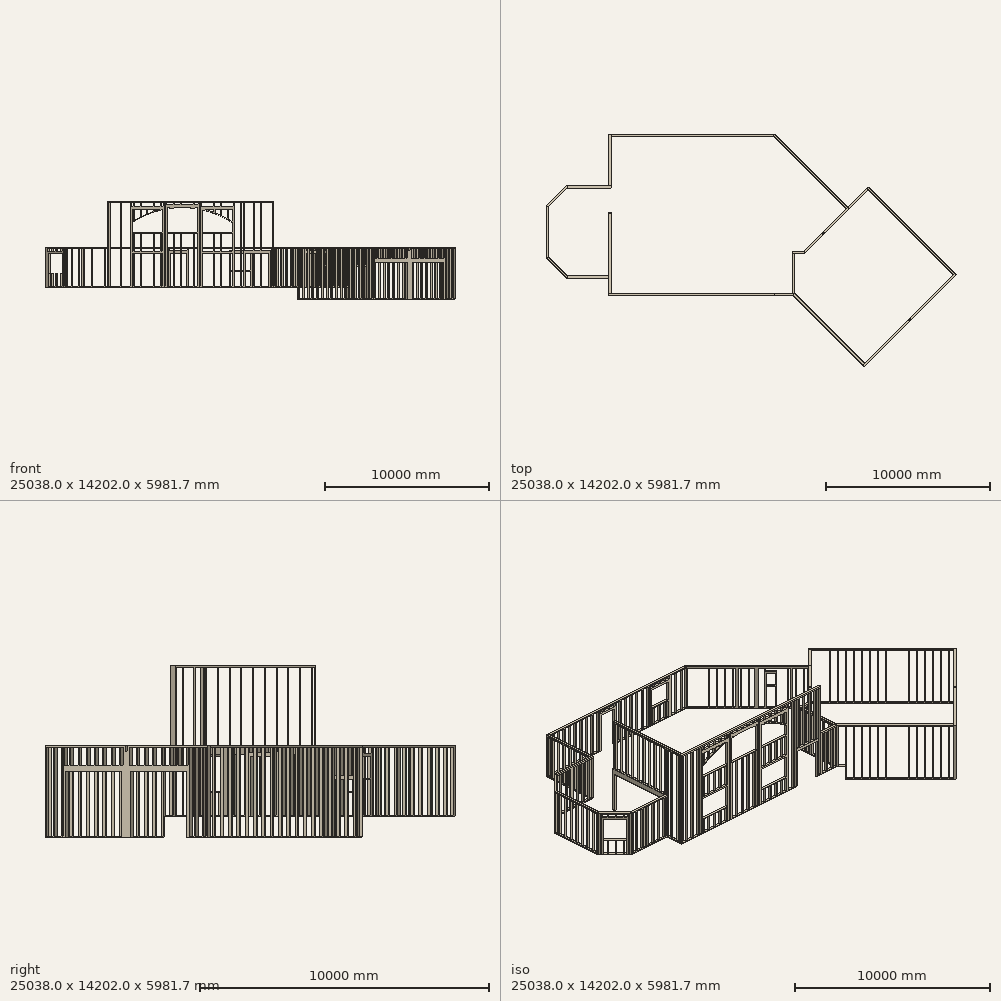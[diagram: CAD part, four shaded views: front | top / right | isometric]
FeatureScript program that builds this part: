
annotation { "Feature Type Name" : "Feature", "Feature Type Description" : "" }
export const myFeature = defineFeature(function(context is Context, id is Id, definition is map)
    precondition{}
    {
        {
            var Q0;
            Q0=qCreatedBy(makeId("Top.planeOp"),FACE);
            var sketch = newSketch(context, id + "F0", { "sketchPlane" : qUnion([Q0]) });
            skLineSegment(sketch, "E0", {"start": v(-0.03, 0) * mm, "end": v(-11277.6, 0) * mm});
            skLineSegment(sketch, "E1", {"start": v(-11277.6, 0) * mm, "end": v(-11277.6, 139.7) * mm});
            skLineSegment(sketch, "E2", {"start": v(-11277.63, 1066.8) * mm, "end": v(-13810.5, 1066.8) * mm});
            skLineSegment(sketch, "E3", {"start": v(-13868.4, 1066.8) * mm, "end": v(-15087.6, 2286) * mm});
            skLineSegment(sketch, "E4", {"start": v(-15087.6, 2286) * mm, "end": v(-15087.6, 2343.87) * mm});
            skLineSegment(sketch, "E5", {"start": v(-15087.6, 5486.4) * mm, "end": v(-13868.4, 6705.6) * mm});
            skLineSegment(sketch, "E6", {"start": v(-13868.4, 6705.6) * mm, "end": v(-13810.53, 6705.6) * mm});
            skLineSegment(sketch, "E7", {"start": v(-11277.6, 6705.63) * mm, "end": v(-11277.6, 9855.2) * mm});
            skLineSegment(sketch, "E8", {"start": v(-11277.6, 9855.2) * mm, "end": v(-11137.9, 9855.2) * mm});
            skLineSegment(sketch, "E9", {"start": v(-1162.31, 9855.2) * mm, "end": v(3305.03, 5387.86) * mm});
            skLineSegment(sketch, "E10", {"start": v(3305.06, 5387.86) * mm, "end": v(4463.48, 6546.28) * mm});
            skLineSegment(sketch, "E11", {"start": v(9950.43, 1256.93) * mm, "end": v(4346.75, -4346.75) * mm});
            skLineSegment(sketch, "E12", {"start": v(4346.75, -4346.75) * mm, "end": v(4247.97, -4247.97) * mm});
            skLineSegment(sketch, "E13.0", {"start": v(-11137.9, 6565.9) * mm, "end": v(-11137.9, 6705.6) * mm});
            skLineSegment(sketch, "E13.1", {"start": v(-13810.5, 6565.9) * mm, "end": v(-11137.9, 6565.9) * mm});
            skLineSegment(sketch, "E13.2", {"start": v(-14947.9, 5428.53) * mm, "end": v(-13810.53, 6565.9) * mm});
            skLineSegment(sketch, "E13.3", {"start": v(9752.87, 1256.93) * mm, "end": v(4346.75, -4149.19) * mm});
            skLineSegment(sketch, "E13.4", {"start": v(4463.5, 6546.3) * mm, "end": v(9752.85, 1256.94) * mm});
            skLineSegment(sketch, "E13.5", {"start": v(3305.04, 5190.28) * mm, "end": v(3403.83, 5289.06) * mm});
            skLineSegment(sketch, "E13.6", {"start": v(-1220.18, 9715.5) * mm, "end": v(3206.24, 5289.08) * mm});
            skLineSegment(sketch, "E13.7", {"start": v(4346.74, -4149.17) * mm, "end": v(57.87, 139.7) * mm});
            skLineSegment(sketch, "E13.8", {"start": v(-81.83, 139.7) * mm, "end": v(-11137.9, 139.7) * mm});
            skLineSegment(sketch, "E13.9", {"start": v(-11137.9, 139.73) * mm, "end": v(-11137.9, 5080) * mm});
            skLineSegment(sketch, "E13.10", {"start": v(-11137.87, 9715.5) * mm, "end": v(-1220.2, 9715.5) * mm});
            skLineSegment(sketch, "E13.12", {"start": v(-13810.53, 1206.5) * mm, "end": v(-14947.9, 2343.87) * mm});
            skLineSegment(sketch, "E13.13", {"start": v(-14947.9, 2343.9) * mm, "end": v(-14947.9, 5428.5) * mm});
            skLineSegment(sketch, "E14", {"start": v(57.87, 139.73) * mm, "end": v(57.87, 2578.07) * mm});
            skLineSegment(sketch, "E15", {"start": v(57.87, 2578.1) * mm, "end": v(692.87, 2578.1) * mm});
            skLineSegment(sketch, "E16", {"start": v(692.87, 2578.1) * mm, "end": v(733.78, 2619.02) * mm});
            skLineSegment(sketch, "E17.0", {"start": v(635.02, 2717.82) * mm, "end": v(3206.26, 5289.06) * mm});
            skLineSegment(sketch, "E17.1", {"start": v(-81.83, 2717.8) * mm, "end": v(635, 2717.8) * mm});
            skLineSegment(sketch, "E17.2", {"start": v(-81.83, 139.73) * mm, "end": v(-81.83, 2578.07) * mm});
            skLineSegment(sketch, "E18", {"start": v(-11137.9, 139.7) * mm, "end": v(-11277.6, 139.7) * mm});
            skLineSegment(sketch, "E19", {"start": v(-11137.9, 139.73) * mm, "end": v(-11277.6, 139.73) * mm});
            skLineSegment(sketch, "E20.trimOffspring", {"start": v(-11277.6, 139.73) * mm, "end": v(-11277.6, 5080) * mm});
            skLineSegment(sketch, "E21", {"start": v(-13810.53, 1206.5) * mm, "end": v(-13810.53, 1066.8) * mm});
            skLineSegment(sketch, "E22", {"start": v(-13810.5, 1206.5) * mm, "end": v(-13810.5, 1066.8) * mm});
            skLineSegment(sketch, "E23.trimOffspring", {"start": v(-13810.53, 1066.8) * mm, "end": v(-13868.4, 1066.8) * mm});
            skLineSegment(sketch, "E24", {"start": v(-14947.9, 2343.87) * mm, "end": v(-15087.6, 2343.87) * mm});
            skLineSegment(sketch, "E25", {"start": v(-15087.6, 2343.9) * mm, "end": v(-14947.9, 2343.9) * mm});
            skLineSegment(sketch, "E26.trimOffspring", {"start": v(-15087.6, 2343.9) * mm, "end": v(-15087.6, 5428.5) * mm});
            skLineSegment(sketch, "E27", {"start": v(-14947.9, 5428.53) * mm, "end": v(-15087.6, 5428.53) * mm});
            skLineSegment(sketch, "E28", {"start": v(-14947.9, 5428.5) * mm, "end": v(-15087.6, 5428.5) * mm});
            skLineSegment(sketch, "E29.trimOffspring", {"start": v(-15087.6, 5428.53) * mm, "end": v(-15087.6, 5486.4) * mm});
            skLineSegment(sketch, "E30", {"start": v(-13810.53, 6565.9) * mm, "end": v(-13810.53, 6705.6) * mm});
            skLineSegment(sketch, "E31", {"start": v(-13810.5, 6705.6) * mm, "end": v(-13810.5, 6565.9) * mm});
            skLineSegment(sketch, "E32.trimOffspring", {"start": v(-13810.5, 6705.6) * mm, "end": v(-11277.6, 6705.6) * mm});
            skLineSegment(sketch, "E33", {"start": v(-11277.6, 6705.6) * mm, "end": v(-11137.9, 6705.6) * mm});
            skLineSegment(sketch, "E34", {"start": v(-11277.6, 6705.63) * mm, "end": v(-11137.9, 6705.63) * mm});
            skLineSegment(sketch, "E35.trimOffspring", {"start": v(-11137.9, 6705.63) * mm, "end": v(-11137.9, 9715.5) * mm});
            skLineSegment(sketch, "E36", {"start": v(-11137.9, 9715.5) * mm, "end": v(-11137.9, 9855.2) * mm});
            skLineSegment(sketch, "E37", {"start": v(-11137.87, 9855.2) * mm, "end": v(-11137.87, 9715.5) * mm});
            skLineSegment(sketch, "E38.trimOffspring", {"start": v(-11137.87, 9855.2) * mm, "end": v(-1220.2, 9855.2) * mm});
            skLineSegment(sketch, "E39", {"start": v(-1220.18, 9715.5) * mm, "end": v(-1220.18, 9855.2) * mm});
            skLineSegment(sketch, "E40", {"start": v(-1220.2, 9855.2) * mm, "end": v(-1220.2, 9715.5) * mm});
            skLineSegment(sketch, "E41.trimOffspring", {"start": v(-1220.18, 9855.2) * mm, "end": v(-1162.31, 9855.2) * mm});
            skLineSegment(sketch, "E42", {"start": v(3206.26, 5289.06) * mm, "end": v(3305.04, 5387.84) * mm});
            skLineSegment(sketch, "E43", {"start": v(3305.04, 5387.84) * mm, "end": v(3403.83, 5289.06) * mm});
            skLineSegment(sketch, "E44", {"start": v(3206.24, 5289.08) * mm, "end": v(3305.03, 5387.86) * mm});
            skLineSegment(sketch, "E45", {"start": v(3305.06, 5387.86) * mm, "end": v(3403.84, 5289.08) * mm});
            skLineSegment(sketch, "E46.trimOffspring", {"start": v(3403.84, 5289.08) * mm, "end": v(4562.26, 6447.5) * mm});
            skLineSegment(sketch, "E47", {"start": v(635, 2717.8) * mm, "end": v(733.78, 2619.02) * mm});
            skLineSegment(sketch, "E48", {"start": v(635.02, 2717.82) * mm, "end": v(733.8, 2619.04) * mm});
            skLineSegment(sketch, "E49.trimOffspring", {"start": v(733.8, 2619.04) * mm, "end": v(3305.04, 5190.28) * mm});
            skLineSegment(sketch, "E50", {"start": v(57.87, 2578.1) * mm, "end": v(-81.83, 2578.1) * mm});
            skLineSegment(sketch, "E51", {"start": v(-81.83, 2578.07) * mm, "end": v(57.87, 2578.07) * mm});
            skLineSegment(sketch, "E52.trimOffspring", {"start": v(-81.83, 2578.1) * mm, "end": v(-81.83, 2717.8) * mm});
            skLineSegment(sketch, "E53", {"start": v(-81.83, 139.7) * mm, "end": v(-0.03, 139.7) * mm});
            skLineSegment(sketch, "E54", {"start": v(-81.83, 139.73) * mm, "end": v(57.87, 139.73) * mm});
            skLineSegment(sketch, "E55", {"start": v(0, 0) * mm, "end": v(0, 139.7) * mm});
            skLineSegment(sketch, "E56", {"start": v(-0.03, 0) * mm, "end": v(-0.03, 139.7) * mm});
            skLineSegment(sketch, "E57.trimOffspring", {"start": v(0, 139.7) * mm, "end": v(57.87, 139.7) * mm});
            skLineSegment(sketch, "E58", {"start": v(4346.75, -4149.19) * mm, "end": v(4247.97, -4247.97) * mm});
            skLineSegment(sketch, "E59", {"start": v(4346.74, -4149.17) * mm, "end": v(4247.95, -4247.95) * mm});
            skLineSegment(sketch, "E60.trimOffspring", {"start": v(4247.95, -4247.95) * mm, "end": v(0, 0) * mm});
            skLineSegment(sketch, "E61", {"start": v(9752.87, 1256.93) * mm, "end": v(9851.65, 1355.7) * mm});
            skLineSegment(sketch, "E62", {"start": v(9752.85, 1256.94) * mm, "end": v(9851.63, 1355.73) * mm});
            skLineSegment(sketch, "E63.trimOffspring", {"start": v(9851.65, 1355.7) * mm, "end": v(9950.43, 1256.93) * mm});
            skLineSegment(sketch, "E64.trimOffspring", {"start": v(4562.28, 6645.08) * mm, "end": v(9851.63, 1355.73) * mm});
            skLineSegment(sketch, "E65", {"start": v(4562.26, 6447.5) * mm, "end": v(4463.48, 6546.28) * mm});
            skLineSegment(sketch, "E66.trimOffspring", {"start": v(4463.5, 6546.3) * mm, "end": v(4562.28, 6645.08) * mm});
            skLineSegment(sketch, "E67", {"start": v(-12712.7, 6565.9) * mm, "end": v(-12712.7, 5080) * mm, "construction": true});
            skLineSegment(sketch, "E68", {"start": v(-12712.7, 5080) * mm, "end": v(-11277.6, 5080) * mm, "construction": true});
            skLineSegment(sketch, "E69", {"start": v(-12801.6, 6565.9) * mm, "end": v(-12801.6, 4991.1) * mm, "construction": true});
            skLineSegment(sketch, "E70", {"start": v(-12801.6, 4991.1) * mm, "end": v(-11277.6, 4991.1) * mm, "construction": true});
            skLineSegment(sketch, "E71", {"start": v(-11277.63, 1206.5) * mm, "end": v(-11277.63, 1066.8) * mm});
            skLineSegment(sketch, "E72.trimOffspring", {"start": v(-11277.63, 1206.5) * mm, "end": v(-13810.5, 1206.5) * mm});
            skLineSegment(sketch, "E73", {"start": v(-11137.9, 5080) * mm, "end": v(-10632.52, 5080) * mm, "construction": true});
            skLineSegment(sketch, "E74", {"start": v(-11137.9, 5000.63) * mm, "end": v(-10601.72, 5000.63) * mm, "construction": true});
            skLineSegment(sketch, "E75", {"start": v(-11277.6, 5080) * mm, "end": v(-11137.9, 5080) * mm});
            skSolve(sketch);
        }
        {
            var Q0;
            Q0 = qSketchRegion(id + "F0", true);
            extrude(context, id + "F1", {"entities" : qUnion([Q0]), "depth" : 38.1 * mm});
        }
        {
            var Q0;
            Q0=makeQuery(id+"F1.opExtrude","CAP_FACE",FACE,{"disambiguationData":[OSD([sQuery(id+"F0.wireOp",EDGE,"E0"),sQuery(id+"F0.wireOp",EDGE,"E1"),sQuery(id+"F0.wireOp",EDGE,"E13.8"),sQuery(id+"F0.wireOp",EDGE,"E18"),sQuery(id+"F0.wireOp",EDGE,"E53"),sQuery(id+"F0.wireOp",EDGE,"E56")])],"isStart":false});
            var sketch = newSketch(context, id + "F2", { "sketchPlane" : qUnion([Q0]) });
            skLineSegment(sketch, "E76.bottom", {"start": v(-11277.6, 0) * mm, "end": v(-11239.5, 0) * mm});
            skLineSegment(sketch, "E76.top", {"start": v(-11277.6, 139.7) * mm, "end": v(-11239.5, 139.7) * mm});
            skLineSegment(sketch, "E76.left", {"start": v(-11277.6, 0) * mm, "end": v(-11277.6, 139.7) * mm});
            skLineSegment(sketch, "E76.right", {"start": v(-11239.5, 0) * mm, "end": v(-11239.5, 139.7) * mm});
            skLineSegment(sketch, "E77.bottom", {"start": v(-11099.8, 139.7) * mm, "end": v(-11239.47, 139.7) * mm});
            skLineSegment(sketch, "E77.top", {"start": v(-11099.8, 101.6) * mm, "end": v(-11239.47, 101.6) * mm});
            skLineSegment(sketch, "E77.left", {"start": v(-11099.8, 139.7) * mm, "end": v(-11099.8, 101.6) * mm});
            skLineSegment(sketch, "E77.right", {"start": v(-11239.47, 139.7) * mm, "end": v(-11239.47, 101.6) * mm});
            skLineSegment(sketch, "E78.bottom", {"start": v(-0.03, 0) * mm, "end": v(-38.1, 0) * mm});
            skLineSegment(sketch, "E78.top", {"start": v(-0.03, 139.7) * mm, "end": v(-38.1, 139.7) * mm});
            skLineSegment(sketch, "E78.left", {"start": v(-0.03, 0) * mm, "end": v(-0.03, 139.7) * mm});
            skLineSegment(sketch, "E78.right", {"start": v(-38.1, 0) * mm, "end": v(-38.1, 139.7) * mm});
            skLineSegment(sketch, "E79.bottom", {"start": v(-127, 139.7) * mm, "end": v(-38.13, 139.7) * mm});
            skLineSegment(sketch, "E79.top", {"start": v(-127, 101.6) * mm, "end": v(-38.13, 101.6) * mm});
            skLineSegment(sketch, "E79.left", {"start": v(-127, 139.7) * mm, "end": v(-127, 101.6) * mm});
            skLineSegment(sketch, "E79.right", {"start": v(-38.13, 139.7) * mm, "end": v(-38.13, 101.6) * mm});
            skLineSegment(sketch, "E80.bottom", {"start": v(-10902.95, 139.7) * mm, "end": v(-10864.85, 139.7) * mm});
            skLineSegment(sketch, "E80.top", {"start": v(-10902.95, 0) * mm, "end": v(-10864.85, 0) * mm});
            skLineSegment(sketch, "E80.left", {"start": v(-10902.95, 139.7) * mm, "end": v(-10902.95, 0) * mm});
            skLineSegment(sketch, "E80.right", {"start": v(-10864.85, 139.7) * mm, "end": v(-10864.85, 0) * mm});
            skLineSegment(sketch, "E81.1.0.0", {"start": v(-10496.55, 139.7) * mm, "end": v(-10496.55, 0) * mm});
            skLineSegment(sketch, "E81.1.0.1", {"start": v(-10458.45, 139.7) * mm, "end": v(-10458.45, 0) * mm});
            skLineSegment(sketch, "E81.1.0.2", {"start": v(-10496.55, 139.7) * mm, "end": v(-10458.45, 139.7) * mm});
            skLineSegment(sketch, "E81.1.0.3", {"start": v(-10496.55, 0) * mm, "end": v(-10458.45, 0) * mm});
            skLineSegment(sketch, "E81.2.0.0", {"start": v(-10090.15, 139.7) * mm, "end": v(-10090.15, 0) * mm});
            skLineSegment(sketch, "E81.2.0.1", {"start": v(-10052.05, 139.7) * mm, "end": v(-10052.05, 0) * mm});
            skLineSegment(sketch, "E81.2.0.2", {"start": v(-10090.15, 139.7) * mm, "end": v(-10052.05, 139.7) * mm});
            skLineSegment(sketch, "E81.2.0.3", {"start": v(-10090.15, 0) * mm, "end": v(-10052.05, 0) * mm});
            skLineSegment(sketch, "E81.3.0.0", {"start": v(-9683.75, 139.7) * mm, "end": v(-9683.75, 0) * mm});
            skLineSegment(sketch, "E81.3.0.1", {"start": v(-9645.65, 139.7) * mm, "end": v(-9645.65, 0) * mm});
            skLineSegment(sketch, "E81.3.0.2", {"start": v(-9683.75, 139.7) * mm, "end": v(-9645.65, 139.7) * mm});
            skLineSegment(sketch, "E81.3.0.3", {"start": v(-9683.75, 0) * mm, "end": v(-9645.65, 0) * mm});
            skLineSegment(sketch, "E81.4.0.0", {"start": v(-9277.35, 139.7) * mm, "end": v(-9277.35, 0) * mm});
            skLineSegment(sketch, "E81.4.0.1", {"start": v(-9239.25, 139.7) * mm, "end": v(-9239.25, 0) * mm});
            skLineSegment(sketch, "E81.4.0.2", {"start": v(-9277.35, 139.7) * mm, "end": v(-9239.25, 139.7) * mm});
            skLineSegment(sketch, "E81.4.0.3", {"start": v(-9277.35, 0) * mm, "end": v(-9239.25, 0) * mm});
            skLineSegment(sketch, "E81.5.0.0", {"start": v(-8870.95, 139.7) * mm, "end": v(-8870.95, 0) * mm});
            skLineSegment(sketch, "E81.5.0.1", {"start": v(-8832.85, 139.7) * mm, "end": v(-8832.85, 0) * mm});
            skLineSegment(sketch, "E81.5.0.2", {"start": v(-8870.95, 139.7) * mm, "end": v(-8832.85, 139.7) * mm});
            skLineSegment(sketch, "E81.5.0.3", {"start": v(-8870.95, 0) * mm, "end": v(-8832.85, 0) * mm});
            skLineSegment(sketch, "E81.6.0.0", {"start": v(-8464.55, 139.7) * mm, "end": v(-8464.55, 0) * mm});
            skLineSegment(sketch, "E81.6.0.1", {"start": v(-8426.45, 139.7) * mm, "end": v(-8426.45, 0) * mm});
            skLineSegment(sketch, "E81.6.0.2", {"start": v(-8464.55, 139.7) * mm, "end": v(-8426.45, 139.7) * mm});
            skLineSegment(sketch, "E81.6.0.3", {"start": v(-8464.55, 0) * mm, "end": v(-8426.45, 0) * mm});
            skLineSegment(sketch, "E81.7.0.0", {"start": v(-8058.15, 139.7) * mm, "end": v(-8058.15, 0) * mm});
            skLineSegment(sketch, "E81.7.0.1", {"start": v(-8020.05, 139.7) * mm, "end": v(-8020.05, 0) * mm});
            skLineSegment(sketch, "E81.7.0.2", {"start": v(-8058.15, 139.7) * mm, "end": v(-8020.05, 139.7) * mm});
            skLineSegment(sketch, "E81.7.0.3", {"start": v(-8058.15, 0) * mm, "end": v(-8020.05, 0) * mm});
            skLineSegment(sketch, "E81.8.0.0", {"start": v(-7651.75, 139.7) * mm, "end": v(-7651.75, 0) * mm});
            skLineSegment(sketch, "E81.8.0.1", {"start": v(-7613.65, 139.7) * mm, "end": v(-7613.65, 0) * mm});
            skLineSegment(sketch, "E81.8.0.2", {"start": v(-7651.75, 139.7) * mm, "end": v(-7613.65, 139.7) * mm});
            skLineSegment(sketch, "E81.8.0.3", {"start": v(-7651.75, 0) * mm, "end": v(-7613.65, 0) * mm});
            skLineSegment(sketch, "E81.9.0.0", {"start": v(-7245.35, 139.7) * mm, "end": v(-7245.35, 0) * mm});
            skLineSegment(sketch, "E81.9.0.1", {"start": v(-7207.25, 139.7) * mm, "end": v(-7207.25, 0) * mm});
            skLineSegment(sketch, "E81.9.0.2", {"start": v(-7245.35, 139.7) * mm, "end": v(-7207.25, 139.7) * mm});
            skLineSegment(sketch, "E81.9.0.3", {"start": v(-7245.35, 0) * mm, "end": v(-7207.25, 0) * mm});
            skLineSegment(sketch, "E81.10.0.0", {"start": v(-6838.95, 139.7) * mm, "end": v(-6838.95, 0) * mm});
            skLineSegment(sketch, "E81.10.0.1", {"start": v(-6800.85, 139.7) * mm, "end": v(-6800.85, 0) * mm});
            skLineSegment(sketch, "E81.10.0.2", {"start": v(-6838.95, 139.7) * mm, "end": v(-6800.85, 139.7) * mm});
            skLineSegment(sketch, "E81.10.0.3", {"start": v(-6838.95, 0) * mm, "end": v(-6800.85, 0) * mm});
            skLineSegment(sketch, "E81.11.0.0", {"start": v(-6432.55, 139.7) * mm, "end": v(-6432.55, 0) * mm});
            skLineSegment(sketch, "E81.11.0.1", {"start": v(-6394.45, 139.7) * mm, "end": v(-6394.45, 0) * mm});
            skLineSegment(sketch, "E81.11.0.2", {"start": v(-6432.55, 139.7) * mm, "end": v(-6394.45, 139.7) * mm});
            skLineSegment(sketch, "E81.11.0.3", {"start": v(-6432.55, 0) * mm, "end": v(-6394.45, 0) * mm});
            skLineSegment(sketch, "E81.12.0.0", {"start": v(-6026.15, 139.7) * mm, "end": v(-6026.15, 0) * mm});
            skLineSegment(sketch, "E81.12.0.1", {"start": v(-5988.05, 139.7) * mm, "end": v(-5988.05, 0) * mm});
            skLineSegment(sketch, "E81.12.0.2", {"start": v(-6026.15, 139.7) * mm, "end": v(-5988.05, 139.7) * mm});
            skLineSegment(sketch, "E81.12.0.3", {"start": v(-6026.15, 0) * mm, "end": v(-5988.05, 0) * mm});
            skLineSegment(sketch, "E81.13.0.0", {"start": v(-5619.75, 139.7) * mm, "end": v(-5619.75, 0) * mm});
            skLineSegment(sketch, "E81.13.0.1", {"start": v(-5581.65, 139.7) * mm, "end": v(-5581.65, 0) * mm});
            skLineSegment(sketch, "E81.13.0.2", {"start": v(-5619.75, 139.7) * mm, "end": v(-5581.65, 139.7) * mm});
            skLineSegment(sketch, "E81.13.0.3", {"start": v(-5619.75, 0) * mm, "end": v(-5581.65, 0) * mm});
            skLineSegment(sketch, "E81.14.0.0", {"start": v(-5213.35, 139.7) * mm, "end": v(-5213.35, 0) * mm});
            skLineSegment(sketch, "E81.14.0.1", {"start": v(-5175.25, 139.7) * mm, "end": v(-5175.25, 0) * mm});
            skLineSegment(sketch, "E81.14.0.2", {"start": v(-5213.35, 139.7) * mm, "end": v(-5175.25, 139.7) * mm});
            skLineSegment(sketch, "E81.14.0.3", {"start": v(-5213.35, 0) * mm, "end": v(-5175.25, 0) * mm});
            skLineSegment(sketch, "E81.15.0.0", {"start": v(-4806.95, 139.7) * mm, "end": v(-4806.95, 0) * mm});
            skLineSegment(sketch, "E81.15.0.1", {"start": v(-4768.85, 139.7) * mm, "end": v(-4768.85, 0) * mm});
            skLineSegment(sketch, "E81.15.0.2", {"start": v(-4806.95, 139.7) * mm, "end": v(-4768.85, 139.7) * mm});
            skLineSegment(sketch, "E81.15.0.3", {"start": v(-4806.95, 0) * mm, "end": v(-4768.85, 0) * mm});
            skLineSegment(sketch, "E81.16.0.0", {"start": v(-4400.55, 139.7) * mm, "end": v(-4400.55, 0) * mm});
            skLineSegment(sketch, "E81.16.0.1", {"start": v(-4362.45, 139.7) * mm, "end": v(-4362.45, 0) * mm});
            skLineSegment(sketch, "E81.16.0.2", {"start": v(-4400.55, 139.7) * mm, "end": v(-4362.45, 139.7) * mm});
            skLineSegment(sketch, "E81.16.0.3", {"start": v(-4400.55, 0) * mm, "end": v(-4362.45, 0) * mm});
            skLineSegment(sketch, "E81.17.0.0", {"start": v(-3994.15, 139.7) * mm, "end": v(-3994.15, 0) * mm});
            skLineSegment(sketch, "E81.17.0.1", {"start": v(-3956.05, 139.7) * mm, "end": v(-3956.05, 0) * mm});
            skLineSegment(sketch, "E81.17.0.2", {"start": v(-3994.15, 139.7) * mm, "end": v(-3956.05, 139.7) * mm});
            skLineSegment(sketch, "E81.17.0.3", {"start": v(-3994.15, 0) * mm, "end": v(-3956.05, 0) * mm});
            skLineSegment(sketch, "E81.18.0.0", {"start": v(-3587.75, 139.7) * mm, "end": v(-3587.75, 0) * mm});
            skLineSegment(sketch, "E81.18.0.1", {"start": v(-3549.65, 139.7) * mm, "end": v(-3549.65, 0) * mm});
            skLineSegment(sketch, "E81.18.0.2", {"start": v(-3587.75, 139.7) * mm, "end": v(-3549.65, 139.7) * mm});
            skLineSegment(sketch, "E81.18.0.3", {"start": v(-3587.75, 0) * mm, "end": v(-3549.65, 0) * mm});
            skLineSegment(sketch, "E81.19.0.0", {"start": v(-3181.35, 139.7) * mm, "end": v(-3181.35, 0) * mm});
            skLineSegment(sketch, "E81.19.0.1", {"start": v(-3143.25, 139.7) * mm, "end": v(-3143.25, 0) * mm});
            skLineSegment(sketch, "E81.19.0.2", {"start": v(-3181.35, 139.7) * mm, "end": v(-3143.25, 139.7) * mm});
            skLineSegment(sketch, "E81.19.0.3", {"start": v(-3181.35, 0) * mm, "end": v(-3143.25, 0) * mm});
            skLineSegment(sketch, "E81.20.0.0", {"start": v(-2774.95, 139.7) * mm, "end": v(-2774.95, 0) * mm});
            skLineSegment(sketch, "E81.20.0.1", {"start": v(-2736.85, 139.7) * mm, "end": v(-2736.85, 0) * mm});
            skLineSegment(sketch, "E81.20.0.2", {"start": v(-2774.95, 139.7) * mm, "end": v(-2736.85, 139.7) * mm});
            skLineSegment(sketch, "E81.20.0.3", {"start": v(-2774.95, 0) * mm, "end": v(-2736.85, 0) * mm});
            skLineSegment(sketch, "E81.21.0.0", {"start": v(-2368.55, 139.7) * mm, "end": v(-2368.55, 0) * mm});
            skLineSegment(sketch, "E81.21.0.1", {"start": v(-2330.45, 139.7) * mm, "end": v(-2330.45, 0) * mm});
            skLineSegment(sketch, "E81.21.0.2", {"start": v(-2368.55, 139.7) * mm, "end": v(-2330.45, 139.7) * mm});
            skLineSegment(sketch, "E81.21.0.3", {"start": v(-2368.55, 0) * mm, "end": v(-2330.45, 0) * mm});
            skLineSegment(sketch, "E81.22.0.0", {"start": v(-1962.15, 139.7) * mm, "end": v(-1962.15, 0) * mm});
            skLineSegment(sketch, "E81.22.0.1", {"start": v(-1924.05, 139.7) * mm, "end": v(-1924.05, 0) * mm});
            skLineSegment(sketch, "E81.22.0.2", {"start": v(-1962.15, 139.7) * mm, "end": v(-1924.05, 139.7) * mm});
            skLineSegment(sketch, "E81.22.0.3", {"start": v(-1962.15, 0) * mm, "end": v(-1924.05, 0) * mm});
            skLineSegment(sketch, "E81.23.0.0", {"start": v(-1555.75, 139.7) * mm, "end": v(-1555.75, 0) * mm});
            skLineSegment(sketch, "E81.23.0.1", {"start": v(-1517.65, 139.7) * mm, "end": v(-1517.65, 0) * mm});
            skLineSegment(sketch, "E81.23.0.2", {"start": v(-1555.75, 139.7) * mm, "end": v(-1517.65, 139.7) * mm});
            skLineSegment(sketch, "E81.23.0.3", {"start": v(-1555.75, 0) * mm, "end": v(-1517.65, 0) * mm});
            skLineSegment(sketch, "E81.25.0.0", {"start": v(-742.95, 139.7) * mm, "end": v(-742.95, 0) * mm});
            skLineSegment(sketch, "E81.25.0.1", {"start": v(-704.85, 139.7) * mm, "end": v(-704.85, 0) * mm});
            skLineSegment(sketch, "E81.25.0.2", {"start": v(-742.95, 139.7) * mm, "end": v(-704.85, 139.7) * mm});
            skLineSegment(sketch, "E81.25.0.3", {"start": v(-742.95, 0) * mm, "end": v(-704.85, 0) * mm});
            skLineSegment(sketch, "E81.26.0.0", {"start": v(-336.55, 139.7) * mm, "end": v(-336.55, 0) * mm});
            skLineSegment(sketch, "E81.26.0.1", {"start": v(-298.45, 139.7) * mm, "end": v(-298.45, 0) * mm});
            skLineSegment(sketch, "E81.26.0.2", {"start": v(-336.55, 139.7) * mm, "end": v(-298.45, 139.7) * mm});
            skLineSegment(sketch, "E81.26.0.3", {"start": v(-336.55, 0) * mm, "end": v(-298.45, 0) * mm});
            skLineSegment(sketch, "E81.direction1", {"start": v(-10902.95, 0) * mm, "end": v(-10496.55, 0) * mm, "construction": true});
            skLineSegment(sketch, "E82", {"start": v(-1085.13, 1434.54) * mm, "end": v(-1085.13, 139.7) * mm, "construction": true});
            skLineSegment(sketch, "E83", {"start": v(-1174.03, 1434.54) * mm, "end": v(-1174.03, 139.7) * mm, "construction": true});
            skLineSegment(sketch, "E84.bottom", {"start": v(-1174.03, 139.7) * mm, "end": v(-1135.93, 139.7) * mm});
            skLineSegment(sketch, "E84.top", {"start": v(-1174.03, 0) * mm, "end": v(-1135.93, 0) * mm});
            skLineSegment(sketch, "E84.left", {"start": v(-1174.03, 139.7) * mm, "end": v(-1174.03, 0) * mm});
            skLineSegment(sketch, "E84.right", {"start": v(-1135.93, 139.7) * mm, "end": v(-1135.93, 0) * mm});
            skLineSegment(sketch, "E85.bottom", {"start": v(-1094.66, 139.7) * mm, "end": v(-1132.76, 139.7) * mm});
            skLineSegment(sketch, "E85.top", {"start": v(-1094.66, 0) * mm, "end": v(-1132.76, 0) * mm});
            skLineSegment(sketch, "E85.left", {"start": v(-1094.66, 139.7) * mm, "end": v(-1094.66, 0) * mm});
            skLineSegment(sketch, "E85.right", {"start": v(-1132.76, 139.7) * mm, "end": v(-1132.76, 0) * mm});
            skLineSegment(sketch, "E86.bottom", {"start": v(-1174.06, 139.7) * mm, "end": v(-1212.13, 139.7) * mm});
            skLineSegment(sketch, "E86.top", {"start": v(-1174.06, 0) * mm, "end": v(-1212.13, 0) * mm});
            skLineSegment(sketch, "E86.left", {"start": v(-1174.06, 139.7) * mm, "end": v(-1174.06, 0) * mm});
            skLineSegment(sketch, "E86.right", {"start": v(-1212.13, 139.7) * mm, "end": v(-1212.13, 0) * mm});
            skLineSegment(sketch, "E87.bottom", {"start": v(-1094.63, 139.7) * mm, "end": v(-1056.56, 139.7) * mm});
            skLineSegment(sketch, "E87.top", {"start": v(-1094.63, 0) * mm, "end": v(-1056.56, 0) * mm});
            skLineSegment(sketch, "E87.left", {"start": v(-1094.63, 139.7) * mm, "end": v(-1094.63, 0) * mm});
            skLineSegment(sketch, "E87.right", {"start": v(-1056.56, 139.7) * mm, "end": v(-1056.56, 0) * mm});
            skLineSegment(sketch, "E88.bottom", {"start": v(-1453.43, 139.7) * mm, "end": v(-1415.33, 139.7) * mm});
            skLineSegment(sketch, "E88.top", {"start": v(-1453.43, 0) * mm, "end": v(-1415.33, 0) * mm});
            skLineSegment(sketch, "E88.left", {"start": v(-1453.43, 139.7) * mm, "end": v(-1453.43, 0) * mm});
            skLineSegment(sketch, "E88.right", {"start": v(-1415.33, 139.7) * mm, "end": v(-1415.33, 0) * mm});
            skLineSegment(sketch, "E89.bottom", {"start": v(-2898.06, 139.7) * mm, "end": v(-2859.96, 139.7) * mm});
            skLineSegment(sketch, "E89.top", {"start": v(-2898.06, 0) * mm, "end": v(-2859.96, 0) * mm});
            skLineSegment(sketch, "E89.left", {"start": v(-2898.06, 139.7) * mm, "end": v(-2898.06, 0) * mm});
            skLineSegment(sketch, "E89.right", {"start": v(-2859.96, 139.7) * mm, "end": v(-2859.96, 0) * mm});
            skLineSegment(sketch, "E90.bottom", {"start": v(-2936.16, 139.7) * mm, "end": v(-2898.08, 139.7) * mm});
            skLineSegment(sketch, "E90.top", {"start": v(-2936.16, 0) * mm, "end": v(-2898.08, 0) * mm});
            skLineSegment(sketch, "E90.left", {"start": v(-2936.16, 139.7) * mm, "end": v(-2936.16, 0) * mm});
            skLineSegment(sketch, "E90.right", {"start": v(-2898.08, 139.7) * mm, "end": v(-2898.08, 0) * mm});
            skLineSegment(sketch, "E91.bottom", {"start": v(-1415.3, 139.7) * mm, "end": v(-1377.23, 139.7) * mm});
            skLineSegment(sketch, "E91.top", {"start": v(-1415.3, 0) * mm, "end": v(-1377.23, 0) * mm});
            skLineSegment(sketch, "E91.left", {"start": v(-1415.3, 139.7) * mm, "end": v(-1415.3, 0) * mm});
            skLineSegment(sketch, "E91.right", {"start": v(-1377.23, 139.7) * mm, "end": v(-1377.23, 0) * mm});
            skLineSegment(sketch, "E92.bottom", {"start": v(-1377.2, 139.7) * mm, "end": v(-1339.13, 139.7) * mm});
            skLineSegment(sketch, "E92.top", {"start": v(-1377.2, 0) * mm, "end": v(-1339.13, 0) * mm});
            skLineSegment(sketch, "E92.left", {"start": v(-1377.2, 139.7) * mm, "end": v(-1377.2, 0) * mm});
            skLineSegment(sketch, "E92.right", {"start": v(-1339.13, 139.7) * mm, "end": v(-1339.13, 0) * mm});
            skLineSegment(sketch, "E93.bottom", {"start": v(-2974.26, 139.7) * mm, "end": v(-2936.18, 139.7) * mm});
            skLineSegment(sketch, "E93.top", {"start": v(-2974.26, 0) * mm, "end": v(-2936.18, 0) * mm});
            skLineSegment(sketch, "E93.left", {"start": v(-2974.26, 139.7) * mm, "end": v(-2974.26, 0) * mm});
            skLineSegment(sketch, "E93.right", {"start": v(-2936.18, 139.7) * mm, "end": v(-2936.18, 0) * mm});
            skLineSegment(sketch, "E94.bottom", {"start": v(-9804.4, 139.7) * mm, "end": v(-9766.3, 139.7) * mm});
            skLineSegment(sketch, "E94.top", {"start": v(-9804.4, 0) * mm, "end": v(-9766.3, 0) * mm});
            skLineSegment(sketch, "E94.left", {"start": v(-9804.4, 139.7) * mm, "end": v(-9804.4, 0) * mm});
            skLineSegment(sketch, "E94.right", {"start": v(-9766.3, 139.7) * mm, "end": v(-9766.3, 0) * mm});
            skLineSegment(sketch, "E95.bottom", {"start": v(-9842.5, 139.7) * mm, "end": v(-9804.43, 139.7) * mm});
            skLineSegment(sketch, "E95.top", {"start": v(-9842.5, 0) * mm, "end": v(-9804.43, 0) * mm});
            skLineSegment(sketch, "E95.left", {"start": v(-9842.5, 139.7) * mm, "end": v(-9842.5, 0) * mm});
            skLineSegment(sketch, "E95.right", {"start": v(-9804.43, 139.7) * mm, "end": v(-9804.43, 0) * mm});
            skLineSegment(sketch, "E96.bottom", {"start": v(-7937.5, 139.7) * mm, "end": v(-7899.4, 139.7) * mm});
            skLineSegment(sketch, "E96.top", {"start": v(-7937.5, 0) * mm, "end": v(-7899.4, 0) * mm});
            skLineSegment(sketch, "E96.left", {"start": v(-7937.5, 139.7) * mm, "end": v(-7937.5, 0) * mm});
            skLineSegment(sketch, "E96.right", {"start": v(-7899.4, 139.7) * mm, "end": v(-7899.4, 0) * mm});
            skLineSegment(sketch, "E97.bottom", {"start": v(-7899.37, 139.7) * mm, "end": v(-7861.3, 139.7) * mm});
            skLineSegment(sketch, "E97.top", {"start": v(-7899.37, 0) * mm, "end": v(-7861.3, 0) * mm});
            skLineSegment(sketch, "E97.left", {"start": v(-7899.37, 139.7) * mm, "end": v(-7899.37, 0) * mm});
            skLineSegment(sketch, "E97.right", {"start": v(-7861.3, 139.7) * mm, "end": v(-7861.3, 0) * mm});
            skLineSegment(sketch, "E98.bottom", {"start": v(-5543.52, 139.7) * mm, "end": v(-5505.42, 139.7) * mm});
            skLineSegment(sketch, "E98.top", {"start": v(-5543.52, 0) * mm, "end": v(-5505.42, 0) * mm});
            skLineSegment(sketch, "E98.left", {"start": v(-5543.52, 139.7) * mm, "end": v(-5543.52, 0) * mm});
            skLineSegment(sketch, "E98.right", {"start": v(-5505.42, 139.7) * mm, "end": v(-5505.42, 0) * mm});
            skLineSegment(sketch, "E99.bottom", {"start": v(-5543.55, 139.7) * mm, "end": v(-5581.62, 139.7) * mm});
            skLineSegment(sketch, "E99.top", {"start": v(-5543.55, 0) * mm, "end": v(-5581.62, 0) * mm});
            skLineSegment(sketch, "E99.left", {"start": v(-5543.55, 139.7) * mm, "end": v(-5543.55, 0) * mm});
            skLineSegment(sketch, "E99.right", {"start": v(-5581.62, 139.7) * mm, "end": v(-5581.62, 0) * mm});
            skLineSegment(sketch, "E100.bottom", {"start": v(-3676.62, 139.7) * mm, "end": v(-3638.52, 139.7) * mm});
            skLineSegment(sketch, "E100.top", {"start": v(-3676.62, 0) * mm, "end": v(-3638.52, 0) * mm});
            skLineSegment(sketch, "E100.left", {"start": v(-3676.62, 139.7) * mm, "end": v(-3676.62, 0) * mm});
            skLineSegment(sketch, "E100.right", {"start": v(-3638.52, 139.7) * mm, "end": v(-3638.52, 0) * mm});
            skLineSegment(sketch, "E101.bottom", {"start": v(-3638.5, 139.7) * mm, "end": v(-3600.42, 139.7) * mm});
            skLineSegment(sketch, "E101.top", {"start": v(-3638.5, 0) * mm, "end": v(-3600.42, 0) * mm});
            skLineSegment(sketch, "E101.left", {"start": v(-3638.5, 139.7) * mm, "end": v(-3638.5, 0) * mm});
            skLineSegment(sketch, "E101.right", {"start": v(-3600.42, 139.7) * mm, "end": v(-3600.42, 0) * mm});
            skLineSegment(sketch, "E102.bottom", {"start": v(-7727.95, 139.7) * mm, "end": v(-7689.88, 139.7) * mm});
            skLineSegment(sketch, "E102.top", {"start": v(-7727.95, 0) * mm, "end": v(-7689.88, 0) * mm});
            skLineSegment(sketch, "E102.left", {"start": v(-7727.95, 139.7) * mm, "end": v(-7727.95, 0) * mm});
            skLineSegment(sketch, "E102.right", {"start": v(-7689.88, 139.7) * mm, "end": v(-7689.88, 0) * mm});
            skLineSegment(sketch, "E103.bottom", {"start": v(-7689.85, 139.7) * mm, "end": v(-7651.78, 139.7) * mm});
            skLineSegment(sketch, "E103.top", {"start": v(-7689.85, 0) * mm, "end": v(-7651.78, 0) * mm});
            skLineSegment(sketch, "E103.left", {"start": v(-7689.85, 139.7) * mm, "end": v(-7689.85, 0) * mm});
            skLineSegment(sketch, "E103.right", {"start": v(-7651.78, 139.7) * mm, "end": v(-7651.78, 0) * mm});
            skLineSegment(sketch, "E104.bottom", {"start": v(-5714.97, 139.7) * mm, "end": v(-5753.05, 139.7) * mm});
            skLineSegment(sketch, "E104.top", {"start": v(-5714.97, 0) * mm, "end": v(-5753.05, 0) * mm});
            skLineSegment(sketch, "E104.left", {"start": v(-5714.97, 139.7) * mm, "end": v(-5714.97, 0) * mm});
            skLineSegment(sketch, "E104.right", {"start": v(-5753.05, 139.7) * mm, "end": v(-5753.05, 0) * mm});
            skLineSegment(sketch, "E105.bottom", {"start": v(-5753.07, 139.7) * mm, "end": v(-5791.17, 139.7) * mm});
            skLineSegment(sketch, "E105.top", {"start": v(-5753.07, 0) * mm, "end": v(-5791.17, 0) * mm});
            skLineSegment(sketch, "E105.left", {"start": v(-5753.07, 139.7) * mm, "end": v(-5753.07, 0) * mm});
            skLineSegment(sketch, "E105.right", {"start": v(-5791.17, 139.7) * mm, "end": v(-5791.17, 0) * mm});
            skLineSegment(sketch, "E106.bottom", {"start": v(-9880.6, 139.7) * mm, "end": v(-9842.53, 139.7) * mm});
            skLineSegment(sketch, "E106.top", {"start": v(-9880.6, 0) * mm, "end": v(-9842.53, 0) * mm});
            skLineSegment(sketch, "E106.left", {"start": v(-9880.6, 139.7) * mm, "end": v(-9880.6, 0) * mm});
            skLineSegment(sketch, "E106.right", {"start": v(-9842.53, 139.7) * mm, "end": v(-9842.53, 0) * mm});
            skLineSegment(sketch, "E107.bottom", {"start": v(-7861.27, 139.7) * mm, "end": v(-7823.2, 139.7) * mm});
            skLineSegment(sketch, "E107.top", {"start": v(-7861.27, 0) * mm, "end": v(-7823.2, 0) * mm});
            skLineSegment(sketch, "E107.left", {"start": v(-7861.27, 139.7) * mm, "end": v(-7861.27, 0) * mm});
            skLineSegment(sketch, "E107.right", {"start": v(-7823.2, 139.7) * mm, "end": v(-7823.2, 0) * mm});
            skLineSegment(sketch, "E108.bottom", {"start": v(-5714.95, 139.7) * mm, "end": v(-5676.87, 139.7) * mm});
            skLineSegment(sketch, "E108.top", {"start": v(-5714.95, 0) * mm, "end": v(-5676.87, 0) * mm});
            skLineSegment(sketch, "E108.left", {"start": v(-5714.95, 139.7) * mm, "end": v(-5714.95, 0) * mm});
            skLineSegment(sketch, "E108.right", {"start": v(-5676.87, 139.7) * mm, "end": v(-5676.87, 0) * mm});
            skLineSegment(sketch, "E109.bottom", {"start": v(-7766.05, 139.7) * mm, "end": v(-7727.98, 139.7) * mm});
            skLineSegment(sketch, "E109.top", {"start": v(-7766.05, 0) * mm, "end": v(-7727.98, 0) * mm});
            skLineSegment(sketch, "E109.left", {"start": v(-7766.05, 139.7) * mm, "end": v(-7766.05, 0) * mm});
            skLineSegment(sketch, "E109.right", {"start": v(-7727.98, 139.7) * mm, "end": v(-7727.98, 0) * mm});
            skSolve(sketch);
        }
        {
            var Q0;
            Q0 = qSketchRegion(id + "F2", true);
            extrude(context, id + "F3", {"entities" : qUnion([Q0]), "operationType" : NewBodyOperationType.ADD, "depth" : 2352.67 * mm});
        }
        {
            var Q0;
            Q0=makeQuery(id+"F3.opExtrude","CAP_FACE",FACE,{"disambiguationData":[OSD([sQuery(id+"F2.wireOp",EDGE,"E84.bottom"),sQuery(id+"F2.wireOp",EDGE,"E84.top"),sQuery(id+"F2.wireOp",EDGE,"E84.left"),sQuery(id+"F2.wireOp",EDGE,"E84.right")])],"isStart":false});
            var sketch = newSketch(context, id + "F4", { "sketchPlane" : qUnion([Q0]) });
            skLineSegment(sketch, "E110.bottom", {"start": v(-1174.03, 0) * mm, "end": v(-0.03, 0) * mm});
            skLineSegment(sketch, "E110.top", {"start": v(-1174.03, 139.7) * mm, "end": v(-0.03, 139.7) * mm});
            skLineSegment(sketch, "E110.left", {"start": v(-1174.03, 0) * mm, "end": v(-1174.03, 139.7) * mm});
            skLineSegment(sketch, "E111", {"start": v(-0.03, 0) * mm, "end": v(-0.03, 139.7) * mm});
            skSolve(sketch);
        }
        {
            var Q0;
            Q0 = qSketchRegion(id + "F4", true);
            extrude(context, id + "F5", {"entities" : qUnion([Q0]), "operationType" : NewBodyOperationType.ADD, "depth" : 76.2 * mm});
        }
        {
            var Q0;
            Q0=makeQuery(id+"F3.opExtrude","CAP_FACE",FACE,{"disambiguationData":[OSD([sQuery(id+"F2.wireOp",EDGE,"E76.bottom"),sQuery(id+"F2.wireOp",EDGE,"E76.top"),sQuery(id+"F2.wireOp",EDGE,"E76.left"),sQuery(id+"F2.wireOp",EDGE,"E76.right")])],"isStart":false});
            var sketch = newSketch(context, id + "F6", { "sketchPlane" : qUnion([Q0]) });
            skSolve(sketch);
        }
        {
            var Q0;
            Q0=makeQuery(id+"F6.imprint","IMPRINT",FACE,{"disambiguationData":[TD([[makeQuery(id+"F6.imprint","IMPRINT",EDGE,{"derivedFrom":makeQuery(id+"F3.opExtrude","CAP_EDGE",EDGE,{"disambiguationData":[OSD([sQuery(id+"F2.wireOp",EDGE,"E76.bottom")])],"isStart":false})}),-1.0]])]});
            var Q1;
            Q1=makeQuery(id+"F3.opExtrude","CAP_FACE",FACE,{"disambiguationData":[OSD([sQuery(id+"F2.wireOp",EDGE,"E77.bottom"),sQuery(id+"F2.wireOp",EDGE,"E77.top"),sQuery(id+"F2.wireOp",EDGE,"E77.left"),sQuery(id+"F2.wireOp",EDGE,"E77.right")])],"isStart":false});
            var Q2;
            Q2=makeQuery(id+"F3.opExtrude","CAP_FACE",FACE,{"disambiguationData":[OSD([sQuery(id+"F2.wireOp",EDGE,"E80.bottom"),sQuery(id+"F2.wireOp",EDGE,"E80.top"),sQuery(id+"F2.wireOp",EDGE,"E80.left"),sQuery(id+"F2.wireOp",EDGE,"E80.right")])],"isStart":false});
            var Q3;
            Q3=makeQuery(id+"F3.opExtrude","CAP_FACE",FACE,{"disambiguationData":[OSD([sQuery(id+"F2.wireOp",EDGE,"E81.1.0.0"),sQuery(id+"F2.wireOp",EDGE,"E81.1.0.1"),sQuery(id+"F2.wireOp",EDGE,"E81.1.0.2"),sQuery(id+"F2.wireOp",EDGE,"E81.1.0.3")])],"isStart":false});
            var Q4;
            Q4=makeQuery(id+"F3.opExtrude","CAP_FACE",FACE,{"disambiguationData":[OSD([sQuery(id+"F2.wireOp",EDGE,"E81.2.0.0"),sQuery(id+"F2.wireOp",EDGE,"E81.2.0.1"),sQuery(id+"F2.wireOp",EDGE,"E81.2.0.2"),sQuery(id+"F2.wireOp",EDGE,"E81.2.0.3")])],"isStart":false});
            var Q5;
            Q5=makeQuery(id+"F3.opExtrude","CAP_FACE",FACE,{"disambiguationData":[OSD([sQuery(id+"F2.wireOp",EDGE,"E81.3.0.0"),sQuery(id+"F2.wireOp",EDGE,"E81.3.0.1"),sQuery(id+"F2.wireOp",EDGE,"E81.3.0.2"),sQuery(id+"F2.wireOp",EDGE,"E81.3.0.3")])],"isStart":false});
            var Q6;
            Q6=makeQuery(id+"F3.opExtrude","CAP_FACE",FACE,{"disambiguationData":[OSD([sQuery(id+"F2.wireOp",EDGE,"E81.4.0.0"),sQuery(id+"F2.wireOp",EDGE,"E81.4.0.1"),sQuery(id+"F2.wireOp",EDGE,"E81.4.0.2"),sQuery(id+"F2.wireOp",EDGE,"E81.4.0.3")])],"isStart":false});
            var Q7;
            Q7=makeQuery(id+"F3.opExtrude","CAP_FACE",FACE,{"disambiguationData":[OSD([sQuery(id+"F2.wireOp",EDGE,"E81.5.0.0"),sQuery(id+"F2.wireOp",EDGE,"E81.5.0.1"),sQuery(id+"F2.wireOp",EDGE,"E81.5.0.2"),sQuery(id+"F2.wireOp",EDGE,"E81.5.0.3")])],"isStart":false});
            var Q8;
            Q8=makeQuery(id+"F3.opExtrude","CAP_FACE",FACE,{"disambiguationData":[OSD([sQuery(id+"F2.wireOp",EDGE,"E81.6.0.0"),sQuery(id+"F2.wireOp",EDGE,"E81.6.0.1"),sQuery(id+"F2.wireOp",EDGE,"E81.6.0.2"),sQuery(id+"F2.wireOp",EDGE,"E81.6.0.3")])],"isStart":false});
            var Q9;
            Q9=makeQuery(id+"F3.opExtrude","CAP_FACE",FACE,{"disambiguationData":[OSD([sQuery(id+"F2.wireOp",EDGE,"E81.7.0.0"),sQuery(id+"F2.wireOp",EDGE,"E81.7.0.1"),sQuery(id+"F2.wireOp",EDGE,"E81.7.0.2"),sQuery(id+"F2.wireOp",EDGE,"E81.7.0.3")])],"isStart":false});
            var Q10;
            Q10=makeQuery(id+"F3.opExtrude","CAP_FACE",FACE,{"disambiguationData":[OSD([sQuery(id+"F2.wireOp",EDGE,"E81.8.0.0"),sQuery(id+"F2.wireOp",EDGE,"E81.8.0.1"),sQuery(id+"F2.wireOp",EDGE,"E81.8.0.2"),sQuery(id+"F2.wireOp",EDGE,"E81.8.0.3")])],"isStart":false});
            var Q11;
            Q11=makeQuery(id+"F3.opExtrude","CAP_FACE",FACE,{"disambiguationData":[OSD([sQuery(id+"F2.wireOp",EDGE,"E81.9.0.0"),sQuery(id+"F2.wireOp",EDGE,"E81.9.0.1"),sQuery(id+"F2.wireOp",EDGE,"E81.9.0.2"),sQuery(id+"F2.wireOp",EDGE,"E81.9.0.3")])],"isStart":false});
            var Q12;
            Q12=makeQuery(id+"F3.opExtrude","CAP_FACE",FACE,{"disambiguationData":[OSD([sQuery(id+"F2.wireOp",EDGE,"E81.10.0.0"),sQuery(id+"F2.wireOp",EDGE,"E81.10.0.1"),sQuery(id+"F2.wireOp",EDGE,"E81.10.0.2"),sQuery(id+"F2.wireOp",EDGE,"E81.10.0.3")])],"isStart":false});
            var Q13;
            Q13=makeQuery(id+"F3.opExtrude","CAP_FACE",FACE,{"disambiguationData":[OSD([sQuery(id+"F2.wireOp",EDGE,"E81.11.0.0"),sQuery(id+"F2.wireOp",EDGE,"E81.11.0.1"),sQuery(id+"F2.wireOp",EDGE,"E81.11.0.2"),sQuery(id+"F2.wireOp",EDGE,"E81.11.0.3")])],"isStart":false});
            var Q14;
            Q14=makeQuery(id+"F3.opExtrude","CAP_FACE",FACE,{"disambiguationData":[OSD([sQuery(id+"F2.wireOp",EDGE,"E81.12.0.0"),sQuery(id+"F2.wireOp",EDGE,"E81.12.0.1"),sQuery(id+"F2.wireOp",EDGE,"E81.12.0.2"),sQuery(id+"F2.wireOp",EDGE,"E81.12.0.3")])],"isStart":false});
            var Q15;
            Q15=makeQuery(id+"F3.opExtrude","CAP_FACE",FACE,{"disambiguationData":[OSD([sQuery(id+"F2.wireOp",EDGE,"E81.13.0.0"),sQuery(id+"F2.wireOp",EDGE,"E81.13.0.1"),sQuery(id+"F2.wireOp",EDGE,"E81.13.0.2"),sQuery(id+"F2.wireOp",EDGE,"E81.13.0.3")])],"isStart":false});
            var Q16;
            Q16=makeQuery(id+"F3.opExtrude","CAP_FACE",FACE,{"disambiguationData":[OSD([sQuery(id+"F2.wireOp",EDGE,"E81.14.0.0"),sQuery(id+"F2.wireOp",EDGE,"E81.14.0.1"),sQuery(id+"F2.wireOp",EDGE,"E81.14.0.2"),sQuery(id+"F2.wireOp",EDGE,"E81.14.0.3")])],"isStart":false});
            var Q17;
            Q17=makeQuery(id+"F3.opExtrude","CAP_FACE",FACE,{"disambiguationData":[OSD([sQuery(id+"F2.wireOp",EDGE,"E81.15.0.0"),sQuery(id+"F2.wireOp",EDGE,"E81.15.0.1"),sQuery(id+"F2.wireOp",EDGE,"E81.15.0.2"),sQuery(id+"F2.wireOp",EDGE,"E81.15.0.3")])],"isStart":false});
            var Q18;
            Q18=makeQuery(id+"F3.opExtrude","CAP_FACE",FACE,{"disambiguationData":[OSD([sQuery(id+"F2.wireOp",EDGE,"E81.16.0.0"),sQuery(id+"F2.wireOp",EDGE,"E81.16.0.1"),sQuery(id+"F2.wireOp",EDGE,"E81.16.0.2"),sQuery(id+"F2.wireOp",EDGE,"E81.16.0.3")])],"isStart":false});
            var Q19;
            Q19=makeQuery(id+"F3.opExtrude","CAP_FACE",FACE,{"disambiguationData":[OSD([sQuery(id+"F2.wireOp",EDGE,"E81.17.0.0"),sQuery(id+"F2.wireOp",EDGE,"E81.17.0.1"),sQuery(id+"F2.wireOp",EDGE,"E81.17.0.2"),sQuery(id+"F2.wireOp",EDGE,"E81.17.0.3")])],"isStart":false});
            var Q20;
            Q20=makeQuery(id+"F3.opExtrude","CAP_FACE",FACE,{"disambiguationData":[OSD([sQuery(id+"F2.wireOp",EDGE,"E81.18.0.0"),sQuery(id+"F2.wireOp",EDGE,"E81.18.0.1"),sQuery(id+"F2.wireOp",EDGE,"E81.18.0.2"),sQuery(id+"F2.wireOp",EDGE,"E81.18.0.3")])],"isStart":false});
            var Q21;
            Q21=makeQuery(id+"F3.opExtrude","CAP_FACE",FACE,{"disambiguationData":[OSD([sQuery(id+"F2.wireOp",EDGE,"E81.19.0.0"),sQuery(id+"F2.wireOp",EDGE,"E81.19.0.1"),sQuery(id+"F2.wireOp",EDGE,"E81.19.0.2"),sQuery(id+"F2.wireOp",EDGE,"E81.19.0.3")])],"isStart":false});
            var Q22;
            Q22=makeQuery(id+"F3.opExtrude","CAP_FACE",FACE,{"disambiguationData":[OSD([sQuery(id+"F2.wireOp",EDGE,"E81.20.0.0"),sQuery(id+"F2.wireOp",EDGE,"E81.20.0.1"),sQuery(id+"F2.wireOp",EDGE,"E81.20.0.2"),sQuery(id+"F2.wireOp",EDGE,"E81.20.0.3")])],"isStart":false});
            var Q23;
            Q23=makeQuery(id+"F3.opExtrude","CAP_FACE",FACE,{"disambiguationData":[OSD([sQuery(id+"F2.wireOp",EDGE,"E81.21.0.0"),sQuery(id+"F2.wireOp",EDGE,"E81.21.0.1"),sQuery(id+"F2.wireOp",EDGE,"E81.21.0.2"),sQuery(id+"F2.wireOp",EDGE,"E81.21.0.3")])],"isStart":false});
            var Q24;
            Q24=makeQuery(id+"F3.opExtrude","CAP_FACE",FACE,{"disambiguationData":[OSD([sQuery(id+"F2.wireOp",EDGE,"E81.22.0.0"),sQuery(id+"F2.wireOp",EDGE,"E81.22.0.1"),sQuery(id+"F2.wireOp",EDGE,"E81.22.0.2"),sQuery(id+"F2.wireOp",EDGE,"E81.22.0.3")])],"isStart":false});
            var Q25;
            Q25=makeQuery(id+"F3.opExtrude","CAP_FACE",FACE,{"disambiguationData":[OSD([sQuery(id+"F2.wireOp",EDGE,"E81.23.0.0"),sQuery(id+"F2.wireOp",EDGE,"E81.23.0.1"),sQuery(id+"F2.wireOp",EDGE,"E81.23.0.2"),sQuery(id+"F2.wireOp",EDGE,"E81.23.0.3")])],"isStart":false});
            var Q26;
            Q26=makeQuery(id+"F3.opExtrude","CAP_FACE",FACE,{"disambiguationData":[OSD([sQuery(id+"F2.wireOp",EDGE,"E86.bottom"),sQuery(id+"F2.wireOp",EDGE,"E86.top"),sQuery(id+"F2.wireOp",EDGE,"E86.left"),sQuery(id+"F2.wireOp",EDGE,"E86.right")])],"isStart":false});
            var Q27;
            Q27=makeQuery(id+"F3.opExtrude","CAP_FACE",FACE,{"disambiguationData":[OSD([sQuery(id+"F2.wireOp",EDGE,"E92.bottom"),sQuery(id+"F2.wireOp",EDGE,"E92.top"),sQuery(id+"F2.wireOp",EDGE,"E92.left"),sQuery(id+"F2.wireOp",EDGE,"E92.right")])],"isStart":false});
            var Q28;
            Q28=makeQuery(id+"F3.opExtrude","CAP_FACE",FACE,{"disambiguationData":[OSD([sQuery(id+"F2.wireOp",EDGE,"E93.bottom"),sQuery(id+"F2.wireOp",EDGE,"E93.top"),sQuery(id+"F2.wireOp",EDGE,"E93.left"),sQuery(id+"F2.wireOp",EDGE,"E93.right")])],"isStart":false});
            var Q29;
            Q29=makeQuery(id+"F3.opExtrude","CAP_FACE",FACE,{"disambiguationData":[OSD([sQuery(id+"F2.wireOp",EDGE,"E95.bottom"),sQuery(id+"F2.wireOp",EDGE,"E95.top"),sQuery(id+"F2.wireOp",EDGE,"E95.left"),sQuery(id+"F2.wireOp",EDGE,"E95.right")])],"isStart":false});
            var Q30;
            Q30=makeQuery(id+"F3.opExtrude","CAP_FACE",FACE,{"disambiguationData":[OSD([sQuery(id+"F2.wireOp",EDGE,"E97.bottom"),sQuery(id+"F2.wireOp",EDGE,"E97.top"),sQuery(id+"F2.wireOp",EDGE,"E97.left"),sQuery(id+"F2.wireOp",EDGE,"E97.right")])],"isStart":false});
            var Q31;
            Q31=makeQuery(id+"F3.opExtrude","CAP_FACE",FACE,{"disambiguationData":[OSD([sQuery(id+"F2.wireOp",EDGE,"E99.bottom"),sQuery(id+"F2.wireOp",EDGE,"E99.top"),sQuery(id+"F2.wireOp",EDGE,"E99.left"),sQuery(id+"F2.wireOp",EDGE,"E99.right")])],"isStart":false});
            var Q32;
            Q32=makeQuery(id+"F3.opExtrude","CAP_FACE",FACE,{"disambiguationData":[OSD([sQuery(id+"F2.wireOp",EDGE,"E101.bottom"),sQuery(id+"F2.wireOp",EDGE,"E101.top"),sQuery(id+"F2.wireOp",EDGE,"E101.left"),sQuery(id+"F2.wireOp",EDGE,"E101.right")])],"isStart":false});
            var Q33;
            Q33=makeQuery(id+"F3.opExtrude","CAP_FACE",FACE,{"disambiguationData":[OSD([sQuery(id+"F2.wireOp",EDGE,"E94.bottom"),sQuery(id+"F2.wireOp",EDGE,"E94.top"),sQuery(id+"F2.wireOp",EDGE,"E94.left"),sQuery(id+"F2.wireOp",EDGE,"E94.right")])],"isStart":false});
            var Q34;
            Q34=makeQuery(id+"F3.opExtrude","CAP_FACE",FACE,{"disambiguationData":[OSD([sQuery(id+"F2.wireOp",EDGE,"E96.bottom"),sQuery(id+"F2.wireOp",EDGE,"E96.top"),sQuery(id+"F2.wireOp",EDGE,"E96.left"),sQuery(id+"F2.wireOp",EDGE,"E96.right")])],"isStart":false});
            var Q35;
            Q35=makeQuery(id+"F3.opExtrude","CAP_FACE",FACE,{"disambiguationData":[OSD([sQuery(id+"F2.wireOp",EDGE,"E98.bottom"),sQuery(id+"F2.wireOp",EDGE,"E98.top"),sQuery(id+"F2.wireOp",EDGE,"E98.left"),sQuery(id+"F2.wireOp",EDGE,"E98.right")])],"isStart":false});
            var Q36;
            Q36=makeQuery(id+"F3.opExtrude","CAP_FACE",FACE,{"disambiguationData":[OSD([sQuery(id+"F2.wireOp",EDGE,"E100.bottom"),sQuery(id+"F2.wireOp",EDGE,"E100.top"),sQuery(id+"F2.wireOp",EDGE,"E100.left"),sQuery(id+"F2.wireOp",EDGE,"E100.right")])],"isStart":false});
            var Q37;
            Q37=makeQuery(id+"F3.opExtrude","CAP_FACE",FACE,{"disambiguationData":[OSD([sQuery(id+"F2.wireOp",EDGE,"E102.bottom"),sQuery(id+"F2.wireOp",EDGE,"E102.top"),sQuery(id+"F2.wireOp",EDGE,"E102.left"),sQuery(id+"F2.wireOp",EDGE,"E102.right")])],"isStart":false});
            var Q38;
            Q38=makeQuery(id+"F3.opExtrude","CAP_FACE",FACE,{"disambiguationData":[OSD([sQuery(id+"F2.wireOp",EDGE,"E103.bottom"),sQuery(id+"F2.wireOp",EDGE,"E103.top"),sQuery(id+"F2.wireOp",EDGE,"E103.left"),sQuery(id+"F2.wireOp",EDGE,"E103.right")])],"isStart":false});
            var Q39;
            Q39=makeQuery(id+"F3.opExtrude","CAP_FACE",FACE,{"disambiguationData":[OSD([sQuery(id+"F2.wireOp",EDGE,"E105.bottom"),sQuery(id+"F2.wireOp",EDGE,"E105.top"),sQuery(id+"F2.wireOp",EDGE,"E105.left"),sQuery(id+"F2.wireOp",EDGE,"E105.right")])],"isStart":false});
            var Q40;
            Q40=makeQuery(id+"F3.opExtrude","CAP_FACE",FACE,{"disambiguationData":[OSD([sQuery(id+"F2.wireOp",EDGE,"E104.bottom"),sQuery(id+"F2.wireOp",EDGE,"E104.top"),sQuery(id+"F2.wireOp",EDGE,"E104.left"),sQuery(id+"F2.wireOp",EDGE,"E104.right")])],"isStart":false});
            var Q41;
            Q41=makeQuery(id+"F3.opExtrude","CAP_FACE",FACE,{"disambiguationData":[OSD([sQuery(id+"F2.wireOp",EDGE,"E106.bottom"),sQuery(id+"F2.wireOp",EDGE,"E106.top"),sQuery(id+"F2.wireOp",EDGE,"E106.left"),sQuery(id+"F2.wireOp",EDGE,"E106.right")])],"isStart":false});
            var Q42;
            Q42=makeQuery(id+"F3.opExtrude","CAP_FACE",FACE,{"disambiguationData":[OSD([sQuery(id+"F2.wireOp",EDGE,"E107.bottom"),sQuery(id+"F2.wireOp",EDGE,"E107.top"),sQuery(id+"F2.wireOp",EDGE,"E107.left"),sQuery(id+"F2.wireOp",EDGE,"E107.right")])],"isStart":false});
            var Q43;
            Q43=makeQuery(id+"F3.opExtrude","CAP_FACE",FACE,{"disambiguationData":[OSD([sQuery(id+"F2.wireOp",EDGE,"E108.bottom"),sQuery(id+"F2.wireOp",EDGE,"E108.top"),sQuery(id+"F2.wireOp",EDGE,"E108.left"),sQuery(id+"F2.wireOp",EDGE,"E108.right")])],"isStart":false});
            var Q44;
            Q44=makeQuery(id+"F3.opExtrude","CAP_FACE",FACE,{"disambiguationData":[OSD([sQuery(id+"F2.wireOp",EDGE,"E109.bottom"),sQuery(id+"F2.wireOp",EDGE,"E109.top"),sQuery(id+"F2.wireOp",EDGE,"E109.left"),sQuery(id+"F2.wireOp",EDGE,"E109.right")])],"isStart":false});
            extrude(context, id + "F7", {"entities" : qUnion([Q0, Q1, Q2, Q3, Q4, Q5, Q6, Q7, Q8, Q9, Q10, Q11, Q12, Q13, Q14, Q15, Q16, Q17, Q18, Q19, Q20, Q21, Q22, Q23, Q24, Q25, Q26, Q27, Q28, Q29, Q30, Q31, Q32, Q33, Q34, Q35, Q36, Q37, Q38, Q39, Q40, Q41, Q42, Q43, Q44]), "operationType" : NewBodyOperationType.ADD, "depth" : 2787.65 * mm});
        }
        {
            var Q0;
            Q0=makeQuery(id+"F7.opExtrude","CAP_FACE",FACE,{"disambiguationData":[OSD([sQuery(id+"F2.wireOp",EDGE,"E76.bottom"),sQuery(id+"F2.wireOp",EDGE,"E76.top"),sQuery(id+"F2.wireOp",EDGE,"E76.left"),sQuery(id+"F2.wireOp",EDGE,"E76.right")])],"isStart":false});
            var sketch = newSketch(context, id + "F8", { "sketchPlane" : qUnion([Q0]) });
            skLineSegment(sketch, "E112.bottom", {"start": v(-11277.6, 139.7) * mm, "end": v(-1174.06, 139.7) * mm});
            skLineSegment(sketch, "E112.top", {"start": v(-11277.6, 0) * mm, "end": v(-1174.06, 0) * mm});
            skLineSegment(sketch, "E112.left", {"start": v(-11277.6, 139.7) * mm, "end": v(-11277.6, 0) * mm});
            skLineSegment(sketch, "E112.right", {"start": v(-1174.06, 139.7) * mm, "end": v(-1174.06, 0) * mm});
            skSolve(sketch);
        }
        {
            var Q0;
            Q0 = qSketchRegion(id + "F8", true);
            extrude(context, id + "F9", {"entities" : qUnion([Q0]), "operationType" : NewBodyOperationType.ADD, "depth" : 76.2 * mm});
        }
        {
            var Q0;
            {var subQ0=sQuery(id+"F2.wireOp",EDGE,"E76.bottom");var subQ1=sQuery(id+"F2.wireOp",EDGE,"E93.top");var subQ2=sQuery(id+"F2.wireOp",EDGE,"E92.top");var subQ3=sQuery(id+"F2.wireOp",EDGE,"E86.top");var subQ4=sQuery(id+"F2.wireOp",EDGE,"E81.23.0.3");var subQ5=sQuery(id+"F2.wireOp",EDGE,"E81.22.0.3");var subQ6=sQuery(id+"F2.wireOp",EDGE,"E81.21.0.3");var subQ7=sQuery(id+"F2.wireOp",EDGE,"E81.20.0.3");var subQ8=sQuery(id+"F2.wireOp",EDGE,"E81.19.0.3");var subQ9=sQuery(id+"F2.wireOp",EDGE,"E81.18.0.3");var subQ10=sQuery(id+"F2.wireOp",EDGE,"E81.17.0.3");var subQ11=sQuery(id+"F2.wireOp",EDGE,"E81.16.0.3");var subQ12=sQuery(id+"F2.wireOp",EDGE,"E81.15.0.3");var subQ13=sQuery(id+"F2.wireOp",EDGE,"E81.14.0.3");var subQ14=sQuery(id+"F2.wireOp",EDGE,"E81.13.0.3");var subQ15=sQuery(id+"F2.wireOp",EDGE,"E81.12.0.3");var subQ16=sQuery(id+"F2.wireOp",EDGE,"E81.11.0.3");var subQ17=sQuery(id+"F2.wireOp",EDGE,"E81.10.0.3");var subQ18=sQuery(id+"F2.wireOp",EDGE,"E81.9.0.3");var subQ19=sQuery(id+"F2.wireOp",EDGE,"E81.8.0.3");var subQ20=sQuery(id+"F2.wireOp",EDGE,"E81.7.0.3");var subQ21=sQuery(id+"F2.wireOp",EDGE,"E81.6.0.3");var subQ22=sQuery(id+"F2.wireOp",EDGE,"E81.5.0.3");var subQ23=sQuery(id+"F2.wireOp",EDGE,"E81.4.0.3");var subQ24=sQuery(id+"F2.wireOp",EDGE,"E81.3.0.3");var subQ25=sQuery(id+"F2.wireOp",EDGE,"E81.2.0.3");var subQ26=sQuery(id+"F2.wireOp",EDGE,"E81.1.0.3");var subQ27=sQuery(id+"F2.wireOp",EDGE,"E80.top");Q0=makeQuery(id+"F9.boolean.opBoolean","MERGE",FACE,{"derivedFrom":[makeQuery(id+"F7.boolean.opBoolean","MERGE",FACE,{"derivedFrom":[makeQuery(id+"F5.boolean.opBoolean","MERGE",FACE,{"derivedFrom":[makeQuery(id+"F3.boolean.opBoolean","MERGE",FACE,{"derivedFrom":[makeQuery(id+"F1.opExtrude","SWEPT_FACE",FACE,{"disambiguationData":[OSD([sQuery(id+"F0.wireOp",EDGE,"E0")])]}),makeQuery(id+"F3.opExtrude","SWEPT_FACE",FACE,{"disambiguationData":[OSD([subQ0])]}),makeQuery(id+"F3.opExtrude","SWEPT_FACE",FACE,{"disambiguationData":[OSD([sQuery(id+"F2.wireOp",EDGE,"E78.bottom")])]}),makeQuery(id+"F3.opExtrude","SWEPT_FACE",FACE,{"disambiguationData":[OSD([subQ27])]}),makeQuery(id+"F3.opExtrude","SWEPT_FACE",FACE,{"disambiguationData":[OSD([subQ26])]}),makeQuery(id+"F3.opExtrude","SWEPT_FACE",FACE,{"disambiguationData":[OSD([subQ25])]}),makeQuery(id+"F3.opExtrude","SWEPT_FACE",FACE,{"disambiguationData":[OSD([subQ24])]}),makeQuery(id+"F3.opExtrude","SWEPT_FACE",FACE,{"disambiguationData":[OSD([subQ23])]}),makeQuery(id+"F3.opExtrude","SWEPT_FACE",FACE,{"disambiguationData":[OSD([subQ22])]}),makeQuery(id+"F3.opExtrude","SWEPT_FACE",FACE,{"disambiguationData":[OSD([subQ21])]}),makeQuery(id+"F3.opExtrude","SWEPT_FACE",FACE,{"disambiguationData":[OSD([subQ20])]}),makeQuery(id+"F3.opExtrude","SWEPT_FACE",FACE,{"disambiguationData":[OSD([subQ19])]}),makeQuery(id+"F3.opExtrude","SWEPT_FACE",FACE,{"disambiguationData":[OSD([subQ18])]}),makeQuery(id+"F3.opExtrude","SWEPT_FACE",FACE,{"disambiguationData":[OSD([subQ17])]}),makeQuery(id+"F3.opExtrude","SWEPT_FACE",FACE,{"disambiguationData":[OSD([subQ16])]}),makeQuery(id+"F3.opExtrude","SWEPT_FACE",FACE,{"disambiguationData":[OSD([subQ15])]}),makeQuery(id+"F3.opExtrude","SWEPT_FACE",FACE,{"disambiguationData":[OSD([subQ14])]}),makeQuery(id+"F3.opExtrude","SWEPT_FACE",FACE,{"disambiguationData":[OSD([subQ13])]}),makeQuery(id+"F3.opExtrude","SWEPT_FACE",FACE,{"disambiguationData":[OSD([subQ12])]}),makeQuery(id+"F3.opExtrude","SWEPT_FACE",FACE,{"disambiguationData":[OSD([subQ11])]}),makeQuery(id+"F3.opExtrude","SWEPT_FACE",FACE,{"disambiguationData":[OSD([subQ10])]}),makeQuery(id+"F3.opExtrude","SWEPT_FACE",FACE,{"disambiguationData":[OSD([subQ9])]}),makeQuery(id+"F3.opExtrude","SWEPT_FACE",FACE,{"disambiguationData":[OSD([subQ8])]}),makeQuery(id+"F3.opExtrude","SWEPT_FACE",FACE,{"disambiguationData":[OSD([subQ7])]}),makeQuery(id+"F3.opExtrude","SWEPT_FACE",FACE,{"disambiguationData":[OSD([subQ6])]}),makeQuery(id+"F3.opExtrude","SWEPT_FACE",FACE,{"disambiguationData":[OSD([subQ5])]}),makeQuery(id+"F3.opExtrude","SWEPT_FACE",FACE,{"disambiguationData":[OSD([subQ4])]}),makeQuery(id+"F3.opExtrude","SWEPT_FACE",FACE,{"disambiguationData":[OSD([sQuery(id+"F2.wireOp",EDGE,"E81.25.0.3")])]}),makeQuery(id+"F3.opExtrude","SWEPT_FACE",FACE,{"disambiguationData":[OSD([sQuery(id+"F2.wireOp",EDGE,"E81.26.0.3")])]}),makeQuery(id+"F3.opExtrude","SWEPT_FACE",FACE,{"disambiguationData":[OSD([sQuery(id+"F2.wireOp",EDGE,"E84.top")])]}),makeQuery(id+"F3.opExtrude","SWEPT_FACE",FACE,{"disambiguationData":[OSD([sQuery(id+"F2.wireOp",EDGE,"E85.top")])]}),makeQuery(id+"F3.opExtrude","SWEPT_FACE",FACE,{"disambiguationData":[OSD([subQ3])]}),makeQuery(id+"F3.opExtrude","SWEPT_FACE",FACE,{"disambiguationData":[OSD([sQuery(id+"F2.wireOp",EDGE,"E87.top")])]}),makeQuery(id+"F3.opExtrude","SWEPT_FACE",FACE,{"disambiguationData":[OSD([sQuery(id+"F2.wireOp",EDGE,"E88.top")])]}),makeQuery(id+"F3.opExtrude","SWEPT_FACE",FACE,{"disambiguationData":[OSD([sQuery(id+"F2.wireOp",EDGE,"E89.top")])]}),makeQuery(id+"F3.opExtrude","SWEPT_FACE",FACE,{"disambiguationData":[OSD([sQuery(id+"F2.wireOp",EDGE,"E90.top")])]}),makeQuery(id+"F3.opExtrude","SWEPT_FACE",FACE,{"disambiguationData":[OSD([sQuery(id+"F2.wireOp",EDGE,"E91.top")])]}),makeQuery(id+"F3.opExtrude","SWEPT_FACE",FACE,{"disambiguationData":[OSD([subQ2])]}),makeQuery(id+"F3.opExtrude","SWEPT_FACE",FACE,{"disambiguationData":[OSD([subQ1])]})]}),makeQuery(id+"F5.opExtrude","SWEPT_FACE",FACE,{"disambiguationData":[OSD([sQuery(id+"F4.wireOp",EDGE,"E110.bottom")])]})]}),makeQuery(id+"F7.opExtrude","SWEPT_FACE",FACE,{"disambiguationData":[OSD([subQ27])]}),makeQuery(id+"F7.opExtrude","SWEPT_FACE",FACE,{"disambiguationData":[OSD([subQ26])]}),makeQuery(id+"F7.opExtrude","SWEPT_FACE",FACE,{"disambiguationData":[OSD([subQ25])]}),makeQuery(id+"F7.opExtrude","SWEPT_FACE",FACE,{"disambiguationData":[OSD([subQ24])]}),makeQuery(id+"F7.opExtrude","SWEPT_FACE",FACE,{"disambiguationData":[OSD([subQ23])]}),makeQuery(id+"F7.opExtrude","SWEPT_FACE",FACE,{"disambiguationData":[OSD([subQ22])]}),makeQuery(id+"F7.opExtrude","SWEPT_FACE",FACE,{"disambiguationData":[OSD([subQ21])]}),makeQuery(id+"F7.opExtrude","SWEPT_FACE",FACE,{"disambiguationData":[OSD([subQ20])]}),makeQuery(id+"F7.opExtrude","SWEPT_FACE",FACE,{"disambiguationData":[OSD([subQ19])]}),makeQuery(id+"F7.opExtrude","SWEPT_FACE",FACE,{"disambiguationData":[OSD([subQ18])]}),makeQuery(id+"F7.opExtrude","SWEPT_FACE",FACE,{"disambiguationData":[OSD([subQ17])]}),makeQuery(id+"F7.opExtrude","SWEPT_FACE",FACE,{"disambiguationData":[OSD([subQ16])]}),makeQuery(id+"F7.opExtrude","SWEPT_FACE",FACE,{"disambiguationData":[OSD([subQ15])]}),makeQuery(id+"F7.opExtrude","SWEPT_FACE",FACE,{"disambiguationData":[OSD([subQ14])]}),makeQuery(id+"F7.opExtrude","SWEPT_FACE",FACE,{"disambiguationData":[OSD([subQ13])]}),makeQuery(id+"F7.opExtrude","SWEPT_FACE",FACE,{"disambiguationData":[OSD([subQ12])]}),makeQuery(id+"F7.opExtrude","SWEPT_FACE",FACE,{"disambiguationData":[OSD([subQ11])]}),makeQuery(id+"F7.opExtrude","SWEPT_FACE",FACE,{"disambiguationData":[OSD([subQ10])]}),makeQuery(id+"F7.opExtrude","SWEPT_FACE",FACE,{"disambiguationData":[OSD([subQ9])]}),makeQuery(id+"F7.opExtrude","SWEPT_FACE",FACE,{"disambiguationData":[OSD([subQ8])]}),makeQuery(id+"F7.opExtrude","SWEPT_FACE",FACE,{"disambiguationData":[OSD([subQ7])]}),makeQuery(id+"F7.opExtrude","SWEPT_FACE",FACE,{"disambiguationData":[OSD([subQ6])]}),makeQuery(id+"F7.opExtrude","SWEPT_FACE",FACE,{"disambiguationData":[OSD([subQ5])]}),makeQuery(id+"F7.opExtrude","SWEPT_FACE",FACE,{"disambiguationData":[OSD([subQ4])]}),makeQuery(id+"F7.opExtrude","SWEPT_FACE",FACE,{"disambiguationData":[OSD([subQ3])]}),makeQuery(id+"F7.opExtrude","SWEPT_FACE",FACE,{"disambiguationData":[OSD([subQ2])]}),makeQuery(id+"F7.opExtrude","SWEPT_FACE",FACE,{"disambiguationData":[OSD([subQ1])]}),makeQuery(id+"F7.opExtrude","SWEPT_FACE",FACE,{"disambiguationData":[OSD([subQ0])]})]}),makeQuery(id+"F9.opExtrude","SWEPT_FACE",FACE,{"disambiguationData":[OSD([sQuery(id+"F8.wireOp",EDGE,"E112.top")])]})]});}
            var sketch = newSketch(context, id + "F10", { "sketchPlane" : qUnion([Q0]) });
            skLineSegment(sketch, "E113.bottom", {"start": v(-2859.96, 0) * mm, "end": v(-1453.43, 0) * mm});
            skLineSegment(sketch, "E113.left", {"start": v(-2859.96, 0) * mm, "end": v(-2859.96, 2095.5) * mm});
            skLineSegment(sketch, "E113.right", {"start": v(-1453.43, 0) * mm, "end": v(-1453.43, 2095.5) * mm});
            skLineSegment(sketch, "E114", {"start": v(-2936.16, 2390.78) * mm, "end": v(-2859.96, 2390.78) * mm});
            skLineSegment(sketch, "E115", {"start": v(-1377.23, 2390.78) * mm, "end": v(-1377.23, 2095.5) * mm});
            skLineSegment(sketch, "E116", {"start": v(-1377.23, 2095.5) * mm, "end": v(-1453.43, 2095.5) * mm});
            skLineSegment(sketch, "E117", {"start": v(-2936.16, 2390.78) * mm, "end": v(-2936.16, 2095.5) * mm});
            skLineSegment(sketch, "E118", {"start": v(-2936.16, 2095.5) * mm, "end": v(-2859.96, 2095.5) * mm});
            skLineSegment(sketch, "E119", {"start": v(-2859.96, 2390.78) * mm, "end": v(-2859.96, 2235.2) * mm});
            skLineSegment(sketch, "E120", {"start": v(-2859.96, 2235.2) * mm, "end": v(-1453.43, 2235.2) * mm});
            skLineSegment(sketch, "E121", {"start": v(-1453.43, 2235.2) * mm, "end": v(-1453.43, 2390.78) * mm});
            skLineSegment(sketch, "E122.trimOffspring", {"start": v(-1453.43, 2390.78) * mm, "end": v(-1377.23, 2390.78) * mm});
            skSolve(sketch);
        }
        {
            var Q0;
            Q0 = qSketchRegion(id + "F10", true);
            extrude(context, id + "F11", {"entities" : qUnion([Q0]), "operationType" : NewBodyOperationType.REMOVE, "oppositeDirection" : true, "depth" : 139.7 * mm});
        }
        {
            var Q0;
            {var subQ0=sQuery(id+"F2.wireOp",EDGE,"E93.right");Q0=makeQuery(id+"F7.boolean.opBoolean","MERGE",FACE,{"derivedFrom":[makeQuery(id+"F3.opExtrude","SWEPT_FACE",FACE,{"disambiguationData":[OSD([subQ0])]}),makeQuery(id+"F7.opExtrude","SWEPT_FACE",FACE,{"disambiguationData":[OSD([subQ0])]})]});}
            var sketch = newSketch(context, id + "F12", { "sketchPlane" : qUnion([Q0]) });
            skLineSegment(sketch, "E123.bottom", {"start": v(0, 2235.17) * mm, "end": v(139.7, 2235.17) * mm});
            skLineSegment(sketch, "E123.top", {"start": v(0, 2095.53) * mm, "end": v(139.7, 2095.53) * mm});
            skLineSegment(sketch, "E123.left", {"start": v(0, 2235.17) * mm, "end": v(0, 2095.53) * mm});
            skLineSegment(sketch, "E123.right", {"start": v(139.7, 2235.17) * mm, "end": v(139.7, 2095.53) * mm});
            skSolve(sketch);
        }
        {
            var Q0;
            Q0 = qSketchRegion(id + "F12", true);
            var Q1;
            {var subQ0=sQuery(id+"F2.wireOp",EDGE,"E92.left");Q1=makeQuery(id+"F7.boolean.opBoolean","MERGE",FACE,{"derivedFrom":[makeQuery(id+"F3.opExtrude","SWEPT_FACE",FACE,{"disambiguationData":[OSD([subQ0])]}),makeQuery(id+"F7.opExtrude","SWEPT_FACE",FACE,{"disambiguationData":[OSD([subQ0])]})]});}
            extrude(context, id + "F13", {"entities" : qUnion([Q0]), "operationType" : NewBodyOperationType.ADD, "endBound" : BoundingType.UP_TO_SURFACE, "endBoundEntityFace" : qUnion([Q1]), "depth" : 25.4 * mm});
        }
        {
            var Q0;
            {var subQ0=sQuery(id+"F2.wireOp",EDGE,"E76.bottom");var subQ1=sQuery(id+"F2.wireOp",EDGE,"E93.top");var subQ2=sQuery(id+"F2.wireOp",EDGE,"E92.top");var subQ3=sQuery(id+"F2.wireOp",EDGE,"E86.top");var subQ4=sQuery(id+"F2.wireOp",EDGE,"E81.23.0.3");var subQ5=sQuery(id+"F2.wireOp",EDGE,"E81.22.0.3");var subQ6=sQuery(id+"F2.wireOp",EDGE,"E81.21.0.3");var subQ7=sQuery(id+"F2.wireOp",EDGE,"E81.20.0.3");var subQ8=sQuery(id+"F2.wireOp",EDGE,"E81.19.0.3");var subQ9=sQuery(id+"F2.wireOp",EDGE,"E81.18.0.3");var subQ10=sQuery(id+"F2.wireOp",EDGE,"E81.17.0.3");var subQ11=sQuery(id+"F2.wireOp",EDGE,"E81.16.0.3");var subQ12=sQuery(id+"F2.wireOp",EDGE,"E81.15.0.3");var subQ13=sQuery(id+"F2.wireOp",EDGE,"E81.14.0.3");var subQ14=sQuery(id+"F2.wireOp",EDGE,"E81.13.0.3");var subQ15=sQuery(id+"F2.wireOp",EDGE,"E81.12.0.3");var subQ16=sQuery(id+"F2.wireOp",EDGE,"E81.11.0.3");var subQ17=sQuery(id+"F2.wireOp",EDGE,"E81.10.0.3");var subQ18=sQuery(id+"F2.wireOp",EDGE,"E81.9.0.3");var subQ19=sQuery(id+"F2.wireOp",EDGE,"E81.8.0.3");var subQ20=sQuery(id+"F2.wireOp",EDGE,"E81.7.0.3");var subQ21=sQuery(id+"F2.wireOp",EDGE,"E81.6.0.3");var subQ22=sQuery(id+"F2.wireOp",EDGE,"E81.5.0.3");var subQ23=sQuery(id+"F2.wireOp",EDGE,"E81.4.0.3");var subQ24=sQuery(id+"F2.wireOp",EDGE,"E81.3.0.3");var subQ25=sQuery(id+"F2.wireOp",EDGE,"E81.2.0.3");var subQ26=sQuery(id+"F2.wireOp",EDGE,"E81.1.0.3");var subQ27=sQuery(id+"F2.wireOp",EDGE,"E80.top");Q0=makeQuery(id+"F13.boolean.opBoolean","MERGE",FACE,{"derivedFrom":[makeQuery(id+"F9.boolean.opBoolean","MERGE",FACE,{"derivedFrom":[makeQuery(id+"F7.boolean.opBoolean","MERGE",FACE,{"derivedFrom":[makeQuery(id+"F5.boolean.opBoolean","MERGE",FACE,{"derivedFrom":[makeQuery(id+"F3.boolean.opBoolean","MERGE",FACE,{"derivedFrom":[makeQuery(id+"F1.opExtrude","SWEPT_FACE",FACE,{"disambiguationData":[OSD([sQuery(id+"F0.wireOp",EDGE,"E0")])]}),makeQuery(id+"F3.opExtrude","SWEPT_FACE",FACE,{"disambiguationData":[OSD([subQ0])]}),makeQuery(id+"F3.opExtrude","SWEPT_FACE",FACE,{"disambiguationData":[OSD([sQuery(id+"F2.wireOp",EDGE,"E78.bottom")])]}),makeQuery(id+"F3.opExtrude","SWEPT_FACE",FACE,{"disambiguationData":[OSD([subQ27])]}),makeQuery(id+"F3.opExtrude","SWEPT_FACE",FACE,{"disambiguationData":[OSD([subQ26])]}),makeQuery(id+"F3.opExtrude","SWEPT_FACE",FACE,{"disambiguationData":[OSD([subQ25])]}),makeQuery(id+"F3.opExtrude","SWEPT_FACE",FACE,{"disambiguationData":[OSD([subQ24])]}),makeQuery(id+"F3.opExtrude","SWEPT_FACE",FACE,{"disambiguationData":[OSD([subQ23])]}),makeQuery(id+"F3.opExtrude","SWEPT_FACE",FACE,{"disambiguationData":[OSD([subQ22])]}),makeQuery(id+"F3.opExtrude","SWEPT_FACE",FACE,{"disambiguationData":[OSD([subQ21])]}),makeQuery(id+"F3.opExtrude","SWEPT_FACE",FACE,{"disambiguationData":[OSD([subQ20])]}),makeQuery(id+"F3.opExtrude","SWEPT_FACE",FACE,{"disambiguationData":[OSD([subQ19])]}),makeQuery(id+"F3.opExtrude","SWEPT_FACE",FACE,{"disambiguationData":[OSD([subQ18])]}),makeQuery(id+"F3.opExtrude","SWEPT_FACE",FACE,{"disambiguationData":[OSD([subQ17])]}),makeQuery(id+"F3.opExtrude","SWEPT_FACE",FACE,{"disambiguationData":[OSD([subQ16])]}),makeQuery(id+"F3.opExtrude","SWEPT_FACE",FACE,{"disambiguationData":[OSD([subQ15])]}),makeQuery(id+"F3.opExtrude","SWEPT_FACE",FACE,{"disambiguationData":[OSD([subQ14])]}),makeQuery(id+"F3.opExtrude","SWEPT_FACE",FACE,{"disambiguationData":[OSD([subQ13])]}),makeQuery(id+"F3.opExtrude","SWEPT_FACE",FACE,{"disambiguationData":[OSD([subQ12])]}),makeQuery(id+"F3.opExtrude","SWEPT_FACE",FACE,{"disambiguationData":[OSD([subQ11])]}),makeQuery(id+"F3.opExtrude","SWEPT_FACE",FACE,{"disambiguationData":[OSD([subQ10])]}),makeQuery(id+"F3.opExtrude","SWEPT_FACE",FACE,{"disambiguationData":[OSD([subQ9])]}),makeQuery(id+"F3.opExtrude","SWEPT_FACE",FACE,{"disambiguationData":[OSD([subQ8])]}),makeQuery(id+"F3.opExtrude","SWEPT_FACE",FACE,{"disambiguationData":[OSD([subQ7])]}),makeQuery(id+"F3.opExtrude","SWEPT_FACE",FACE,{"disambiguationData":[OSD([subQ6])]}),makeQuery(id+"F3.opExtrude","SWEPT_FACE",FACE,{"disambiguationData":[OSD([subQ5])]}),makeQuery(id+"F3.opExtrude","SWEPT_FACE",FACE,{"disambiguationData":[OSD([subQ4])]}),makeQuery(id+"F3.opExtrude","SWEPT_FACE",FACE,{"disambiguationData":[OSD([sQuery(id+"F2.wireOp",EDGE,"E81.25.0.3")])]}),makeQuery(id+"F3.opExtrude","SWEPT_FACE",FACE,{"disambiguationData":[OSD([sQuery(id+"F2.wireOp",EDGE,"E81.26.0.3")])]}),makeQuery(id+"F3.opExtrude","SWEPT_FACE",FACE,{"disambiguationData":[OSD([sQuery(id+"F2.wireOp",EDGE,"E84.top")])]}),makeQuery(id+"F3.opExtrude","SWEPT_FACE",FACE,{"disambiguationData":[OSD([sQuery(id+"F2.wireOp",EDGE,"E85.top")])]}),makeQuery(id+"F3.opExtrude","SWEPT_FACE",FACE,{"disambiguationData":[OSD([subQ3])]}),makeQuery(id+"F3.opExtrude","SWEPT_FACE",FACE,{"disambiguationData":[OSD([sQuery(id+"F2.wireOp",EDGE,"E87.top")])]}),makeQuery(id+"F3.opExtrude","SWEPT_FACE",FACE,{"disambiguationData":[OSD([sQuery(id+"F2.wireOp",EDGE,"E88.top")])]}),makeQuery(id+"F3.opExtrude","SWEPT_FACE",FACE,{"disambiguationData":[OSD([sQuery(id+"F2.wireOp",EDGE,"E89.top")])]}),makeQuery(id+"F3.opExtrude","SWEPT_FACE",FACE,{"disambiguationData":[OSD([sQuery(id+"F2.wireOp",EDGE,"E90.top")])]}),makeQuery(id+"F3.opExtrude","SWEPT_FACE",FACE,{"disambiguationData":[OSD([sQuery(id+"F2.wireOp",EDGE,"E91.top")])]}),makeQuery(id+"F3.opExtrude","SWEPT_FACE",FACE,{"disambiguationData":[OSD([subQ2])]}),makeQuery(id+"F3.opExtrude","SWEPT_FACE",FACE,{"disambiguationData":[OSD([subQ1])]}),makeQuery(id+"F3.opExtrude","SWEPT_FACE",FACE,{"disambiguationData":[OSD([sQuery(id+"F2.wireOp",EDGE,"E94.top")])]}),makeQuery(id+"F3.opExtrude","SWEPT_FACE",FACE,{"disambiguationData":[OSD([sQuery(id+"F2.wireOp",EDGE,"E95.top")])]}),makeQuery(id+"F3.opExtrude","SWEPT_FACE",FACE,{"disambiguationData":[OSD([sQuery(id+"F2.wireOp",EDGE,"E96.top")])]}),makeQuery(id+"F3.opExtrude","SWEPT_FACE",FACE,{"disambiguationData":[OSD([sQuery(id+"F2.wireOp",EDGE,"E97.top")])]}),makeQuery(id+"F3.opExtrude","SWEPT_FACE",FACE,{"disambiguationData":[OSD([sQuery(id+"F2.wireOp",EDGE,"E98.top")])]}),makeQuery(id+"F3.opExtrude","SWEPT_FACE",FACE,{"disambiguationData":[OSD([sQuery(id+"F2.wireOp",EDGE,"E99.top")])]}),makeQuery(id+"F3.opExtrude","SWEPT_FACE",FACE,{"disambiguationData":[OSD([sQuery(id+"F2.wireOp",EDGE,"E100.top")])]}),makeQuery(id+"F3.opExtrude","SWEPT_FACE",FACE,{"disambiguationData":[OSD([sQuery(id+"F2.wireOp",EDGE,"E101.top")])]})]}),makeQuery(id+"F5.opExtrude","SWEPT_FACE",FACE,{"disambiguationData":[OSD([sQuery(id+"F4.wireOp",EDGE,"E110.bottom")])]})]}),makeQuery(id+"F7.opExtrude","SWEPT_FACE",FACE,{"disambiguationData":[OSD([subQ27])]}),makeQuery(id+"F7.opExtrude","SWEPT_FACE",FACE,{"disambiguationData":[OSD([subQ26])]}),makeQuery(id+"F7.opExtrude","SWEPT_FACE",FACE,{"disambiguationData":[OSD([subQ25])]}),makeQuery(id+"F7.opExtrude","SWEPT_FACE",FACE,{"disambiguationData":[OSD([subQ24])]}),makeQuery(id+"F7.opExtrude","SWEPT_FACE",FACE,{"disambiguationData":[OSD([subQ23])]}),makeQuery(id+"F7.opExtrude","SWEPT_FACE",FACE,{"disambiguationData":[OSD([subQ22])]}),makeQuery(id+"F7.opExtrude","SWEPT_FACE",FACE,{"disambiguationData":[OSD([subQ21])]}),makeQuery(id+"F7.opExtrude","SWEPT_FACE",FACE,{"disambiguationData":[OSD([subQ20])]}),makeQuery(id+"F7.opExtrude","SWEPT_FACE",FACE,{"disambiguationData":[OSD([subQ19])]}),makeQuery(id+"F7.opExtrude","SWEPT_FACE",FACE,{"disambiguationData":[OSD([subQ18])]}),makeQuery(id+"F7.opExtrude","SWEPT_FACE",FACE,{"disambiguationData":[OSD([subQ17])]}),makeQuery(id+"F7.opExtrude","SWEPT_FACE",FACE,{"disambiguationData":[OSD([subQ16])]}),makeQuery(id+"F7.opExtrude","SWEPT_FACE",FACE,{"disambiguationData":[OSD([subQ15])]}),makeQuery(id+"F7.opExtrude","SWEPT_FACE",FACE,{"disambiguationData":[OSD([subQ14])]}),makeQuery(id+"F7.opExtrude","SWEPT_FACE",FACE,{"disambiguationData":[OSD([subQ13])]}),makeQuery(id+"F7.opExtrude","SWEPT_FACE",FACE,{"disambiguationData":[OSD([subQ12])]}),makeQuery(id+"F7.opExtrude","SWEPT_FACE",FACE,{"disambiguationData":[OSD([subQ11])]}),makeQuery(id+"F7.opExtrude","SWEPT_FACE",FACE,{"disambiguationData":[OSD([subQ10])]}),makeQuery(id+"F7.opExtrude","SWEPT_FACE",FACE,{"disambiguationData":[OSD([subQ9])]}),makeQuery(id+"F7.opExtrude","SWEPT_FACE",FACE,{"disambiguationData":[OSD([subQ8])]}),makeQuery(id+"F7.opExtrude","SWEPT_FACE",FACE,{"disambiguationData":[OSD([subQ7])]}),makeQuery(id+"F7.opExtrude","SWEPT_FACE",FACE,{"disambiguationData":[OSD([subQ6])]}),makeQuery(id+"F7.opExtrude","SWEPT_FACE",FACE,{"disambiguationData":[OSD([subQ5])]}),makeQuery(id+"F7.opExtrude","SWEPT_FACE",FACE,{"disambiguationData":[OSD([subQ4])]}),makeQuery(id+"F7.opExtrude","SWEPT_FACE",FACE,{"disambiguationData":[OSD([subQ3])]}),makeQuery(id+"F7.opExtrude","SWEPT_FACE",FACE,{"disambiguationData":[OSD([subQ2])]}),makeQuery(id+"F7.opExtrude","SWEPT_FACE",FACE,{"disambiguationData":[OSD([subQ1])]}),makeQuery(id+"F7.opExtrude","SWEPT_FACE",FACE,{"disambiguationData":[OSD([subQ0])]})]}),makeQuery(id+"F9.opExtrude","SWEPT_FACE",FACE,{"disambiguationData":[OSD([sQuery(id+"F8.wireOp",EDGE,"E112.top")])]})]}),makeQuery(id+"F13.opExtrude","SWEPT_FACE",FACE,{"disambiguationData":[OSD([sQuery(id+"F12.wireOp",EDGE,"E123.left")])]})]});}
            var sketch = newSketch(context, id + "F14", { "sketchPlane" : qUnion([Q0]) });
            skLineSegment(sketch, "E124", {"start": v(-9804.43, 2184.4) * mm, "end": v(-9804.43, 2095.5) * mm});
            skLineSegment(sketch, "E125", {"start": v(-9804.43, 2095.5) * mm, "end": v(-9766.3, 2095.5) * mm});
            skLineSegment(sketch, "E126", {"start": v(-9766.3, 2095.5) * mm, "end": v(-9766.3, 876.3) * mm});
            skLineSegment(sketch, "E127", {"start": v(-9766.3, 876.3) * mm, "end": v(-7937.5, 876.3) * mm});
            skLineSegment(sketch, "E128", {"start": v(-7937.5, 876.3) * mm, "end": v(-7937.5, 2095.5) * mm});
            skLineSegment(sketch, "E129", {"start": v(-7937.5, 2095.5) * mm, "end": v(-7899.4, 2095.5) * mm});
            skLineSegment(sketch, "E130", {"start": v(-7899.4, 2095.5) * mm, "end": v(-7899.4, 2184.4) * mm});
            skLineSegment(sketch, "E131", {"start": v(-7899.4, 2184.4) * mm, "end": v(-9804.43, 2184.4) * mm});
            skLineSegment(sketch, "E132", {"start": v(-5543.55, 2184.4) * mm, "end": v(-5543.55, 2095.5) * mm});
            skLineSegment(sketch, "E133", {"start": v(-5543.55, 2095.5) * mm, "end": v(-5505.42, 2095.5) * mm});
            skLineSegment(sketch, "E134", {"start": v(-5505.42, 2095.5) * mm, "end": v(-5505.42, 876.3) * mm});
            skLineSegment(sketch, "E135", {"start": v(-5505.42, 876.3) * mm, "end": v(-3676.62, 876.3) * mm});
            skLineSegment(sketch, "E136", {"start": v(-3676.62, 876.3) * mm, "end": v(-3676.62, 2095.5) * mm});
            skLineSegment(sketch, "E137", {"start": v(-3676.62, 2095.5) * mm, "end": v(-3638.52, 2095.5) * mm});
            skLineSegment(sketch, "E138", {"start": v(-3638.52, 2095.5) * mm, "end": v(-3638.52, 2184.4) * mm});
            skLineSegment(sketch, "E139", {"start": v(-3638.52, 2184.4) * mm, "end": v(-5543.55, 2184.4) * mm});
            skLineSegment(sketch, "E140", {"start": v(-9766.3, 3352.8) * mm, "end": v(-7937.5, 3352.8) * mm, "construction": true});
            skLineSegment(sketch, "E141", {"start": v(-7651.75, 3352.8) * mm, "end": v(-5791.17, 3352.8) * mm, "construction": true});
            skLineSegment(sketch, "E142", {"start": v(-5505.42, 3352.8) * mm, "end": v(-3676.62, 3352.8) * mm, "construction": true});
            skLineSegment(sketch, "E143", {"start": v(-9766.3, 3352.8) * mm, "end": v(-9766.3, 4741.36) * mm, "construction": true});
            skLineSegment(sketch, "E144", {"start": v(-3676.62, 3352.8) * mm, "end": v(-3676.62, 4741.36) * mm, "construction": true});
            skLineSegment(sketch, "E145", {"start": v(-9766.3, 4741.36) * mm, "end": v(-9842.53, 4741.36) * mm, "construction": true});
            skLineSegment(sketch, "E146", {"start": v(-9842.53, 4741.36) * mm, "end": v(-9842.53, 5178.43) * mm, "construction": true});
            skLineSegment(sketch, "E147", {"start": v(-9842.53, 5178.43) * mm, "end": v(-9766.3, 5178.43) * mm, "construction": true});
            skLineSegment(sketch, "E148", {"start": v(-9766.3, 5178.43) * mm, "end": v(-9766.3, 4925.5) * mm, "construction": true});
            skLineSegment(sketch, "E149", {"start": v(-9766.3, 4925.5) * mm, "end": v(-7937.5, 4925.5) * mm, "construction": true});
            skLineSegment(sketch, "E150", {"start": v(-7937.5, 4925.5) * mm, "end": v(-7937.5, 5178.43) * mm, "construction": true});
            skLineSegment(sketch, "E151", {"start": v(-7937.5, 5178.43) * mm, "end": v(-7861.3, 5178.43) * mm, "construction": true});
            skLineSegment(sketch, "E152", {"start": v(-7861.3, 5178.43) * mm, "end": v(-7861.3, 4741.36) * mm, "construction": true});
            skLineSegment(sketch, "E153", {"start": v(-7861.3, 4741.36) * mm, "end": v(-7937.5, 4741.36) * mm, "construction": true});
            skLineSegment(sketch, "E154", {"start": v(-7937.5, 4741.36) * mm, "end": v(-7937.5, 3352.8) * mm, "construction": true});
            skLineSegment(sketch, "E155", {"start": v(-5791.17, 3352.8) * mm, "end": v(-5791.17, 4876.8) * mm, "construction": true});
            skLineSegment(sketch, "E156", {"start": v(-5791.17, 4876.8) * mm, "end": v(-5714.97, 4876.8) * mm, "construction": true});
            skLineSegment(sketch, "E157", {"start": v(-5714.97, 4876.8) * mm, "end": v(-5714.97, 5178.43) * mm, "construction": true});
            skLineSegment(sketch, "E158", {"start": v(-5714.97, 5178.43) * mm, "end": v(-5791.17, 5178.43) * mm, "construction": true});
            skLineSegment(sketch, "E159", {"start": v(-5791.17, 5178.43) * mm, "end": v(-5791.17, 5060.95) * mm, "construction": true});
            skLineSegment(sketch, "E160", {"start": v(-5791.17, 5060.95) * mm, "end": v(-7651.75, 5060.95) * mm, "construction": true});
            skLineSegment(sketch, "E161", {"start": v(-7651.75, 5060.95) * mm, "end": v(-7651.75, 5178.43) * mm, "construction": true});
            skLineSegment(sketch, "E162", {"start": v(-7651.75, 5178.43) * mm, "end": v(-7727.95, 5178.43) * mm, "construction": true});
            skLineSegment(sketch, "E163", {"start": v(-7727.95, 5178.43) * mm, "end": v(-7727.95, 4876.8) * mm, "construction": true});
            skLineSegment(sketch, "E164", {"start": v(-7727.95, 4876.8) * mm, "end": v(-7651.75, 4876.8) * mm, "construction": true});
            skLineSegment(sketch, "E165", {"start": v(-7651.75, 4876.8) * mm, "end": v(-7651.75, 3352.8) * mm, "construction": true});
            skLineSegment(sketch, "E166", {"start": v(-3676.62, 4741.36) * mm, "end": v(-3600.42, 4741.36) * mm, "construction": true});
            skLineSegment(sketch, "E167", {"start": v(-3600.42, 4741.36) * mm, "end": v(-3600.42, 5178.43) * mm, "construction": true});
            skLineSegment(sketch, "E168", {"start": v(-3600.42, 5178.43) * mm, "end": v(-3676.62, 5178.43) * mm, "construction": true});
            skLineSegment(sketch, "E169", {"start": v(-3676.62, 5178.43) * mm, "end": v(-3676.62, 4925.5) * mm, "construction": true});
            skLineSegment(sketch, "E170", {"start": v(-3676.62, 4925.5) * mm, "end": v(-5505.42, 4925.5) * mm, "construction": true});
            skLineSegment(sketch, "E171", {"start": v(-5505.42, 4925.5) * mm, "end": v(-5505.42, 5178.43) * mm, "construction": true});
            skLineSegment(sketch, "E172", {"start": v(-5505.42, 5178.43) * mm, "end": v(-5581.65, 5178.43) * mm, "construction": true});
            skLineSegment(sketch, "E173", {"start": v(-5581.65, 5178.43) * mm, "end": v(-5581.65, 4741.36) * mm, "construction": true});
            skLineSegment(sketch, "E174", {"start": v(-5581.65, 4741.36) * mm, "end": v(-5505.42, 4741.36) * mm, "construction": true});
            skLineSegment(sketch, "E175", {"start": v(-5505.42, 4741.36) * mm, "end": v(-5505.42, 3352.8) * mm, "construction": true});
            skArc(sketch, "E176", {"start": v(-3676.62, 3962.4) * mm, "mid": v(-6721.46, 4876.8) * mm, "end": v(-9766.3, 3962.4) * mm, "construction": true});
            skLineSegment(sketch, "E177", {"start": v(-7651.75, 4876.8) * mm, "end": v(-5791.17, 4876.8) * mm, "construction": true});
            skSolve(sketch);
        }
        {
            var Q0;
            Q0 = qSketchRegion(id + "F14", true);
            extrude(context, id + "F15", {"entities" : qUnion([Q0]), "operationType" : NewBodyOperationType.REMOVE, "oppositeDirection" : true, "depth" : 139.7 * mm});
        }
        {
            var Q0;
            {var subQ0=sQuery(id+"F2.wireOp",EDGE,"E76.bottom");var subQ1=sQuery(id+"F2.wireOp",EDGE,"E93.top");var subQ2=sQuery(id+"F2.wireOp",EDGE,"E92.top");var subQ3=sQuery(id+"F2.wireOp",EDGE,"E86.top");var subQ4=sQuery(id+"F2.wireOp",EDGE,"E81.23.0.3");var subQ5=sQuery(id+"F2.wireOp",EDGE,"E81.22.0.3");var subQ6=sQuery(id+"F2.wireOp",EDGE,"E81.21.0.3");var subQ7=sQuery(id+"F2.wireOp",EDGE,"E81.20.0.3");var subQ8=sQuery(id+"F2.wireOp",EDGE,"E81.19.0.3");var subQ9=sQuery(id+"F2.wireOp",EDGE,"E81.18.0.3");var subQ10=sQuery(id+"F2.wireOp",EDGE,"E81.17.0.3");var subQ11=sQuery(id+"F2.wireOp",EDGE,"E81.16.0.3");var subQ12=sQuery(id+"F2.wireOp",EDGE,"E81.15.0.3");var subQ13=sQuery(id+"F2.wireOp",EDGE,"E81.14.0.3");var subQ14=sQuery(id+"F2.wireOp",EDGE,"E81.13.0.3");var subQ15=sQuery(id+"F2.wireOp",EDGE,"E81.12.0.3");var subQ16=sQuery(id+"F2.wireOp",EDGE,"E81.11.0.3");var subQ17=sQuery(id+"F2.wireOp",EDGE,"E81.10.0.3");var subQ18=sQuery(id+"F2.wireOp",EDGE,"E81.9.0.3");var subQ19=sQuery(id+"F2.wireOp",EDGE,"E81.8.0.3");var subQ20=sQuery(id+"F2.wireOp",EDGE,"E81.7.0.3");var subQ21=sQuery(id+"F2.wireOp",EDGE,"E81.6.0.3");var subQ22=sQuery(id+"F2.wireOp",EDGE,"E81.5.0.3");var subQ23=sQuery(id+"F2.wireOp",EDGE,"E81.4.0.3");var subQ24=sQuery(id+"F2.wireOp",EDGE,"E81.3.0.3");var subQ25=sQuery(id+"F2.wireOp",EDGE,"E81.2.0.3");var subQ26=sQuery(id+"F2.wireOp",EDGE,"E81.1.0.3");var subQ27=sQuery(id+"F2.wireOp",EDGE,"E80.top");Q0=makeQuery(id+"F13.boolean.opBoolean","MERGE",FACE,{"derivedFrom":[makeQuery(id+"F9.boolean.opBoolean","MERGE",FACE,{"derivedFrom":[makeQuery(id+"F7.boolean.opBoolean","MERGE",FACE,{"derivedFrom":[makeQuery(id+"F5.boolean.opBoolean","MERGE",FACE,{"derivedFrom":[makeQuery(id+"F3.boolean.opBoolean","MERGE",FACE,{"derivedFrom":[makeQuery(id+"F1.opExtrude","SWEPT_FACE",FACE,{"disambiguationData":[OSD([sQuery(id+"F0.wireOp",EDGE,"E0")])]}),makeQuery(id+"F3.opExtrude","SWEPT_FACE",FACE,{"disambiguationData":[OSD([subQ0])]}),makeQuery(id+"F3.opExtrude","SWEPT_FACE",FACE,{"disambiguationData":[OSD([sQuery(id+"F2.wireOp",EDGE,"E78.bottom")])]}),makeQuery(id+"F3.opExtrude","SWEPT_FACE",FACE,{"disambiguationData":[OSD([subQ27])]}),makeQuery(id+"F3.opExtrude","SWEPT_FACE",FACE,{"disambiguationData":[OSD([subQ26])]}),makeQuery(id+"F3.opExtrude","SWEPT_FACE",FACE,{"disambiguationData":[OSD([subQ25])]}),makeQuery(id+"F3.opExtrude","SWEPT_FACE",FACE,{"disambiguationData":[OSD([subQ24])]}),makeQuery(id+"F3.opExtrude","SWEPT_FACE",FACE,{"disambiguationData":[OSD([subQ23])]}),makeQuery(id+"F3.opExtrude","SWEPT_FACE",FACE,{"disambiguationData":[OSD([subQ22])]}),makeQuery(id+"F3.opExtrude","SWEPT_FACE",FACE,{"disambiguationData":[OSD([subQ21])]}),makeQuery(id+"F3.opExtrude","SWEPT_FACE",FACE,{"disambiguationData":[OSD([subQ20])]}),makeQuery(id+"F3.opExtrude","SWEPT_FACE",FACE,{"disambiguationData":[OSD([subQ19])]}),makeQuery(id+"F3.opExtrude","SWEPT_FACE",FACE,{"disambiguationData":[OSD([subQ18])]}),makeQuery(id+"F3.opExtrude","SWEPT_FACE",FACE,{"disambiguationData":[OSD([subQ17])]}),makeQuery(id+"F3.opExtrude","SWEPT_FACE",FACE,{"disambiguationData":[OSD([subQ16])]}),makeQuery(id+"F3.opExtrude","SWEPT_FACE",FACE,{"disambiguationData":[OSD([subQ15])]}),makeQuery(id+"F3.opExtrude","SWEPT_FACE",FACE,{"disambiguationData":[OSD([subQ14])]}),makeQuery(id+"F3.opExtrude","SWEPT_FACE",FACE,{"disambiguationData":[OSD([subQ13])]}),makeQuery(id+"F3.opExtrude","SWEPT_FACE",FACE,{"disambiguationData":[OSD([subQ12])]}),makeQuery(id+"F3.opExtrude","SWEPT_FACE",FACE,{"disambiguationData":[OSD([subQ11])]}),makeQuery(id+"F3.opExtrude","SWEPT_FACE",FACE,{"disambiguationData":[OSD([subQ10])]}),makeQuery(id+"F3.opExtrude","SWEPT_FACE",FACE,{"disambiguationData":[OSD([subQ9])]}),makeQuery(id+"F3.opExtrude","SWEPT_FACE",FACE,{"disambiguationData":[OSD([subQ8])]}),makeQuery(id+"F3.opExtrude","SWEPT_FACE",FACE,{"disambiguationData":[OSD([subQ7])]}),makeQuery(id+"F3.opExtrude","SWEPT_FACE",FACE,{"disambiguationData":[OSD([subQ6])]}),makeQuery(id+"F3.opExtrude","SWEPT_FACE",FACE,{"disambiguationData":[OSD([subQ5])]}),makeQuery(id+"F3.opExtrude","SWEPT_FACE",FACE,{"disambiguationData":[OSD([subQ4])]}),makeQuery(id+"F3.opExtrude","SWEPT_FACE",FACE,{"disambiguationData":[OSD([sQuery(id+"F2.wireOp",EDGE,"E81.25.0.3")])]}),makeQuery(id+"F3.opExtrude","SWEPT_FACE",FACE,{"disambiguationData":[OSD([sQuery(id+"F2.wireOp",EDGE,"E81.26.0.3")])]}),makeQuery(id+"F3.opExtrude","SWEPT_FACE",FACE,{"disambiguationData":[OSD([sQuery(id+"F2.wireOp",EDGE,"E84.top")])]}),makeQuery(id+"F3.opExtrude","SWEPT_FACE",FACE,{"disambiguationData":[OSD([sQuery(id+"F2.wireOp",EDGE,"E85.top")])]}),makeQuery(id+"F3.opExtrude","SWEPT_FACE",FACE,{"disambiguationData":[OSD([subQ3])]}),makeQuery(id+"F3.opExtrude","SWEPT_FACE",FACE,{"disambiguationData":[OSD([sQuery(id+"F2.wireOp",EDGE,"E87.top")])]}),makeQuery(id+"F3.opExtrude","SWEPT_FACE",FACE,{"disambiguationData":[OSD([sQuery(id+"F2.wireOp",EDGE,"E88.top")])]}),makeQuery(id+"F3.opExtrude","SWEPT_FACE",FACE,{"disambiguationData":[OSD([sQuery(id+"F2.wireOp",EDGE,"E89.top")])]}),makeQuery(id+"F3.opExtrude","SWEPT_FACE",FACE,{"disambiguationData":[OSD([sQuery(id+"F2.wireOp",EDGE,"E90.top")])]}),makeQuery(id+"F3.opExtrude","SWEPT_FACE",FACE,{"disambiguationData":[OSD([sQuery(id+"F2.wireOp",EDGE,"E91.top")])]}),makeQuery(id+"F3.opExtrude","SWEPT_FACE",FACE,{"disambiguationData":[OSD([subQ2])]}),makeQuery(id+"F3.opExtrude","SWEPT_FACE",FACE,{"disambiguationData":[OSD([subQ1])]}),makeQuery(id+"F3.opExtrude","SWEPT_FACE",FACE,{"disambiguationData":[OSD([sQuery(id+"F2.wireOp",EDGE,"E94.top")])]}),makeQuery(id+"F3.opExtrude","SWEPT_FACE",FACE,{"disambiguationData":[OSD([sQuery(id+"F2.wireOp",EDGE,"E95.top")])]}),makeQuery(id+"F3.opExtrude","SWEPT_FACE",FACE,{"disambiguationData":[OSD([sQuery(id+"F2.wireOp",EDGE,"E96.top")])]}),makeQuery(id+"F3.opExtrude","SWEPT_FACE",FACE,{"disambiguationData":[OSD([sQuery(id+"F2.wireOp",EDGE,"E97.top")])]}),makeQuery(id+"F3.opExtrude","SWEPT_FACE",FACE,{"disambiguationData":[OSD([sQuery(id+"F2.wireOp",EDGE,"E98.top")])]}),makeQuery(id+"F3.opExtrude","SWEPT_FACE",FACE,{"disambiguationData":[OSD([sQuery(id+"F2.wireOp",EDGE,"E99.top")])]}),makeQuery(id+"F3.opExtrude","SWEPT_FACE",FACE,{"disambiguationData":[OSD([sQuery(id+"F2.wireOp",EDGE,"E100.top")])]}),makeQuery(id+"F3.opExtrude","SWEPT_FACE",FACE,{"disambiguationData":[OSD([sQuery(id+"F2.wireOp",EDGE,"E101.top")])]})]}),makeQuery(id+"F5.opExtrude","SWEPT_FACE",FACE,{"disambiguationData":[OSD([sQuery(id+"F4.wireOp",EDGE,"E110.bottom")])]})]}),makeQuery(id+"F7.opExtrude","SWEPT_FACE",FACE,{"disambiguationData":[OSD([subQ27])]}),makeQuery(id+"F7.opExtrude","SWEPT_FACE",FACE,{"disambiguationData":[OSD([subQ26])]}),makeQuery(id+"F7.opExtrude","SWEPT_FACE",FACE,{"disambiguationData":[OSD([subQ25])]}),makeQuery(id+"F7.opExtrude","SWEPT_FACE",FACE,{"disambiguationData":[OSD([subQ24])]}),makeQuery(id+"F7.opExtrude","SWEPT_FACE",FACE,{"disambiguationData":[OSD([subQ23])]}),makeQuery(id+"F7.opExtrude","SWEPT_FACE",FACE,{"disambiguationData":[OSD([subQ22])]}),makeQuery(id+"F7.opExtrude","SWEPT_FACE",FACE,{"disambiguationData":[OSD([subQ21])]}),makeQuery(id+"F7.opExtrude","SWEPT_FACE",FACE,{"disambiguationData":[OSD([subQ20])]}),makeQuery(id+"F7.opExtrude","SWEPT_FACE",FACE,{"disambiguationData":[OSD([subQ19])]}),makeQuery(id+"F7.opExtrude","SWEPT_FACE",FACE,{"disambiguationData":[OSD([subQ18])]}),makeQuery(id+"F7.opExtrude","SWEPT_FACE",FACE,{"disambiguationData":[OSD([subQ17])]}),makeQuery(id+"F7.opExtrude","SWEPT_FACE",FACE,{"disambiguationData":[OSD([subQ16])]}),makeQuery(id+"F7.opExtrude","SWEPT_FACE",FACE,{"disambiguationData":[OSD([subQ15])]}),makeQuery(id+"F7.opExtrude","SWEPT_FACE",FACE,{"disambiguationData":[OSD([subQ14])]}),makeQuery(id+"F7.opExtrude","SWEPT_FACE",FACE,{"disambiguationData":[OSD([subQ13])]}),makeQuery(id+"F7.opExtrude","SWEPT_FACE",FACE,{"disambiguationData":[OSD([subQ12])]}),makeQuery(id+"F7.opExtrude","SWEPT_FACE",FACE,{"disambiguationData":[OSD([subQ11])]}),makeQuery(id+"F7.opExtrude","SWEPT_FACE",FACE,{"disambiguationData":[OSD([subQ10])]}),makeQuery(id+"F7.opExtrude","SWEPT_FACE",FACE,{"disambiguationData":[OSD([subQ9])]}),makeQuery(id+"F7.opExtrude","SWEPT_FACE",FACE,{"disambiguationData":[OSD([subQ8])]}),makeQuery(id+"F7.opExtrude","SWEPT_FACE",FACE,{"disambiguationData":[OSD([subQ7])]}),makeQuery(id+"F7.opExtrude","SWEPT_FACE",FACE,{"disambiguationData":[OSD([subQ6])]}),makeQuery(id+"F7.opExtrude","SWEPT_FACE",FACE,{"disambiguationData":[OSD([subQ5])]}),makeQuery(id+"F7.opExtrude","SWEPT_FACE",FACE,{"disambiguationData":[OSD([subQ4])]}),makeQuery(id+"F7.opExtrude","SWEPT_FACE",FACE,{"disambiguationData":[OSD([subQ3])]}),makeQuery(id+"F7.opExtrude","SWEPT_FACE",FACE,{"disambiguationData":[OSD([subQ2])]}),makeQuery(id+"F7.opExtrude","SWEPT_FACE",FACE,{"disambiguationData":[OSD([subQ1])]}),makeQuery(id+"F7.opExtrude","SWEPT_FACE",FACE,{"disambiguationData":[OSD([subQ0])]})]}),makeQuery(id+"F9.opExtrude","SWEPT_FACE",FACE,{"disambiguationData":[OSD([sQuery(id+"F8.wireOp",EDGE,"E112.top")])]})]}),makeQuery(id+"F13.opExtrude","SWEPT_FACE",FACE,{"disambiguationData":[OSD([sQuery(id+"F12.wireOp",EDGE,"E123.left")])]})]});}
            var sketch = newSketch(context, id + "F16", { "sketchPlane" : qUnion([Q0]) });
            skLineSegment(sketch, "E178.bottom", {"start": v(-9804.43, 2184.4) * mm, "end": v(-7899.37, 2184.4) * mm});
            skLineSegment(sketch, "E178.top", {"start": v(-9804.43, 2095.53) * mm, "end": v(-7899.37, 2095.53) * mm});
            skLineSegment(sketch, "E178.left", {"start": v(-9804.43, 2184.4) * mm, "end": v(-9804.43, 2095.53) * mm});
            skLineSegment(sketch, "E178.right", {"start": v(-7899.37, 2184.4) * mm, "end": v(-7899.37, 2095.53) * mm});
            skLineSegment(sketch, "E179.bottom", {"start": v(-5543.55, 2184.4) * mm, "end": v(-3638.5, 2184.4) * mm});
            skLineSegment(sketch, "E179.top", {"start": v(-5543.55, 2095.53) * mm, "end": v(-3638.5, 2095.53) * mm});
            skLineSegment(sketch, "E179.left", {"start": v(-5543.55, 2184.4) * mm, "end": v(-5543.55, 2095.53) * mm});
            skLineSegment(sketch, "E179.right", {"start": v(-3638.5, 2184.4) * mm, "end": v(-3638.5, 2095.53) * mm});
            skLineSegment(sketch, "E180.bottom", {"start": v(-9766.3, 838.2) * mm, "end": v(-7937.5, 838.2) * mm});
            skLineSegment(sketch, "E180.top", {"start": v(-9766.3, 876.3) * mm, "end": v(-7937.5, 876.3) * mm});
            skLineSegment(sketch, "E180.left", {"start": v(-9766.3, 838.2) * mm, "end": v(-9766.3, 876.3) * mm});
            skLineSegment(sketch, "E180.right", {"start": v(-7937.5, 838.2) * mm, "end": v(-7937.5, 876.3) * mm});
            skLineSegment(sketch, "E181.bottom", {"start": v(-5505.42, 838.2) * mm, "end": v(-3676.62, 838.2) * mm});
            skLineSegment(sketch, "E181.top", {"start": v(-5505.42, 876.3) * mm, "end": v(-3676.62, 876.3) * mm});
            skLineSegment(sketch, "E181.left", {"start": v(-5505.42, 838.2) * mm, "end": v(-5505.42, 876.3) * mm});
            skLineSegment(sketch, "E181.right", {"start": v(-3676.62, 838.2) * mm, "end": v(-3676.62, 876.3) * mm});
            skSolve(sketch);
        }
        {
            var Q0;
            Q0 = qSketchRegion(id + "F16", true);
            extrude(context, id + "F17", {"entities" : qUnion([Q0]), "operationType" : NewBodyOperationType.ADD, "oppositeDirection" : true, "depth" : 139.7 * mm});
        }
        {
            var Q0;
            {var subQ170=sQuery(id+"F14.wireOp",EDGE,"E124");Q0=makeQuery(id+"F14.imprint","IMPRINT",FACE,{"disambiguationData":[TD([[makeQuery(id+"F14.imprint","IMPRINT",EDGE,{"derivedFrom":subQ170}),-1.0]])]});}
            var sketch = newSketch(context, id + "F18", { "sketchPlane" : qUnion([Q0]) });
            skLineSegment(sketch, "E182.0", {"start": v(-9766.3, 4925.5) * mm, "end": v(-7937.5, 4925.5) * mm});
            skLineSegment(sketch, "E182.1", {"start": v(-9766.3, 5178.43) * mm, "end": v(-9766.3, 4925.5) * mm});
            skLineSegment(sketch, "E182.2", {"start": v(-9842.53, 5178.43) * mm, "end": v(-9766.3, 5178.43) * mm});
            skLineSegment(sketch, "E182.3", {"start": v(-9842.53, 4741.36) * mm, "end": v(-9842.53, 5178.43) * mm});
            skLineSegment(sketch, "E182.4", {"start": v(-9766.3, 4741.36) * mm, "end": v(-9842.53, 4741.36) * mm});
            skLineSegment(sketch, "E182.5", {"start": v(-9766.3, 3352.8) * mm, "end": v(-9766.3, 4741.36) * mm});
            skLineSegment(sketch, "E182.6", {"start": v(-9766.3, 3352.8) * mm, "end": v(-7937.5, 3352.8) * mm});
            skLineSegment(sketch, "E182.7", {"start": v(-7937.5, 4741.36) * mm, "end": v(-7937.5, 3352.8) * mm});
            skLineSegment(sketch, "E182.8", {"start": v(-7861.3, 4741.36) * mm, "end": v(-7937.5, 4741.36) * mm});
            skLineSegment(sketch, "E182.9", {"start": v(-7861.3, 5178.43) * mm, "end": v(-7861.3, 4741.36) * mm});
            skLineSegment(sketch, "E182.10", {"start": v(-7937.5, 5178.43) * mm, "end": v(-7861.3, 5178.43) * mm});
            skLineSegment(sketch, "E182.11", {"start": v(-7937.5, 4925.5) * mm, "end": v(-7937.5, 5178.43) * mm});
            skLineSegment(sketch, "E183.0", {"start": v(-7651.75, 5178.43) * mm, "end": v(-7727.95, 5178.43) * mm});
            skLineSegment(sketch, "E183.1", {"start": v(-7727.95, 5178.43) * mm, "end": v(-7727.95, 4876.8) * mm});
            skLineSegment(sketch, "E183.2", {"start": v(-7727.95, 4876.8) * mm, "end": v(-7651.75, 4876.8) * mm});
            skLineSegment(sketch, "E183.3", {"start": v(-7651.75, 5060.95) * mm, "end": v(-7651.75, 5178.43) * mm});
            skLineSegment(sketch, "E183.4", {"start": v(-5791.17, 5060.95) * mm, "end": v(-7651.75, 5060.95) * mm});
            skLineSegment(sketch, "E183.5", {"start": v(-7651.75, 4876.8) * mm, "end": v(-7651.75, 3352.8) * mm});
            skLineSegment(sketch, "E183.6", {"start": v(-7651.75, 3352.8) * mm, "end": v(-5791.17, 3352.8) * mm});
            skLineSegment(sketch, "E183.7", {"start": v(-5791.17, 3352.8) * mm, "end": v(-5791.17, 4876.8) * mm});
            skLineSegment(sketch, "E183.8", {"start": v(-5714.97, 5178.43) * mm, "end": v(-5791.17, 5178.43) * mm});
            skLineSegment(sketch, "E183.9", {"start": v(-5714.97, 4876.8) * mm, "end": v(-5714.97, 5178.43) * mm});
            skLineSegment(sketch, "E183.10", {"start": v(-5791.17, 4876.8) * mm, "end": v(-5714.97, 4876.8) * mm});
            skLineSegment(sketch, "E183.11", {"start": v(-5791.17, 5178.43) * mm, "end": v(-5791.17, 5060.95) * mm});
            skLineSegment(sketch, "E184.0", {"start": v(-5581.65, 5178.43) * mm, "end": v(-5581.65, 4741.36) * mm});
            skLineSegment(sketch, "E184.1", {"start": v(-5505.42, 4925.5) * mm, "end": v(-5505.42, 5178.43) * mm});
            skLineSegment(sketch, "E184.2", {"start": v(-5505.42, 5178.43) * mm, "end": v(-5581.65, 5178.43) * mm});
            skLineSegment(sketch, "E184.3", {"start": v(-5581.65, 4741.36) * mm, "end": v(-5505.42, 4741.36) * mm});
            skLineSegment(sketch, "E184.4", {"start": v(-5505.42, 4741.36) * mm, "end": v(-5505.42, 3352.8) * mm});
            skLineSegment(sketch, "E184.5", {"start": v(-3676.62, 4925.5) * mm, "end": v(-5505.42, 4925.5) * mm});
            skLineSegment(sketch, "E184.6", {"start": v(-5505.42, 3352.8) * mm, "end": v(-3676.62, 3352.8) * mm});
            skLineSegment(sketch, "E184.7", {"start": v(-3676.62, 3352.8) * mm, "end": v(-3676.62, 4741.36) * mm});
            skLineSegment(sketch, "E184.8", {"start": v(-3676.62, 4741.36) * mm, "end": v(-3600.42, 4741.36) * mm});
            skLineSegment(sketch, "E184.9", {"start": v(-3600.42, 4741.36) * mm, "end": v(-3600.42, 5178.43) * mm});
            skLineSegment(sketch, "E184.10", {"start": v(-3676.62, 5178.43) * mm, "end": v(-3676.62, 4925.5) * mm});
            skLineSegment(sketch, "E184.11", {"start": v(-3600.42, 5178.43) * mm, "end": v(-3676.62, 5178.43) * mm});
            skSolve(sketch);
        }
        {
            var Q0;
            Q0 = qSketchRegion(id + "F18", true);
            extrude(context, id + "F19", {"entities" : qUnion([Q0]), "operationType" : NewBodyOperationType.REMOVE, "oppositeDirection" : true, "depth" : 139.7 * mm});
        }
        {
            var Q0;
            {var subQ0=sQuery(id+"F2.wireOp",EDGE,"E76.bottom");var subQ1=sQuery(id+"F2.wireOp",EDGE,"E105.top");var subQ2=sQuery(id+"F2.wireOp",EDGE,"E104.top");var subQ3=sQuery(id+"F2.wireOp",EDGE,"E103.top");var subQ4=sQuery(id+"F2.wireOp",EDGE,"E102.top");var subQ5=sQuery(id+"F2.wireOp",EDGE,"E101.top");var subQ6=sQuery(id+"F2.wireOp",EDGE,"E100.top");var subQ7=sQuery(id+"F2.wireOp",EDGE,"E99.top");var subQ8=sQuery(id+"F2.wireOp",EDGE,"E98.top");var subQ9=sQuery(id+"F2.wireOp",EDGE,"E97.top");var subQ10=sQuery(id+"F2.wireOp",EDGE,"E96.top");var subQ11=sQuery(id+"F2.wireOp",EDGE,"E95.top");var subQ12=sQuery(id+"F2.wireOp",EDGE,"E94.top");var subQ13=sQuery(id+"F2.wireOp",EDGE,"E93.top");var subQ14=sQuery(id+"F2.wireOp",EDGE,"E92.top");var subQ15=sQuery(id+"F2.wireOp",EDGE,"E86.top");var subQ16=sQuery(id+"F2.wireOp",EDGE,"E81.23.0.3");var subQ17=sQuery(id+"F2.wireOp",EDGE,"E81.22.0.3");var subQ18=sQuery(id+"F2.wireOp",EDGE,"E81.21.0.3");var subQ19=sQuery(id+"F2.wireOp",EDGE,"E81.20.0.3");var subQ20=sQuery(id+"F2.wireOp",EDGE,"E81.19.0.3");var subQ21=sQuery(id+"F2.wireOp",EDGE,"E81.18.0.3");var subQ22=sQuery(id+"F2.wireOp",EDGE,"E81.17.0.3");var subQ23=sQuery(id+"F2.wireOp",EDGE,"E81.16.0.3");var subQ24=sQuery(id+"F2.wireOp",EDGE,"E81.15.0.3");var subQ25=sQuery(id+"F2.wireOp",EDGE,"E81.14.0.3");var subQ26=sQuery(id+"F2.wireOp",EDGE,"E81.13.0.3");var subQ27=sQuery(id+"F2.wireOp",EDGE,"E81.12.0.3");var subQ28=sQuery(id+"F2.wireOp",EDGE,"E81.11.0.3");var subQ29=sQuery(id+"F2.wireOp",EDGE,"E81.10.0.3");var subQ30=sQuery(id+"F2.wireOp",EDGE,"E81.9.0.3");var subQ31=sQuery(id+"F2.wireOp",EDGE,"E81.8.0.3");var subQ32=sQuery(id+"F2.wireOp",EDGE,"E81.7.0.3");var subQ33=sQuery(id+"F2.wireOp",EDGE,"E81.6.0.3");var subQ34=sQuery(id+"F2.wireOp",EDGE,"E81.5.0.3");var subQ35=sQuery(id+"F2.wireOp",EDGE,"E81.4.0.3");var subQ36=sQuery(id+"F2.wireOp",EDGE,"E81.3.0.3");var subQ37=sQuery(id+"F2.wireOp",EDGE,"E81.2.0.3");var subQ38=sQuery(id+"F2.wireOp",EDGE,"E81.1.0.3");var subQ39=sQuery(id+"F2.wireOp",EDGE,"E80.top");Q0=makeQuery(id+"F17.boolean.opBoolean","MERGE",FACE,{"derivedFrom":[makeQuery(id+"F13.boolean.opBoolean","MERGE",FACE,{"derivedFrom":[makeQuery(id+"F9.boolean.opBoolean","MERGE",FACE,{"derivedFrom":[makeQuery(id+"F7.boolean.opBoolean","MERGE",FACE,{"derivedFrom":[makeQuery(id+"F5.boolean.opBoolean","MERGE",FACE,{"derivedFrom":[makeQuery(id+"F3.boolean.opBoolean","MERGE",FACE,{"derivedFrom":[makeQuery(id+"F1.opExtrude","SWEPT_FACE",FACE,{"disambiguationData":[OSD([sQuery(id+"F0.wireOp",EDGE,"E0")])]}),makeQuery(id+"F3.opExtrude","SWEPT_FACE",FACE,{"disambiguationData":[OSD([subQ0])]}),makeQuery(id+"F3.opExtrude","SWEPT_FACE",FACE,{"disambiguationData":[OSD([sQuery(id+"F2.wireOp",EDGE,"E78.bottom")])]}),makeQuery(id+"F3.opExtrude","SWEPT_FACE",FACE,{"disambiguationData":[OSD([subQ39])]}),makeQuery(id+"F3.opExtrude","SWEPT_FACE",FACE,{"disambiguationData":[OSD([subQ38])]}),makeQuery(id+"F3.opExtrude","SWEPT_FACE",FACE,{"disambiguationData":[OSD([subQ37])]}),makeQuery(id+"F3.opExtrude","SWEPT_FACE",FACE,{"disambiguationData":[OSD([subQ36])]}),makeQuery(id+"F3.opExtrude","SWEPT_FACE",FACE,{"disambiguationData":[OSD([subQ35])]}),makeQuery(id+"F3.opExtrude","SWEPT_FACE",FACE,{"disambiguationData":[OSD([subQ34])]}),makeQuery(id+"F3.opExtrude","SWEPT_FACE",FACE,{"disambiguationData":[OSD([subQ33])]}),makeQuery(id+"F3.opExtrude","SWEPT_FACE",FACE,{"disambiguationData":[OSD([subQ32])]}),makeQuery(id+"F3.opExtrude","SWEPT_FACE",FACE,{"disambiguationData":[OSD([subQ31])]}),makeQuery(id+"F3.opExtrude","SWEPT_FACE",FACE,{"disambiguationData":[OSD([subQ30])]}),makeQuery(id+"F3.opExtrude","SWEPT_FACE",FACE,{"disambiguationData":[OSD([subQ29])]}),makeQuery(id+"F3.opExtrude","SWEPT_FACE",FACE,{"disambiguationData":[OSD([subQ28])]}),makeQuery(id+"F3.opExtrude","SWEPT_FACE",FACE,{"disambiguationData":[OSD([subQ27])]}),makeQuery(id+"F3.opExtrude","SWEPT_FACE",FACE,{"disambiguationData":[OSD([subQ26])]}),makeQuery(id+"F3.opExtrude","SWEPT_FACE",FACE,{"disambiguationData":[OSD([subQ25])]}),makeQuery(id+"F3.opExtrude","SWEPT_FACE",FACE,{"disambiguationData":[OSD([subQ24])]}),makeQuery(id+"F3.opExtrude","SWEPT_FACE",FACE,{"disambiguationData":[OSD([subQ23])]}),makeQuery(id+"F3.opExtrude","SWEPT_FACE",FACE,{"disambiguationData":[OSD([subQ22])]}),makeQuery(id+"F3.opExtrude","SWEPT_FACE",FACE,{"disambiguationData":[OSD([subQ21])]}),makeQuery(id+"F3.opExtrude","SWEPT_FACE",FACE,{"disambiguationData":[OSD([subQ20])]}),makeQuery(id+"F3.opExtrude","SWEPT_FACE",FACE,{"disambiguationData":[OSD([subQ19])]}),makeQuery(id+"F3.opExtrude","SWEPT_FACE",FACE,{"disambiguationData":[OSD([subQ18])]}),makeQuery(id+"F3.opExtrude","SWEPT_FACE",FACE,{"disambiguationData":[OSD([subQ17])]}),makeQuery(id+"F3.opExtrude","SWEPT_FACE",FACE,{"disambiguationData":[OSD([subQ16])]}),makeQuery(id+"F3.opExtrude","SWEPT_FACE",FACE,{"disambiguationData":[OSD([sQuery(id+"F2.wireOp",EDGE,"E81.25.0.3")])]}),makeQuery(id+"F3.opExtrude","SWEPT_FACE",FACE,{"disambiguationData":[OSD([sQuery(id+"F2.wireOp",EDGE,"E81.26.0.3")])]}),makeQuery(id+"F3.opExtrude","SWEPT_FACE",FACE,{"disambiguationData":[OSD([sQuery(id+"F2.wireOp",EDGE,"E84.top")])]}),makeQuery(id+"F3.opExtrude","SWEPT_FACE",FACE,{"disambiguationData":[OSD([sQuery(id+"F2.wireOp",EDGE,"E85.top")])]}),makeQuery(id+"F3.opExtrude","SWEPT_FACE",FACE,{"disambiguationData":[OSD([subQ15])]}),makeQuery(id+"F3.opExtrude","SWEPT_FACE",FACE,{"disambiguationData":[OSD([sQuery(id+"F2.wireOp",EDGE,"E87.top")])]}),makeQuery(id+"F3.opExtrude","SWEPT_FACE",FACE,{"disambiguationData":[OSD([sQuery(id+"F2.wireOp",EDGE,"E88.top")])]}),makeQuery(id+"F3.opExtrude","SWEPT_FACE",FACE,{"disambiguationData":[OSD([sQuery(id+"F2.wireOp",EDGE,"E89.top")])]}),makeQuery(id+"F3.opExtrude","SWEPT_FACE",FACE,{"disambiguationData":[OSD([sQuery(id+"F2.wireOp",EDGE,"E90.top")])]}),makeQuery(id+"F3.opExtrude","SWEPT_FACE",FACE,{"disambiguationData":[OSD([sQuery(id+"F2.wireOp",EDGE,"E91.top")])]}),makeQuery(id+"F3.opExtrude","SWEPT_FACE",FACE,{"disambiguationData":[OSD([subQ14])]}),makeQuery(id+"F3.opExtrude","SWEPT_FACE",FACE,{"disambiguationData":[OSD([subQ13])]}),makeQuery(id+"F3.opExtrude","SWEPT_FACE",FACE,{"disambiguationData":[OSD([subQ12])]}),makeQuery(id+"F3.opExtrude","SWEPT_FACE",FACE,{"disambiguationData":[OSD([subQ11])]}),makeQuery(id+"F3.opExtrude","SWEPT_FACE",FACE,{"disambiguationData":[OSD([subQ10])]}),makeQuery(id+"F3.opExtrude","SWEPT_FACE",FACE,{"disambiguationData":[OSD([subQ9])]}),makeQuery(id+"F3.opExtrude","SWEPT_FACE",FACE,{"disambiguationData":[OSD([subQ8])]}),makeQuery(id+"F3.opExtrude","SWEPT_FACE",FACE,{"disambiguationData":[OSD([subQ7])]}),makeQuery(id+"F3.opExtrude","SWEPT_FACE",FACE,{"disambiguationData":[OSD([subQ6])]}),makeQuery(id+"F3.opExtrude","SWEPT_FACE",FACE,{"disambiguationData":[OSD([subQ5])]}),makeQuery(id+"F3.opExtrude","SWEPT_FACE",FACE,{"disambiguationData":[OSD([subQ4])]}),makeQuery(id+"F3.opExtrude","SWEPT_FACE",FACE,{"disambiguationData":[OSD([subQ3])]}),makeQuery(id+"F3.opExtrude","SWEPT_FACE",FACE,{"disambiguationData":[OSD([subQ2])]}),makeQuery(id+"F3.opExtrude","SWEPT_FACE",FACE,{"disambiguationData":[OSD([subQ1])]})]}),makeQuery(id+"F5.opExtrude","SWEPT_FACE",FACE,{"disambiguationData":[OSD([sQuery(id+"F4.wireOp",EDGE,"E110.bottom")])]})]}),makeQuery(id+"F7.opExtrude","SWEPT_FACE",FACE,{"disambiguationData":[OSD([subQ39])]}),makeQuery(id+"F7.opExtrude","SWEPT_FACE",FACE,{"disambiguationData":[OSD([subQ38])]}),makeQuery(id+"F7.opExtrude","SWEPT_FACE",FACE,{"disambiguationData":[OSD([subQ37])]}),makeQuery(id+"F7.opExtrude","SWEPT_FACE",FACE,{"disambiguationData":[OSD([subQ36])]}),makeQuery(id+"F7.opExtrude","SWEPT_FACE",FACE,{"disambiguationData":[OSD([subQ35])]}),makeQuery(id+"F7.opExtrude","SWEPT_FACE",FACE,{"disambiguationData":[OSD([subQ34])]}),makeQuery(id+"F7.opExtrude","SWEPT_FACE",FACE,{"disambiguationData":[OSD([subQ33])]}),makeQuery(id+"F7.opExtrude","SWEPT_FACE",FACE,{"disambiguationData":[OSD([subQ32])]}),makeQuery(id+"F7.opExtrude","SWEPT_FACE",FACE,{"disambiguationData":[OSD([subQ31])]}),makeQuery(id+"F7.opExtrude","SWEPT_FACE",FACE,{"disambiguationData":[OSD([subQ30])]}),makeQuery(id+"F7.opExtrude","SWEPT_FACE",FACE,{"disambiguationData":[OSD([subQ29])]}),makeQuery(id+"F7.opExtrude","SWEPT_FACE",FACE,{"disambiguationData":[OSD([subQ28])]}),makeQuery(id+"F7.opExtrude","SWEPT_FACE",FACE,{"disambiguationData":[OSD([subQ27])]}),makeQuery(id+"F7.opExtrude","SWEPT_FACE",FACE,{"disambiguationData":[OSD([subQ26])]}),makeQuery(id+"F7.opExtrude","SWEPT_FACE",FACE,{"disambiguationData":[OSD([subQ25])]}),makeQuery(id+"F7.opExtrude","SWEPT_FACE",FACE,{"disambiguationData":[OSD([subQ24])]}),makeQuery(id+"F7.opExtrude","SWEPT_FACE",FACE,{"disambiguationData":[OSD([subQ23])]}),makeQuery(id+"F7.opExtrude","SWEPT_FACE",FACE,{"disambiguationData":[OSD([subQ22])]}),makeQuery(id+"F7.opExtrude","SWEPT_FACE",FACE,{"disambiguationData":[OSD([subQ21])]}),makeQuery(id+"F7.opExtrude","SWEPT_FACE",FACE,{"disambiguationData":[OSD([subQ20])]}),makeQuery(id+"F7.opExtrude","SWEPT_FACE",FACE,{"disambiguationData":[OSD([subQ19])]}),makeQuery(id+"F7.opExtrude","SWEPT_FACE",FACE,{"disambiguationData":[OSD([subQ18])]}),makeQuery(id+"F7.opExtrude","SWEPT_FACE",FACE,{"disambiguationData":[OSD([subQ17])]}),makeQuery(id+"F7.opExtrude","SWEPT_FACE",FACE,{"disambiguationData":[OSD([subQ16])]}),makeQuery(id+"F7.opExtrude","SWEPT_FACE",FACE,{"disambiguationData":[OSD([subQ15])]}),makeQuery(id+"F7.opExtrude","SWEPT_FACE",FACE,{"disambiguationData":[OSD([subQ14])]}),makeQuery(id+"F7.opExtrude","SWEPT_FACE",FACE,{"disambiguationData":[OSD([subQ13])]}),makeQuery(id+"F7.opExtrude","SWEPT_FACE",FACE,{"disambiguationData":[OSD([subQ12])]}),makeQuery(id+"F7.opExtrude","SWEPT_FACE",FACE,{"disambiguationData":[OSD([subQ11])]}),makeQuery(id+"F7.opExtrude","SWEPT_FACE",FACE,{"disambiguationData":[OSD([subQ10])]}),makeQuery(id+"F7.opExtrude","SWEPT_FACE",FACE,{"disambiguationData":[OSD([subQ9])]}),makeQuery(id+"F7.opExtrude","SWEPT_FACE",FACE,{"disambiguationData":[OSD([subQ8])]}),makeQuery(id+"F7.opExtrude","SWEPT_FACE",FACE,{"disambiguationData":[OSD([subQ7])]}),makeQuery(id+"F7.opExtrude","SWEPT_FACE",FACE,{"disambiguationData":[OSD([subQ6])]}),makeQuery(id+"F7.opExtrude","SWEPT_FACE",FACE,{"disambiguationData":[OSD([subQ5])]}),makeQuery(id+"F7.opExtrude","SWEPT_FACE",FACE,{"disambiguationData":[OSD([subQ4])]}),makeQuery(id+"F7.opExtrude","SWEPT_FACE",FACE,{"disambiguationData":[OSD([subQ3])]}),makeQuery(id+"F7.opExtrude","SWEPT_FACE",FACE,{"disambiguationData":[OSD([subQ2])]}),makeQuery(id+"F7.opExtrude","SWEPT_FACE",FACE,{"disambiguationData":[OSD([subQ1])]}),makeQuery(id+"F7.opExtrude","SWEPT_FACE",FACE,{"disambiguationData":[OSD([subQ0])]})]}),makeQuery(id+"F9.opExtrude","SWEPT_FACE",FACE,{"disambiguationData":[OSD([sQuery(id+"F8.wireOp",EDGE,"E112.top")])]})]}),makeQuery(id+"F13.opExtrude","SWEPT_FACE",FACE,{"disambiguationData":[OSD([sQuery(id+"F12.wireOp",EDGE,"E123.left")])]})]}),makeQuery(id+"F17.opExtrude","CAP_FACE",FACE,{"disambiguationData":[OSD([sQuery(id+"F16.wireOp",EDGE,"E178.bottom"),sQuery(id+"F16.wireOp",EDGE,"E178.top"),sQuery(id+"F16.wireOp",EDGE,"E178.left"),sQuery(id+"F16.wireOp",EDGE,"E178.right")])],"isStart":true}),makeQuery(id+"F17.opExtrude","CAP_FACE",FACE,{"disambiguationData":[OSD([sQuery(id+"F16.wireOp",EDGE,"E179.bottom"),sQuery(id+"F16.wireOp",EDGE,"E179.top"),sQuery(id+"F16.wireOp",EDGE,"E179.left"),sQuery(id+"F16.wireOp",EDGE,"E179.right")])],"isStart":true}),makeQuery(id+"F17.opExtrude","CAP_FACE",FACE,{"disambiguationData":[OSD([sQuery(id+"F16.wireOp",EDGE,"E180.bottom"),sQuery(id+"F16.wireOp",EDGE,"E180.top"),sQuery(id+"F16.wireOp",EDGE,"E180.left"),sQuery(id+"F16.wireOp",EDGE,"E180.right")])],"isStart":true}),makeQuery(id+"F17.opExtrude","CAP_FACE",FACE,{"disambiguationData":[OSD([sQuery(id+"F16.wireOp",EDGE,"E181.bottom"),sQuery(id+"F16.wireOp",EDGE,"E181.top"),sQuery(id+"F16.wireOp",EDGE,"E181.left"),sQuery(id+"F16.wireOp",EDGE,"E181.right")])],"isStart":true})]});}
            var sketch = newSketch(context, id + "F20", { "sketchPlane" : qUnion([Q0]) });
            skLineSegment(sketch, "E185.bottom", {"start": v(-9842.53, 4741.38) * mm, "end": v(-7861.27, 4741.38) * mm});
            skLineSegment(sketch, "E185.top", {"start": v(-9842.53, 4925.48) * mm, "end": v(-7861.27, 4925.48) * mm});
            skLineSegment(sketch, "E185.left", {"start": v(-9842.53, 4741.38) * mm, "end": v(-9842.53, 4925.48) * mm});
            skLineSegment(sketch, "E185.right", {"start": v(-7861.27, 4741.38) * mm, "end": v(-7861.27, 4925.48) * mm});
            skLineSegment(sketch, "E186.bottom", {"start": v(-7727.98, 4876.83) * mm, "end": v(-5714.95, 4876.83) * mm});
            skLineSegment(sketch, "E186.top", {"start": v(-7727.98, 5060.92) * mm, "end": v(-5714.95, 5060.92) * mm});
            skLineSegment(sketch, "E186.left", {"start": v(-7727.98, 4876.83) * mm, "end": v(-7727.98, 5060.92) * mm});
            skLineSegment(sketch, "E186.right", {"start": v(-5714.95, 4876.83) * mm, "end": v(-5714.95, 5060.92) * mm});
            skLineSegment(sketch, "E187.bottom", {"start": v(-5581.65, 4741.38) * mm, "end": v(-3587.75, 4741.38) * mm});
            skLineSegment(sketch, "E187.top", {"start": v(-5581.65, 4925.48) * mm, "end": v(-3587.75, 4925.48) * mm});
            skLineSegment(sketch, "E187.left", {"start": v(-5581.65, 4741.38) * mm, "end": v(-5581.65, 4925.48) * mm});
            skLineSegment(sketch, "E187.right", {"start": v(-3587.75, 4741.38) * mm, "end": v(-3587.75, 4925.48) * mm});
            skLineSegment(sketch, "E188.bottom", {"start": v(-3676.62, 3352.8) * mm, "end": v(-5505.42, 3352.8) * mm});
            skLineSegment(sketch, "E188.top", {"start": v(-3676.62, 3314.7) * mm, "end": v(-5505.42, 3314.7) * mm});
            skLineSegment(sketch, "E188.left", {"start": v(-3676.62, 3352.8) * mm, "end": v(-3676.62, 3314.7) * mm});
            skLineSegment(sketch, "E188.right", {"start": v(-5505.42, 3352.8) * mm, "end": v(-5505.42, 3314.7) * mm});
            skLineSegment(sketch, "E189.bottom", {"start": v(-5791.17, 3352.8) * mm, "end": v(-7651.78, 3352.8) * mm});
            skLineSegment(sketch, "E189.top", {"start": v(-5791.17, 3314.7) * mm, "end": v(-7651.78, 3314.7) * mm});
            skLineSegment(sketch, "E189.left", {"start": v(-5791.17, 3352.8) * mm, "end": v(-5791.17, 3314.7) * mm});
            skLineSegment(sketch, "E189.right", {"start": v(-7651.78, 3352.8) * mm, "end": v(-7651.78, 3314.7) * mm});
            skLineSegment(sketch, "E190.bottom", {"start": v(-7937.5, 3352.8) * mm, "end": v(-9766.3, 3352.8) * mm});
            skLineSegment(sketch, "E190.top", {"start": v(-7937.5, 3314.7) * mm, "end": v(-9766.3, 3314.7) * mm});
            skLineSegment(sketch, "E190.left", {"start": v(-7937.5, 3352.8) * mm, "end": v(-7937.5, 3314.7) * mm});
            skLineSegment(sketch, "E190.right", {"start": v(-9766.3, 3352.8) * mm, "end": v(-9766.3, 3314.7) * mm});
            skSolve(sketch);
        }
        {
            var Q0;
            Q0 = qSketchRegion(id + "F20", true);
            extrude(context, id + "F21", {"entities" : qUnion([Q0]), "operationType" : NewBodyOperationType.ADD, "oppositeDirection" : true, "depth" : 139.7 * mm});
        }
        {
            var Q0;
            {var subQ170=sQuery(id+"F14.wireOp",EDGE,"E124");Q0=makeQuery(id+"F14.imprint","IMPRINT",FACE,{"disambiguationData":[TD([[makeQuery(id+"F14.imprint","IMPRINT",EDGE,{"derivedFrom":subQ170}),-1.0]])]});}
            var sketch = newSketch(context, id + "F22", { "sketchPlane" : qUnion([Q0]) });
            skLineSegment(sketch, "E191", {"start": v(-9683.75, 4741.38) * mm, "end": v(-9683.75, 4063.82) * mm});
            skLineSegment(sketch, "E192", {"start": v(-9683.75, 4063.82) * mm, "end": v(-9766.27, 4015.32) * mm});
            skLineSegment(sketch, "E193", {"start": v(-9766.27, 4015.32) * mm, "end": v(-9766.27, 3971.12) * mm});
            skLineSegment(sketch, "E194", {"start": v(-9766.27, 3971.12) * mm, "end": v(-9277.38, 4258.47) * mm});
            skLineSegment(sketch, "E195", {"start": v(-9277.38, 4258.47) * mm, "end": v(-8870.95, 4443.57) * mm});
            skLineSegment(sketch, "E196", {"start": v(-8870.95, 4443.57) * mm, "end": v(-8464.58, 4603.15) * mm});
            skLineSegment(sketch, "E197", {"start": v(-8464.58, 4603.15) * mm, "end": v(-7958.42, 4741.38) * mm});
            skLineSegment(sketch, "E198", {"start": v(-9683.75, 4741.38) * mm, "end": v(-9645.65, 4741.38) * mm});
            skLineSegment(sketch, "E199", {"start": v(-9645.65, 4741.38) * mm, "end": v(-9645.65, 4086.21) * mm});
            skLineSegment(sketch, "E200", {"start": v(-9645.65, 4086.21) * mm, "end": v(-9315.45, 4280.28) * mm});
            skLineSegment(sketch, "E201", {"start": v(-9315.45, 4280.28) * mm, "end": v(-9315.45, 4741.38) * mm});
            skLineSegment(sketch, "E202", {"start": v(-9315.45, 4741.38) * mm, "end": v(-9277.38, 4741.38) * mm});
            skLineSegment(sketch, "E203", {"start": v(-9277.38, 4741.38) * mm, "end": v(-9277.38, 4302.66) * mm});
            skLineSegment(sketch, "E204", {"start": v(-9277.38, 4302.66) * mm, "end": v(-9277.35, 4302.66) * mm});
            skLineSegment(sketch, "E205", {"start": v(-9277.35, 4302.66) * mm, "end": v(-9277.35, 4741.38) * mm});
            skLineSegment(sketch, "E206", {"start": v(-9277.35, 4741.38) * mm, "end": v(-9239.25, 4741.38) * mm});
            skLineSegment(sketch, "E207", {"start": v(-9239.25, 4741.38) * mm, "end": v(-9239.25, 4317.7) * mm});
            skLineSegment(sketch, "E208", {"start": v(-9239.25, 4317.7) * mm, "end": v(-8909.05, 4468.08) * mm});
            skPoint(sketch, "E209", {"position": v(-9521.82, 4114.8) * mm});
            skLineSegment(sketch, "E210", {"start": v(-8909.05, 4468.08) * mm, "end": v(-8909.05, 4741.38) * mm});
            skLineSegment(sketch, "E211", {"start": v(-8909.05, 4741.38) * mm, "end": v(-8870.98, 4741.38) * mm});
            skLineSegment(sketch, "E212", {"start": v(-8870.98, 4741.38) * mm, "end": v(-8870.98, 4485.43) * mm});
            skLineSegment(sketch, "E213", {"start": v(-8870.98, 4485.43) * mm, "end": v(-8870.95, 4485.43) * mm});
            skLineSegment(sketch, "E214", {"start": v(-8870.95, 4485.43) * mm, "end": v(-8870.95, 4741.38) * mm});
            skLineSegment(sketch, "E215", {"start": v(-8870.95, 4741.38) * mm, "end": v(-8832.85, 4741.38) * mm});
            skLineSegment(sketch, "E216", {"start": v(-8832.85, 4741.38) * mm, "end": v(-8832.85, 4499.46) * mm});
            skLineSegment(sketch, "E217", {"start": v(-8832.85, 4499.46) * mm, "end": v(-8502.65, 4629.13) * mm});
            skPoint(sketch, "E218", {"position": v(-9074.16, 4351.02) * mm});
            skLineSegment(sketch, "E219", {"start": v(-8502.65, 4629.13) * mm, "end": v(-8502.65, 4741.38) * mm});
            skLineSegment(sketch, "E220", {"start": v(-8502.65, 4741.38) * mm, "end": v(-8464.58, 4741.38) * mm});
            skLineSegment(sketch, "E221", {"start": v(-8464.58, 4741.38) * mm, "end": v(-8464.58, 4644.09) * mm});
            skLineSegment(sketch, "E222", {"start": v(-8464.58, 4644.09) * mm, "end": v(-8464.55, 4644.09) * mm});
            skLineSegment(sketch, "E223", {"start": v(-8464.55, 4644.09) * mm, "end": v(-8464.55, 4741.38) * mm});
            skLineSegment(sketch, "E224", {"start": v(-8464.55, 4741.38) * mm, "end": v(-8426.45, 4741.38) * mm});
            skLineSegment(sketch, "E225", {"start": v(-8426.45, 4741.38) * mm, "end": v(-8426.45, 4653.05) * mm});
            skLineSegment(sketch, "E226", {"start": v(-8426.45, 4653.05) * mm, "end": v(-8103.03, 4741.38) * mm});
            skLineSegment(sketch, "E227", {"start": v(-8103.03, 4741.38) * mm, "end": v(-7958.42, 4741.38) * mm});
            skLineSegment(sketch, "E228", {"start": v(-7651.75, 4806.83) * mm, "end": v(-7032.87, 4876.8) * mm});
            skLineSegment(sketch, "E229", {"start": v(-7032.87, 4876.8) * mm, "end": v(-7219.63, 4876.8) * mm});
            skLineSegment(sketch, "E230", {"start": v(-7372.03, 4876.8) * mm, "end": v(-7651.75, 4845.18) * mm});
            skLineSegment(sketch, "E231", {"start": v(-7651.75, 4845.18) * mm, "end": v(-7651.75, 4806.83) * mm});
            skPoint(sketch, "E232", {"position": v(-7342.31, 4841.82) * mm});
            skLineSegment(sketch, "E233", {"start": v(-6410.05, 4876.8) * mm, "end": v(-5791.17, 4806.83) * mm});
            skLineSegment(sketch, "E234", {"start": v(-5791.17, 4806.83) * mm, "end": v(-5791.17, 4845.18) * mm});
            skLineSegment(sketch, "E235", {"start": v(-5791.17, 4845.18) * mm, "end": v(-6070.9, 4876.8) * mm});
            skLineSegment(sketch, "E236", {"start": v(-6070.9, 4876.8) * mm, "end": v(-6410.05, 4876.8) * mm});
            skLineSegment(sketch, "E237", {"start": v(-4324.35, 4378.78) * mm, "end": v(-3994.15, 4201.65) * mm});
            skLineSegment(sketch, "E238", {"start": v(-3994.15, 4201.65) * mm, "end": v(-3994.15, 4741.38) * mm});
            skLineSegment(sketch, "E239", {"start": v(-3994.15, 4741.38) * mm, "end": v(-3956.05, 4741.38) * mm});
            skLineSegment(sketch, "E240", {"start": v(-3956.05, 4741.38) * mm, "end": v(-3956.05, 4182.76) * mm});
            skLineSegment(sketch, "E241", {"start": v(-3956.05, 4182.76) * mm, "end": v(-3956.02, 4182.76) * mm});
            skLineSegment(sketch, "E242", {"start": v(-3956.02, 4182.76) * mm, "end": v(-3956.02, 4741.38) * mm});
            skLineSegment(sketch, "E243", {"start": v(-3956.02, 4741.38) * mm, "end": v(-3917.95, 4741.38) * mm});
            skLineSegment(sketch, "E244", {"start": v(-3917.95, 4741.38) * mm, "end": v(-3917.95, 4159.23) * mm});
            skLineSegment(sketch, "E245", {"start": v(-3917.95, 4159.23) * mm, "end": v(-3676.62, 4010.1) * mm});
            skLineSegment(sketch, "E246", {"start": v(-3676.62, 4010.1) * mm, "end": v(-3676.62, 3965.32) * mm});
            skLineSegment(sketch, "E247", {"start": v(-3676.62, 3965.32) * mm, "end": v(-3956.02, 4137.97) * mm});
            skLineSegment(sketch, "E248", {"start": v(-3956.02, 4137.97) * mm, "end": v(-4362.45, 4355.98) * mm});
            skPoint(sketch, "E249", {"position": v(-3816.32, 4051.65) * mm});
            skLineSegment(sketch, "E250", {"start": v(-4324.35, 4378.78) * mm, "end": v(-4324.35, 4741.38) * mm});
            skLineSegment(sketch, "E251", {"start": v(-4324.35, 4741.38) * mm, "end": v(-4362.42, 4741.38) * mm});
            skLineSegment(sketch, "E252", {"start": v(-4362.42, 4741.38) * mm, "end": v(-4362.42, 4399.21) * mm});
            skLineSegment(sketch, "E253", {"start": v(-4362.42, 4399.21) * mm, "end": v(-4362.45, 4399.21) * mm});
            skLineSegment(sketch, "E254", {"start": v(-4362.45, 4399.21) * mm, "end": v(-4362.45, 4741.38) * mm});
            skLineSegment(sketch, "E255", {"start": v(-4362.45, 4741.38) * mm, "end": v(-4400.55, 4741.38) * mm});
            skLineSegment(sketch, "E256", {"start": v(-4400.55, 4741.38) * mm, "end": v(-4400.55, 4412.8) * mm});
            skLineSegment(sketch, "E257", {"start": v(-4400.55, 4412.8) * mm, "end": v(-4730.75, 4548.32) * mm});
            skLineSegment(sketch, "E258", {"start": v(-4730.75, 4548.32) * mm, "end": v(-4730.75, 4741.38) * mm});
            skLineSegment(sketch, "E259", {"start": v(-4730.75, 4741.38) * mm, "end": v(-4768.82, 4741.38) * mm});
            skLineSegment(sketch, "E260", {"start": v(-4768.82, 4741.38) * mm, "end": v(-4768.82, 4563.95) * mm});
            skLineSegment(sketch, "E261", {"start": v(-4768.82, 4563.95) * mm, "end": v(-4768.85, 4563.95) * mm});
            skLineSegment(sketch, "E262", {"start": v(-4768.85, 4563.95) * mm, "end": v(-4768.85, 4741.38) * mm});
            skLineSegment(sketch, "E263", {"start": v(-4768.85, 4741.38) * mm, "end": v(-4806.95, 4741.38) * mm});
            skLineSegment(sketch, "E264", {"start": v(-4806.95, 4741.38) * mm, "end": v(-4806.95, 4576.23) * mm});
            skLineSegment(sketch, "E265", {"start": v(-4806.95, 4576.23) * mm, "end": v(-5137.15, 4690.24) * mm});
            skLineSegment(sketch, "E266", {"start": v(-4362.45, 4355.98) * mm, "end": v(-4768.82, 4522.76) * mm});
            skLineSegment(sketch, "E267", {"start": v(-4768.82, 4522.76) * mm, "end": v(-5175.22, 4663.08) * mm});
            skPoint(sketch, "E268", {"position": v(-4159.24, 4246.97) * mm});
            skPoint(sketch, "E269", {"position": v(-4565.64, 4439.37) * mm});
            skLineSegment(sketch, "E270", {"start": v(-5137.15, 4690.24) * mm, "end": v(-5137.15, 4741.38) * mm});
            skLineSegment(sketch, "E271", {"start": v(-5137.15, 4741.38) * mm, "end": v(-5175.22, 4741.38) * mm});
            skLineSegment(sketch, "E272", {"start": v(-5175.22, 4741.38) * mm, "end": v(-5175.22, 4703.4) * mm});
            skLineSegment(sketch, "E273", {"start": v(-5175.22, 4703.4) * mm, "end": v(-5175.25, 4703.4) * mm});
            skLineSegment(sketch, "E274", {"start": v(-5175.25, 4703.4) * mm, "end": v(-5175.25, 4741.38) * mm});
            skLineSegment(sketch, "E275", {"start": v(-5175.25, 4741.38) * mm, "end": v(-5213.35, 4741.38) * mm});
            skLineSegment(sketch, "E276", {"start": v(-5213.35, 4741.38) * mm, "end": v(-5213.35, 4711.33) * mm});
            skLineSegment(sketch, "E277", {"start": v(-5213.35, 4711.33) * mm, "end": v(-5339.44, 4741.38) * mm});
            skLineSegment(sketch, "E278", {"start": v(-5339.44, 4741.38) * mm, "end": v(-5503.78, 4741.38) * mm});
            skLineSegment(sketch, "E279", {"start": v(-5503.78, 4741.38) * mm, "end": v(-5175.22, 4663.08) * mm});
            skLineSegment(sketch, "E280.top", {"start": v(-7270.43, 4889.5) * mm, "end": v(-7219.63, 4889.5) * mm});
            skLineSegment(sketch, "E280.left", {"start": v(-7270.43, 4876.8) * mm, "end": v(-7270.43, 4889.5) * mm});
            skLineSegment(sketch, "E280.right", {"start": v(-7219.63, 4876.8) * mm, "end": v(-7219.63, 4889.5) * mm});
            skLineSegment(sketch, "E281.trimOffspring", {"start": v(-7270.43, 4876.8) * mm, "end": v(-7372.03, 4876.8) * mm});
            skSolve(sketch);
        }
        {
            var Q0;
            Q0 = qSketchRegion(id + "F22", true);
            extrude(context, id + "F23", {"entities" : qUnion([Q0]), "operationType" : NewBodyOperationType.ADD, "oppositeDirection" : true, "depth" : 139.7 * mm});
        }
        {
            var Q0;
            Q0=makeQuery(id+"F1.opExtrude","CAP_FACE",FACE,{"disambiguationData":[OSD([sQuery(id+"F0.wireOp",EDGE,"E2"),sQuery(id+"F0.wireOp",EDGE,"E13.11"),sQuery(id+"F0.wireOp",EDGE,"6705dlQq-f1UD-V3qU-CbVU-eFvXpBAe9cDM"),sQuery(id+"F0.wireOp",EDGE,"86c541f8-da60-444e-9c9f-927beb1ecad3.trimOffspring"),sQuery(id+"F0.wireOp",EDGE,"E22")])],"isStart":false});
            var sketch = newSketch(context, id + "F24", { "sketchPlane" : qUnion([Q0]) });
            skLineSegment(sketch, "E282.bottom", {"start": v(-13486.31, 1206.5) * mm, "end": v(-13448.21, 1206.5) * mm});
            skLineSegment(sketch, "E282.top", {"start": v(-13486.31, 1066.8) * mm, "end": v(-13448.21, 1066.8) * mm});
            skLineSegment(sketch, "E282.left", {"start": v(-13486.31, 1206.5) * mm, "end": v(-13486.31, 1066.8) * mm});
            skLineSegment(sketch, "E282.right", {"start": v(-13448.21, 1206.5) * mm, "end": v(-13448.21, 1066.8) * mm});
            skLineSegment(sketch, "E283", {"start": v(-13857.29, 1066.8) * mm, "end": v(-13873.66, 1066.8) * mm, "construction": true});
            skLineSegment(sketch, "E284", {"start": v(-13873.66, 1066.8) * mm, "end": v(-13873.66, 1054.1) * mm, "construction": true});
            skLineSegment(sketch, "E285", {"start": v(-13873.66, 1054.1) * mm, "end": v(-13808.05, 1054.1) * mm, "construction": true});
            skLineSegment(sketch, "E286", {"start": v(-13963.04, 1161.44) * mm, "end": v(-13871.03, 1069.43) * mm, "construction": true});
            skLineSegment(sketch, "E287", {"start": v(-13871.03, 1069.43) * mm, "end": v(-13880.01, 1060.45) * mm, "construction": true});
            skLineSegment(sketch, "E288", {"start": v(-13880.01, 1060.45) * mm, "end": v(-13955.28, 1135.72) * mm, "construction": true});
            skLineSegment(sketch, "E289.1.0.0", {"start": v(-13079.91, 1206.5) * mm, "end": v(-13079.91, 1066.8) * mm});
            skLineSegment(sketch, "E289.1.0.1", {"start": v(-13041.81, 1206.5) * mm, "end": v(-13041.81, 1066.8) * mm});
            skLineSegment(sketch, "E289.1.0.2", {"start": v(-13079.91, 1206.5) * mm, "end": v(-13041.81, 1206.5) * mm});
            skLineSegment(sketch, "E289.1.0.3", {"start": v(-13079.91, 1066.8) * mm, "end": v(-13041.81, 1066.8) * mm});
            skLineSegment(sketch, "E289.2.0.0", {"start": v(-12673.51, 1206.5) * mm, "end": v(-12673.51, 1066.8) * mm});
            skLineSegment(sketch, "E289.2.0.1", {"start": v(-12635.41, 1206.5) * mm, "end": v(-12635.41, 1066.8) * mm});
            skLineSegment(sketch, "E289.2.0.2", {"start": v(-12673.51, 1206.5) * mm, "end": v(-12635.41, 1206.5) * mm});
            skLineSegment(sketch, "E289.2.0.3", {"start": v(-12673.51, 1066.8) * mm, "end": v(-12635.41, 1066.8) * mm});
            skLineSegment(sketch, "E289.3.0.0", {"start": v(-12267.11, 1206.5) * mm, "end": v(-12267.11, 1066.8) * mm});
            skLineSegment(sketch, "E289.3.0.1", {"start": v(-12229.01, 1206.5) * mm, "end": v(-12229.01, 1066.8) * mm});
            skLineSegment(sketch, "E289.3.0.2", {"start": v(-12267.11, 1206.5) * mm, "end": v(-12229.01, 1206.5) * mm});
            skLineSegment(sketch, "E289.3.0.3", {"start": v(-12267.11, 1066.8) * mm, "end": v(-12229.01, 1066.8) * mm});
            skLineSegment(sketch, "E289.4.0.0", {"start": v(-11860.71, 1206.5) * mm, "end": v(-11860.71, 1066.8) * mm});
            skLineSegment(sketch, "E289.4.0.1", {"start": v(-11822.61, 1206.5) * mm, "end": v(-11822.61, 1066.8) * mm});
            skLineSegment(sketch, "E289.4.0.2", {"start": v(-11860.71, 1206.5) * mm, "end": v(-11822.61, 1206.5) * mm});
            skLineSegment(sketch, "E289.4.0.3", {"start": v(-11860.71, 1066.8) * mm, "end": v(-11822.61, 1066.8) * mm});
            skLineSegment(sketch, "E289.5.0.0", {"start": v(-11454.31, 1206.5) * mm, "end": v(-11454.31, 1066.8) * mm});
            skLineSegment(sketch, "E289.5.0.1", {"start": v(-11416.21, 1206.5) * mm, "end": v(-11416.21, 1066.8) * mm});
            skLineSegment(sketch, "E289.5.0.2", {"start": v(-11454.31, 1206.5) * mm, "end": v(-11416.21, 1206.5) * mm});
            skLineSegment(sketch, "E289.5.0.3", {"start": v(-11454.31, 1066.8) * mm, "end": v(-11416.21, 1066.8) * mm});
            skLineSegment(sketch, "E289.direction1", {"start": v(-13486.31, 1066.8) * mm, "end": v(-13079.91, 1066.8) * mm, "construction": true});
            skLineSegment(sketch, "E290", {"start": v(-12788.9, 1206.5) * mm, "end": v(-12788.9, 1283.32) * mm, "construction": true});
            skLineSegment(sketch, "E291", {"start": v(-12788.9, 1283.32) * mm, "end": v(-12700, 1283.32) * mm, "construction": true});
            skLineSegment(sketch, "E292", {"start": v(-12700, 1283.32) * mm, "end": v(-12700, 1372.22) * mm, "construction": true});
            skLineSegment(sketch, "E293", {"start": v(-12700, 1372.22) * mm, "end": v(-12877.8, 1372.22) * mm, "construction": true});
            skLineSegment(sketch, "E294", {"start": v(-12877.8, 1372.22) * mm, "end": v(-12877.8, 1066.8) * mm, "construction": true});
            skLineSegment(sketch, "E295.bottom", {"start": v(-12903.2, 1206.5) * mm, "end": v(-12763.5, 1206.5) * mm});
            skLineSegment(sketch, "E295.top", {"start": v(-12903.2, 1168.4) * mm, "end": v(-12763.5, 1168.4) * mm});
            skLineSegment(sketch, "E295.left", {"start": v(-12903.2, 1206.5) * mm, "end": v(-12903.2, 1168.4) * mm});
            skLineSegment(sketch, "E295.right", {"start": v(-12763.5, 1206.5) * mm, "end": v(-12763.5, 1168.4) * mm});
            skLineSegment(sketch, "E296.bottom", {"start": v(-13810.5, 1206.5) * mm, "end": v(-13772.43, 1206.5) * mm});
            skLineSegment(sketch, "E296.top", {"start": v(-13810.5, 1066.8) * mm, "end": v(-13772.43, 1066.8) * mm});
            skLineSegment(sketch, "E296.left", {"start": v(-13810.5, 1206.5) * mm, "end": v(-13810.5, 1066.8) * mm});
            skLineSegment(sketch, "E296.right", {"start": v(-13772.43, 1206.5) * mm, "end": v(-13772.43, 1066.8) * mm});
            skLineSegment(sketch, "E297.bottom", {"start": v(-11277.63, 1066.8) * mm, "end": v(-11315.7, 1066.8) * mm});
            skLineSegment(sketch, "E297.top", {"start": v(-11277.63, 1206.5) * mm, "end": v(-11315.7, 1206.5) * mm});
            skLineSegment(sketch, "E297.left", {"start": v(-11277.63, 1066.8) * mm, "end": v(-11277.63, 1206.5) * mm});
            skLineSegment(sketch, "E297.right", {"start": v(-11315.7, 1066.8) * mm, "end": v(-11315.7, 1206.5) * mm});
            skLineSegment(sketch, "E298", {"start": v(-11277.6, 1372.22) * mm, "end": v(-11455.4, 1372.22) * mm, "construction": true});
            skLineSegment(sketch, "E299", {"start": v(-11455.4, 1372.22) * mm, "end": v(-11455.4, 1283.32) * mm, "construction": true});
            skLineSegment(sketch, "E300", {"start": v(-11455.4, 1283.32) * mm, "end": v(-11277.6, 1283.32) * mm, "construction": true});
            skSolve(sketch);
        }
        {
            var Q0;
            Q0 = qSketchRegion(id + "F24", true);
            extrude(context, id + "F25", {"entities" : qUnion([Q0]), "operationType" : NewBodyOperationType.ADD, "depth" : 2352.67 * mm});
        }
        {
            var Q0;
            Q0=makeQuery(id+"F25.opExtrude","CAP_FACE",FACE,{"disambiguationData":[OSD([sQuery(id+"F24.wireOp",EDGE,"E296.bottom"),sQuery(id+"F24.wireOp",EDGE,"E296.top"),sQuery(id+"F24.wireOp",EDGE,"E296.left"),sQuery(id+"F24.wireOp",EDGE,"E296.right")])],"isStart":false});
            var sketch = newSketch(context, id + "F26", { "sketchPlane" : qUnion([Q0]) });
            skLineSegment(sketch, "E301.bottom", {"start": v(-11277.63, 1206.5) * mm, "end": v(-13810.5, 1206.5) * mm});
            skLineSegment(sketch, "E301.top", {"start": v(-11277.63, 1066.8) * mm, "end": v(-13810.5, 1066.8) * mm});
            skLineSegment(sketch, "E301.left", {"start": v(-11277.63, 1206.5) * mm, "end": v(-11277.63, 1066.8) * mm});
            skLineSegment(sketch, "E301.right", {"start": v(-13810.5, 1206.5) * mm, "end": v(-13810.5, 1066.8) * mm});
            skSolve(sketch);
        }
        {
            var Q0;
            Q0 = qSketchRegion(id + "F26", true);
            extrude(context, id + "F27", {"entities" : qUnion([Q0]), "operationType" : NewBodyOperationType.ADD, "depth" : 76.2 * mm});
        }
        {
            var Q0;
            Q0=makeQuery(id+"F1.opExtrude","CAP_FACE",FACE,{"disambiguationData":[OSD([sQuery(id+"F0.wireOp",EDGE,"E3"),sQuery(id+"F0.wireOp",EDGE,"E4"),sQuery(id+"F0.wireOp",EDGE,"E13.12"),sQuery(id+"F0.wireOp",EDGE,"E21"),sQuery(id+"F0.wireOp",EDGE,"E23.trimOffspring"),sQuery(id+"F0.wireOp",EDGE,"E24")])],"isStart":false});
            var sketch = newSketch(context, id + "F28", { "sketchPlane" : qUnion([Q0]) });
            skLineSegment(sketch, "E302", {"start": v(-13810.53, 1206.5) * mm, "end": v(-13909.32, 1107.72) * mm});
            skLineSegment(sketch, "E303", {"start": v(-13909.32, 1107.72) * mm, "end": v(-13936.26, 1134.66) * mm});
            skLineSegment(sketch, "E304", {"start": v(-13936.26, 1134.66) * mm, "end": v(-13837.48, 1233.44) * mm});
            skLineSegment(sketch, "E305", {"start": v(-13837.48, 1233.44) * mm, "end": v(-13810.53, 1206.5) * mm});
            skLineSegment(sketch, "E306", {"start": v(-13810.53, 1206.46) * mm, "end": v(-13810.53, 1066.8) * mm});
            skLineSegment(sketch, "E307", {"start": v(-13810.53, 1066.8) * mm, "end": v(-13848.63, 1066.8) * mm});
            skLineSegment(sketch, "E308", {"start": v(-13848.63, 1066.8) * mm, "end": v(-13848.63, 1168.36) * mm});
            skLineSegment(sketch, "E309", {"start": v(-13848.63, 1168.36) * mm, "end": v(-13810.53, 1206.46) * mm});
            skLineSegment(sketch, "E310", {"start": v(-13909.3, 1107.7) * mm, "end": v(-13868.4, 1066.8) * mm});
            skLineSegment(sketch, "E311", {"start": v(-13868.4, 1066.8) * mm, "end": v(-13848.66, 1066.8) * mm});
            skLineSegment(sketch, "E312", {"start": v(-13848.66, 1066.8) * mm, "end": v(-13848.66, 1100.94) * mm});
            skLineSegment(sketch, "E313", {"start": v(-13882.36, 1134.64) * mm, "end": v(-13909.3, 1107.7) * mm});
            skLineSegment(sketch, "E314", {"start": v(-13882.36, 1134.64) * mm, "end": v(-13848.66, 1100.94) * mm});
            skLineSegment(sketch, "E315", {"start": v(-13921.83, 1120.23) * mm, "end": v(-13871.03, 1069.43) * mm, "construction": true});
            skLineSegment(sketch, "E316", {"start": v(-13871.03, 1069.43) * mm, "end": v(-13880.01, 1060.45) * mm, "construction": true});
            skLineSegment(sketch, "E317", {"start": v(-13880.01, 1060.45) * mm, "end": v(-13926.76, 1107.2) * mm, "construction": true});
            skLineSegment(sketch, "E318", {"start": v(-13826.73, 1066.8) * mm, "end": v(-13873.66, 1066.8) * mm, "construction": true});
            skLineSegment(sketch, "E319", {"start": v(-13873.66, 1066.8) * mm, "end": v(-13873.66, 1054.1) * mm, "construction": true});
            skLineSegment(sketch, "E320", {"start": v(-13873.66, 1054.1) * mm, "end": v(-13817.24, 1054.1) * mm, "construction": true});
            skLineSegment(sketch, "E321", {"start": v(-14046.15, 1442.11) * mm, "end": v(-14144.93, 1343.33) * mm});
            skLineSegment(sketch, "E322", {"start": v(-14144.93, 1343.33) * mm, "end": v(-14171.87, 1370.27) * mm});
            skLineSegment(sketch, "E323", {"start": v(-14171.87, 1370.27) * mm, "end": v(-14073.09, 1469.05) * mm});
            skLineSegment(sketch, "E324", {"start": v(-14073.09, 1469.05) * mm, "end": v(-14046.15, 1442.11) * mm});
            skLineSegment(sketch, "E325.0.1.0", {"start": v(-14333.51, 1729.48) * mm, "end": v(-14432.3, 1630.7) * mm});
            skLineSegment(sketch, "E325.0.1.1", {"start": v(-14459.24, 1657.64) * mm, "end": v(-14360.45, 1756.42) * mm});
            skLineSegment(sketch, "E325.0.1.2", {"start": v(-14360.45, 1756.42) * mm, "end": v(-14333.51, 1729.48) * mm});
            skLineSegment(sketch, "E325.0.1.3", {"start": v(-14432.3, 1630.7) * mm, "end": v(-14459.24, 1657.64) * mm});
            skLineSegment(sketch, "E325.0.2.0", {"start": v(-14620.88, 2016.85) * mm, "end": v(-14719.66, 1918.06) * mm});
            skLineSegment(sketch, "E325.0.2.1", {"start": v(-14746.6, 1945) * mm, "end": v(-14647.82, 2043.79) * mm});
            skLineSegment(sketch, "E325.0.2.2", {"start": v(-14647.82, 2043.79) * mm, "end": v(-14620.88, 2016.85) * mm});
            skLineSegment(sketch, "E325.0.2.3", {"start": v(-14719.66, 1918.06) * mm, "end": v(-14746.6, 1945) * mm});
            skLineSegment(sketch, "E325.direction1", {"start": v(-14144.93, 1343.33) * mm, "end": v(-14119.53, 1343.33) * mm, "construction": true});
            skLineSegment(sketch, "E325.direction2", {"start": v(-14144.93, 1343.33) * mm, "end": v(-14432.3, 1630.7) * mm, "construction": true});
            skLineSegment(sketch, "E326", {"start": v(-14947.9, 2343.87) * mm, "end": v(-14920.96, 2316.92) * mm});
            skLineSegment(sketch, "E327", {"start": v(-14920.96, 2316.92) * mm, "end": v(-15019.74, 2218.14) * mm});
            skLineSegment(sketch, "E328", {"start": v(-15019.74, 2218.14) * mm, "end": v(-15046.68, 2245.08) * mm});
            skLineSegment(sketch, "E329", {"start": v(-15046.68, 2245.08) * mm, "end": v(-14947.9, 2343.87) * mm});
            skLineSegment(sketch, "E330", {"start": v(-14920.94, 2316.9) * mm, "end": v(-15019.72, 2218.12) * mm});
            skLineSegment(sketch, "E331", {"start": v(-15019.72, 2218.12) * mm, "end": v(-14992.8, 2191.2) * mm});
            skLineSegment(sketch, "E332", {"start": v(-14992.8, 2191.2) * mm, "end": v(-14894.02, 2289.98) * mm});
            skLineSegment(sketch, "E333", {"start": v(-14894.02, 2289.98) * mm, "end": v(-14920.94, 2316.9) * mm});
            skLineSegment(sketch, "E334", {"start": v(-14947.94, 2343.87) * mm, "end": v(-14986.04, 2305.77) * mm});
            skLineSegment(sketch, "E335", {"start": v(-14986.04, 2305.77) * mm, "end": v(-15087.6, 2305.77) * mm});
            skLineSegment(sketch, "E336", {"start": v(-15087.6, 2305.77) * mm, "end": v(-15087.6, 2343.87) * mm});
            skLineSegment(sketch, "E337", {"start": v(-15087.6, 2343.87) * mm, "end": v(-14947.94, 2343.87) * mm});
            skLineSegment(sketch, "E338", {"start": v(-15087.6, 2305.74) * mm, "end": v(-15087.6, 2286) * mm});
            skLineSegment(sketch, "E339", {"start": v(-15087.6, 2286) * mm, "end": v(-15046.7, 2245.1) * mm});
            skLineSegment(sketch, "E340", {"start": v(-15046.7, 2245.1) * mm, "end": v(-15019.76, 2272.04) * mm});
            skLineSegment(sketch, "E341", {"start": v(-15019.76, 2272.04) * mm, "end": v(-15053.46, 2305.74) * mm});
            skLineSegment(sketch, "E342", {"start": v(-15053.46, 2305.74) * mm, "end": v(-15087.6, 2305.74) * mm});
            skLineSegment(sketch, "E343", {"start": v(-15087.6, 2286) * mm, "end": v(-14909.05, 2107.45) * mm, "construction": true});
            skLineSegment(sketch, "E344", {"start": v(-13868.4, 1066.8) * mm, "end": v(-14046.95, 1245.35) * mm, "construction": true});
            skLineSegment(sketch, "E345", {"start": v(-14909.05, 2107.45) * mm, "end": v(-14810.27, 2206.24) * mm});
            skLineSegment(sketch, "E346", {"start": v(-14810.27, 2206.24) * mm, "end": v(-14837.21, 2233.18) * mm});
            skLineSegment(sketch, "E347", {"start": v(-14837.21, 2233.18) * mm, "end": v(-14936, 2134.4) * mm});
            skLineSegment(sketch, "E348", {"start": v(-14936, 2134.4) * mm, "end": v(-14909.05, 2107.45) * mm});
            skLineSegment(sketch, "E349", {"start": v(-14837.23, 2233.2) * mm, "end": v(-14864.15, 2260.12) * mm});
            skLineSegment(sketch, "E350", {"start": v(-14864.15, 2260.12) * mm, "end": v(-14962.93, 2161.33) * mm});
            skLineSegment(sketch, "E351", {"start": v(-14962.93, 2161.33) * mm, "end": v(-14936.01, 2134.41) * mm});
            skLineSegment(sketch, "E352", {"start": v(-14936.01, 2134.41) * mm, "end": v(-14837.23, 2233.2) * mm});
            skLineSegment(sketch, "E353", {"start": v(-14046.95, 1245.35) * mm, "end": v(-13948.16, 1344.13) * mm});
            skLineSegment(sketch, "E354", {"start": v(-13948.16, 1344.13) * mm, "end": v(-13921.22, 1317.19) * mm});
            skLineSegment(sketch, "E355", {"start": v(-13921.22, 1317.19) * mm, "end": v(-14020, 1218.4) * mm});
            skLineSegment(sketch, "E356", {"start": v(-14020, 1218.4) * mm, "end": v(-14046.95, 1245.35) * mm});
            skLineSegment(sketch, "E357", {"start": v(-13921.2, 1317.17) * mm, "end": v(-14019.99, 1218.39) * mm});
            skLineSegment(sketch, "E358", {"start": v(-14019.99, 1218.39) * mm, "end": v(-13993.07, 1191.47) * mm});
            skLineSegment(sketch, "E359", {"start": v(-13993.07, 1191.47) * mm, "end": v(-13894.28, 1290.25) * mm});
            skLineSegment(sketch, "E360", {"start": v(-13894.28, 1290.25) * mm, "end": v(-13921.2, 1317.17) * mm});
            skSolve(sketch);
        }
        {
            var Q0;
            Q0 = qSketchRegion(id + "F28", true);
            extrude(context, id + "F29", {"entities" : qUnion([Q0]), "operationType" : NewBodyOperationType.ADD, "depth" : 2352.67 * mm});
        }
        {
            var Q0;
            Q0=makeQuery(id+"F29.opExtrude","CAP_FACE",FACE,{"disambiguationData":[OSD([sQuery(id+"F28.wireOp",EDGE,"E302"),sQuery(id+"F28.wireOp",EDGE,"E303"),sQuery(id+"F28.wireOp",EDGE,"E304"),sQuery(id+"F28.wireOp",EDGE,"E305")])],"isStart":false});
            var sketch = newSketch(context, id + "F30", { "sketchPlane" : qUnion([Q0]) });
            skLineSegment(sketch, "E361", {"start": v(-13810.53, 1206.5) * mm, "end": v(-13810.53, 1066.8) * mm});
            skLineSegment(sketch, "E362", {"start": v(-13810.53, 1066.8) * mm, "end": v(-13868.4, 1066.8) * mm});
            skLineSegment(sketch, "E363", {"start": v(-13868.4, 1066.8) * mm, "end": v(-15087.6, 2286) * mm});
            skLineSegment(sketch, "E364", {"start": v(-15087.6, 2286) * mm, "end": v(-15087.6, 2343.87) * mm});
            skLineSegment(sketch, "E365", {"start": v(-15087.6, 2343.87) * mm, "end": v(-14947.9, 2343.87) * mm});
            skLineSegment(sketch, "E366", {"start": v(-14947.9, 2343.87) * mm, "end": v(-13810.53, 1206.5) * mm});
            skSolve(sketch);
        }
        {
            var Q0;
            Q0 = qSketchRegion(id + "F30", true);
            extrude(context, id + "F31", {"entities" : qUnion([Q0]), "operationType" : NewBodyOperationType.ADD, "depth" : 76.2 * mm});
        }
        {
            var Q0;
            Q0=makeQuery(id+"F31.boolean.opBoolean","MERGE",FACE,{"derivedFrom":[makeQuery(id+"F29.boolean.opBoolean","MERGE",FACE,{"derivedFrom":[makeQuery(id+"F1.opExtrude","SWEPT_FACE",FACE,{"disambiguationData":[OSD([sQuery(id+"F0.wireOp",EDGE,"E3")])]}),makeQuery(id+"F29.opExtrude","SWEPT_FACE",FACE,{"disambiguationData":[OSD([sQuery(id+"F28.wireOp",EDGE,"E303")])]}),makeQuery(id+"F29.opExtrude","SWEPT_FACE",FACE,{"disambiguationData":[OSD([sQuery(id+"F28.wireOp",EDGE,"E310")])]}),makeQuery(id+"F29.opExtrude","SWEPT_FACE",FACE,{"disambiguationData":[OSD([sQuery(id+"F28.wireOp",EDGE,"E322")])]}),makeQuery(id+"F29.opExtrude","SWEPT_FACE",FACE,{"disambiguationData":[OSD([sQuery(id+"F28.wireOp",EDGE,"E325.0.1.3")])]}),makeQuery(id+"F29.opExtrude","SWEPT_FACE",FACE,{"disambiguationData":[OSD([sQuery(id+"F28.wireOp",EDGE,"E325.0.2.3")])]}),makeQuery(id+"F29.opExtrude","SWEPT_FACE",FACE,{"disambiguationData":[OSD([sQuery(id+"F28.wireOp",EDGE,"E328")])]}),makeQuery(id+"F29.opExtrude","SWEPT_FACE",FACE,{"disambiguationData":[OSD([sQuery(id+"F28.wireOp",EDGE,"E331")])]}),makeQuery(id+"F29.opExtrude","SWEPT_FACE",FACE,{"disambiguationData":[OSD([sQuery(id+"F28.wireOp",EDGE,"E339")])]}),makeQuery(id+"F29.opExtrude","SWEPT_FACE",FACE,{"disambiguationData":[OSD([sQuery(id+"F28.wireOp",EDGE,"E348")])]}),makeQuery(id+"F29.opExtrude","SWEPT_FACE",FACE,{"disambiguationData":[OSD([sQuery(id+"F28.wireOp",EDGE,"E351")])]}),makeQuery(id+"F29.opExtrude","SWEPT_FACE",FACE,{"disambiguationData":[OSD([sQuery(id+"F28.wireOp",EDGE,"E356")])]}),makeQuery(id+"F29.opExtrude","SWEPT_FACE",FACE,{"disambiguationData":[OSD([sQuery(id+"F28.wireOp",EDGE,"E358")])]})]}),makeQuery(id+"F31.opExtrude","SWEPT_FACE",FACE,{"disambiguationData":[OSD([sQuery(id+"F30.wireOp",EDGE,"E363")])]})]});
            var sketch = newSketch(context, id + "F32", { "sketchPlane" : qUnion([Q0]) });
            skLineSegment(sketch, "E367", {"start": v(-12032.49, 2184.4) * mm, "end": v(-10813.29, 2184.4) * mm});
            skLineSegment(sketch, "E368", {"start": v(-10775.19, 2184.4) * mm, "end": v(-10775.19, 2095.5) * mm});
            skLineSegment(sketch, "E369", {"start": v(-10775.19, 2095.5) * mm, "end": v(-10813.29, 2095.5) * mm});
            skLineSegment(sketch, "E370", {"start": v(-10813.29, 2095.5) * mm, "end": v(-10813.29, 876.3) * mm});
            skLineSegment(sketch, "E371", {"start": v(-12032.49, 876.3) * mm, "end": v(-12032.49, 2095.5) * mm});
            skLineSegment(sketch, "E372", {"start": v(-12032.49, 2095.5) * mm, "end": v(-12070.59, 2095.5) * mm});
            skLineSegment(sketch, "E373", {"start": v(-12070.59, 2095.5) * mm, "end": v(-12070.59, 2184.4) * mm});
            skLineSegment(sketch, "E374", {"start": v(-12032.49, 876.3) * mm, "end": v(-12032.49, 876.3) * mm});
            skLineSegment(sketch, "E375", {"start": v(-12032.49, 876.3) * mm, "end": v(-12032.49, 838.2) * mm});
            skLineSegment(sketch, "E376", {"start": v(-12032.49, 838.2) * mm, "end": v(-10813.29, 838.2) * mm});
            skLineSegment(sketch, "E377", {"start": v(-10813.29, 838.2) * mm, "end": v(-10813.29, 876.3) * mm});
            skLineSegment(sketch, "E378", {"start": v(-10813.29, 876.3) * mm, "end": v(-10813.29, 876.3) * mm});
            skLineSegment(sketch, "E379", {"start": v(-12070.59, 2184.4) * mm, "end": v(-12070.59, 2390.78) * mm});
            skLineSegment(sketch, "E380", {"start": v(-12070.59, 2390.78) * mm, "end": v(-12032.49, 2390.78) * mm});
            skLineSegment(sketch, "E381", {"start": v(-12032.49, 2390.78) * mm, "end": v(-12032.49, 2184.4) * mm});
            skLineSegment(sketch, "E382", {"start": v(-10813.29, 2184.4) * mm, "end": v(-10813.29, 2390.78) * mm});
            skLineSegment(sketch, "E383", {"start": v(-10813.29, 2390.78) * mm, "end": v(-10775.19, 2390.78) * mm});
            skLineSegment(sketch, "E384", {"start": v(-10775.19, 2390.78) * mm, "end": v(-10775.19, 2184.4) * mm});
            skSolve(sketch);
        }
        {
            var Q0;
            Q0 = qSketchRegion(id + "F32", true);
            extrude(context, id + "F33", {"entities" : qUnion([Q0]), "operationType" : NewBodyOperationType.REMOVE, "oppositeDirection" : true, "depth" : 139.7 * mm});
        }
        {
            var Q0;
            Q0=makeQuery(id+"F29.opExtrude","SWEPT_FACE",FACE,{"disambiguationData":[OSD([sQuery(id+"F28.wireOp",EDGE,"E357")])]});
            var sketch = newSketch(context, id + "F34", { "sketchPlane" : qUnion([Q0]) });
            skLineSegment(sketch, "E385.bottom", {"start": v(8912.4, 876.3) * mm, "end": v(9052.1, 876.3) * mm});
            skLineSegment(sketch, "E385.top", {"start": v(8912.4, 838.23) * mm, "end": v(9052.1, 838.23) * mm});
            skLineSegment(sketch, "E385.left", {"start": v(8912.4, 876.3) * mm, "end": v(8912.4, 838.23) * mm});
            skLineSegment(sketch, "E385.right", {"start": v(9052.1, 876.3) * mm, "end": v(9052.1, 838.23) * mm});
            skLineSegment(sketch, "E386.bottom", {"start": v(8912.4, 2095.53) * mm, "end": v(9052.1, 2095.53) * mm});
            skLineSegment(sketch, "E386.top", {"start": v(8912.4, 2184.37) * mm, "end": v(9052.1, 2184.37) * mm});
            skLineSegment(sketch, "E386.left", {"start": v(8912.4, 2095.53) * mm, "end": v(8912.4, 2184.37) * mm});
            skLineSegment(sketch, "E386.right", {"start": v(9052.1, 2095.53) * mm, "end": v(9052.1, 2184.37) * mm});
            skSolve(sketch);
        }
        {
            var Q0;
            Q0 = qSketchRegion(id + "F34", true);
            var Q1;
            Q1=makeQuery(id+"F29.opExtrude","SWEPT_FACE",FACE,{"disambiguationData":[OSD([sQuery(id+"F28.wireOp",EDGE,"E352")])]});
            extrude(context, id + "F35", {"entities" : qUnion([Q0]), "operationType" : NewBodyOperationType.ADD, "endBound" : BoundingType.UP_TO_SURFACE, "endBoundEntityFace" : qUnion([Q1]), "depth" : 25.4 * mm});
        }
        {
            var Q0;
            Q0=makeQuery(id+"F1.opExtrude","CAP_FACE",FACE,{"disambiguationData":[OSD([sQuery(id+"F0.wireOp",EDGE,"E5"),sQuery(id+"F0.wireOp",EDGE,"E6"),sQuery(id+"F0.wireOp",EDGE,"E13.2"),sQuery(id+"F0.wireOp",EDGE,"E27"),sQuery(id+"F0.wireOp",EDGE,"E29.trimOffspring"),sQuery(id+"F0.wireOp",EDGE,"E30")])],"isStart":false});
            var sketch = newSketch(context, id + "F36", { "sketchPlane" : qUnion([Q0]) });
            skLineSegment(sketch, "E387", {"start": v(-13810.53, 6565.9) * mm, "end": v(-13909.32, 6664.68) * mm});
            skLineSegment(sketch, "E388", {"start": v(-13909.32, 6664.68) * mm, "end": v(-13936.26, 6637.74) * mm});
            skLineSegment(sketch, "E389", {"start": v(-13936.26, 6637.74) * mm, "end": v(-13837.48, 6538.96) * mm});
            skLineSegment(sketch, "E390", {"start": v(-13837.48, 6538.96) * mm, "end": v(-13810.53, 6565.9) * mm});
            skLineSegment(sketch, "E391", {"start": v(-13810.53, 6565.94) * mm, "end": v(-13810.53, 6705.6) * mm});
            skLineSegment(sketch, "E392", {"start": v(-13810.53, 6705.6) * mm, "end": v(-13848.63, 6705.6) * mm});
            skLineSegment(sketch, "E393", {"start": v(-13848.63, 6705.6) * mm, "end": v(-13848.63, 6604.04) * mm});
            skLineSegment(sketch, "E394", {"start": v(-13848.63, 6604.04) * mm, "end": v(-13810.53, 6565.94) * mm});
            skLineSegment(sketch, "E395", {"start": v(-13848.66, 6705.6) * mm, "end": v(-13868.4, 6705.6) * mm});
            skLineSegment(sketch, "E396", {"start": v(-13868.4, 6705.6) * mm, "end": v(-13909.3, 6664.7) * mm});
            skLineSegment(sketch, "E397", {"start": v(-13909.3, 6664.7) * mm, "end": v(-13882.36, 6637.76) * mm});
            skLineSegment(sketch, "E398", {"start": v(-13882.36, 6637.76) * mm, "end": v(-13848.66, 6671.46) * mm});
            skLineSegment(sketch, "E399", {"start": v(-13848.66, 6671.46) * mm, "end": v(-13848.66, 6705.6) * mm});
            skLineSegment(sketch, "E400", {"start": v(-14947.9, 5428.53) * mm, "end": v(-15046.68, 5527.32) * mm});
            skLineSegment(sketch, "E401", {"start": v(-15046.68, 5527.32) * mm, "end": v(-15019.74, 5554.26) * mm});
            skLineSegment(sketch, "E402", {"start": v(-15019.74, 5554.26) * mm, "end": v(-14920.96, 5455.48) * mm});
            skLineSegment(sketch, "E403", {"start": v(-14920.96, 5455.48) * mm, "end": v(-14947.9, 5428.53) * mm});
            skLineSegment(sketch, "E404", {"start": v(-14947.94, 5428.53) * mm, "end": v(-14986.04, 5466.63) * mm});
            skLineSegment(sketch, "E405", {"start": v(-14986.04, 5466.63) * mm, "end": v(-15087.6, 5466.63) * mm});
            skLineSegment(sketch, "E406", {"start": v(-15087.6, 5466.63) * mm, "end": v(-15087.6, 5428.53) * mm});
            skLineSegment(sketch, "E407", {"start": v(-15087.6, 5428.53) * mm, "end": v(-14947.94, 5428.53) * mm});
            skLineSegment(sketch, "E408", {"start": v(-15087.6, 5466.66) * mm, "end": v(-15087.6, 5486.4) * mm});
            skLineSegment(sketch, "E409", {"start": v(-15087.6, 5486.4) * mm, "end": v(-15046.7, 5527.3) * mm});
            skLineSegment(sketch, "E410", {"start": v(-15046.7, 5527.3) * mm, "end": v(-15019.76, 5500.36) * mm});
            skLineSegment(sketch, "E411", {"start": v(-15019.76, 5500.36) * mm, "end": v(-15053.46, 5466.66) * mm});
            skLineSegment(sketch, "E412", {"start": v(-15053.46, 5466.66) * mm, "end": v(-15087.6, 5466.66) * mm});
            skLineSegment(sketch, "E413", {"start": v(-13868.4, 6705.6) * mm, "end": v(-13873.66, 6705.6) * mm, "construction": true});
            skLineSegment(sketch, "E414", {"start": v(-13873.66, 6705.6) * mm, "end": v(-13873.66, 6718.3) * mm, "construction": true});
            skLineSegment(sketch, "E415", {"start": v(-13873.66, 6718.3) * mm, "end": v(-13789.55, 6718.3) * mm, "construction": true});
            skLineSegment(sketch, "E416", {"start": v(-13871.03, 6702.97) * mm, "end": v(-13880.01, 6711.95) * mm, "construction": true});
            skLineSegment(sketch, "E417", {"start": v(-13880.01, 6711.95) * mm, "end": v(-13953.67, 6638.29) * mm, "construction": true});
            skLineSegment(sketch, "E418", {"start": v(-14144.93, 6429.07) * mm, "end": v(-14046.15, 6330.29) * mm});
            skLineSegment(sketch, "E419", {"start": v(-14046.15, 6330.29) * mm, "end": v(-14073.09, 6303.35) * mm});
            skLineSegment(sketch, "E420", {"start": v(-14073.09, 6303.35) * mm, "end": v(-14171.87, 6402.13) * mm});
            skLineSegment(sketch, "E421", {"start": v(-14171.87, 6402.13) * mm, "end": v(-14144.93, 6429.07) * mm});
            skLineSegment(sketch, "E422.1.0.0", {"start": v(-14432.3, 6141.7) * mm, "end": v(-14333.51, 6042.92) * mm});
            skLineSegment(sketch, "E422.1.0.1", {"start": v(-14360.45, 6015.98) * mm, "end": v(-14459.24, 6114.76) * mm});
            skLineSegment(sketch, "E422.1.0.2", {"start": v(-14333.51, 6042.92) * mm, "end": v(-14360.45, 6015.98) * mm});
            skLineSegment(sketch, "E422.1.0.3", {"start": v(-14459.24, 6114.76) * mm, "end": v(-14432.3, 6141.7) * mm});
            skLineSegment(sketch, "E422.2.0.0", {"start": v(-14719.66, 5854.34) * mm, "end": v(-14620.88, 5755.55) * mm});
            skLineSegment(sketch, "E422.2.0.1", {"start": v(-14647.82, 5728.61) * mm, "end": v(-14746.6, 5827.4) * mm});
            skLineSegment(sketch, "E422.2.0.2", {"start": v(-14620.88, 5755.55) * mm, "end": v(-14647.82, 5728.61) * mm});
            skLineSegment(sketch, "E422.2.0.3", {"start": v(-14746.6, 5827.4) * mm, "end": v(-14719.66, 5854.34) * mm});
            skLineSegment(sketch, "E422.direction1", {"start": v(-14073.09, 6303.35) * mm, "end": v(-14360.45, 6015.98) * mm, "construction": true});
            skLineSegment(sketch, "E423", {"start": v(-15019.72, 5554.28) * mm, "end": v(-14920.94, 5455.5) * mm});
            skLineSegment(sketch, "E424", {"start": v(-14920.94, 5455.5) * mm, "end": v(-14894.02, 5482.42) * mm});
            skLineSegment(sketch, "E425", {"start": v(-14894.02, 5482.42) * mm, "end": v(-14992.8, 5581.2) * mm});
            skLineSegment(sketch, "E426", {"start": v(-14992.8, 5581.2) * mm, "end": v(-15019.72, 5554.28) * mm});
            skLineSegment(sketch, "E427", {"start": v(-15087.6, 5486.4) * mm, "end": v(-14909.05, 5664.95) * mm, "construction": true});
            skLineSegment(sketch, "E428", {"start": v(-13868.4, 6705.6) * mm, "end": v(-14046.95, 6527.05) * mm, "construction": true});
            skLineSegment(sketch, "E429", {"start": v(-14046.95, 6527.05) * mm, "end": v(-13948.16, 6428.27) * mm});
            skLineSegment(sketch, "E430", {"start": v(-13948.16, 6428.27) * mm, "end": v(-13921.22, 6455.21) * mm});
            skLineSegment(sketch, "E431", {"start": v(-13921.22, 6455.21) * mm, "end": v(-14020, 6554) * mm});
            skLineSegment(sketch, "E432", {"start": v(-14020, 6554) * mm, "end": v(-14046.95, 6527.05) * mm});
            skLineSegment(sketch, "E433", {"start": v(-14019.99, 6554.01) * mm, "end": v(-13921.2, 6455.23) * mm});
            skLineSegment(sketch, "E434", {"start": v(-13921.2, 6455.23) * mm, "end": v(-13894.28, 6482.15) * mm});
            skLineSegment(sketch, "E435", {"start": v(-13894.28, 6482.15) * mm, "end": v(-13993.07, 6580.93) * mm});
            skLineSegment(sketch, "E436", {"start": v(-13993.07, 6580.93) * mm, "end": v(-14019.99, 6554.01) * mm});
            skLineSegment(sketch, "E437", {"start": v(-14909.05, 5664.95) * mm, "end": v(-14810.27, 5566.16) * mm});
            skLineSegment(sketch, "E438", {"start": v(-14810.27, 5566.16) * mm, "end": v(-14837.21, 5539.22) * mm});
            skLineSegment(sketch, "E439", {"start": v(-14837.21, 5539.22) * mm, "end": v(-14936, 5638) * mm});
            skLineSegment(sketch, "E440", {"start": v(-14936, 5638) * mm, "end": v(-14909.05, 5664.95) * mm});
            skLineSegment(sketch, "E441", {"start": v(-14936.01, 5637.99) * mm, "end": v(-14837.23, 5539.2) * mm});
            skLineSegment(sketch, "E442", {"start": v(-14837.23, 5539.2) * mm, "end": v(-14864.17, 5512.27) * mm});
            skLineSegment(sketch, "E443", {"start": v(-14864.17, 5512.27) * mm, "end": v(-14962.95, 5611.05) * mm});
            skLineSegment(sketch, "E444", {"start": v(-14962.95, 5611.05) * mm, "end": v(-14936.01, 5637.99) * mm});
            skSolve(sketch);
        }
        {
            var Q0;
            Q0 = qSketchRegion(id + "F36", true);
            extrude(context, id + "F37", {"entities" : qUnion([Q0]), "operationType" : NewBodyOperationType.ADD, "depth" : 2352.67 * mm});
        }
        {
            var Q0;
            Q0=makeQuery(id+"F37.opExtrude","CAP_FACE",FACE,{"disambiguationData":[OSD([sQuery(id+"F36.wireOp",EDGE,"E391"),sQuery(id+"F36.wireOp",EDGE,"E392"),sQuery(id+"F36.wireOp",EDGE,"E393"),sQuery(id+"F36.wireOp",EDGE,"E394")])],"isStart":false});
            var sketch = newSketch(context, id + "F38", { "sketchPlane" : qUnion([Q0]) });
            skLineSegment(sketch, "E445", {"start": v(-13810.53, 6705.6) * mm, "end": v(-13868.4, 6705.6) * mm});
            skLineSegment(sketch, "E446", {"start": v(-13868.4, 6705.6) * mm, "end": v(-15087.6, 5486.4) * mm});
            skLineSegment(sketch, "E447", {"start": v(-15087.6, 5486.4) * mm, "end": v(-15087.6, 5428.53) * mm});
            skLineSegment(sketch, "E448", {"start": v(-15087.6, 5428.53) * mm, "end": v(-14947.9, 5428.53) * mm});
            skLineSegment(sketch, "E449", {"start": v(-14947.9, 5428.53) * mm, "end": v(-13810.53, 6565.9) * mm});
            skLineSegment(sketch, "E450", {"start": v(-13810.53, 6565.9) * mm, "end": v(-13810.53, 6705.6) * mm});
            skSolve(sketch);
        }
        {
            var Q0;
            Q0 = qSketchRegion(id + "F38", true);
            extrude(context, id + "F39", {"entities" : qUnion([Q0]), "operationType" : NewBodyOperationType.ADD, "depth" : 76.2 * mm});
        }
        {
            var Q0;
            Q0=makeQuery(id+"F39.boolean.opBoolean","MERGE",FACE,{"derivedFrom":[makeQuery(id+"F37.boolean.opBoolean","MERGE",FACE,{"derivedFrom":[makeQuery(id+"F1.opExtrude","SWEPT_FACE",FACE,{"disambiguationData":[OSD([sQuery(id+"F0.wireOp",EDGE,"E5")])]}),makeQuery(id+"F37.opExtrude","SWEPT_FACE",FACE,{"disambiguationData":[OSD([sQuery(id+"F36.wireOp",EDGE,"E388")])]}),makeQuery(id+"F37.opExtrude","SWEPT_FACE",FACE,{"disambiguationData":[OSD([sQuery(id+"F36.wireOp",EDGE,"E396")])]}),makeQuery(id+"F37.opExtrude","SWEPT_FACE",FACE,{"disambiguationData":[OSD([sQuery(id+"F36.wireOp",EDGE,"E401")])]}),makeQuery(id+"F37.opExtrude","SWEPT_FACE",FACE,{"disambiguationData":[OSD([sQuery(id+"F36.wireOp",EDGE,"E409")])]}),makeQuery(id+"F37.opExtrude","SWEPT_FACE",FACE,{"disambiguationData":[OSD([sQuery(id+"F36.wireOp",EDGE,"E421")])]}),makeQuery(id+"F37.opExtrude","SWEPT_FACE",FACE,{"disambiguationData":[OSD([sQuery(id+"F36.wireOp",EDGE,"E422.1.0.3")])]}),makeQuery(id+"F37.opExtrude","SWEPT_FACE",FACE,{"disambiguationData":[OSD([sQuery(id+"F36.wireOp",EDGE,"E422.2.0.3")])]}),makeQuery(id+"F37.opExtrude","SWEPT_FACE",FACE,{"disambiguationData":[OSD([sQuery(id+"F36.wireOp",EDGE,"E426")])]}),makeQuery(id+"F37.opExtrude","SWEPT_FACE",FACE,{"disambiguationData":[OSD([sQuery(id+"F36.wireOp",EDGE,"E432")])]}),makeQuery(id+"F37.opExtrude","SWEPT_FACE",FACE,{"disambiguationData":[OSD([sQuery(id+"F36.wireOp",EDGE,"E436")])]}),makeQuery(id+"F37.opExtrude","SWEPT_FACE",FACE,{"disambiguationData":[OSD([sQuery(id+"F36.wireOp",EDGE,"E440")])]}),makeQuery(id+"F37.opExtrude","SWEPT_FACE",FACE,{"disambiguationData":[OSD([sQuery(id+"F36.wireOp",EDGE,"E444")])]})]}),makeQuery(id+"F39.opExtrude","SWEPT_FACE",FACE,{"disambiguationData":[OSD([sQuery(id+"F38.wireOp",EDGE,"E446")])]})]});
            var sketch = newSketch(context, id + "F40", { "sketchPlane" : qUnion([Q0]) });
            skLineSegment(sketch, "E451", {"start": v(5317.37, 2390.78) * mm, "end": v(5279.27, 2390.78) * mm});
            skLineSegment(sketch, "E452", {"start": v(5279.27, 2390.78) * mm, "end": v(5279.27, 2095.5) * mm});
            skLineSegment(sketch, "E453", {"start": v(5279.27, 2095.5) * mm, "end": v(5317.37, 2095.5) * mm});
            skLineSegment(sketch, "E454", {"start": v(5317.37, 2095.5) * mm, "end": v(5317.37, 838.2) * mm});
            skLineSegment(sketch, "E455", {"start": v(5317.37, 838.2) * mm, "end": v(6536.57, 838.2) * mm});
            skLineSegment(sketch, "E456", {"start": v(6536.57, 838.2) * mm, "end": v(6536.57, 2095.5) * mm});
            skLineSegment(sketch, "E457", {"start": v(6536.57, 2095.5) * mm, "end": v(6574.67, 2095.5) * mm});
            skLineSegment(sketch, "E458", {"start": v(6574.67, 2095.5) * mm, "end": v(6574.67, 2390.78) * mm});
            skLineSegment(sketch, "E459", {"start": v(6574.67, 2390.78) * mm, "end": v(6536.57, 2390.78) * mm});
            skLineSegment(sketch, "E460", {"start": v(6536.57, 2390.78) * mm, "end": v(6536.57, 2184.4) * mm});
            skLineSegment(sketch, "E461", {"start": v(6536.57, 2184.4) * mm, "end": v(5317.37, 2184.4) * mm});
            skLineSegment(sketch, "E462", {"start": v(5317.37, 2184.4) * mm, "end": v(5317.37, 2390.78) * mm});
            skSolve(sketch);
        }
        {
            var Q0;
            Q0 = qSketchRegion(id + "F40", true);
            extrude(context, id + "F41", {"entities" : qUnion([Q0]), "operationType" : NewBodyOperationType.REMOVE, "oppositeDirection" : true, "depth" : 139.7 * mm});
        }
        {
            var Q0;
            Q0=makeQuery(id+"F37.opExtrude","SWEPT_FACE",FACE,{"disambiguationData":[OSD([sQuery(id+"F36.wireOp",EDGE,"E441")])]});
            var sketch = newSketch(context, id + "F42", { "sketchPlane" : qUnion([Q0]) });
            skLineSegment(sketch, "E463.bottom", {"start": v(14408.31, 2184.37) * mm, "end": v(14548.01, 2184.37) * mm});
            skLineSegment(sketch, "E463.top", {"start": v(14408.31, 2095.53) * mm, "end": v(14548.01, 2095.53) * mm});
            skLineSegment(sketch, "E463.left", {"start": v(14408.31, 2184.37) * mm, "end": v(14408.31, 2095.53) * mm});
            skLineSegment(sketch, "E463.right", {"start": v(14548.01, 2184.37) * mm, "end": v(14548.01, 2095.53) * mm});
            skLineSegment(sketch, "E464.bottom", {"start": v(14408.31, 838.23) * mm, "end": v(14548.01, 838.23) * mm});
            skLineSegment(sketch, "E464.top", {"start": v(14408.31, 876.3) * mm, "end": v(14548.01, 876.3) * mm});
            skLineSegment(sketch, "E464.left", {"start": v(14408.31, 838.23) * mm, "end": v(14408.31, 876.3) * mm});
            skLineSegment(sketch, "E464.right", {"start": v(14548.01, 838.23) * mm, "end": v(14548.01, 876.3) * mm});
            skSolve(sketch);
        }
        {
            var Q0;
            Q0 = qSketchRegion(id + "F42", true);
            var Q1;
            Q1=makeQuery(id+"F37.opExtrude","SWEPT_FACE",FACE,{"disambiguationData":[OSD([sQuery(id+"F36.wireOp",EDGE,"E433")])]});
            extrude(context, id + "F43", {"entities" : qUnion([Q0]), "operationType" : NewBodyOperationType.ADD, "endBound" : BoundingType.UP_TO_SURFACE, "endBoundEntityFace" : qUnion([Q1]), "depth" : 25.4 * mm});
        }
        {
            var Q0;
            Q0=makeQuery(id+"F1.opExtrude","CAP_FACE",FACE,{"disambiguationData":[OSD([sQuery(id+"F0.wireOp",EDGE,"E7"),sQuery(id+"F0.wireOp",EDGE,"E8"),sQuery(id+"F0.wireOp",EDGE,"E34"),sQuery(id+"F0.wireOp",EDGE,"E35.trimOffspring"),sQuery(id+"F0.wireOp",EDGE,"E36")])],"isStart":false});
            var sketch = newSketch(context, id + "F44", { "sketchPlane" : qUnion([Q0]) });
            skLineSegment(sketch, "E465.bottom", {"start": v(-11277.6, 6705.63) * mm, "end": v(-11137.9, 6705.63) * mm});
            skLineSegment(sketch, "E465.top", {"start": v(-11277.6, 6743.7) * mm, "end": v(-11137.9, 6743.7) * mm});
            skLineSegment(sketch, "E465.left", {"start": v(-11277.6, 6705.63) * mm, "end": v(-11277.6, 6743.7) * mm});
            skLineSegment(sketch, "E465.right", {"start": v(-11137.9, 6705.63) * mm, "end": v(-11137.9, 6743.7) * mm});
            skLineSegment(sketch, "E466.bottom", {"start": v(-11137.9, 9855.2) * mm, "end": v(-11277.6, 9855.2) * mm});
            skLineSegment(sketch, "E466.top", {"start": v(-11137.9, 9817.1) * mm, "end": v(-11277.6, 9817.1) * mm});
            skLineSegment(sketch, "E466.left", {"start": v(-11137.9, 9855.2) * mm, "end": v(-11137.9, 9817.1) * mm});
            skLineSegment(sketch, "E466.right", {"start": v(-11277.6, 9855.2) * mm, "end": v(-11277.6, 9817.1) * mm});
            skLineSegment(sketch, "E467.bottom", {"start": v(-11137.9, 9677.4) * mm, "end": v(-11176, 9677.4) * mm});
            skLineSegment(sketch, "E467.top", {"start": v(-11137.9, 9817.07) * mm, "end": v(-11176, 9817.07) * mm});
            skLineSegment(sketch, "E467.left", {"start": v(-11137.9, 9677.4) * mm, "end": v(-11137.9, 9817.07) * mm});
            skLineSegment(sketch, "E467.right", {"start": v(-11176, 9677.4) * mm, "end": v(-11176, 9817.07) * mm});
            skLineSegment(sketch, "E468.bottom", {"start": v(-11277.6, 9467.85) * mm, "end": v(-11137.9, 9467.85) * mm});
            skLineSegment(sketch, "E468.top", {"start": v(-11277.6, 9429.75) * mm, "end": v(-11137.9, 9429.75) * mm});
            skLineSegment(sketch, "E468.left", {"start": v(-11277.6, 9467.85) * mm, "end": v(-11277.6, 9429.75) * mm});
            skLineSegment(sketch, "E468.right", {"start": v(-11137.9, 9467.85) * mm, "end": v(-11137.9, 9429.75) * mm});
            skLineSegment(sketch, "E469.0.1.0", {"start": v(-11277.6, 9061.45) * mm, "end": v(-11137.9, 9061.45) * mm});
            skLineSegment(sketch, "E469.0.1.1", {"start": v(-11277.6, 9023.35) * mm, "end": v(-11137.9, 9023.35) * mm});
            skLineSegment(sketch, "E469.0.1.2", {"start": v(-11277.6, 9061.45) * mm, "end": v(-11277.6, 9023.35) * mm});
            skLineSegment(sketch, "E469.0.1.3", {"start": v(-11137.9, 9061.45) * mm, "end": v(-11137.9, 9023.35) * mm});
            skLineSegment(sketch, "E469.0.2.0", {"start": v(-11277.6, 8655.05) * mm, "end": v(-11137.9, 8655.05) * mm});
            skLineSegment(sketch, "E469.0.2.1", {"start": v(-11277.6, 8616.95) * mm, "end": v(-11137.9, 8616.95) * mm});
            skLineSegment(sketch, "E469.0.2.2", {"start": v(-11277.6, 8655.05) * mm, "end": v(-11277.6, 8616.95) * mm});
            skLineSegment(sketch, "E469.0.2.3", {"start": v(-11137.9, 8655.05) * mm, "end": v(-11137.9, 8616.95) * mm});
            skLineSegment(sketch, "E469.0.3.0", {"start": v(-11277.6, 8248.65) * mm, "end": v(-11137.9, 8248.65) * mm});
            skLineSegment(sketch, "E469.0.3.1", {"start": v(-11277.6, 8210.55) * mm, "end": v(-11137.9, 8210.55) * mm});
            skLineSegment(sketch, "E469.0.3.2", {"start": v(-11277.6, 8248.65) * mm, "end": v(-11277.6, 8210.55) * mm});
            skLineSegment(sketch, "E469.0.3.3", {"start": v(-11137.9, 8248.65) * mm, "end": v(-11137.9, 8210.55) * mm});
            skLineSegment(sketch, "E469.0.4.0", {"start": v(-11277.6, 7842.25) * mm, "end": v(-11137.9, 7842.25) * mm});
            skLineSegment(sketch, "E469.0.4.1", {"start": v(-11277.6, 7804.15) * mm, "end": v(-11137.9, 7804.15) * mm});
            skLineSegment(sketch, "E469.0.4.2", {"start": v(-11277.6, 7842.25) * mm, "end": v(-11277.6, 7804.15) * mm});
            skLineSegment(sketch, "E469.0.4.3", {"start": v(-11137.9, 7842.25) * mm, "end": v(-11137.9, 7804.15) * mm});
            skLineSegment(sketch, "E469.0.5.0", {"start": v(-11277.6, 7435.85) * mm, "end": v(-11137.9, 7435.85) * mm});
            skLineSegment(sketch, "E469.0.5.1", {"start": v(-11277.6, 7397.75) * mm, "end": v(-11137.9, 7397.75) * mm});
            skLineSegment(sketch, "E469.0.5.2", {"start": v(-11277.6, 7435.85) * mm, "end": v(-11277.6, 7397.75) * mm});
            skLineSegment(sketch, "E469.0.5.3", {"start": v(-11137.9, 7435.85) * mm, "end": v(-11137.9, 7397.75) * mm});
            skLineSegment(sketch, "E469.0.6.0", {"start": v(-11277.6, 7029.45) * mm, "end": v(-11137.9, 7029.45) * mm});
            skLineSegment(sketch, "E469.0.6.1", {"start": v(-11277.6, 6991.35) * mm, "end": v(-11137.9, 6991.35) * mm});
            skLineSegment(sketch, "E469.0.6.2", {"start": v(-11277.6, 7029.45) * mm, "end": v(-11277.6, 6991.35) * mm});
            skLineSegment(sketch, "E469.0.6.3", {"start": v(-11137.9, 7029.45) * mm, "end": v(-11137.9, 6991.35) * mm});
            skLineSegment(sketch, "E469.direction1", {"start": v(-11277.6, 9429.75) * mm, "end": v(-11252.2, 9429.75) * mm, "construction": true});
            skLineSegment(sketch, "E469.direction2", {"start": v(-11277.6, 9429.75) * mm, "end": v(-11277.6, 9023.35) * mm, "construction": true});
            skSolve(sketch);
        }
        {
            var Q0;
            Q0 = qSketchRegion(id + "F44", true);
            extrude(context, id + "F45", {"entities" : qUnion([Q0]), "operationType" : NewBodyOperationType.ADD, "depth" : 2352.67 * mm});
        }
        {
            var Q0;
            Q0=makeQuery(id+"F45.opExtrude","CAP_FACE",FACE,{"disambiguationData":[OSD([sQuery(id+"F44.wireOp",EDGE,"E465.bottom"),sQuery(id+"F44.wireOp",EDGE,"E465.top"),sQuery(id+"F44.wireOp",EDGE,"E465.left"),sQuery(id+"F44.wireOp",EDGE,"E465.right")])],"isStart":false});
            var sketch = newSketch(context, id + "F46", { "sketchPlane" : qUnion([Q0]) });
            skLineSegment(sketch, "E470.bottom", {"start": v(-11277.6, 6705.63) * mm, "end": v(-11137.9, 6705.63) * mm});
            skLineSegment(sketch, "E470.top", {"start": v(-11277.6, 9855.2) * mm, "end": v(-11137.9, 9855.2) * mm});
            skLineSegment(sketch, "E470.left", {"start": v(-11277.6, 6705.63) * mm, "end": v(-11277.6, 9855.2) * mm});
            skLineSegment(sketch, "E470.right", {"start": v(-11137.9, 6705.63) * mm, "end": v(-11137.9, 9855.2) * mm});
            skSolve(sketch);
        }
        {
            var Q0;
            Q0 = qSketchRegion(id + "F46", true);
            extrude(context, id + "F47", {"entities" : qUnion([Q0]), "operationType" : NewBodyOperationType.ADD, "depth" : 76.2 * mm});
        }
        {
            var Q0;
            Q0=makeQuery(id+"F1.opExtrude","CAP_FACE",FACE,{"disambiguationData":[OSD([sQuery(id+"F0.wireOp",EDGE,"E9"),sQuery(id+"F0.wireOp",EDGE,"E13.6"),sQuery(id+"F0.wireOp",EDGE,"E39"),sQuery(id+"F0.wireOp",EDGE,"E41.trimOffspring"),sQuery(id+"F0.wireOp",EDGE,"E44")])],"isStart":false});
            var sketch = newSketch(context, id + "F48", { "sketchPlane" : qUnion([Q0]) });
            skLineSegment(sketch, "E471", {"start": v(-1220.18, 9715.5) * mm, "end": v(-1121.4, 9814.28) * mm});
            skLineSegment(sketch, "E472", {"start": v(-1121.4, 9814.28) * mm, "end": v(-1094.45, 9787.34) * mm});
            skLineSegment(sketch, "E473", {"start": v(-1094.45, 9787.34) * mm, "end": v(-1193.24, 9688.56) * mm});
            skLineSegment(sketch, "E474", {"start": v(-1193.24, 9688.56) * mm, "end": v(-1220.18, 9715.5) * mm});
            skLineSegment(sketch, "E475", {"start": v(-1220.18, 9715.54) * mm, "end": v(-1182.08, 9753.64) * mm});
            skLineSegment(sketch, "E476", {"start": v(-1182.08, 9753.64) * mm, "end": v(-1182.08, 9855.2) * mm});
            skLineSegment(sketch, "E477", {"start": v(-1182.08, 9855.2) * mm, "end": v(-1220.18, 9855.2) * mm});
            skLineSegment(sketch, "E478", {"start": v(-1220.18, 9855.2) * mm, "end": v(-1220.18, 9715.54) * mm});
            skLineSegment(sketch, "E479", {"start": v(-1121.41, 9814.3) * mm, "end": v(-1148.35, 9787.36) * mm});
            skLineSegment(sketch, "E480", {"start": v(-1148.35, 9787.36) * mm, "end": v(-1182.05, 9821.06) * mm});
            skLineSegment(sketch, "E481", {"start": v(-1182.05, 9821.06) * mm, "end": v(-1182.05, 9855.2) * mm});
            skLineSegment(sketch, "E482", {"start": v(-1182.05, 9855.2) * mm, "end": v(-1162.31, 9855.2) * mm});
            skLineSegment(sketch, "E483", {"start": v(-1162.31, 9855.2) * mm, "end": v(-1121.41, 9814.3) * mm});
            skLineSegment(sketch, "E484", {"start": v(-1162.31, 9855.2) * mm, "end": v(-1157.05, 9855.2) * mm, "construction": true});
            skLineSegment(sketch, "E485", {"start": v(-1157.05, 9855.2) * mm, "end": v(-1157.05, 9867.9) * mm, "construction": true});
            skLineSegment(sketch, "E486", {"start": v(-1157.05, 9867.9) * mm, "end": v(-1347.83, 9867.9) * mm, "construction": true});
            skLineSegment(sketch, "E487", {"start": v(-1159.68, 9852.57) * mm, "end": v(-1150.7, 9861.55) * mm, "construction": true});
            skLineSegment(sketch, "E488", {"start": v(-1150.7, 9861.55) * mm, "end": v(-1054.88, 9765.73) * mm, "construction": true});
            skLineSegment(sketch, "E489", {"start": v(-885.78, 9578.67) * mm, "end": v(-984.57, 9479.89) * mm});
            skLineSegment(sketch, "E490", {"start": v(-984.57, 9479.89) * mm, "end": v(-957.63, 9452.95) * mm});
            skLineSegment(sketch, "E491", {"start": v(-957.63, 9452.95) * mm, "end": v(-858.84, 9551.73) * mm});
            skLineSegment(sketch, "E492", {"start": v(-858.84, 9551.73) * mm, "end": v(-885.78, 9578.67) * mm});
            skLineSegment(sketch, "E493.1.0.0", {"start": v(-598.42, 9291.3) * mm, "end": v(-697.2, 9192.52) * mm});
            skLineSegment(sketch, "E493.1.0.1", {"start": v(-670.26, 9165.58) * mm, "end": v(-571.48, 9264.36) * mm});
            skLineSegment(sketch, "E493.1.0.2", {"start": v(-571.48, 9264.36) * mm, "end": v(-598.42, 9291.3) * mm});
            skLineSegment(sketch, "E493.1.0.3", {"start": v(-697.2, 9192.52) * mm, "end": v(-670.26, 9165.58) * mm});
            skLineSegment(sketch, "E493.2.0.0", {"start": v(-311.05, 9003.94) * mm, "end": v(-409.83, 8905.15) * mm});
            skLineSegment(sketch, "E493.2.0.1", {"start": v(-382.89, 8878.21) * mm, "end": v(-284.1, 8977) * mm});
            skLineSegment(sketch, "E493.2.0.2", {"start": v(-284.1, 8977) * mm, "end": v(-311.05, 9003.94) * mm});
            skLineSegment(sketch, "E493.2.0.3", {"start": v(-409.83, 8905.15) * mm, "end": v(-382.89, 8878.21) * mm});
            skLineSegment(sketch, "E493.3.0.0", {"start": v(-23.68, 8716.57) * mm, "end": v(-122.46, 8617.78) * mm});
            skLineSegment(sketch, "E493.3.0.1", {"start": v(-95.52, 8590.84) * mm, "end": v(3.26, 8689.63) * mm});
            skLineSegment(sketch, "E493.3.0.2", {"start": v(3.26, 8689.63) * mm, "end": v(-23.68, 8716.57) * mm});
            skLineSegment(sketch, "E493.3.0.3", {"start": v(-122.46, 8617.78) * mm, "end": v(-95.52, 8590.84) * mm});
            skLineSegment(sketch, "E493.4.0.0", {"start": v(263.69, 8429.2) * mm, "end": v(164.9, 8330.42) * mm});
            skLineSegment(sketch, "E493.4.0.1", {"start": v(191.85, 8303.48) * mm, "end": v(290.63, 8402.26) * mm});
            skLineSegment(sketch, "E493.4.0.2", {"start": v(290.63, 8402.26) * mm, "end": v(263.69, 8429.2) * mm});
            skLineSegment(sketch, "E493.4.0.3", {"start": v(164.9, 8330.42) * mm, "end": v(191.85, 8303.48) * mm});
            skLineSegment(sketch, "E493.5.0.0", {"start": v(551.06, 8141.83) * mm, "end": v(452.27, 8043.05) * mm});
            skLineSegment(sketch, "E493.5.0.1", {"start": v(479.21, 8016.1) * mm, "end": v(578, 8114.9) * mm});
            skLineSegment(sketch, "E493.5.0.2", {"start": v(578, 8114.9) * mm, "end": v(551.06, 8141.83) * mm});
            skLineSegment(sketch, "E493.5.0.3", {"start": v(452.27, 8043.05) * mm, "end": v(479.21, 8016.1) * mm});
            skLineSegment(sketch, "E493.6.0.0", {"start": v(838.43, 7854.46) * mm, "end": v(739.64, 7755.68) * mm});
            skLineSegment(sketch, "E493.6.0.1", {"start": v(766.58, 7728.74) * mm, "end": v(865.37, 7827.52) * mm});
            skLineSegment(sketch, "E493.6.0.2", {"start": v(865.37, 7827.52) * mm, "end": v(838.43, 7854.46) * mm});
            skLineSegment(sketch, "E493.6.0.3", {"start": v(739.64, 7755.68) * mm, "end": v(766.58, 7728.74) * mm});
            skLineSegment(sketch, "E493.7.0.0", {"start": v(1125.8, 7567.1) * mm, "end": v(1027.01, 7468.31) * mm});
            skLineSegment(sketch, "E493.7.0.1", {"start": v(1053.95, 7441.37) * mm, "end": v(1152.73, 7540.15) * mm});
            skLineSegment(sketch, "E493.7.0.2", {"start": v(1152.73, 7540.15) * mm, "end": v(1125.8, 7567.1) * mm});
            skLineSegment(sketch, "E493.7.0.3", {"start": v(1027.01, 7468.31) * mm, "end": v(1053.95, 7441.37) * mm});
            skLineSegment(sketch, "E493.8.0.0", {"start": v(1413.16, 7279.73) * mm, "end": v(1314.38, 7180.94) * mm});
            skLineSegment(sketch, "E493.8.0.1", {"start": v(1341.32, 7154) * mm, "end": v(1440.1, 7252.79) * mm});
            skLineSegment(sketch, "E493.8.0.2", {"start": v(1440.1, 7252.79) * mm, "end": v(1413.16, 7279.73) * mm});
            skLineSegment(sketch, "E493.8.0.3", {"start": v(1314.38, 7180.94) * mm, "end": v(1341.32, 7154) * mm});
            skLineSegment(sketch, "E493.9.0.0", {"start": v(1700.53, 6992.36) * mm, "end": v(1601.75, 6893.58) * mm});
            skLineSegment(sketch, "E493.9.0.1", {"start": v(1628.69, 6866.63) * mm, "end": v(1727.47, 6965.42) * mm});
            skLineSegment(sketch, "E493.9.0.2", {"start": v(1727.47, 6965.42) * mm, "end": v(1700.53, 6992.36) * mm});
            skLineSegment(sketch, "E493.9.0.3", {"start": v(1601.75, 6893.58) * mm, "end": v(1628.69, 6866.63) * mm});
            skLineSegment(sketch, "E493.10.0.0", {"start": v(1987.9, 6704.99) * mm, "end": v(1889.12, 6606.2) * mm});
            skLineSegment(sketch, "E493.10.0.1", {"start": v(1916.06, 6579.27) * mm, "end": v(2014.84, 6678.05) * mm});
            skLineSegment(sketch, "E493.10.0.2", {"start": v(2014.84, 6678.05) * mm, "end": v(1987.9, 6704.99) * mm});
            skLineSegment(sketch, "E493.10.0.3", {"start": v(1889.12, 6606.2) * mm, "end": v(1916.06, 6579.27) * mm});
            skLineSegment(sketch, "E493.11.0.0", {"start": v(2275.27, 6417.62) * mm, "end": v(2176.48, 6318.84) * mm});
            skLineSegment(sketch, "E493.11.0.1", {"start": v(2203.42, 6291.9) * mm, "end": v(2302.2, 6390.68) * mm});
            skLineSegment(sketch, "E493.11.0.2", {"start": v(2302.2, 6390.68) * mm, "end": v(2275.27, 6417.62) * mm});
            skLineSegment(sketch, "E493.11.0.3", {"start": v(2176.48, 6318.84) * mm, "end": v(2203.42, 6291.9) * mm});
            skLineSegment(sketch, "E493.12.0.0", {"start": v(2562.63, 6130.25) * mm, "end": v(2463.85, 6031.47) * mm});
            skLineSegment(sketch, "E493.12.0.1", {"start": v(2490.8, 6004.53) * mm, "end": v(2589.58, 6103.31) * mm});
            skLineSegment(sketch, "E493.12.0.2", {"start": v(2589.58, 6103.31) * mm, "end": v(2562.63, 6130.25) * mm});
            skLineSegment(sketch, "E493.12.0.3", {"start": v(2463.85, 6031.47) * mm, "end": v(2490.8, 6004.53) * mm});
            skLineSegment(sketch, "E493.13.0.0", {"start": v(2850, 5842.89) * mm, "end": v(2751.22, 5744.1) * mm});
            skLineSegment(sketch, "E493.13.0.1", {"start": v(2778.16, 5717.16) * mm, "end": v(2876.94, 5815.94) * mm});
            skLineSegment(sketch, "E493.13.0.2", {"start": v(2876.94, 5815.94) * mm, "end": v(2850, 5842.89) * mm});
            skLineSegment(sketch, "E493.13.0.3", {"start": v(2751.22, 5744.1) * mm, "end": v(2778.16, 5717.16) * mm});
            skLineSegment(sketch, "E493.14.0.0", {"start": v(3137.37, 5555.52) * mm, "end": v(3038.59, 5456.73) * mm});
            skLineSegment(sketch, "E493.14.0.1", {"start": v(3065.53, 5429.8) * mm, "end": v(3164.31, 5528.58) * mm});
            skLineSegment(sketch, "E493.14.0.2", {"start": v(3164.31, 5528.58) * mm, "end": v(3137.37, 5555.52) * mm});
            skLineSegment(sketch, "E493.14.0.3", {"start": v(3038.59, 5456.73) * mm, "end": v(3065.53, 5429.8) * mm});
            skLineSegment(sketch, "E493.direction1", {"start": v(-957.63, 9452.95) * mm, "end": v(-670.26, 9165.58) * mm, "construction": true});
            skLineSegment(sketch, "E494", {"start": v(3206.24, 5289.08) * mm, "end": v(3179.32, 5316) * mm});
            skLineSegment(sketch, "E495", {"start": v(3179.32, 5316) * mm, "end": v(3278.1, 5414.78) * mm});
            skLineSegment(sketch, "E496", {"start": v(3278.1, 5414.78) * mm, "end": v(3305.03, 5387.86) * mm});
            skLineSegment(sketch, "E497", {"start": v(3305.03, 5387.86) * mm, "end": v(3206.24, 5289.08) * mm});
            skLineSegment(sketch, "E498", {"start": v(2548.46, 5946.86) * mm, "end": v(2575.4, 5973.8) * mm});
            skLineSegment(sketch, "E499", {"start": v(2575.4, 5973.8) * mm, "end": v(2674.18, 5875.02) * mm});
            skLineSegment(sketch, "E500", {"start": v(2674.18, 5875.02) * mm, "end": v(2647.24, 5848.08) * mm});
            skLineSegment(sketch, "E501", {"start": v(2647.24, 5848.08) * mm, "end": v(2548.46, 5946.86) * mm});
            skLineSegment(sketch, "E502", {"start": v(2656.22, 5892.98) * mm, "end": v(2629.28, 5866.04) * mm, "construction": true});
            skLineSegment(sketch, "E503", {"start": v(2593.36, 5955.85) * mm, "end": v(2566.42, 5928.9) * mm, "construction": true});
            skLineSegment(sketch, "E504", {"start": v(1341.34, 7153.98) * mm, "end": v(1404.18, 7091.14) * mm});
            skLineSegment(sketch, "E505", {"start": v(1341.34, 7153.98) * mm, "end": v(1368.28, 7180.93) * mm});
            skLineSegment(sketch, "E506", {"start": v(1368.28, 7180.93) * mm, "end": v(1431.12, 7118.08) * mm});
            skLineSegment(sketch, "E507", {"start": v(1431.12, 7118.08) * mm, "end": v(1404.18, 7091.14) * mm});
            skLineSegment(sketch, "E508", {"start": v(1314.36, 7180.96) * mm, "end": v(1341.3, 7207.9) * mm});
            skLineSegment(sketch, "E509", {"start": v(1341.3, 7207.9) * mm, "end": v(1278.46, 7270.75) * mm});
            skLineSegment(sketch, "E510", {"start": v(1278.46, 7270.75) * mm, "end": v(1251.52, 7243.8) * mm});
            skLineSegment(sketch, "E511", {"start": v(1251.52, 7243.8) * mm, "end": v(1314.36, 7180.96) * mm});
            skLineSegment(sketch, "E512", {"start": v(569.14, 7926.18) * mm, "end": v(596.08, 7953.12) * mm});
            skLineSegment(sketch, "E513", {"start": v(596.08, 7953.12) * mm, "end": v(694.86, 7854.34) * mm});
            skLineSegment(sketch, "E514", {"start": v(694.86, 7854.34) * mm, "end": v(667.92, 7827.4) * mm});
            skLineSegment(sketch, "E515", {"start": v(667.92, 7827.4) * mm, "end": v(569.14, 7926.18) * mm});
            skLineSegment(sketch, "E516", {"start": v(614.04, 7935.16) * mm, "end": v(587.1, 7908.22) * mm, "construction": true});
            skLineSegment(sketch, "E517", {"start": v(676.9, 7872.3) * mm, "end": v(649.96, 7845.36) * mm, "construction": true});
            skLineSegment(sketch, "E518", {"start": v(1383.27, 7112.05) * mm, "end": v(1410.2, 7139) * mm, "construction": true});
            skLineSegment(sketch, "E519", {"start": v(1347.35, 7201.86) * mm, "end": v(1320.4, 7174.91) * mm, "construction": true});
            skLineSegment(sketch, "E520", {"start": v(1655.65, 6839.68) * mm, "end": v(1754.43, 6938.46) * mm});
            skLineSegment(sketch, "E521", {"start": v(1754.43, 6938.46) * mm, "end": v(1781.35, 6911.54) * mm});
            skLineSegment(sketch, "E522", {"start": v(1781.35, 6911.54) * mm, "end": v(1682.57, 6812.75) * mm});
            skLineSegment(sketch, "E523", {"start": v(1682.57, 6812.75) * mm, "end": v(1655.65, 6839.68) * mm});
            skLineSegment(sketch, "E524", {"start": v(1727.49, 6965.4) * mm, "end": v(1628.7, 6866.62) * mm});
            skLineSegment(sketch, "E525", {"start": v(1628.7, 6866.62) * mm, "end": v(1655.63, 6839.7) * mm});
            skLineSegment(sketch, "E526", {"start": v(1655.63, 6839.7) * mm, "end": v(1754.41, 6938.48) * mm});
            skLineSegment(sketch, "E527", {"start": v(1754.41, 6938.48) * mm, "end": v(1727.49, 6965.4) * mm});
            skLineSegment(sketch, "E528", {"start": v(2005.86, 6489.46) * mm, "end": v(2104.64, 6588.25) * mm});
            skLineSegment(sketch, "E529", {"start": v(2104.64, 6588.25) * mm, "end": v(2131.58, 6561.3) * mm});
            skLineSegment(sketch, "E530", {"start": v(2131.58, 6561.3) * mm, "end": v(2032.8, 6462.52) * mm});
            skLineSegment(sketch, "E531", {"start": v(2032.8, 6462.52) * mm, "end": v(2005.86, 6489.46) * mm});
            skLineSegment(sketch, "E532", {"start": v(2131.6, 6561.29) * mm, "end": v(2032.82, 6462.5) * mm});
            skLineSegment(sketch, "E533", {"start": v(2032.82, 6462.5) * mm, "end": v(2059.74, 6435.58) * mm});
            skLineSegment(sketch, "E534", {"start": v(2059.74, 6435.58) * mm, "end": v(2158.52, 6534.37) * mm});
            skLineSegment(sketch, "E535", {"start": v(2158.52, 6534.37) * mm, "end": v(2131.6, 6561.29) * mm});
            skSolve(sketch);
        }
        {
            var Q0;
            Q0 = qSketchRegion(id + "F48", true);
            extrude(context, id + "F49", {"entities" : qUnion([Q0]), "operationType" : NewBodyOperationType.ADD, "depth" : 2352.67 * mm});
        }
        {
            var Q0;
            Q0=makeQuery(id+"F49.opExtrude","CAP_FACE",FACE,{"disambiguationData":[OSD([sQuery(id+"F48.wireOp",EDGE,"E475"),sQuery(id+"F48.wireOp",EDGE,"E476"),sQuery(id+"F48.wireOp",EDGE,"E477"),sQuery(id+"F48.wireOp",EDGE,"E478")])],"isStart":false});
            var sketch = newSketch(context, id + "F50", { "sketchPlane" : qUnion([Q0]) });
            skLineSegment(sketch, "E536", {"start": v(-1220.18, 9855.2) * mm, "end": v(-1220.18, 9715.5) * mm});
            skLineSegment(sketch, "E537", {"start": v(-1220.18, 9715.5) * mm, "end": v(3206.24, 5289.08) * mm});
            skLineSegment(sketch, "E538", {"start": v(3206.24, 5289.08) * mm, "end": v(3305.03, 5387.86) * mm});
            skLineSegment(sketch, "E539", {"start": v(3305.03, 5387.86) * mm, "end": v(-1162.31, 9855.2) * mm});
            skLineSegment(sketch, "E540", {"start": v(-1162.31, 9855.2) * mm, "end": v(-1220.18, 9855.2) * mm});
            skSolve(sketch);
        }
        {
            var Q0;
            Q0 = qSketchRegion(id + "F50", true);
            extrude(context, id + "F51", {"entities" : qUnion([Q0]), "operationType" : NewBodyOperationType.ADD, "depth" : 76.2 * mm});
        }
        {
            var Q0;
            Q0=makeQuery(id+"F51.boolean.opBoolean","MERGE",FACE,{"derivedFrom":[makeQuery(id+"F49.boolean.opBoolean","MERGE",FACE,{"derivedFrom":[makeQuery(id+"F1.opExtrude","SWEPT_FACE",FACE,{"disambiguationData":[OSD([sQuery(id+"F0.wireOp",EDGE,"E13.6")])]}),makeQuery(id+"F49.opExtrude","SWEPT_FACE",FACE,{"disambiguationData":[OSD([sQuery(id+"F48.wireOp",EDGE,"E474")])]}),makeQuery(id+"F49.opExtrude","SWEPT_FACE",FACE,{"disambiguationData":[OSD([sQuery(id+"F48.wireOp",EDGE,"E490")])]}),makeQuery(id+"F49.opExtrude","SWEPT_FACE",FACE,{"disambiguationData":[OSD([sQuery(id+"F48.wireOp",EDGE,"E493.1.0.3")])]}),makeQuery(id+"F49.opExtrude","SWEPT_FACE",FACE,{"disambiguationData":[OSD([sQuery(id+"F48.wireOp",EDGE,"E493.2.0.3")])]}),makeQuery(id+"F49.opExtrude","SWEPT_FACE",FACE,{"disambiguationData":[OSD([sQuery(id+"F48.wireOp",EDGE,"E493.3.0.3")])]}),makeQuery(id+"F49.opExtrude","SWEPT_FACE",FACE,{"disambiguationData":[OSD([sQuery(id+"F48.wireOp",EDGE,"E493.4.0.3")])]}),makeQuery(id+"F49.opExtrude","SWEPT_FACE",FACE,{"disambiguationData":[OSD([sQuery(id+"F48.wireOp",EDGE,"E493.5.0.3")])]}),makeQuery(id+"F49.opExtrude","SWEPT_FACE",FACE,{"disambiguationData":[OSD([sQuery(id+"F48.wireOp",EDGE,"E493.6.0.3")])]}),makeQuery(id+"F49.opExtrude","SWEPT_FACE",FACE,{"disambiguationData":[OSD([sQuery(id+"F48.wireOp",EDGE,"E493.7.0.3")])]}),makeQuery(id+"F49.opExtrude","SWEPT_FACE",FACE,{"disambiguationData":[OSD([sQuery(id+"F48.wireOp",EDGE,"E493.8.0.3")])]}),makeQuery(id+"F49.opExtrude","SWEPT_FACE",FACE,{"disambiguationData":[OSD([sQuery(id+"F48.wireOp",EDGE,"E493.9.0.3")])]}),makeQuery(id+"F49.opExtrude","SWEPT_FACE",FACE,{"disambiguationData":[OSD([sQuery(id+"F48.wireOp",EDGE,"E493.10.0.3")])]}),makeQuery(id+"F49.opExtrude","SWEPT_FACE",FACE,{"disambiguationData":[OSD([sQuery(id+"F48.wireOp",EDGE,"E493.11.0.3")])]}),makeQuery(id+"F49.opExtrude","SWEPT_FACE",FACE,{"disambiguationData":[OSD([sQuery(id+"F48.wireOp",EDGE,"E493.12.0.3")])]}),makeQuery(id+"F49.opExtrude","SWEPT_FACE",FACE,{"disambiguationData":[OSD([sQuery(id+"F48.wireOp",EDGE,"E493.13.0.3")])]}),makeQuery(id+"F49.opExtrude","SWEPT_FACE",FACE,{"disambiguationData":[OSD([sQuery(id+"F48.wireOp",EDGE,"E493.14.0.3")])]}),makeQuery(id+"F49.opExtrude","SWEPT_FACE",FACE,{"disambiguationData":[OSD([sQuery(id+"F48.wireOp",EDGE,"E494")])]}),makeQuery(id+"F49.opExtrude","SWEPT_FACE",FACE,{"disambiguationData":[OSD([sQuery(id+"F48.wireOp",EDGE,"E501")])]}),makeQuery(id+"F49.opExtrude","SWEPT_FACE",FACE,{"disambiguationData":[OSD([sQuery(id+"F48.wireOp",EDGE,"E504")])]}),makeQuery(id+"F49.opExtrude","SWEPT_FACE",FACE,{"disambiguationData":[OSD([sQuery(id+"F48.wireOp",EDGE,"E511")])]}),makeQuery(id+"F49.opExtrude","SWEPT_FACE",FACE,{"disambiguationData":[OSD([sQuery(id+"F48.wireOp",EDGE,"E515")])]}),makeQuery(id+"F49.opExtrude","SWEPT_FACE",FACE,{"disambiguationData":[OSD([sQuery(id+"F48.wireOp",EDGE,"E523")])]}),makeQuery(id+"F49.opExtrude","SWEPT_FACE",FACE,{"disambiguationData":[OSD([sQuery(id+"F48.wireOp",EDGE,"E525")])]}),makeQuery(id+"F49.opExtrude","SWEPT_FACE",FACE,{"disambiguationData":[OSD([sQuery(id+"F48.wireOp",EDGE,"E531")])]}),makeQuery(id+"F49.opExtrude","SWEPT_FACE",FACE,{"disambiguationData":[OSD([sQuery(id+"F48.wireOp",EDGE,"E533")])]})]}),makeQuery(id+"F51.opExtrude","SWEPT_FACE",FACE,{"disambiguationData":[OSD([sQuery(id+"F50.wireOp",EDGE,"E537")])]})]});
            var sketch = newSketch(context, id + "F52", { "sketchPlane" : qUnion([Q0]) });
            skLineSegment(sketch, "E541", {"start": v(-3665.66, 2390.78) * mm, "end": v(-3665.66, 2095.5) * mm});
            skLineSegment(sketch, "E542", {"start": v(-3665.66, 2095.5) * mm, "end": v(-3627.59, 2095.5) * mm});
            skLineSegment(sketch, "E543", {"start": v(-3627.59, 2095.5) * mm, "end": v(-3627.59, 1333.5) * mm});
            skLineSegment(sketch, "E544", {"start": v(-3627.59, 1333.5) * mm, "end": v(-3170.39, 1333.5) * mm});
            skLineSegment(sketch, "E545", {"start": v(-3170.39, 1333.5) * mm, "end": v(-3170.39, 2095.5) * mm});
            skLineSegment(sketch, "E546", {"start": v(-3170.39, 2095.5) * mm, "end": v(-3132.29, 2095.5) * mm});
            skLineSegment(sketch, "E547", {"start": v(-3132.29, 2095.5) * mm, "end": v(-3132.29, 2390.78) * mm});
            skLineSegment(sketch, "E548", {"start": v(-3132.29, 2390.78) * mm, "end": v(-3170.39, 2390.78) * mm});
            skLineSegment(sketch, "E549", {"start": v(-3170.39, 2390.78) * mm, "end": v(-3170.39, 2184.4) * mm});
            skLineSegment(sketch, "E550", {"start": v(-3170.39, 2184.4) * mm, "end": v(-3627.59, 2184.4) * mm});
            skLineSegment(sketch, "E551", {"start": v(-3627.59, 2184.4) * mm, "end": v(-3627.59, 2390.78) * mm});
            skLineSegment(sketch, "E552", {"start": v(-3627.59, 2390.78) * mm, "end": v(-3665.66, 2390.78) * mm});
            skSolve(sketch);
        }
        {
            var Q0;
            Q0 = qSketchRegion(id + "F52", true);
            extrude(context, id + "F53", {"entities" : qUnion([Q0]), "operationType" : NewBodyOperationType.REMOVE, "oppositeDirection" : true, "depth" : 139.7 * mm});
        }
        {
            var Q0;
            Q0=makeQuery(id+"F49.opExtrude","SWEPT_FACE",FACE,{"disambiguationData":[OSD([sQuery(id+"F48.wireOp",EDGE,"E532")])]});
            var sketch = newSketch(context, id + "F54", { "sketchPlane" : qUnion([Q0]) });
            skLineSegment(sketch, "E553.bottom", {"start": v(-6146.8, 2095.53) * mm, "end": v(-6007.1, 2095.53) * mm});
            skLineSegment(sketch, "E553.top", {"start": v(-6146.8, 2184.37) * mm, "end": v(-6007.1, 2184.37) * mm});
            skLineSegment(sketch, "E553.left", {"start": v(-6146.8, 2095.53) * mm, "end": v(-6146.8, 2184.37) * mm});
            skLineSegment(sketch, "E553.right", {"start": v(-6007.1, 2095.53) * mm, "end": v(-6007.1, 2184.37) * mm});
            skLineSegment(sketch, "E554.bottom", {"start": v(-6146.8, 1333.5) * mm, "end": v(-6007.1, 1333.5) * mm});
            skLineSegment(sketch, "E554.top", {"start": v(-6146.8, 1295.4) * mm, "end": v(-6007.1, 1295.4) * mm});
            skLineSegment(sketch, "E554.left", {"start": v(-6146.8, 1333.5) * mm, "end": v(-6146.8, 1295.4) * mm});
            skLineSegment(sketch, "E554.right", {"start": v(-6007.1, 1333.5) * mm, "end": v(-6007.1, 1295.4) * mm});
            skSolve(sketch);
        }
        {
            var Q0;
            Q0 = qSketchRegion(id + "F54", true);
            var Q1;
            Q1=makeQuery(id+"F49.opExtrude","SWEPT_FACE",FACE,{"disambiguationData":[OSD([sQuery(id+"F48.wireOp",EDGE,"E526")])]});
            extrude(context, id + "F55", {"entities" : qUnion([Q0]), "operationType" : NewBodyOperationType.ADD, "endBound" : BoundingType.UP_TO_SURFACE, "endBoundEntityFace" : qUnion([Q1]), "depth" : 25.4 * mm});
        }
        {
            var Q0;
            Q0=makeQuery(id+"F1.opExtrude","CAP_FACE",FACE,{"disambiguationData":[OSD([sQuery(id+"F0.wireOp",EDGE,"E10"),sQuery(id+"F0.wireOp",EDGE,"R3NqnxSR-PkqM-YKfb-wwZ6-WPldUnmdQ9gS"),sQuery(id+"F0.wireOp",EDGE,"E45"),sQuery(id+"F0.wireOp",EDGE,"E46.trimOffspring"),sQuery(id+"F0.wireOp",EDGE,"c1pFT6Vn-Ejmc-tbf9-30GN-3fvkMUixsVtu")])],"isStart":true});
            var sketch = newSketch(context, id + "F56", { "sketchPlane" : qUnion([Q0]) });
            skSolve(sketch);
        }
        {
            var Q0;
            Q0=makeQuery(id+"F56.imprint","IMPRINT",FACE,{"disambiguationData":[TD([[makeQuery(id+"F56.imprint","IMPRINT",EDGE,{"derivedFrom":makeQuery(id+"F1.opExtrude","CAP_EDGE",EDGE,{"disambiguationData":[OSD([sQuery(id+"F0.wireOp",EDGE,"E10")])],"isStart":true})}),1.0]])]});
            extrude(context, id + "F57", {"entities" : qUnion([Q0]), "operationType" : NewBodyOperationType.ADD, "depth" : 727.07 * mm});
        }
        {
            var Q0;
            Q0=makeQuery(id+"F1.opExtrude","CAP_FACE",FACE,{"disambiguationData":[OSD([sQuery(id+"F0.wireOp",EDGE,"E10"),sQuery(id+"F0.wireOp",EDGE,"R3NqnxSR-PkqM-YKfb-wwZ6-WPldUnmdQ9gS"),sQuery(id+"F0.wireOp",EDGE,"E45"),sQuery(id+"F0.wireOp",EDGE,"E46.trimOffspring"),sQuery(id+"F0.wireOp",EDGE,"c1pFT6Vn-Ejmc-tbf9-30GN-3fvkMUixsVtu")])],"isStart":false});
            var sketch = newSketch(context, id + "F58", { "sketchPlane" : qUnion([Q0]) });
            skLineSegment(sketch, "E555", {"start": v(4535.34, 6420.57) * mm, "end": v(4436.56, 6519.36) * mm});
            skLineSegment(sketch, "E556", {"start": v(4436.56, 6519.36) * mm, "end": v(4436.54, 6519.34) * mm});
            skLineSegment(sketch, "E557", {"start": v(4436.54, 6519.34) * mm, "end": v(4535.32, 6420.56) * mm});
            skLineSegment(sketch, "E558", {"start": v(4535.32, 6420.56) * mm, "end": v(4535.34, 6420.57) * mm});
            skLineSegment(sketch, "E559", {"start": v(4508.38, 6393.61) * mm, "end": v(4409.6, 6492.4) * mm});
            skLineSegment(sketch, "E560", {"start": v(4409.6, 6492.4) * mm, "end": v(4180.62, 6263.42) * mm});
            skLineSegment(sketch, "E561", {"start": v(4180.62, 6263.42) * mm, "end": v(4279.4, 6164.64) * mm});
            skLineSegment(sketch, "E562", {"start": v(4279.4, 6164.64) * mm, "end": v(4508.38, 6393.61) * mm});
            skLineSegment(sketch, "E563", {"start": v(4252.46, 6137.7) * mm, "end": v(4153.68, 6236.48) * mm});
            skLineSegment(sketch, "E564", {"start": v(4153.68, 6236.48) * mm, "end": v(3893.25, 5976.05) * mm});
            skLineSegment(sketch, "E565", {"start": v(3893.25, 5976.05) * mm, "end": v(3992.03, 5877.27) * mm});
            skLineSegment(sketch, "E566", {"start": v(3992.03, 5877.27) * mm, "end": v(4252.46, 6137.7) * mm});
            skLineSegment(sketch, "E567", {"start": v(3965.1, 5850.33) * mm, "end": v(3866.3, 5949.1) * mm});
            skLineSegment(sketch, "E568", {"start": v(3866.3, 5949.1) * mm, "end": v(3718.12, 5800.92) * mm});
            skLineSegment(sketch, "E569", {"start": v(3605.88, 5688.68) * mm, "end": v(3704.67, 5589.9) * mm});
            skLineSegment(sketch, "E570", {"start": v(3704.67, 5589.9) * mm, "end": v(3763.02, 5648.25) * mm});
            skLineSegment(sketch, "E571", {"start": v(3677.72, 5562.96) * mm, "end": v(3578.94, 5661.74) * mm});
            skLineSegment(sketch, "E572", {"start": v(3578.94, 5661.74) * mm, "end": v(3331.98, 5414.78) * mm});
            skLineSegment(sketch, "E573", {"start": v(3331.98, 5414.78) * mm, "end": v(3430.77, 5316) * mm});
            skLineSegment(sketch, "E574", {"start": v(3430.77, 5316) * mm, "end": v(3677.72, 5562.96) * mm});
            skLineSegment(sketch, "E575", {"start": v(3816.9, 5702.13) * mm, "end": v(3718.12, 5800.92) * mm});
            skLineSegment(sketch, "E576", {"start": v(3789.96, 5675.2) * mm, "end": v(3691.18, 5773.98) * mm});
            skLineSegment(sketch, "E577", {"start": v(3789.94, 5675.18) * mm, "end": v(3691.16, 5773.96) * mm});
            skLineSegment(sketch, "E578", {"start": v(3763.02, 5648.25) * mm, "end": v(3664.24, 5747.04) * mm});
            skLineSegment(sketch, "E579.trimOffspring", {"start": v(3816.9, 5702.13) * mm, "end": v(3965.1, 5850.33) * mm});
            skLineSegment(sketch, "E580.trimOffspring", {"start": v(3789.94, 5675.18) * mm, "end": v(3789.96, 5675.2) * mm});
            skLineSegment(sketch, "E581.trimOffspring", {"start": v(3664.24, 5747.04) * mm, "end": v(3605.88, 5688.68) * mm});
            skLineSegment(sketch, "E582.trimOffspring", {"start": v(3691.18, 5773.98) * mm, "end": v(3691.16, 5773.96) * mm});
            skSolve(sketch);
        }
        {
            var Q0;
            Q0 = qSketchRegion(id + "F58", true);
            extrude(context, id + "F59", {"entities" : qUnion([Q0]), "operationType" : NewBodyOperationType.REMOVE, "oppositeDirection" : true, "depth" : 727.07 * mm});
        }
        {
            var Q0;
            {var subQ0=sQuery(id+"F0.wireOp",EDGE,"E46.trimOffspring");var subQ1=sQuery(id+"F0.wireOp",EDGE,"E10");var subQ2=sQuery(id+"F0.wireOp",EDGE,"E65");Q0=makeQuery(id+"F59.boolean.opBoolean","SPLIT",FACE,{"disambiguationData":[TD([makeQuery(id+"F1.opExtrude","SWEPT_FACE",FACE,{"disambiguationData":[OSD([subQ2])]})])],"derivedFrom":makeQuery(id+"F1.opExtrude","CAP_FACE",FACE,{"disambiguationData":[OSD([subQ1,sQuery(id+"F0.wireOp",EDGE,"E45"),subQ0,subQ2])],"isStart":false})});}
            var sketch = newSketch(context, id + "F60", { "sketchPlane" : qUnion([Q0]) });
            skSolve(sketch);
        }
        {
            var Q0;
            {var subQ0=sQuery(id+"F0.wireOp",EDGE,"E65");Q0=makeQuery(id+"F60.imprint","IMPRINT",FACE,{"disambiguationData":[TD([[makeQuery(id+"F60.imprint","IMPRINT",EDGE,{"derivedFrom":makeQuery(id+"F1.opExtrude","CAP_EDGE",EDGE,{"disambiguationData":[OSD([subQ0])],"isStart":false})}),1.0]])]});}
            var Q1;
            {var subQ0=sQuery(id+"F0.wireOp",EDGE,"E46.trimOffspring");var subQ1=sQuery(id+"F0.wireOp",EDGE,"E10");Q1=makeQuery(id+"F59.boolean.opBoolean","SPLIT",FACE,{"disambiguationData":[TD([makeQuery(id+"F59.opExtrude","SWEPT_FACE",FACE,{"disambiguationData":[OSD([sQuery(id+"F58.wireOp",EDGE,"E557")])]})])],"derivedFrom":makeQuery(id+"F1.opExtrude","CAP_FACE",FACE,{"disambiguationData":[OSD([subQ1,sQuery(id+"F0.wireOp",EDGE,"E45"),subQ0,sQuery(id+"F0.wireOp",EDGE,"E65")])],"isStart":false})});}
            var Q2;
            {var subQ0=sQuery(id+"F0.wireOp",EDGE,"E46.trimOffspring");var subQ1=sQuery(id+"F0.wireOp",EDGE,"E10");Q2=makeQuery(id+"F59.boolean.opBoolean","SPLIT",FACE,{"disambiguationData":[TD([makeQuery(id+"F59.opExtrude","SWEPT_FACE",FACE,{"disambiguationData":[OSD([sQuery(id+"F58.wireOp",EDGE,"E561")])]})])],"derivedFrom":makeQuery(id+"F1.opExtrude","CAP_FACE",FACE,{"disambiguationData":[OSD([subQ1,sQuery(id+"F0.wireOp",EDGE,"E45"),subQ0,sQuery(id+"F0.wireOp",EDGE,"E65")])],"isStart":false})});}
            var Q3;
            {var subQ0=sQuery(id+"F0.wireOp",EDGE,"E46.trimOffspring");var subQ1=sQuery(id+"F0.wireOp",EDGE,"E10");Q3=makeQuery(id+"F59.boolean.opBoolean","SPLIT",FACE,{"disambiguationData":[TD([makeQuery(id+"F59.opExtrude","SWEPT_FACE",FACE,{"disambiguationData":[OSD([sQuery(id+"F58.wireOp",EDGE,"E565")])]})])],"derivedFrom":makeQuery(id+"F1.opExtrude","CAP_FACE",FACE,{"disambiguationData":[OSD([subQ1,sQuery(id+"F0.wireOp",EDGE,"E45"),subQ0,sQuery(id+"F0.wireOp",EDGE,"E65")])],"isStart":false})});}
            var Q4;
            {var subQ0=sQuery(id+"F0.wireOp",EDGE,"E46.trimOffspring");var subQ1=sQuery(id+"F0.wireOp",EDGE,"E10");Q4=makeQuery(id+"F59.boolean.opBoolean","SPLIT",FACE,{"disambiguationData":[TD([makeQuery(id+"F59.opExtrude","SWEPT_FACE",FACE,{"disambiguationData":[OSD([sQuery(id+"F58.wireOp",EDGE,"E575")])]})])],"derivedFrom":makeQuery(id+"F1.opExtrude","CAP_FACE",FACE,{"disambiguationData":[OSD([subQ1,sQuery(id+"F0.wireOp",EDGE,"E45"),subQ0,sQuery(id+"F0.wireOp",EDGE,"E65")])],"isStart":false})});}
            var Q5;
            {var subQ0=sQuery(id+"F0.wireOp",EDGE,"E46.trimOffspring");var subQ1=sQuery(id+"F0.wireOp",EDGE,"E10");Q5=makeQuery(id+"F59.boolean.opBoolean","SPLIT",FACE,{"disambiguationData":[TD([makeQuery(id+"F59.opExtrude","SWEPT_FACE",FACE,{"disambiguationData":[OSD([sQuery(id+"F58.wireOp",EDGE,"E577")])]})])],"derivedFrom":makeQuery(id+"F1.opExtrude","CAP_FACE",FACE,{"disambiguationData":[OSD([subQ1,sQuery(id+"F0.wireOp",EDGE,"E45"),subQ0,sQuery(id+"F0.wireOp",EDGE,"E65")])],"isStart":false})});}
            var Q6;
            {var subQ0=sQuery(id+"F0.wireOp",EDGE,"E46.trimOffspring");var subQ1=sQuery(id+"F0.wireOp",EDGE,"E10");Q6=makeQuery(id+"F59.boolean.opBoolean","SPLIT",FACE,{"disambiguationData":[TD([makeQuery(id+"F59.opExtrude","SWEPT_FACE",FACE,{"disambiguationData":[OSD([sQuery(id+"F58.wireOp",EDGE,"E569")])]})])],"derivedFrom":makeQuery(id+"F1.opExtrude","CAP_FACE",FACE,{"disambiguationData":[OSD([subQ1,sQuery(id+"F0.wireOp",EDGE,"E45"),subQ0,sQuery(id+"F0.wireOp",EDGE,"E65")])],"isStart":false})});}
            var Q7;
            {var subQ0=sQuery(id+"F0.wireOp",EDGE,"E46.trimOffspring");var subQ1=sQuery(id+"F0.wireOp",EDGE,"E45");var subQ2=sQuery(id+"F0.wireOp",EDGE,"E10");Q7=makeQuery(id+"F59.boolean.opBoolean","SPLIT",FACE,{"disambiguationData":[TD([makeQuery(id+"F1.opExtrude","SWEPT_FACE",FACE,{"disambiguationData":[OSD([subQ1])]})])],"derivedFrom":makeQuery(id+"F1.opExtrude","CAP_FACE",FACE,{"disambiguationData":[OSD([subQ2,subQ1,subQ0,sQuery(id+"F0.wireOp",EDGE,"E65")])],"isStart":false})});}
            extrude(context, id + "F61", {"entities" : qUnion([Q0, Q1, Q2, Q3, Q4, Q5, Q6, Q7]), "operationType" : NewBodyOperationType.ADD, "depth" : 2352.67 * mm});
        }
        {
            var Q0;
            Q0=makeQuery(id+"F61.opExtrude","CAP_FACE",FACE,{"disambiguationData":[OSD([sQuery(id+"F0.wireOp",EDGE,"E10"),sQuery(id+"F0.wireOp",EDGE,"E46.trimOffspring"),sQuery(id+"F0.wireOp",EDGE,"E65"),sQuery(id+"F58.wireOp",EDGE,"E555")])],"isStart":false});
            var sketch = newSketch(context, id + "F62", { "sketchPlane" : qUnion([Q0]) });
            skLineSegment(sketch, "E583", {"start": v(4562.26, 6447.5) * mm, "end": v(3403.84, 5289.08) * mm});
            skLineSegment(sketch, "E584", {"start": v(3403.84, 5289.08) * mm, "end": v(3305.06, 5387.86) * mm});
            skLineSegment(sketch, "E585", {"start": v(3305.06, 5387.86) * mm, "end": v(4463.48, 6546.28) * mm});
            skLineSegment(sketch, "E586", {"start": v(4463.48, 6546.28) * mm, "end": v(4562.26, 6447.5) * mm});
            skSolve(sketch);
        }
        {
            var Q0;
            Q0 = qSketchRegion(id + "F62", true);
            extrude(context, id + "F63", {"entities" : qUnion([Q0]), "operationType" : NewBodyOperationType.ADD, "depth" : 76.2 * mm});
        }
        {
            var Q0;
            {var subQ0=sQuery(id+"F0.wireOp",EDGE,"E65");var subQ1=sQuery(id+"F0.wireOp",EDGE,"E45");var subQ2=sQuery(id+"F0.wireOp",EDGE,"E10");var subQ4=makeQuery(id+"F57.opExtrude","SWEPT_FACE",FACE,{"disambiguationData":[OSD([subQ2])]});var subQ5=makeQuery(id+"F1.opExtrude","SWEPT_FACE",FACE,{"disambiguationData":[OSD([subQ2])]});var subQ6=makeQuery(id+"F1.opExtrude","CAP_EDGE",EDGE,{"disambiguationData":[OSD([subQ2])],"isStart":false});Q0=makeQuery(id+"F63.boolean.opBoolean","MERGE",FACE,{"derivedFrom":[makeQuery(id+"F61.boolean.opBoolean","MERGE",FACE,{"derivedFrom":[makeQuery(id+"F57.boolean.opBoolean","MERGE",FACE,{"derivedFrom":[subQ5,subQ4]}),makeQuery(id+"F61.opExtrude","SWEPT_FACE",FACE,{"disambiguationData":[OSD([subQ2]),TDD([makeQuery(id+"F59.boolean.opBoolean","SPLIT",EDGE,{"disambiguationData":[TD([makeQuery(id+"F1.opExtrude","SWEPT_FACE",FACE,{"disambiguationData":[OSD([subQ1])]})])],"derivedFrom":subQ6})])]}),makeQuery(id+"F61.opExtrude","SWEPT_FACE",FACE,{"disambiguationData":[OSD([subQ2]),TDD([makeQuery(id+"F59.boolean.opBoolean","SPLIT",EDGE,{"disambiguationData":[TD([makeQuery(id+"F59.opExtrude","SWEPT_FACE",FACE,{"disambiguationData":[OSD([sQuery(id+"F58.wireOp",EDGE,"E557")])]})])],"derivedFrom":subQ6})])]}),makeQuery(id+"F61.opExtrude","SWEPT_FACE",FACE,{"disambiguationData":[OSD([subQ2]),TDD([makeQuery(id+"F59.boolean.opBoolean","SPLIT",EDGE,{"disambiguationData":[TD([makeQuery(id+"F59.opExtrude","SWEPT_FACE",FACE,{"disambiguationData":[OSD([sQuery(id+"F58.wireOp",EDGE,"E561")])]})])],"derivedFrom":subQ6})])]}),makeQuery(id+"F61.opExtrude","SWEPT_FACE",FACE,{"disambiguationData":[OSD([subQ2]),TDD([makeQuery(id+"F59.boolean.opBoolean","SPLIT",EDGE,{"disambiguationData":[TD([makeQuery(id+"F59.opExtrude","SWEPT_FACE",FACE,{"disambiguationData":[OSD([sQuery(id+"F58.wireOp",EDGE,"E565")])]})])],"derivedFrom":subQ6})])]}),makeQuery(id+"F61.opExtrude","SWEPT_FACE",FACE,{"disambiguationData":[OSD([subQ2]),TDD([makeQuery(id+"F59.boolean.opBoolean","SPLIT",EDGE,{"disambiguationData":[TD([makeQuery(id+"F59.opExtrude","SWEPT_FACE",FACE,{"disambiguationData":[OSD([sQuery(id+"F58.wireOp",EDGE,"E575")])]})])],"derivedFrom":subQ6})])]}),makeQuery(id+"F61.opExtrude","SWEPT_FACE",FACE,{"disambiguationData":[OSD([subQ2]),TDD([makeQuery(id+"F59.boolean.opBoolean","SPLIT",EDGE,{"disambiguationData":[TD([makeQuery(id+"F59.opExtrude","SWEPT_FACE",FACE,{"disambiguationData":[OSD([sQuery(id+"F58.wireOp",EDGE,"E569")])]})])],"derivedFrom":subQ6})])]}),makeQuery(id+"F61.opExtrude","SWEPT_FACE",FACE,{"disambiguationData":[OSD([subQ2]),TDD([makeQuery(id+"F59.boolean.opBoolean","SPLIT",EDGE,{"disambiguationData":[TD([makeQuery(id+"F59.opExtrude","SWEPT_FACE",FACE,{"disambiguationData":[OSD([sQuery(id+"F58.wireOp",EDGE,"E577")])]})])],"derivedFrom":subQ6})])]}),makeQuery(id+"F61.opExtrude","SWEPT_FACE",FACE,{"disambiguationData":[OSD([subQ2]),TDD([makeQuery(id+"F60.imprint","IMPRINT",EDGE,{"derivedFrom":makeQuery(id+"F59.boolean.opBoolean","SPLIT",EDGE,{"disambiguationData":[TD([makeQuery(id+"F1.opExtrude","SWEPT_FACE",FACE,{"disambiguationData":[OSD([subQ0])]})])],"derivedFrom":subQ6})})])]})]}),makeQuery(id+"F63.opExtrude","SWEPT_FACE",FACE,{"disambiguationData":[OSD([sQuery(id+"F62.wireOp",EDGE,"E585")])]})]});}
            var sketch = newSketch(context, id + "F64", { "sketchPlane" : qUnion([Q0]) });
            skLineSegment(sketch, "E587", {"start": v(-7746.97, 2390.78) * mm, "end": v(-7746.97, 1292.22) * mm});
            skLineSegment(sketch, "E588", {"start": v(-7746.97, 1292.22) * mm, "end": v(-7708.87, 1292.22) * mm});
            skLineSegment(sketch, "E589", {"start": v(-7708.87, 1292.22) * mm, "end": v(-7708.87, -727.08) * mm});
            skLineSegment(sketch, "E590", {"start": v(-7708.87, -727.08) * mm, "end": v(-6730.97, -727.07) * mm});
            skLineSegment(sketch, "E591", {"start": v(-6730.97, -727.07) * mm, "end": v(-6730.97, 1292.23) * mm});
            skLineSegment(sketch, "E592", {"start": v(-6730.97, 1292.23) * mm, "end": v(-6692.87, 1292.23) * mm});
            skLineSegment(sketch, "E593", {"start": v(-6692.87, 1292.23) * mm, "end": v(-6692.87, 2390.78) * mm});
            skLineSegment(sketch, "E594", {"start": v(-6692.87, 2390.78) * mm, "end": v(-6730.97, 2390.78) * mm});
            skLineSegment(sketch, "E595", {"start": v(-6730.97, 2390.78) * mm, "end": v(-6730.97, 1431.93) * mm});
            skLineSegment(sketch, "E596", {"start": v(-6730.97, 1431.93) * mm, "end": v(-7708.87, 1431.93) * mm});
            skLineSegment(sketch, "E597", {"start": v(-7708.87, 1431.93) * mm, "end": v(-7708.87, 2390.78) * mm});
            skLineSegment(sketch, "E598", {"start": v(-7708.87, 2390.78) * mm, "end": v(-7746.97, 2390.78) * mm});
            skSolve(sketch);
        }
        {
            var Q0;
            Q0 = qSketchRegion(id + "F64", true);
            extrude(context, id + "F65", {"entities" : qUnion([Q0]), "operationType" : NewBodyOperationType.REMOVE, "oppositeDirection" : true, "depth" : 139.7 * mm});
        }
        {
            var Q0;
            {var subQ0=sQuery(id+"F58.wireOp",EDGE,"E577");Q0=makeQuery(id+"F61.boolean.opBoolean","MERGE",FACE,{"derivedFrom":[makeQuery(id+"F59.boolean.opBoolean","COPY",FACE,{"derivedFrom":makeQuery(id+"F59.opExtrude","SWEPT_FACE",FACE,{"disambiguationData":[OSD([subQ0])]})}),makeQuery(id+"F61.opExtrude","SWEPT_FACE",FACE,{"disambiguationData":[OSD([subQ0])]})]});}
            var sketch = newSketch(context, id + "F66", { "sketchPlane" : qUnion([Q0]) });
            skLineSegment(sketch, "E599.bottom", {"start": v(1333.06, 1292.25) * mm, "end": v(1472.76, 1292.25) * mm});
            skLineSegment(sketch, "E599.top", {"start": v(1333.06, 1431.9) * mm, "end": v(1472.76, 1431.9) * mm});
            skLineSegment(sketch, "E599.left", {"start": v(1333.06, 1292.25) * mm, "end": v(1333.06, 1431.9) * mm});
            skLineSegment(sketch, "E599.right", {"start": v(1472.76, 1292.25) * mm, "end": v(1472.76, 1431.9) * mm});
            skSolve(sketch);
        }
        {
            var Q0;
            Q0 = qSketchRegion(id + "F66", true);
            var Q1;
            {var subQ0=sQuery(id+"F58.wireOp",EDGE,"E555");Q1=makeQuery(id+"F61.boolean.opBoolean","MERGE",FACE,{"derivedFrom":[makeQuery(id+"F59.boolean.opBoolean","COPY",FACE,{"derivedFrom":makeQuery(id+"F59.opExtrude","SWEPT_FACE",FACE,{"disambiguationData":[OSD([subQ0])]})}),makeQuery(id+"F61.opExtrude","SWEPT_FACE",FACE,{"disambiguationData":[OSD([subQ0])]})]});}
            extrude(context, id + "F67", {"entities" : qUnion([Q0]), "operationType" : NewBodyOperationType.ADD, "endBound" : BoundingType.UP_TO_SURFACE, "endBoundEntityFace" : qUnion([Q1]), "depth" : 25.4 * mm});
        }
        {
            var Q0;
            Q0=makeQuery(id+"F1.opExtrude","CAP_FACE",FACE,{"disambiguationData":[OSD([sQuery(id+"F0.wireOp",EDGE,"E11"),sQuery(id+"F0.wireOp",EDGE,"E12"),sQuery(id+"F0.wireOp",EDGE,"E13.3"),sQuery(id+"F0.wireOp",EDGE,"E58"),sQuery(id+"F0.wireOp",EDGE,"E61"),sQuery(id+"F0.wireOp",EDGE,"E63.trimOffspring")])],"isStart":true});
            var sketch = newSketch(context, id + "F68", { "sketchPlane" : qUnion([Q0]) });
            skSolve(sketch);
        }
        {
            var Q0;
            Q0=makeQuery(id+"F68.imprint","IMPRINT",FACE,{"disambiguationData":[TD([[makeQuery(id+"F68.imprint","IMPRINT",EDGE,{"derivedFrom":makeQuery(id+"F1.opExtrude","CAP_EDGE",EDGE,{"disambiguationData":[OSD([sQuery(id+"F0.wireOp",EDGE,"E11")])],"isStart":true})}),1.0]])]});
            var Q1;
            {var subQ1=sQuery(id+"F0.wireOp",EDGE,"E46.trimOffspring");var subQ4=sQuery(id+"F0.wireOp",EDGE,"E65");var subQ5=sQuery(id+"F0.wireOp",EDGE,"E45");var subQ6=sQuery(id+"F0.wireOp",EDGE,"E10");var subQ25=makeQuery(id+"F1.opExtrude","SWEPT_FACE",FACE,{"disambiguationData":[OSD([subQ5])]});Q1=makeQuery(id+"F65.boolean.opBoolean","SPLIT",FACE,{"disambiguationData":[TD([subQ25])],"derivedFrom":makeQuery(id+"F57.opExtrude","CAP_FACE",FACE,{"disambiguationData":[OSD([subQ6,subQ5,subQ1,subQ4])],"isStart":false})});}
            extrude(context, id + "F69", {"entities" : qUnion([Q0]), "operationType" : NewBodyOperationType.ADD, "endBound" : BoundingType.UP_TO_SURFACE, "endBoundEntityFace" : qUnion([Q1]), "depth" : 457.2 * mm});
        }
        {
            var Q0;
            Q0=makeQuery(id+"F1.opExtrude","CAP_FACE",FACE,{"disambiguationData":[OSD([sQuery(id+"F0.wireOp",EDGE,"E11"),sQuery(id+"F0.wireOp",EDGE,"E12"),sQuery(id+"F0.wireOp",EDGE,"E13.3"),sQuery(id+"F0.wireOp",EDGE,"E58"),sQuery(id+"F0.wireOp",EDGE,"E61"),sQuery(id+"F0.wireOp",EDGE,"E63.trimOffspring")])],"isStart":false});
            var sketch = newSketch(context, id + "F70", { "sketchPlane" : qUnion([Q0]) });
            skLineSegment(sketch, "E600", {"start": v(4346.75, -4346.75) * mm, "end": v(4247.97, -4247.97) * mm});
            skLineSegment(sketch, "E601", {"start": v(4247.97, -4247.97) * mm, "end": v(4274.91, -4221.03) * mm});
            skLineSegment(sketch, "E602", {"start": v(4274.91, -4221.03) * mm, "end": v(4373.7, -4319.81) * mm});
            skLineSegment(sketch, "E603", {"start": v(4373.7, -4319.81) * mm, "end": v(4346.75, -4346.75) * mm});
            skLineSegment(sketch, "E604", {"start": v(4274.93, -4221.01) * mm, "end": v(4301.87, -4247.95) * mm});
            skLineSegment(sketch, "E605", {"start": v(4301.87, -4247.95) * mm, "end": v(4400.64, -4149.19) * mm});
            skLineSegment(sketch, "E606", {"start": v(4400.64, -4149.19) * mm, "end": v(4373.7, -4122.25) * mm});
            skLineSegment(sketch, "E607", {"start": v(4373.7, -4122.25) * mm, "end": v(4274.93, -4221.01) * mm});
            skLineSegment(sketch, "E608", {"start": v(9950.43, 1256.93) * mm, "end": v(9851.65, 1355.7) * mm});
            skLineSegment(sketch, "E609", {"start": v(9851.65, 1355.7) * mm, "end": v(9824.7, 1328.77) * mm});
            skLineSegment(sketch, "E610", {"start": v(9824.7, 1328.77) * mm, "end": v(9923.5, 1229.99) * mm});
            skLineSegment(sketch, "E611", {"start": v(9923.5, 1229.99) * mm, "end": v(9950.43, 1256.93) * mm});
            skLineSegment(sketch, "E612", {"start": v(9824.7, 1328.75) * mm, "end": v(9851.63, 1301.8) * mm});
            skLineSegment(sketch, "E613", {"start": v(9851.63, 1301.8) * mm, "end": v(9752.87, 1203.04) * mm});
            skLineSegment(sketch, "E614", {"start": v(9752.87, 1203.04) * mm, "end": v(9725.93, 1229.99) * mm});
            skLineSegment(sketch, "E615", {"start": v(9725.93, 1229.99) * mm, "end": v(9824.7, 1328.75) * mm});
            skLineSegment(sketch, "E616", {"start": v(7049.81, -1446.13) * mm, "end": v(7148.6, -1544.91) * mm, "construction": true});
            skLineSegment(sketch, "E617", {"start": v(6896.02, -1599.92) * mm, "end": v(6994.8, -1698.7) * mm});
            skLineSegment(sketch, "E618", {"start": v(6994.8, -1698.7) * mm, "end": v(7021.75, -1671.76) * mm});
            skLineSegment(sketch, "E619", {"start": v(7021.75, -1671.76) * mm, "end": v(6922.96, -1572.98) * mm});
            skLineSegment(sketch, "E620", {"start": v(6922.96, -1572.98) * mm, "end": v(6896.02, -1599.92) * mm});
            skLineSegment(sketch, "E621", {"start": v(7203.6, -1292.34) * mm, "end": v(7302.38, -1391.13) * mm});
            skLineSegment(sketch, "E622", {"start": v(7302.38, -1391.13) * mm, "end": v(7275.44, -1418.07) * mm});
            skLineSegment(sketch, "E623", {"start": v(7275.44, -1418.07) * mm, "end": v(7176.66, -1319.28) * mm});
            skLineSegment(sketch, "E624", {"start": v(7176.66, -1319.28) * mm, "end": v(7203.6, -1292.34) * mm});
            skLineSegment(sketch, "E625", {"start": v(9143.33, 647.4) * mm, "end": v(9242.12, 548.6) * mm});
            skLineSegment(sketch, "E626", {"start": v(9242.12, 548.6) * mm, "end": v(9269.06, 575.55) * mm});
            skLineSegment(sketch, "E627", {"start": v(9269.06, 575.55) * mm, "end": v(9170.27, 674.33) * mm});
            skLineSegment(sketch, "E628", {"start": v(9170.27, 674.33) * mm, "end": v(9143.33, 647.4) * mm});
            skLineSegment(sketch, "E629", {"start": v(4956.29, -3539.65) * mm, "end": v(5055.07, -3638.44) * mm});
            skLineSegment(sketch, "E630", {"start": v(5055.07, -3638.44) * mm, "end": v(5028.13, -3665.38) * mm});
            skLineSegment(sketch, "E631", {"start": v(5028.13, -3665.38) * mm, "end": v(4929.35, -3566.6) * mm});
            skLineSegment(sketch, "E632", {"start": v(4929.35, -3566.6) * mm, "end": v(4956.29, -3539.65) * mm});
            skLineSegment(sketch, "E633", {"start": v(4521.87, -3974.07) * mm, "end": v(4620.65, -4072.86) * mm});
            skLineSegment(sketch, "E634", {"start": v(4620.65, -4072.86) * mm, "end": v(4647.6, -4045.92) * mm});
            skLineSegment(sketch, "E635", {"start": v(4647.6, -4045.92) * mm, "end": v(4548.8, -3947.13) * mm});
            skLineSegment(sketch, "E636", {"start": v(4548.8, -3947.13) * mm, "end": v(4521.87, -3974.07) * mm});
            skLineSegment(sketch, "E637.1.0.0", {"start": v(4934.96, -3758.55) * mm, "end": v(4836.18, -3659.76) * mm});
            skLineSegment(sketch, "E637.1.0.1", {"start": v(4809.24, -3686.7) * mm, "end": v(4908.02, -3785.49) * mm});
            skLineSegment(sketch, "E637.1.0.2", {"start": v(4908.02, -3785.49) * mm, "end": v(4934.96, -3758.55) * mm});
            skLineSegment(sketch, "E637.1.0.3", {"start": v(4836.18, -3659.76) * mm, "end": v(4809.24, -3686.7) * mm});
            skLineSegment(sketch, "E637.2.0.0", {"start": v(5222.33, -3471.18) * mm, "end": v(5123.55, -3372.4) * mm});
            skLineSegment(sketch, "E637.2.0.1", {"start": v(5096.6, -3399.34) * mm, "end": v(5195.39, -3498.12) * mm});
            skLineSegment(sketch, "E637.2.0.2", {"start": v(5195.39, -3498.12) * mm, "end": v(5222.33, -3471.18) * mm});
            skLineSegment(sketch, "E637.2.0.3", {"start": v(5123.55, -3372.4) * mm, "end": v(5096.6, -3399.34) * mm});
            skLineSegment(sketch, "E637.3.0.0", {"start": v(5509.7, -3183.81) * mm, "end": v(5410.91, -3085.03) * mm});
            skLineSegment(sketch, "E637.3.0.1", {"start": v(5383.97, -3111.97) * mm, "end": v(5482.76, -3210.75) * mm});
            skLineSegment(sketch, "E637.3.0.2", {"start": v(5482.76, -3210.75) * mm, "end": v(5509.7, -3183.81) * mm});
            skLineSegment(sketch, "E637.3.0.3", {"start": v(5410.91, -3085.03) * mm, "end": v(5383.97, -3111.97) * mm});
            skLineSegment(sketch, "E637.4.0.0", {"start": v(5797.07, -2896.44) * mm, "end": v(5698.28, -2797.66) * mm});
            skLineSegment(sketch, "E637.4.0.1", {"start": v(5671.34, -2824.6) * mm, "end": v(5770.12, -2923.38) * mm});
            skLineSegment(sketch, "E637.4.0.2", {"start": v(5770.12, -2923.38) * mm, "end": v(5797.07, -2896.44) * mm});
            skLineSegment(sketch, "E637.4.0.3", {"start": v(5698.28, -2797.66) * mm, "end": v(5671.34, -2824.6) * mm});
            skLineSegment(sketch, "E637.5.0.0", {"start": v(6084.43, -2609.07) * mm, "end": v(5985.65, -2510.3) * mm});
            skLineSegment(sketch, "E637.5.0.1", {"start": v(5958.7, -2537.23) * mm, "end": v(6057.5, -2636.01) * mm});
            skLineSegment(sketch, "E637.5.0.2", {"start": v(6057.5, -2636.01) * mm, "end": v(6084.43, -2609.07) * mm});
            skLineSegment(sketch, "E637.5.0.3", {"start": v(5985.65, -2510.3) * mm, "end": v(5958.7, -2537.23) * mm});
            skLineSegment(sketch, "E637.6.0.0", {"start": v(6371.8, -2321.7) * mm, "end": v(6273.02, -2222.92) * mm});
            skLineSegment(sketch, "E637.6.0.1", {"start": v(6246.08, -2249.86) * mm, "end": v(6344.86, -2348.65) * mm});
            skLineSegment(sketch, "E637.6.0.2", {"start": v(6344.86, -2348.65) * mm, "end": v(6371.8, -2321.7) * mm});
            skLineSegment(sketch, "E637.6.0.3", {"start": v(6273.02, -2222.92) * mm, "end": v(6246.08, -2249.86) * mm});
            skLineSegment(sketch, "E637.7.0.0", {"start": v(6659.17, -2034.34) * mm, "end": v(6560.39, -1935.55) * mm});
            skLineSegment(sketch, "E637.7.0.1", {"start": v(6533.45, -1962.5) * mm, "end": v(6632.23, -2061.28) * mm});
            skLineSegment(sketch, "E637.7.0.2", {"start": v(6632.23, -2061.28) * mm, "end": v(6659.17, -2034.34) * mm});
            skLineSegment(sketch, "E637.7.0.3", {"start": v(6560.39, -1935.55) * mm, "end": v(6533.45, -1962.5) * mm});
            skLineSegment(sketch, "E637.8.0.0", {"start": v(6946.54, -1746.97) * mm, "end": v(6847.76, -1648.19) * mm});
            skLineSegment(sketch, "E637.8.0.1", {"start": v(6820.81, -1675.13) * mm, "end": v(6919.6, -1773.91) * mm});
            skLineSegment(sketch, "E637.8.0.2", {"start": v(6919.6, -1773.91) * mm, "end": v(6946.54, -1746.97) * mm});
            skLineSegment(sketch, "E637.8.0.3", {"start": v(6847.76, -1648.19) * mm, "end": v(6820.81, -1675.13) * mm});
            skLineSegment(sketch, "E637.10.0.0", {"start": v(7521.27, -1172.23) * mm, "end": v(7422.5, -1073.45) * mm});
            skLineSegment(sketch, "E637.10.0.1", {"start": v(7395.55, -1100.4) * mm, "end": v(7494.33, -1199.17) * mm});
            skLineSegment(sketch, "E637.10.0.2", {"start": v(7494.33, -1199.17) * mm, "end": v(7521.27, -1172.23) * mm});
            skLineSegment(sketch, "E637.10.0.3", {"start": v(7422.5, -1073.45) * mm, "end": v(7395.55, -1100.4) * mm});
            skLineSegment(sketch, "E637.11.0.0", {"start": v(7808.64, -884.86) * mm, "end": v(7709.86, -786.08) * mm});
            skLineSegment(sketch, "E637.11.0.1", {"start": v(7682.92, -813.02) * mm, "end": v(7781.7, -911.8) * mm});
            skLineSegment(sketch, "E637.11.0.2", {"start": v(7781.7, -911.8) * mm, "end": v(7808.64, -884.86) * mm});
            skLineSegment(sketch, "E637.11.0.3", {"start": v(7709.86, -786.08) * mm, "end": v(7682.92, -813.02) * mm});
            skLineSegment(sketch, "E637.12.0.0", {"start": v(8096.01, -597.5) * mm, "end": v(7997.23, -498.71) * mm});
            skLineSegment(sketch, "E637.12.0.1", {"start": v(7970.29, -525.65) * mm, "end": v(8069.07, -624.44) * mm});
            skLineSegment(sketch, "E637.12.0.2", {"start": v(8069.07, -624.44) * mm, "end": v(8096.01, -597.5) * mm});
            skLineSegment(sketch, "E637.12.0.3", {"start": v(7997.23, -498.71) * mm, "end": v(7970.29, -525.65) * mm});
            skLineSegment(sketch, "E637.13.0.0", {"start": v(8383.38, -310.13) * mm, "end": v(8284.6, -211.35) * mm});
            skLineSegment(sketch, "E637.13.0.1", {"start": v(8257.66, -238.29) * mm, "end": v(8356.44, -337.07) * mm});
            skLineSegment(sketch, "E637.13.0.2", {"start": v(8356.44, -337.07) * mm, "end": v(8383.38, -310.13) * mm});
            skLineSegment(sketch, "E637.13.0.3", {"start": v(8284.6, -211.35) * mm, "end": v(8257.66, -238.29) * mm});
            skLineSegment(sketch, "E637.14.0.0", {"start": v(8670.75, -22.76) * mm, "end": v(8571.96, 76.02) * mm});
            skLineSegment(sketch, "E637.14.0.1", {"start": v(8545.02, 49.08) * mm, "end": v(8643.8, -49.7) * mm});
            skLineSegment(sketch, "E637.14.0.2", {"start": v(8643.8, -49.7) * mm, "end": v(8670.75, -22.76) * mm});
            skLineSegment(sketch, "E637.14.0.3", {"start": v(8571.96, 76.02) * mm, "end": v(8545.02, 49.08) * mm});
            skLineSegment(sketch, "E637.15.0.0", {"start": v(8958.12, 264.6) * mm, "end": v(8859.33, 363.4) * mm});
            skLineSegment(sketch, "E637.15.0.1", {"start": v(8832.4, 336.45) * mm, "end": v(8931.17, 237.67) * mm});
            skLineSegment(sketch, "E637.15.0.2", {"start": v(8931.17, 237.67) * mm, "end": v(8958.12, 264.6) * mm});
            skLineSegment(sketch, "E637.15.0.3", {"start": v(8859.33, 363.4) * mm, "end": v(8832.4, 336.45) * mm});
            skLineSegment(sketch, "E637.16.0.0", {"start": v(9245.48, 551.98) * mm, "end": v(9146.7, 650.76) * mm, "construction": true});
            skLineSegment(sketch, "E637.16.0.1", {"start": v(9119.76, 623.82) * mm, "end": v(9218.54, 525.04) * mm, "construction": true});
            skLineSegment(sketch, "E637.16.0.2", {"start": v(9218.54, 525.04) * mm, "end": v(9245.48, 551.98) * mm, "construction": true});
            skLineSegment(sketch, "E637.16.0.3", {"start": v(9146.7, 650.76) * mm, "end": v(9119.76, 623.82) * mm, "construction": true});
            skLineSegment(sketch, "E637.17.0.0", {"start": v(9532.85, 839.34) * mm, "end": v(9434.07, 938.13) * mm});
            skLineSegment(sketch, "E637.17.0.1", {"start": v(9407.13, 911.19) * mm, "end": v(9505.91, 812.4) * mm});
            skLineSegment(sketch, "E637.17.0.2", {"start": v(9505.91, 812.4) * mm, "end": v(9532.85, 839.34) * mm});
            skLineSegment(sketch, "E637.17.0.3", {"start": v(9434.07, 938.13) * mm, "end": v(9407.13, 911.19) * mm});
            skLineSegment(sketch, "E637.18.0.0", {"start": v(9820.22, 1126.71) * mm, "end": v(9721.44, 1225.5) * mm});
            skLineSegment(sketch, "E637.18.0.1", {"start": v(9694.5, 1198.55) * mm, "end": v(9793.28, 1099.77) * mm});
            skLineSegment(sketch, "E637.18.0.2", {"start": v(9793.28, 1099.77) * mm, "end": v(9820.22, 1126.71) * mm});
            skLineSegment(sketch, "E637.18.0.3", {"start": v(9721.44, 1225.5) * mm, "end": v(9694.5, 1198.55) * mm});
            skLineSegment(sketch, "E637.direction1", {"start": v(4620.65, -4072.86) * mm, "end": v(4908.02, -3785.49) * mm, "construction": true});
            skLineSegment(sketch, "E638", {"start": v(4929.33, -3566.61) * mm, "end": v(5028.11, -3665.4) * mm});
            skLineSegment(sketch, "E639", {"start": v(5028.11, -3665.4) * mm, "end": v(5001.19, -3692.32) * mm});
            skLineSegment(sketch, "E640", {"start": v(5001.19, -3692.32) * mm, "end": v(4902.4, -3593.53) * mm});
            skLineSegment(sketch, "E641", {"start": v(4902.4, -3593.53) * mm, "end": v(4929.33, -3566.61) * mm});
            skLineSegment(sketch, "E642", {"start": v(4902.39, -3593.55) * mm, "end": v(5001.17, -3692.34) * mm});
            skLineSegment(sketch, "E643", {"start": v(5001.17, -3692.34) * mm, "end": v(4974.25, -3719.26) * mm});
            skLineSegment(sketch, "E644", {"start": v(4974.25, -3719.26) * mm, "end": v(4875.47, -3620.48) * mm});
            skLineSegment(sketch, "E645", {"start": v(4875.47, -3620.48) * mm, "end": v(4902.39, -3593.55) * mm});
            skLineSegment(sketch, "E646", {"start": v(6922.98, -1572.96) * mm, "end": v(7021.77, -1671.74) * mm});
            skLineSegment(sketch, "E647", {"start": v(7021.77, -1671.74) * mm, "end": v(7048.69, -1644.82) * mm});
            skLineSegment(sketch, "E648", {"start": v(7048.69, -1644.82) * mm, "end": v(6949.9, -1546.04) * mm});
            skLineSegment(sketch, "E649", {"start": v(6949.9, -1546.04) * mm, "end": v(6922.98, -1572.96) * mm});
            skLineSegment(sketch, "E650", {"start": v(6949.92, -1546.02) * mm, "end": v(7048.7, -1644.8) * mm});
            skLineSegment(sketch, "E651", {"start": v(7048.7, -1644.8) * mm, "end": v(7075.63, -1617.88) * mm});
            skLineSegment(sketch, "E652", {"start": v(7075.63, -1617.88) * mm, "end": v(6976.85, -1519.1) * mm});
            skLineSegment(sketch, "E653", {"start": v(6976.85, -1519.1) * mm, "end": v(6949.92, -1546.02) * mm});
            skLineSegment(sketch, "E654", {"start": v(7176.64, -1319.3) * mm, "end": v(7275.42, -1418.09) * mm});
            skLineSegment(sketch, "E655", {"start": v(7275.42, -1418.09) * mm, "end": v(7248.5, -1445) * mm});
            skLineSegment(sketch, "E656", {"start": v(7248.5, -1445) * mm, "end": v(7149.72, -1346.23) * mm});
            skLineSegment(sketch, "E657", {"start": v(7149.72, -1346.23) * mm, "end": v(7176.64, -1319.3) * mm});
            skLineSegment(sketch, "E658", {"start": v(7149.7, -1346.24) * mm, "end": v(7248.48, -1445.03) * mm});
            skLineSegment(sketch, "E659", {"start": v(7248.48, -1445.03) * mm, "end": v(7221.56, -1471.95) * mm});
            skLineSegment(sketch, "E660", {"start": v(7221.56, -1471.95) * mm, "end": v(7122.78, -1373.17) * mm});
            skLineSegment(sketch, "E661", {"start": v(7122.78, -1373.17) * mm, "end": v(7149.7, -1346.24) * mm});
            skLineSegment(sketch, "E662", {"start": v(7122.76, -1373.18) * mm, "end": v(7221.54, -1471.97) * mm});
            skLineSegment(sketch, "E663", {"start": v(7221.54, -1471.97) * mm, "end": v(7194.62, -1498.89) * mm});
            skLineSegment(sketch, "E664", {"start": v(7194.62, -1498.89) * mm, "end": v(7095.83, -1400.1) * mm});
            skLineSegment(sketch, "E665", {"start": v(7095.83, -1400.1) * mm, "end": v(7122.76, -1373.18) * mm});
            skLineSegment(sketch, "E666", {"start": v(9170.3, 674.35) * mm, "end": v(9269.07, 575.57) * mm});
            skLineSegment(sketch, "E667", {"start": v(9269.07, 575.57) * mm, "end": v(9296, 602.49) * mm});
            skLineSegment(sketch, "E668", {"start": v(9296, 602.49) * mm, "end": v(9197.21, 701.27) * mm});
            skLineSegment(sketch, "E669", {"start": v(9197.21, 701.27) * mm, "end": v(9170.3, 674.35) * mm});
            skLineSegment(sketch, "E670", {"start": v(9197.23, 701.3) * mm, "end": v(9296.02, 602.5) * mm});
            skLineSegment(sketch, "E671", {"start": v(9296.02, 602.5) * mm, "end": v(9322.94, 629.43) * mm});
            skLineSegment(sketch, "E672", {"start": v(9322.94, 629.43) * mm, "end": v(9224.16, 728.21) * mm});
            skLineSegment(sketch, "E673", {"start": v(9224.16, 728.21) * mm, "end": v(9197.23, 701.3) * mm});
            skLineSegment(sketch, "E674", {"start": v(6780.68, -1581.1) * mm, "end": v(7068.04, -1293.74) * mm, "construction": true});
            skLineSegment(sketch, "E675", {"start": v(7068.04, -1293.74) * mm, "end": v(7105.17, -1330.87) * mm, "construction": true});
            skLineSegment(sketch, "E676", {"start": v(7041.1, -1320.68) * mm, "end": v(7077.37, -1356.94) * mm, "construction": true});
            skLineSegment(sketch, "E677", {"start": v(7095.82, -1400.13) * mm, "end": v(7194.6, -1498.9) * mm});
            skLineSegment(sketch, "E678", {"start": v(7194.6, -1498.9) * mm, "end": v(7167.68, -1525.83) * mm});
            skLineSegment(sketch, "E679", {"start": v(7167.68, -1525.83) * mm, "end": v(7068.9, -1427.05) * mm});
            skLineSegment(sketch, "E680", {"start": v(7068.9, -1427.05) * mm, "end": v(7095.82, -1400.13) * mm});
            skLineSegment(sketch, "E681", {"start": v(6976.86, -1519.08) * mm, "end": v(7075.65, -1617.86) * mm});
            skLineSegment(sketch, "E682", {"start": v(7075.65, -1617.86) * mm, "end": v(7102.57, -1590.94) * mm});
            skLineSegment(sketch, "E683", {"start": v(7102.57, -1590.94) * mm, "end": v(7003.79, -1492.15) * mm});
            skLineSegment(sketch, "E684", {"start": v(7003.79, -1492.15) * mm, "end": v(6976.86, -1519.08) * mm});
            skLineSegment(sketch, "E685", {"start": v(7003.8, -1492.14) * mm, "end": v(7102.59, -1590.92) * mm});
            skLineSegment(sketch, "E686", {"start": v(7102.59, -1590.92) * mm, "end": v(7129.51, -1564) * mm});
            skLineSegment(sketch, "E687", {"start": v(7129.51, -1564) * mm, "end": v(7030.73, -1465.21) * mm});
            skLineSegment(sketch, "E688", {"start": v(7030.73, -1465.21) * mm, "end": v(7003.8, -1492.14) * mm});
            skLineSegment(sketch, "E689", {"start": v(7036.34, -1459.6) * mm, "end": v(7135.12, -1558.38) * mm});
            skLineSegment(sketch, "E690", {"start": v(7135.12, -1558.38) * mm, "end": v(7162.06, -1531.44) * mm});
            skLineSegment(sketch, "E691", {"start": v(7162.06, -1531.44) * mm, "end": v(7063.28, -1432.66) * mm});
            skLineSegment(sketch, "E692", {"start": v(7063.28, -1432.66) * mm, "end": v(7036.34, -1459.6) * mm});
            skSolve(sketch);
        }
        {
            var Q0;
            Q0 = qSketchRegion(id + "F70", true);
            extrude(context, id + "F71", {"entities" : qUnion([Q0]), "operationType" : NewBodyOperationType.ADD, "depth" : 2352.67 * mm});
        }
        {
            var Q0;
            {var subQ0=sQuery(id+"F0.wireOp",EDGE,"E11");var subQ1=sQuery(id+"F0.wireOp",EDGE,"E61");var subQ2=sQuery(id+"F0.wireOp",EDGE,"E58");var subQ3=sQuery(id+"F0.wireOp",EDGE,"E13.3");Q0=makeQuery(id+"F71.boolean.opBoolean","SPLIT",FACE,{"disambiguationData":[TD([makeQuery(id+"F71.opExtrude","SWEPT_FACE",FACE,{"disambiguationData":[OSD([sQuery(id+"F70.wireOp",EDGE,"E602")])]})])],"derivedFrom":makeQuery(id+"F1.opExtrude","CAP_FACE",FACE,{"disambiguationData":[OSD([subQ0,sQuery(id+"F0.wireOp",EDGE,"E12"),subQ3,subQ2,subQ1,sQuery(id+"F0.wireOp",EDGE,"E63.trimOffspring")])],"isStart":false})});}
            var sketch = newSketch(context, id + "F72", { "sketchPlane" : qUnion([Q0]) });
            skLineSegment(sketch, "E693", {"start": v(4373.7, -4319.81) * mm, "end": v(4274.91, -4221.03) * mm});
            skLineSegment(sketch, "E694", {"start": v(4274.91, -4221.03) * mm, "end": v(4274.93, -4221.01) * mm});
            skLineSegment(sketch, "E695", {"start": v(4274.93, -4221.01) * mm, "end": v(4301.87, -4247.95) * mm});
            skLineSegment(sketch, "E696", {"start": v(4301.87, -4247.95) * mm, "end": v(4400.64, -4149.19) * mm});
            skLineSegment(sketch, "E697", {"start": v(4400.64, -4149.19) * mm, "end": v(4373.7, -4122.25) * mm});
            skLineSegment(sketch, "E698", {"start": v(4373.7, -4122.25) * mm, "end": v(4521.87, -3974.07) * mm});
            skLineSegment(sketch, "E699", {"start": v(4521.87, -3974.07) * mm, "end": v(4620.65, -4072.86) * mm});
            skLineSegment(sketch, "E700", {"start": v(4620.65, -4072.86) * mm, "end": v(4373.7, -4319.81) * mm});
            skLineSegment(sketch, "E701", {"start": v(4548.8, -3947.13) * mm, "end": v(4647.6, -4045.92) * mm});
            skLineSegment(sketch, "E702", {"start": v(4647.6, -4045.92) * mm, "end": v(4908.02, -3785.49) * mm});
            skLineSegment(sketch, "E703", {"start": v(4908.02, -3785.49) * mm, "end": v(4809.24, -3686.7) * mm});
            skLineSegment(sketch, "E704", {"start": v(4809.24, -3686.7) * mm, "end": v(4548.8, -3947.13) * mm});
            skLineSegment(sketch, "E705", {"start": v(4836.18, -3659.76) * mm, "end": v(4934.96, -3758.55) * mm});
            skLineSegment(sketch, "E706", {"start": v(4934.96, -3758.55) * mm, "end": v(4974.25, -3719.26) * mm});
            skLineSegment(sketch, "E707", {"start": v(4974.25, -3719.26) * mm, "end": v(4875.47, -3620.48) * mm});
            skLineSegment(sketch, "E708", {"start": v(4875.47, -3620.48) * mm, "end": v(4836.18, -3659.76) * mm});
            skLineSegment(sketch, "E709", {"start": v(4902.39, -3593.55) * mm, "end": v(4902.4, -3593.53) * mm});
            skLineSegment(sketch, "E710", {"start": v(4902.4, -3593.53) * mm, "end": v(5001.19, -3692.32) * mm});
            skLineSegment(sketch, "E711", {"start": v(5001.19, -3692.32) * mm, "end": v(5001.17, -3692.34) * mm});
            skLineSegment(sketch, "E712", {"start": v(5001.17, -3692.34) * mm, "end": v(4902.39, -3593.55) * mm});
            skLineSegment(sketch, "E713", {"start": v(4929.33, -3566.61) * mm, "end": v(4929.35, -3566.6) * mm});
            skLineSegment(sketch, "E714", {"start": v(4929.35, -3566.6) * mm, "end": v(5028.13, -3665.38) * mm});
            skLineSegment(sketch, "E715", {"start": v(5028.13, -3665.38) * mm, "end": v(5028.11, -3665.4) * mm});
            skLineSegment(sketch, "E716", {"start": v(5028.11, -3665.4) * mm, "end": v(4929.33, -3566.61) * mm});
            skLineSegment(sketch, "E717", {"start": v(4956.29, -3539.65) * mm, "end": v(5055.07, -3638.44) * mm});
            skLineSegment(sketch, "E718", {"start": v(5055.07, -3638.44) * mm, "end": v(5195.39, -3498.12) * mm});
            skLineSegment(sketch, "E719", {"start": v(5195.39, -3498.12) * mm, "end": v(5096.6, -3399.34) * mm});
            skLineSegment(sketch, "E720", {"start": v(5096.6, -3399.34) * mm, "end": v(4956.29, -3539.65) * mm});
            skLineSegment(sketch, "E721", {"start": v(5123.55, -3372.4) * mm, "end": v(5222.33, -3471.18) * mm});
            skLineSegment(sketch, "E722", {"start": v(5222.33, -3471.18) * mm, "end": v(5482.76, -3210.75) * mm});
            skLineSegment(sketch, "E723", {"start": v(5482.76, -3210.75) * mm, "end": v(5383.97, -3111.97) * mm});
            skLineSegment(sketch, "E724", {"start": v(5383.97, -3111.97) * mm, "end": v(5123.55, -3372.4) * mm});
            skLineSegment(sketch, "E725", {"start": v(5410.91, -3085.03) * mm, "end": v(5509.7, -3183.81) * mm});
            skLineSegment(sketch, "E726", {"start": v(5509.7, -3183.81) * mm, "end": v(5770.12, -2923.38) * mm});
            skLineSegment(sketch, "E727", {"start": v(5770.12, -2923.38) * mm, "end": v(5671.34, -2824.6) * mm});
            skLineSegment(sketch, "E728", {"start": v(5671.34, -2824.6) * mm, "end": v(5410.91, -3085.03) * mm});
            skLineSegment(sketch, "E729", {"start": v(6057.5, -2636.01) * mm, "end": v(5958.7, -2537.23) * mm});
            skLineSegment(sketch, "E730", {"start": v(5698.28, -2797.66) * mm, "end": v(5958.7, -2537.23) * mm});
            skLineSegment(sketch, "E731", {"start": v(5698.28, -2797.66) * mm, "end": v(5797.07, -2896.44) * mm});
            skLineSegment(sketch, "E732", {"start": v(6057.5, -2636.01) * mm, "end": v(5797.07, -2896.44) * mm});
            skLineSegment(sketch, "E733", {"start": v(5985.65, -2510.3) * mm, "end": v(6084.43, -2609.07) * mm});
            skLineSegment(sketch, "E734", {"start": v(6084.43, -2609.07) * mm, "end": v(6344.86, -2348.65) * mm});
            skLineSegment(sketch, "E735", {"start": v(6344.86, -2348.65) * mm, "end": v(6246.08, -2249.86) * mm});
            skLineSegment(sketch, "E736", {"start": v(6246.08, -2249.86) * mm, "end": v(5985.65, -2510.3) * mm});
            skLineSegment(sketch, "E737", {"start": v(6273.02, -2222.92) * mm, "end": v(6371.8, -2321.7) * mm});
            skLineSegment(sketch, "E738", {"start": v(6371.8, -2321.7) * mm, "end": v(6632.23, -2061.28) * mm});
            skLineSegment(sketch, "E739", {"start": v(6632.23, -2061.28) * mm, "end": v(6533.45, -1962.5) * mm});
            skLineSegment(sketch, "E740", {"start": v(6533.45, -1962.5) * mm, "end": v(6273.02, -2222.92) * mm});
            skLineSegment(sketch, "E741", {"start": v(6560.39, -1935.55) * mm, "end": v(6659.17, -2034.34) * mm});
            skLineSegment(sketch, "E742", {"start": v(6659.17, -2034.34) * mm, "end": v(6919.6, -1773.91) * mm});
            skLineSegment(sketch, "E743", {"start": v(6919.6, -1773.91) * mm, "end": v(6820.81, -1675.13) * mm});
            skLineSegment(sketch, "E744", {"start": v(6820.81, -1675.13) * mm, "end": v(6560.39, -1935.55) * mm});
            skLineSegment(sketch, "E745", {"start": v(6847.76, -1648.19) * mm, "end": v(6946.54, -1746.97) * mm});
            skLineSegment(sketch, "E746", {"start": v(6946.54, -1746.97) * mm, "end": v(6994.8, -1698.7) * mm});
            skLineSegment(sketch, "E747", {"start": v(6994.8, -1698.7) * mm, "end": v(6896.02, -1599.92) * mm});
            skLineSegment(sketch, "E748", {"start": v(6896.02, -1599.92) * mm, "end": v(6847.76, -1648.19) * mm});
            skLineSegment(sketch, "E749", {"start": v(6922.96, -1572.98) * mm, "end": v(6922.98, -1572.96) * mm});
            skLineSegment(sketch, "E750", {"start": v(6922.98, -1572.96) * mm, "end": v(7021.77, -1671.74) * mm});
            skLineSegment(sketch, "E751", {"start": v(7021.77, -1671.74) * mm, "end": v(7021.75, -1671.76) * mm});
            skLineSegment(sketch, "E752", {"start": v(7021.75, -1671.76) * mm, "end": v(6922.96, -1572.98) * mm});
            skLineSegment(sketch, "E753", {"start": v(6949.9, -1546.04) * mm, "end": v(6949.92, -1546.02) * mm});
            skLineSegment(sketch, "E754", {"start": v(6949.92, -1546.02) * mm, "end": v(7048.7, -1644.8) * mm});
            skLineSegment(sketch, "E755", {"start": v(7048.7, -1644.8) * mm, "end": v(7048.69, -1644.82) * mm});
            skLineSegment(sketch, "E756", {"start": v(7048.69, -1644.82) * mm, "end": v(6949.9, -1546.04) * mm});
            skLineSegment(sketch, "E757", {"start": v(6976.85, -1519.1) * mm, "end": v(6976.86, -1519.08) * mm});
            skLineSegment(sketch, "E758", {"start": v(7095.83, -1400.1) * mm, "end": v(7194.62, -1498.89) * mm});
            skLineSegment(sketch, "E759", {"start": v(7194.62, -1498.89) * mm, "end": v(7194.6, -1498.9) * mm});
            skLineSegment(sketch, "E760", {"start": v(7075.63, -1617.88) * mm, "end": v(6976.85, -1519.1) * mm});
            skLineSegment(sketch, "E761", {"start": v(7122.76, -1373.18) * mm, "end": v(7221.54, -1471.97) * mm});
            skLineSegment(sketch, "E762", {"start": v(7221.54, -1471.97) * mm, "end": v(7221.56, -1471.95) * mm});
            skLineSegment(sketch, "E763", {"start": v(7221.56, -1471.95) * mm, "end": v(7122.78, -1373.17) * mm});
            skLineSegment(sketch, "E764", {"start": v(7122.78, -1373.17) * mm, "end": v(7122.76, -1373.18) * mm});
            skLineSegment(sketch, "E765", {"start": v(7149.7, -1346.24) * mm, "end": v(7248.48, -1445.03) * mm});
            skLineSegment(sketch, "E766", {"start": v(7248.48, -1445.03) * mm, "end": v(7248.5, -1445) * mm});
            skLineSegment(sketch, "E767", {"start": v(7248.5, -1445) * mm, "end": v(7149.72, -1346.23) * mm});
            skLineSegment(sketch, "E768", {"start": v(7149.72, -1346.23) * mm, "end": v(7149.7, -1346.24) * mm});
            skLineSegment(sketch, "E769", {"start": v(7176.64, -1319.3) * mm, "end": v(7275.42, -1418.09) * mm});
            skLineSegment(sketch, "E770", {"start": v(7275.42, -1418.09) * mm, "end": v(7275.44, -1418.07) * mm});
            skLineSegment(sketch, "E771", {"start": v(7275.44, -1418.07) * mm, "end": v(7176.66, -1319.28) * mm});
            skLineSegment(sketch, "E772", {"start": v(7176.66, -1319.28) * mm, "end": v(7176.64, -1319.3) * mm});
            skLineSegment(sketch, "E773", {"start": v(7203.6, -1292.34) * mm, "end": v(7302.38, -1391.13) * mm});
            skLineSegment(sketch, "E774", {"start": v(7302.38, -1391.13) * mm, "end": v(7494.33, -1199.17) * mm});
            skLineSegment(sketch, "E775", {"start": v(7494.33, -1199.17) * mm, "end": v(7395.55, -1100.4) * mm});
            skLineSegment(sketch, "E776", {"start": v(7395.55, -1100.4) * mm, "end": v(7203.6, -1292.34) * mm});
            skLineSegment(sketch, "E777", {"start": v(7422.5, -1073.45) * mm, "end": v(7521.27, -1172.23) * mm});
            skLineSegment(sketch, "E778", {"start": v(7521.27, -1172.23) * mm, "end": v(7781.7, -911.8) * mm});
            skLineSegment(sketch, "E779", {"start": v(7781.7, -911.8) * mm, "end": v(7682.92, -813.02) * mm});
            skLineSegment(sketch, "E780", {"start": v(7682.92, -813.02) * mm, "end": v(7422.5, -1073.45) * mm});
            skLineSegment(sketch, "E781", {"start": v(7709.86, -786.08) * mm, "end": v(7808.64, -884.86) * mm});
            skLineSegment(sketch, "E782", {"start": v(7808.64, -884.86) * mm, "end": v(8069.07, -624.44) * mm});
            skLineSegment(sketch, "E783", {"start": v(8069.07, -624.44) * mm, "end": v(7970.29, -525.65) * mm});
            skLineSegment(sketch, "E784", {"start": v(7970.29, -525.65) * mm, "end": v(7709.86, -786.08) * mm});
            skLineSegment(sketch, "E785", {"start": v(7997.23, -498.71) * mm, "end": v(8096.01, -597.5) * mm});
            skLineSegment(sketch, "E786", {"start": v(8096.01, -597.5) * mm, "end": v(8356.44, -337.07) * mm});
            skLineSegment(sketch, "E787", {"start": v(8356.44, -337.07) * mm, "end": v(8257.66, -238.29) * mm});
            skLineSegment(sketch, "E788", {"start": v(8257.66, -238.29) * mm, "end": v(7997.23, -498.71) * mm});
            skLineSegment(sketch, "E789", {"start": v(8284.6, -211.35) * mm, "end": v(8383.38, -310.13) * mm});
            skLineSegment(sketch, "E790", {"start": v(8383.38, -310.13) * mm, "end": v(8643.8, -49.7) * mm});
            skLineSegment(sketch, "E791", {"start": v(8643.8, -49.7) * mm, "end": v(8545.02, 49.08) * mm});
            skLineSegment(sketch, "E792", {"start": v(8545.02, 49.08) * mm, "end": v(8284.6, -211.35) * mm});
            skLineSegment(sketch, "E793", {"start": v(8571.96, 76.02) * mm, "end": v(8670.75, -22.76) * mm});
            skLineSegment(sketch, "E794", {"start": v(8670.75, -22.76) * mm, "end": v(8931.17, 237.67) * mm});
            skLineSegment(sketch, "E795", {"start": v(8931.17, 237.67) * mm, "end": v(8832.4, 336.45) * mm});
            skLineSegment(sketch, "E796", {"start": v(8832.4, 336.45) * mm, "end": v(8571.96, 76.02) * mm});
            skLineSegment(sketch, "E797", {"start": v(8859.33, 363.4) * mm, "end": v(8958.12, 264.6) * mm});
            skLineSegment(sketch, "E798", {"start": v(8958.12, 264.6) * mm, "end": v(9242.12, 548.6) * mm});
            skLineSegment(sketch, "E799", {"start": v(9242.12, 548.6) * mm, "end": v(9143.33, 647.4) * mm});
            skLineSegment(sketch, "E800", {"start": v(9143.33, 647.4) * mm, "end": v(8859.33, 363.4) * mm});
            skLineSegment(sketch, "E801", {"start": v(9170.27, 674.33) * mm, "end": v(9269.06, 575.55) * mm});
            skLineSegment(sketch, "E802", {"start": v(9269.06, 575.55) * mm, "end": v(9269.07, 575.57) * mm});
            skLineSegment(sketch, "E803", {"start": v(9269.07, 575.57) * mm, "end": v(9170.3, 674.35) * mm});
            skLineSegment(sketch, "E804", {"start": v(9170.3, 674.35) * mm, "end": v(9170.27, 674.33) * mm});
            skLineSegment(sketch, "E805", {"start": v(9197.21, 701.27) * mm, "end": v(9296, 602.49) * mm});
            skLineSegment(sketch, "E806", {"start": v(9296, 602.49) * mm, "end": v(9296.02, 602.5) * mm});
            skLineSegment(sketch, "E807", {"start": v(9296.02, 602.5) * mm, "end": v(9197.23, 701.3) * mm});
            skLineSegment(sketch, "E808", {"start": v(9197.23, 701.3) * mm, "end": v(9197.21, 701.27) * mm});
            skLineSegment(sketch, "E809", {"start": v(9224.16, 728.21) * mm, "end": v(9322.94, 629.43) * mm});
            skLineSegment(sketch, "E810", {"start": v(9322.94, 629.43) * mm, "end": v(9505.91, 812.4) * mm});
            skLineSegment(sketch, "E811", {"start": v(9505.91, 812.4) * mm, "end": v(9407.13, 911.19) * mm});
            skLineSegment(sketch, "E812", {"start": v(9407.13, 911.19) * mm, "end": v(9224.16, 728.21) * mm});
            skLineSegment(sketch, "E813", {"start": v(9434.07, 938.13) * mm, "end": v(9532.85, 839.34) * mm});
            skLineSegment(sketch, "E814", {"start": v(9532.85, 839.34) * mm, "end": v(9793.28, 1099.77) * mm});
            skLineSegment(sketch, "E815", {"start": v(9793.28, 1099.77) * mm, "end": v(9694.5, 1198.55) * mm});
            skLineSegment(sketch, "E816", {"start": v(9694.5, 1198.55) * mm, "end": v(9434.07, 938.13) * mm});
            skLineSegment(sketch, "E817", {"start": v(9721.44, 1225.5) * mm, "end": v(9820.22, 1126.71) * mm});
            skLineSegment(sketch, "E818", {"start": v(9820.22, 1126.71) * mm, "end": v(9923.5, 1229.99) * mm});
            skLineSegment(sketch, "E819", {"start": v(9923.5, 1229.99) * mm, "end": v(9824.7, 1328.77) * mm});
            skLineSegment(sketch, "E820", {"start": v(9824.7, 1328.77) * mm, "end": v(9824.7, 1328.75) * mm});
            skLineSegment(sketch, "E821", {"start": v(9824.7, 1328.75) * mm, "end": v(9851.63, 1301.8) * mm});
            skLineSegment(sketch, "E822", {"start": v(9851.63, 1301.8) * mm, "end": v(9752.87, 1203.04) * mm});
            skLineSegment(sketch, "E823", {"start": v(9752.87, 1203.04) * mm, "end": v(9725.93, 1229.99) * mm});
            skLineSegment(sketch, "E824", {"start": v(9725.93, 1229.99) * mm, "end": v(9721.44, 1225.5) * mm});
            skLineSegment(sketch, "E825", {"start": v(7102.57, -1590.94) * mm, "end": v(7003.79, -1492.15) * mm});
            skLineSegment(sketch, "E826", {"start": v(7102.59, -1590.92) * mm, "end": v(7003.8, -1492.14) * mm});
            skLineSegment(sketch, "E827", {"start": v(7129.51, -1564) * mm, "end": v(7030.73, -1465.21) * mm});
            skLineSegment(sketch, "E828", {"start": v(7135.12, -1558.38) * mm, "end": v(7036.34, -1459.6) * mm});
            skLineSegment(sketch, "E829", {"start": v(7162.06, -1531.44) * mm, "end": v(7063.28, -1432.66) * mm});
            skLineSegment(sketch, "E830", {"start": v(7167.68, -1525.83) * mm, "end": v(7068.9, -1427.05) * mm});
            skLineSegment(sketch, "E831", {"start": v(7075.65, -1617.86) * mm, "end": v(6976.86, -1519.08) * mm});
            skLineSegment(sketch, "E832.trimOffspring", {"start": v(7075.65, -1617.86) * mm, "end": v(7075.63, -1617.88) * mm});
            skLineSegment(sketch, "E833.trimOffspring", {"start": v(7102.59, -1590.92) * mm, "end": v(7102.57, -1590.94) * mm});
            skLineSegment(sketch, "E834.trimOffspring", {"start": v(7135.12, -1558.38) * mm, "end": v(7129.51, -1564) * mm});
            skLineSegment(sketch, "E835.trimOffspring", {"start": v(7003.79, -1492.15) * mm, "end": v(7003.8, -1492.14) * mm});
            skLineSegment(sketch, "E836.trimOffspring", {"start": v(7030.73, -1465.21) * mm, "end": v(7036.34, -1459.6) * mm});
            skLineSegment(sketch, "E837.trimOffspring", {"start": v(7063.28, -1432.66) * mm, "end": v(7068.9, -1427.05) * mm});
            skLineSegment(sketch, "E838", {"start": v(7194.6, -1498.9) * mm, "end": v(7095.82, -1400.13) * mm});
            skLineSegment(sketch, "E839.trimOffspring", {"start": v(7095.82, -1400.13) * mm, "end": v(7095.83, -1400.1) * mm});
            skLineSegment(sketch, "E840.trimOffspring", {"start": v(7167.68, -1525.83) * mm, "end": v(7162.06, -1531.44) * mm});
            skSolve(sketch);
        }
        {
            var Q0;
            Q0 = qSketchRegion(id + "F72", true);
            var Q1;
            Q1=makeQuery(id+"F59.boolean.opBoolean","COPY",FACE,{"derivedFrom":makeQuery(id+"F59.opExtrude","CAP_FACE",FACE,{"disambiguationData":[OSD([sQuery(id+"F58.wireOp",EDGE,"E571"),sQuery(id+"F58.wireOp",EDGE,"E572"),sQuery(id+"F58.wireOp",EDGE,"E573"),sQuery(id+"F58.wireOp",EDGE,"E574")])],"isStart":false})});
            extrude(context, id + "F73", {"entities" : qUnion([Q0]), "operationType" : NewBodyOperationType.REMOVE, "endBound" : BoundingType.UP_TO_SURFACE, "oppositeDirection" : true, "endBoundEntityFace" : qUnion([Q1]), "depth" : 457.2 * mm});
        }
        {
            var Q0;
            Q0=makeQuery(id+"F71.opExtrude","CAP_FACE",FACE,{"disambiguationData":[OSD([sQuery(id+"F70.wireOp",EDGE,"E600"),sQuery(id+"F70.wireOp",EDGE,"E601"),sQuery(id+"F70.wireOp",EDGE,"E602"),sQuery(id+"F70.wireOp",EDGE,"E603")])],"isStart":false});
            var sketch = newSketch(context, id + "F74", { "sketchPlane" : qUnion([Q0]) });
            skLineSegment(sketch, "E841", {"start": v(4247.97, -4247.97) * mm, "end": v(4346.75, -4346.75) * mm});
            skLineSegment(sketch, "E842", {"start": v(4346.75, -4346.75) * mm, "end": v(9950.43, 1256.93) * mm});
            skLineSegment(sketch, "E843", {"start": v(9950.43, 1256.93) * mm, "end": v(9851.65, 1355.7) * mm});
            skLineSegment(sketch, "E844", {"start": v(9851.65, 1355.7) * mm, "end": v(4247.97, -4247.97) * mm});
            skSolve(sketch);
        }
        {
            var Q0;
            Q0 = qSketchRegion(id + "F74", true);
            extrude(context, id + "F75", {"entities" : qUnion([Q0]), "operationType" : NewBodyOperationType.ADD, "depth" : 76.2 * mm});
        }
        {
            var Q0;
            {var subQ0=sQuery(id+"F0.wireOp",EDGE,"E11");Q0=makeQuery(id+"F75.boolean.opBoolean","MERGE",FACE,{"derivedFrom":[makeQuery(id+"F71.boolean.opBoolean","MERGE",FACE,{"derivedFrom":[makeQuery(id+"F69.boolean.opBoolean","MERGE",FACE,{"derivedFrom":[makeQuery(id+"F1.opExtrude","SWEPT_FACE",FACE,{"disambiguationData":[OSD([subQ0])]}),makeQuery(id+"F69.opExtrude","SWEPT_FACE",FACE,{"disambiguationData":[OSD([subQ0])]})]}),makeQuery(id+"F71.opExtrude","SWEPT_FACE",FACE,{"disambiguationData":[OSD([sQuery(id+"F70.wireOp",EDGE,"E603")])]}),makeQuery(id+"F71.opExtrude","SWEPT_FACE",FACE,{"disambiguationData":[OSD([sQuery(id+"F70.wireOp",EDGE,"E611")])]}),makeQuery(id+"F71.opExtrude","SWEPT_FACE",FACE,{"disambiguationData":[OSD([sQuery(id+"F70.wireOp",EDGE,"E618")])]}),makeQuery(id+"F71.opExtrude","SWEPT_FACE",FACE,{"disambiguationData":[OSD([sQuery(id+"F70.wireOp",EDGE,"E622")])]}),makeQuery(id+"F71.opExtrude","SWEPT_FACE",FACE,{"disambiguationData":[OSD([sQuery(id+"F70.wireOp",EDGE,"E626")])]}),makeQuery(id+"F71.opExtrude","SWEPT_FACE",FACE,{"disambiguationData":[OSD([sQuery(id+"F70.wireOp",EDGE,"E630")])]}),makeQuery(id+"F71.opExtrude","SWEPT_FACE",FACE,{"disambiguationData":[OSD([sQuery(id+"F70.wireOp",EDGE,"E634")])]}),makeQuery(id+"F71.opExtrude","SWEPT_FACE",FACE,{"disambiguationData":[OSD([sQuery(id+"F70.wireOp",EDGE,"E637.1.0.2")])]}),makeQuery(id+"F71.opExtrude","SWEPT_FACE",FACE,{"disambiguationData":[OSD([sQuery(id+"F70.wireOp",EDGE,"E637.2.0.2")])]}),makeQuery(id+"F71.opExtrude","SWEPT_FACE",FACE,{"disambiguationData":[OSD([sQuery(id+"F70.wireOp",EDGE,"E637.3.0.2")])]}),makeQuery(id+"F71.opExtrude","SWEPT_FACE",FACE,{"disambiguationData":[OSD([sQuery(id+"F70.wireOp",EDGE,"E637.4.0.2")])]}),makeQuery(id+"F71.opExtrude","SWEPT_FACE",FACE,{"disambiguationData":[OSD([sQuery(id+"F70.wireOp",EDGE,"E637.5.0.2")])]}),makeQuery(id+"F71.opExtrude","SWEPT_FACE",FACE,{"disambiguationData":[OSD([sQuery(id+"F70.wireOp",EDGE,"E637.6.0.2")])]}),makeQuery(id+"F71.opExtrude","SWEPT_FACE",FACE,{"disambiguationData":[OSD([sQuery(id+"F70.wireOp",EDGE,"E637.7.0.2")])]}),makeQuery(id+"F71.opExtrude","SWEPT_FACE",FACE,{"disambiguationData":[OSD([sQuery(id+"F70.wireOp",EDGE,"E637.8.0.2")])]}),makeQuery(id+"F71.opExtrude","SWEPT_FACE",FACE,{"disambiguationData":[OSD([sQuery(id+"F70.wireOp",EDGE,"E637.10.0.2")])]}),makeQuery(id+"F71.opExtrude","SWEPT_FACE",FACE,{"disambiguationData":[OSD([sQuery(id+"F70.wireOp",EDGE,"E637.11.0.2")])]}),makeQuery(id+"F71.opExtrude","SWEPT_FACE",FACE,{"disambiguationData":[OSD([sQuery(id+"F70.wireOp",EDGE,"E637.12.0.2")])]}),makeQuery(id+"F71.opExtrude","SWEPT_FACE",FACE,{"disambiguationData":[OSD([sQuery(id+"F70.wireOp",EDGE,"E637.13.0.2")])]}),makeQuery(id+"F71.opExtrude","SWEPT_FACE",FACE,{"disambiguationData":[OSD([sQuery(id+"F70.wireOp",EDGE,"E637.14.0.2")])]}),makeQuery(id+"F71.opExtrude","SWEPT_FACE",FACE,{"disambiguationData":[OSD([sQuery(id+"F70.wireOp",EDGE,"E637.15.0.2")])]}),makeQuery(id+"F71.opExtrude","SWEPT_FACE",FACE,{"disambiguationData":[OSD([sQuery(id+"F70.wireOp",EDGE,"E637.16.0.2")])]}),makeQuery(id+"F71.opExtrude","SWEPT_FACE",FACE,{"disambiguationData":[OSD([sQuery(id+"F70.wireOp",EDGE,"E637.17.0.2")])]}),makeQuery(id+"F71.opExtrude","SWEPT_FACE",FACE,{"disambiguationData":[OSD([sQuery(id+"F70.wireOp",EDGE,"E637.18.0.2")])]}),makeQuery(id+"F71.opExtrude","SWEPT_FACE",FACE,{"disambiguationData":[OSD([sQuery(id+"F70.wireOp",EDGE,"E639")])]}),makeQuery(id+"F71.opExtrude","SWEPT_FACE",FACE,{"disambiguationData":[OSD([sQuery(id+"F70.wireOp",EDGE,"E643")])]}),makeQuery(id+"F71.opExtrude","SWEPT_FACE",FACE,{"disambiguationData":[OSD([sQuery(id+"F70.wireOp",EDGE,"E647")])]}),makeQuery(id+"F71.opExtrude","SWEPT_FACE",FACE,{"disambiguationData":[OSD([sQuery(id+"F70.wireOp",EDGE,"E651")])]}),makeQuery(id+"F71.opExtrude","SWEPT_FACE",FACE,{"disambiguationData":[OSD([sQuery(id+"F70.wireOp",EDGE,"E655")])]}),makeQuery(id+"F71.opExtrude","SWEPT_FACE",FACE,{"disambiguationData":[OSD([sQuery(id+"F70.wireOp",EDGE,"E659")])]}),makeQuery(id+"F71.opExtrude","SWEPT_FACE",FACE,{"disambiguationData":[OSD([sQuery(id+"F70.wireOp",EDGE,"E663")])]}),makeQuery(id+"F71.opExtrude","SWEPT_FACE",FACE,{"disambiguationData":[OSD([sQuery(id+"F70.wireOp",EDGE,"E667")])]}),makeQuery(id+"F71.opExtrude","SWEPT_FACE",FACE,{"disambiguationData":[OSD([sQuery(id+"F70.wireOp",EDGE,"E671")])]})]}),makeQuery(id+"F75.opExtrude","SWEPT_FACE",FACE,{"disambiguationData":[OSD([sQuery(id+"F74.wireOp",EDGE,"E842")])]})]});}
            var sketch = newSketch(context, id + "F76", { "sketchPlane" : qUnion([Q0]) });
            skLineSegment(sketch, "E845", {"start": v(925.51, 2390.78) * mm, "end": v(925.51, 1558.92) * mm});
            skLineSegment(sketch, "E846", {"start": v(925.51, 1558.92) * mm, "end": v(1001.71, 1558.92) * mm});
            skLineSegment(sketch, "E847", {"start": v(1001.71, 1558.92) * mm, "end": v(1001.71, -727.08) * mm});
            skLineSegment(sketch, "E848", {"start": v(1001.71, -727.08) * mm, "end": v(3744.91, -727.08) * mm});
            skLineSegment(sketch, "E849", {"start": v(3744.91, -727.08) * mm, "end": v(3744.91, 1558.92) * mm});
            skLineSegment(sketch, "E850", {"start": v(3744.91, 1558.92) * mm, "end": v(3821.11, 1558.92) * mm});
            skLineSegment(sketch, "E851", {"start": v(3821.11, 1558.92) * mm, "end": v(3821.11, 2390.78) * mm});
            skLineSegment(sketch, "E852", {"start": v(3821.11, 2390.78) * mm, "end": v(3744.91, 2390.78) * mm});
            skLineSegment(sketch, "E853", {"start": v(3744.91, 2390.78) * mm, "end": v(3744.91, 1787.52) * mm});
            skLineSegment(sketch, "E854", {"start": v(3744.91, 1787.52) * mm, "end": v(1001.71, 1787.52) * mm});
            skLineSegment(sketch, "E855", {"start": v(1001.71, 1787.52) * mm, "end": v(1001.71, 2390.78) * mm});
            skLineSegment(sketch, "E856", {"start": v(1001.71, 2390.78) * mm, "end": v(925.51, 2390.78) * mm});
            skLineSegment(sketch, "E857", {"start": v(4103.69, 2390.78) * mm, "end": v(4103.69, 1558.92) * mm});
            skLineSegment(sketch, "E858", {"start": v(4103.69, 1558.92) * mm, "end": v(4179.89, 1558.92) * mm});
            skLineSegment(sketch, "E859", {"start": v(4179.89, 1558.92) * mm, "end": v(4179.89, -727.08) * mm});
            skLineSegment(sketch, "E860", {"start": v(4179.89, -727.08) * mm, "end": v(6923.09, -727.08) * mm});
            skLineSegment(sketch, "E861", {"start": v(6923.09, -727.08) * mm, "end": v(6923.09, 1558.92) * mm});
            skLineSegment(sketch, "E862", {"start": v(6923.09, 1558.92) * mm, "end": v(6999.29, 1558.92) * mm});
            skLineSegment(sketch, "E863", {"start": v(6999.29, 1558.92) * mm, "end": v(6999.29, 2390.78) * mm});
            skPoint(sketch, "E863.endSnap0", {"position": v(6722.27, 2390.78) * mm});
            skLineSegment(sketch, "E864", {"start": v(6999.29, 2390.78) * mm, "end": v(6923.09, 2390.78) * mm});
            skLineSegment(sketch, "E865", {"start": v(6923.09, 2390.78) * mm, "end": v(6923.09, 1787.52) * mm});
            skLineSegment(sketch, "E866", {"start": v(6923.09, 1787.52) * mm, "end": v(4179.89, 1787.52) * mm});
            skLineSegment(sketch, "E867", {"start": v(4179.89, 1787.52) * mm, "end": v(4179.89, 2390.78) * mm});
            skLineSegment(sketch, "E868", {"start": v(4179.89, 2390.78) * mm, "end": v(4103.69, 2390.78) * mm});
            skLineSegment(sketch, "E869.bottom", {"start": v(3897.31, 2466.98) * mm, "end": v(4027.49, 2466.98) * mm});
            skLineSegment(sketch, "E869.top", {"start": v(3897.31, 2273.3) * mm, "end": v(4027.49, 2273.3) * mm});
            skLineSegment(sketch, "E869.left", {"start": v(3897.31, 2466.98) * mm, "end": v(3897.31, 2273.3) * mm});
            skLineSegment(sketch, "E869.right", {"start": v(4027.49, 2466.98) * mm, "end": v(4027.49, 2273.3) * mm});
            skSolve(sketch);
        }
        {
            var Q0;
            Q0 = qSketchRegion(id + "F76", true);
            extrude(context, id + "F77", {"entities" : qUnion([Q0]), "operationType" : NewBodyOperationType.REMOVE, "oppositeDirection" : true, "depth" : 139.7 * mm});
        }
        {
            var Q0;
            {var subQ9=sQuery(id+"F74.wireOp",EDGE,"E842");var subQ84=sQuery(id+"F74.wireOp",EDGE,"E844");var subQ86=makeQuery(id+"F75.opExtrude","CAP_FACE",FACE,{"disambiguationData":[OSD([sQuery(id+"F74.wireOp",EDGE,"E841"),subQ9,sQuery(id+"F74.wireOp",EDGE,"E843"),subQ84])],"isStart":true});Q0=makeQuery(id+"F77.boolean.opBoolean","MERGE",FACE,{"derivedFrom":[makeQuery(id+"F75.boolean.opBoolean","SPLIT",FACE,{"disambiguationData":[TD([makeQuery(id+"F71.opExtrude","SWEPT_FACE",FACE,{"disambiguationData":[OSD([sQuery(id+"F70.wireOp",EDGE,"E625")])]})])],"derivedFrom":subQ86}),makeQuery(id+"F75.boolean.opBoolean","SPLIT",FACE,{"disambiguationData":[TD([makeQuery(id+"F71.opExtrude","SWEPT_FACE",FACE,{"disambiguationData":[OSD([sQuery(id+"F70.wireOp",EDGE,"E627")])]})])],"derivedFrom":subQ86}),makeQuery(id+"F75.boolean.opBoolean","SPLIT",FACE,{"disambiguationData":[TD([makeQuery(id+"F71.opExtrude","SWEPT_FACE",FACE,{"disambiguationData":[OSD([sQuery(id+"F70.wireOp",EDGE,"E668")])]})])],"derivedFrom":subQ86}),makeQuery(id+"F77.opExtrude","SWEPT_FACE",FACE,{"disambiguationData":[OSD([sQuery(id+"F76.wireOp",EDGE,"E864")])]})]});}
            var sketch = newSketch(context, id + "F78", { "sketchPlane" : qUnion([Q0]) });
            skLineSegment(sketch, "E870", {"start": v(9218.54, -525.04) * mm, "end": v(9119.76, -623.82) * mm});
            skLineSegment(sketch, "E871", {"start": v(9119.76, -623.82) * mm, "end": v(9146.7, -650.76) * mm});
            skLineSegment(sketch, "E872", {"start": v(9146.7, -650.76) * mm, "end": v(9245.48, -551.98) * mm});
            skLineSegment(sketch, "E873", {"start": v(9245.48, -551.98) * mm, "end": v(9218.54, -525.04) * mm});
            skSolve(sketch);
        }
        {
            var Q0;
            Q0 = qSketchRegion(id + "F78", true);
            var Q1;
            Q1=makeQuery(id+"F77.boolean.opBoolean","COPY",FACE,{"disambiguationData":[TD([makeQuery(id+"F71.opExtrude","SWEPT_FACE",FACE,{"disambiguationData":[OSD([sQuery(id+"F70.wireOp",EDGE,"E637.15.0.0")])]})])],"derivedFrom":makeQuery(id+"F77.opExtrude","SWEPT_FACE",FACE,{"disambiguationData":[OSD([sQuery(id+"F76.wireOp",EDGE,"E866")])]})});
            extrude(context, id + "F79", {"entities" : qUnion([Q0]), "operationType" : NewBodyOperationType.ADD, "endBound" : BoundingType.UP_TO_SURFACE, "endBoundEntityFace" : qUnion([Q1]), "depth" : 25.4 * mm});
        }
        {
            var Q0;
            Q0=makeQuery(id+"F73.boolean.opBoolean","MERGE",FACE,{"derivedFrom":[makeQuery(id+"F71.opExtrude","SWEPT_FACE",FACE,{"disambiguationData":[OSD([sQuery(id+"F70.wireOp",EDGE,"E650")])]}),makeQuery(id+"F73.opExtrude","SWEPT_FACE",FACE,{"disambiguationData":[OSD([sQuery(id+"F72.wireOp",EDGE,"E754")])]})]});
            var sketch = newSketch(context, id + "F80", { "sketchPlane" : qUnion([Q0]) });
            skLineSegment(sketch, "E874.bottom", {"start": v(6007.54, 1558.95) * mm, "end": v(6147.24, 1558.95) * mm});
            skLineSegment(sketch, "E874.top", {"start": v(6007.54, 1787.5) * mm, "end": v(6147.24, 1787.5) * mm});
            skLineSegment(sketch, "E874.left", {"start": v(6007.54, 1558.95) * mm, "end": v(6007.54, 1787.5) * mm});
            skLineSegment(sketch, "E874.right", {"start": v(6147.24, 1558.95) * mm, "end": v(6147.24, 1787.5) * mm});
            skSolve(sketch);
        }
        {
            var Q0;
            Q0 = qSketchRegion(id + "F80", true);
            var Q1;
            Q1=makeQuery(id+"F73.boolean.opBoolean","MERGE",FACE,{"derivedFrom":[makeQuery(id+"F71.opExtrude","SWEPT_FACE",FACE,{"disambiguationData":[OSD([sQuery(id+"F70.wireOp",EDGE,"E642")])]}),makeQuery(id+"F73.opExtrude","SWEPT_FACE",FACE,{"disambiguationData":[OSD([sQuery(id+"F72.wireOp",EDGE,"E712")])]})]});
            extrude(context, id + "F81", {"entities" : qUnion([Q0]), "operationType" : NewBodyOperationType.ADD, "endBound" : BoundingType.UP_TO_SURFACE, "endBoundEntityFace" : qUnion([Q1]), "depth" : 25.4 * mm});
        }
        {
            var Q0;
            Q0=makeQuery(id+"F73.boolean.opBoolean","MERGE",FACE,{"derivedFrom":[makeQuery(id+"F71.opExtrude","SWEPT_FACE",FACE,{"disambiguationData":[OSD([sQuery(id+"F70.wireOp",EDGE,"E658")])]}),makeQuery(id+"F73.opExtrude","SWEPT_FACE",FACE,{"disambiguationData":[OSD([sQuery(id+"F72.wireOp",EDGE,"E765")])]})]});
            var sketch = newSketch(context, id + "F82", { "sketchPlane" : qUnion([Q0]) });
            skLineSegment(sketch, "E875.bottom", {"start": v(-6147.24, 1787.5) * mm, "end": v(-6007.54, 1787.5) * mm});
            skLineSegment(sketch, "E875.top", {"start": v(-6147.24, 1558.95) * mm, "end": v(-6007.54, 1558.95) * mm});
            skLineSegment(sketch, "E875.left", {"start": v(-6147.24, 1787.5) * mm, "end": v(-6147.24, 1558.95) * mm});
            skLineSegment(sketch, "E875.right", {"start": v(-6007.54, 1787.5) * mm, "end": v(-6007.54, 1558.95) * mm});
            skSolve(sketch);
        }
        {
            var Q0;
            Q0 = qSketchRegion(id + "F82", true);
            var Q1;
            Q1=makeQuery(id+"F73.boolean.opBoolean","MERGE",FACE,{"derivedFrom":[makeQuery(id+"F71.opExtrude","SWEPT_FACE",FACE,{"disambiguationData":[OSD([sQuery(id+"F70.wireOp",EDGE,"E670")])]}),makeQuery(id+"F73.opExtrude","SWEPT_FACE",FACE,{"disambiguationData":[OSD([sQuery(id+"F72.wireOp",EDGE,"E807")])]})]});
            extrude(context, id + "F83", {"entities" : qUnion([Q0]), "operationType" : NewBodyOperationType.ADD, "endBound" : BoundingType.UP_TO_SURFACE, "endBoundEntityFace" : qUnion([Q1]), "depth" : 25.4 * mm});
        }
        {
            var Q0;
            Q0=makeQuery(id+"F1.opExtrude","CAP_FACE",FACE,{"disambiguationData":[OSD([sQuery(id+"F0.wireOp",EDGE,"E13.0"),sQuery(id+"F0.wireOp",EDGE,"E13.1"),sQuery(id+"F0.wireOp",EDGE,"E31"),sQuery(id+"F0.wireOp",EDGE,"E32.trimOffspring"),sQuery(id+"F0.wireOp",EDGE,"E33")])],"isStart":false});
            var sketch = newSketch(context, id + "F84", { "sketchPlane" : qUnion([Q0]) });
            skLineSegment(sketch, "E876.bottom", {"start": v(-13810.5, 6705.6) * mm, "end": v(-13772.4, 6705.6) * mm});
            skLineSegment(sketch, "E876.top", {"start": v(-13810.5, 6565.9) * mm, "end": v(-13772.4, 6565.9) * mm});
            skLineSegment(sketch, "E876.left", {"start": v(-13810.5, 6705.6) * mm, "end": v(-13810.5, 6565.9) * mm});
            skLineSegment(sketch, "E876.right", {"start": v(-13772.4, 6705.6) * mm, "end": v(-13772.4, 6565.9) * mm});
            skLineSegment(sketch, "E877.bottom", {"start": v(-11137.9, 6565.9) * mm, "end": v(-11176, 6565.9) * mm});
            skLineSegment(sketch, "E877.top", {"start": v(-11137.9, 6705.6) * mm, "end": v(-11176, 6705.6) * mm});
            skLineSegment(sketch, "E877.left", {"start": v(-11137.9, 6565.9) * mm, "end": v(-11137.9, 6705.6) * mm});
            skLineSegment(sketch, "E877.right", {"start": v(-11176, 6565.9) * mm, "end": v(-11176, 6705.6) * mm});
            skLineSegment(sketch, "E878.bottom", {"start": v(-11176.03, 6705.6) * mm, "end": v(-11315.7, 6705.6) * mm});
            skLineSegment(sketch, "E878.top", {"start": v(-11176.03, 6667.5) * mm, "end": v(-11315.7, 6667.5) * mm});
            skLineSegment(sketch, "E878.left", {"start": v(-11176.03, 6705.6) * mm, "end": v(-11176.03, 6667.5) * mm});
            skLineSegment(sketch, "E878.right", {"start": v(-11315.7, 6705.6) * mm, "end": v(-11315.7, 6667.5) * mm});
            skLineSegment(sketch, "E879", {"start": v(-13868.4, 6705.6) * mm, "end": v(-13873.66, 6705.6) * mm, "construction": true});
            skLineSegment(sketch, "E880", {"start": v(-13873.66, 6705.6) * mm, "end": v(-13873.66, 6718.3) * mm, "construction": true});
            skLineSegment(sketch, "E881", {"start": v(-13873.66, 6718.3) * mm, "end": v(-13686.02, 6718.3) * mm, "construction": true});
            skLineSegment(sketch, "E882", {"start": v(-13871.03, 6702.97) * mm, "end": v(-13880.01, 6711.95) * mm, "construction": true});
            skLineSegment(sketch, "E883", {"start": v(-13880.01, 6711.95) * mm, "end": v(-14007.29, 6584.68) * mm, "construction": true});
            skLineSegment(sketch, "E884.bottom", {"start": v(-13486.31, 6705.6) * mm, "end": v(-13448.21, 6705.6) * mm});
            skLineSegment(sketch, "E884.top", {"start": v(-13486.31, 6565.9) * mm, "end": v(-13448.21, 6565.9) * mm});
            skLineSegment(sketch, "E884.left", {"start": v(-13486.31, 6705.6) * mm, "end": v(-13486.31, 6565.9) * mm});
            skLineSegment(sketch, "E884.right", {"start": v(-13448.21, 6705.6) * mm, "end": v(-13448.21, 6565.9) * mm});
            skLineSegment(sketch, "E885.1.0.0", {"start": v(-13079.91, 6565.9) * mm, "end": v(-13041.81, 6565.9) * mm});
            skLineSegment(sketch, "E885.1.0.1", {"start": v(-13079.91, 6705.6) * mm, "end": v(-13079.91, 6565.9) * mm});
            skLineSegment(sketch, "E885.1.0.2", {"start": v(-13041.81, 6705.6) * mm, "end": v(-13041.81, 6565.9) * mm});
            skLineSegment(sketch, "E885.1.0.3", {"start": v(-13079.91, 6705.6) * mm, "end": v(-13041.81, 6705.6) * mm});
            skLineSegment(sketch, "E885.2.0.0", {"start": v(-12673.51, 6565.9) * mm, "end": v(-12635.41, 6565.9) * mm});
            skLineSegment(sketch, "E885.2.0.1", {"start": v(-12673.51, 6705.6) * mm, "end": v(-12673.51, 6565.9) * mm});
            skLineSegment(sketch, "E885.2.0.2", {"start": v(-12635.41, 6705.6) * mm, "end": v(-12635.41, 6565.9) * mm});
            skLineSegment(sketch, "E885.2.0.3", {"start": v(-12673.51, 6705.6) * mm, "end": v(-12635.41, 6705.6) * mm});
            skLineSegment(sketch, "E885.3.0.0", {"start": v(-12267.11, 6565.9) * mm, "end": v(-12229.01, 6565.9) * mm});
            skLineSegment(sketch, "E885.3.0.1", {"start": v(-12267.11, 6705.6) * mm, "end": v(-12267.11, 6565.9) * mm});
            skLineSegment(sketch, "E885.3.0.2", {"start": v(-12229.01, 6705.6) * mm, "end": v(-12229.01, 6565.9) * mm});
            skLineSegment(sketch, "E885.3.0.3", {"start": v(-12267.11, 6705.6) * mm, "end": v(-12229.01, 6705.6) * mm});
            skLineSegment(sketch, "E885.4.0.0", {"start": v(-11860.71, 6565.9) * mm, "end": v(-11822.61, 6565.9) * mm});
            skLineSegment(sketch, "E885.4.0.1", {"start": v(-11860.71, 6705.6) * mm, "end": v(-11860.71, 6565.9) * mm});
            skLineSegment(sketch, "E885.4.0.2", {"start": v(-11822.61, 6705.6) * mm, "end": v(-11822.61, 6565.9) * mm});
            skLineSegment(sketch, "E885.4.0.3", {"start": v(-11860.71, 6705.6) * mm, "end": v(-11822.61, 6705.6) * mm});
            skLineSegment(sketch, "E885.5.0.0", {"start": v(-11454.31, 6565.9) * mm, "end": v(-11416.21, 6565.9) * mm});
            skLineSegment(sketch, "E885.5.0.1", {"start": v(-11454.31, 6705.6) * mm, "end": v(-11454.31, 6565.9) * mm});
            skLineSegment(sketch, "E885.5.0.2", {"start": v(-11416.21, 6705.6) * mm, "end": v(-11416.21, 6565.9) * mm});
            skLineSegment(sketch, "E885.5.0.3", {"start": v(-11454.31, 6705.6) * mm, "end": v(-11416.21, 6705.6) * mm});
            skLineSegment(sketch, "E885.direction1", {"start": v(-13486.31, 6565.9) * mm, "end": v(-13079.91, 6565.9) * mm, "construction": true});
            skLineSegment(sketch, "E886.bottom", {"start": v(-12827, 6565.9) * mm, "end": v(-12687.3, 6565.9) * mm});
            skLineSegment(sketch, "E886.top", {"start": v(-12827, 6604) * mm, "end": v(-12687.3, 6604) * mm});
            skLineSegment(sketch, "E886.left", {"start": v(-12827, 6565.9) * mm, "end": v(-12827, 6604) * mm});
            skLineSegment(sketch, "E886.right", {"start": v(-12687.3, 6565.9) * mm, "end": v(-12687.3, 6604) * mm});
            skLineSegment(sketch, "E887", {"start": v(-12712.7, 6604) * mm, "end": v(-12712.7, 6565.9) * mm, "construction": true});
            skLineSegment(sketch, "E888", {"start": v(-12801.6, 6604) * mm, "end": v(-12801.6, 6565.9) * mm, "construction": true});
            skSolve(sketch);
        }
        {
            var Q0;
            Q0 = qSketchRegion(id + "F84", true);
            extrude(context, id + "F85", {"entities" : qUnion([Q0]), "operationType" : NewBodyOperationType.ADD, "depth" : 2352.67 * mm});
        }
        {
            var Q0;
            Q0=makeQuery(id+"F85.opExtrude","CAP_FACE",FACE,{"disambiguationData":[OSD([sQuery(id+"F84.wireOp",EDGE,"E876.bottom"),sQuery(id+"F84.wireOp",EDGE,"E876.top"),sQuery(id+"F84.wireOp",EDGE,"E876.left"),sQuery(id+"F84.wireOp",EDGE,"E876.right")])],"isStart":false});
            var sketch = newSketch(context, id + "F86", { "sketchPlane" : qUnion([Q0]) });
            skLineSegment(sketch, "E889.bottom", {"start": v(-13810.5, 6705.6) * mm, "end": v(-11137.9, 6705.6) * mm});
            skLineSegment(sketch, "E889.top", {"start": v(-13810.5, 6565.9) * mm, "end": v(-11137.9, 6565.9) * mm});
            skLineSegment(sketch, "E889.left", {"start": v(-13810.5, 6705.6) * mm, "end": v(-13810.5, 6565.9) * mm});
            skLineSegment(sketch, "E889.right", {"start": v(-11137.9, 6705.6) * mm, "end": v(-11137.9, 6565.9) * mm});
            skSolve(sketch);
        }
        {
            var Q0;
            Q0 = qSketchRegion(id + "F86", true);
            extrude(context, id + "F87", {"entities" : qUnion([Q0]), "operationType" : NewBodyOperationType.ADD, "depth" : 76.2 * mm});
        }
        {
            var Q0;
            Q0=makeQuery(id+"F1.opExtrude","CAP_FACE",FACE,{"disambiguationData":[OSD([sQuery(id+"F0.wireOp",EDGE,"E13.4"),sQuery(id+"F0.wireOp",EDGE,"E62"),sQuery(id+"F0.wireOp",EDGE,"E64.trimOffspring"),sQuery(id+"F0.wireOp",EDGE,"E66.trimOffspring")])],"isStart":true});
            var sketch = newSketch(context, id + "F88", { "sketchPlane" : qUnion([Q0]) });
            skSolve(sketch);
        }
        {
            var Q0;
            Q0=makeQuery(id+"F88.imprint","IMPRINT",FACE,{"disambiguationData":[TD([[makeQuery(id+"F88.imprint","IMPRINT",EDGE,{"derivedFrom":makeQuery(id+"F1.opExtrude","CAP_EDGE",EDGE,{"disambiguationData":[OSD([sQuery(id+"F0.wireOp",EDGE,"E13.4")])],"isStart":true})}),-1.0]])]});
            var Q1;
            {var subQ1=sQuery(id+"F0.wireOp",EDGE,"E46.trimOffspring");var subQ4=sQuery(id+"F0.wireOp",EDGE,"E65");var subQ5=sQuery(id+"F0.wireOp",EDGE,"E45");var subQ6=sQuery(id+"F0.wireOp",EDGE,"E10");var subQ25=makeQuery(id+"F1.opExtrude","SWEPT_FACE",FACE,{"disambiguationData":[OSD([subQ5])]});Q1=makeQuery(id+"F65.boolean.opBoolean","SPLIT",FACE,{"disambiguationData":[TD([subQ25])],"derivedFrom":makeQuery(id+"F57.opExtrude","CAP_FACE",FACE,{"disambiguationData":[OSD([subQ6,subQ5,subQ1,subQ4])],"isStart":false})});}
            extrude(context, id + "F89", {"entities" : qUnion([Q0]), "operationType" : NewBodyOperationType.ADD, "endBound" : BoundingType.UP_TO_SURFACE, "endBoundEntityFace" : qUnion([Q1]), "depth" : 457.2 * mm});
        }
        {
            var Q0;
            Q0=makeQuery(id+"F1.opExtrude","CAP_FACE",FACE,{"disambiguationData":[OSD([sQuery(id+"F0.wireOp",EDGE,"E13.4"),sQuery(id+"F0.wireOp",EDGE,"E62"),sQuery(id+"F0.wireOp",EDGE,"E64.trimOffspring"),sQuery(id+"F0.wireOp",EDGE,"E66.trimOffspring")])],"isStart":false});
            var sketch = newSketch(context, id + "F90", { "sketchPlane" : qUnion([Q0]) });
            skLineSegment(sketch, "E890", {"start": v(9824.7, 1382.65) * mm, "end": v(9725.93, 1283.87) * mm});
            skLineSegment(sketch, "E891", {"start": v(9725.93, 1283.87) * mm, "end": v(9586.73, 1423.06) * mm});
            skLineSegment(sketch, "E892", {"start": v(9586.73, 1423.06) * mm, "end": v(9685.52, 1521.84) * mm});
            skLineSegment(sketch, "E893", {"start": v(9685.52, 1521.84) * mm, "end": v(9824.7, 1382.65) * mm});
            skLineSegment(sketch, "E894", {"start": v(9559.8, 1450) * mm, "end": v(9658.58, 1548.78) * mm});
            skLineSegment(sketch, "E895", {"start": v(9658.58, 1548.78) * mm, "end": v(9398.15, 1809.21) * mm});
            skLineSegment(sketch, "E896", {"start": v(9398.15, 1809.21) * mm, "end": v(9299.36, 1710.43) * mm});
            skLineSegment(sketch, "E897", {"start": v(9299.36, 1710.43) * mm, "end": v(9559.8, 1450) * mm});
            skLineSegment(sketch, "E898.1.0.0", {"start": v(9110.78, 2096.58) * mm, "end": v(9012, 1997.8) * mm});
            skLineSegment(sketch, "E898.1.0.1", {"start": v(9371.2, 1836.15) * mm, "end": v(9110.78, 2096.58) * mm});
            skLineSegment(sketch, "E898.1.0.2", {"start": v(9012, 1997.8) * mm, "end": v(9272.42, 1737.37) * mm});
            skLineSegment(sketch, "E898.1.0.3", {"start": v(9272.42, 1737.37) * mm, "end": v(9371.2, 1836.15) * mm});
            skLineSegment(sketch, "E898.2.0.0", {"start": v(8823.41, 2383.95) * mm, "end": v(8724.63, 2285.17) * mm});
            skLineSegment(sketch, "E898.2.0.1", {"start": v(9083.84, 2123.52) * mm, "end": v(8823.41, 2383.95) * mm});
            skLineSegment(sketch, "E898.2.0.2", {"start": v(8724.63, 2285.17) * mm, "end": v(8985.06, 2024.74) * mm});
            skLineSegment(sketch, "E898.2.0.3", {"start": v(8985.06, 2024.74) * mm, "end": v(9083.84, 2123.52) * mm});
            skLineSegment(sketch, "E898.3.0.0", {"start": v(8536.04, 2671.32) * mm, "end": v(8437.26, 2572.53) * mm});
            skLineSegment(sketch, "E898.3.0.1", {"start": v(8796.47, 2410.89) * mm, "end": v(8536.04, 2671.32) * mm});
            skLineSegment(sketch, "E898.3.0.2", {"start": v(8437.26, 2572.53) * mm, "end": v(8697.69, 2312.1) * mm});
            skLineSegment(sketch, "E898.3.0.3", {"start": v(8697.69, 2312.1) * mm, "end": v(8796.47, 2410.89) * mm});
            skLineSegment(sketch, "E898.4.0.0", {"start": v(8248.67, 2958.68) * mm, "end": v(8149.9, 2859.9) * mm});
            skLineSegment(sketch, "E898.4.0.1", {"start": v(8509.1, 2698.26) * mm, "end": v(8248.67, 2958.68) * mm});
            skLineSegment(sketch, "E898.4.0.2", {"start": v(8149.9, 2859.9) * mm, "end": v(8410.32, 2599.47) * mm});
            skLineSegment(sketch, "E898.4.0.3", {"start": v(8410.32, 2599.47) * mm, "end": v(8509.1, 2698.26) * mm});
            skLineSegment(sketch, "E898.5.0.0", {"start": v(7961.3, 3246.05) * mm, "end": v(7862.52, 3147.27) * mm});
            skLineSegment(sketch, "E898.5.0.1", {"start": v(8221.73, 2985.63) * mm, "end": v(7961.3, 3246.05) * mm});
            skLineSegment(sketch, "E898.5.0.2", {"start": v(7862.52, 3147.27) * mm, "end": v(8122.95, 2886.84) * mm});
            skLineSegment(sketch, "E898.5.0.3", {"start": v(8122.95, 2886.84) * mm, "end": v(8221.73, 2985.63) * mm});
            skLineSegment(sketch, "E898.6.0.0", {"start": v(7673.94, 3533.42) * mm, "end": v(7575.16, 3434.64) * mm});
            skLineSegment(sketch, "E898.6.0.1", {"start": v(7934.37, 3273) * mm, "end": v(7673.94, 3533.42) * mm});
            skLineSegment(sketch, "E898.6.0.2", {"start": v(7575.16, 3434.64) * mm, "end": v(7835.58, 3174.21) * mm});
            skLineSegment(sketch, "E898.6.0.3", {"start": v(7835.58, 3174.21) * mm, "end": v(7934.37, 3273) * mm});
            skLineSegment(sketch, "E898.7.0.0", {"start": v(7386.57, 3820.79) * mm, "end": v(7287.79, 3722) * mm});
            skLineSegment(sketch, "E898.7.0.1", {"start": v(7647, 3560.36) * mm, "end": v(7386.57, 3820.79) * mm});
            skLineSegment(sketch, "E898.7.0.2", {"start": v(7287.79, 3722) * mm, "end": v(7548.21, 3461.58) * mm});
            skLineSegment(sketch, "E898.7.0.3", {"start": v(7548.21, 3461.58) * mm, "end": v(7647, 3560.36) * mm});
            skLineSegment(sketch, "E898.8.0.0", {"start": v(7099.2, 4108.16) * mm, "end": v(7000.42, 4009.37) * mm});
            skLineSegment(sketch, "E898.8.0.1", {"start": v(7359.63, 3847.73) * mm, "end": v(7099.2, 4108.16) * mm});
            skLineSegment(sketch, "E898.8.0.2", {"start": v(7000.42, 4009.37) * mm, "end": v(7260.85, 3748.95) * mm});
            skLineSegment(sketch, "E898.8.0.3", {"start": v(7260.85, 3748.95) * mm, "end": v(7359.63, 3847.73) * mm});
            skLineSegment(sketch, "E898.9.0.0", {"start": v(6811.83, 4395.53) * mm, "end": v(6713.05, 4296.74) * mm});
            skLineSegment(sketch, "E898.9.0.1", {"start": v(7072.26, 4135.1) * mm, "end": v(6811.83, 4395.53) * mm});
            skLineSegment(sketch, "E898.9.0.2", {"start": v(6713.05, 4296.74) * mm, "end": v(6973.48, 4036.32) * mm});
            skLineSegment(sketch, "E898.9.0.3", {"start": v(6973.48, 4036.32) * mm, "end": v(7072.26, 4135.1) * mm});
            skLineSegment(sketch, "E898.10.0.0", {"start": v(6524.47, 4682.9) * mm, "end": v(6425.68, 4584.11) * mm});
            skLineSegment(sketch, "E898.10.0.1", {"start": v(6784.9, 4422.47) * mm, "end": v(6524.47, 4682.9) * mm});
            skLineSegment(sketch, "E898.10.0.2", {"start": v(6425.68, 4584.11) * mm, "end": v(6686.11, 4323.68) * mm});
            skLineSegment(sketch, "E898.10.0.3", {"start": v(6686.11, 4323.68) * mm, "end": v(6784.9, 4422.47) * mm});
            skLineSegment(sketch, "E898.11.0.0", {"start": v(6237.1, 4970.26) * mm, "end": v(6138.31, 4871.48) * mm});
            skLineSegment(sketch, "E898.11.0.1", {"start": v(6497.53, 4709.83) * mm, "end": v(6237.1, 4970.26) * mm});
            skLineSegment(sketch, "E898.11.0.2", {"start": v(6138.31, 4871.48) * mm, "end": v(6398.74, 4611.05) * mm});
            skLineSegment(sketch, "E898.11.0.3", {"start": v(6398.74, 4611.05) * mm, "end": v(6497.53, 4709.83) * mm});
            skLineSegment(sketch, "E898.12.0.0", {"start": v(5949.73, 5257.63) * mm, "end": v(5850.95, 5158.85) * mm});
            skLineSegment(sketch, "E898.12.0.1", {"start": v(6210.16, 4997.2) * mm, "end": v(5949.73, 5257.63) * mm});
            skLineSegment(sketch, "E898.12.0.2", {"start": v(5850.95, 5158.85) * mm, "end": v(6111.37, 4898.42) * mm});
            skLineSegment(sketch, "E898.12.0.3", {"start": v(6111.37, 4898.42) * mm, "end": v(6210.16, 4997.2) * mm});
            skLineSegment(sketch, "E898.13.0.0", {"start": v(5662.36, 5545) * mm, "end": v(5563.58, 5446.22) * mm});
            skLineSegment(sketch, "E898.13.0.1", {"start": v(5922.79, 5284.57) * mm, "end": v(5662.36, 5545) * mm});
            skLineSegment(sketch, "E898.13.0.2", {"start": v(5563.58, 5446.22) * mm, "end": v(5824, 5185.79) * mm});
            skLineSegment(sketch, "E898.13.0.3", {"start": v(5824, 5185.79) * mm, "end": v(5922.79, 5284.57) * mm});
            skLineSegment(sketch, "E898.14.0.0", {"start": v(5375, 5832.37) * mm, "end": v(5276.21, 5733.58) * mm});
            skLineSegment(sketch, "E898.14.0.1", {"start": v(5635.42, 5571.94) * mm, "end": v(5375, 5832.37) * mm});
            skLineSegment(sketch, "E898.14.0.2", {"start": v(5276.21, 5733.58) * mm, "end": v(5536.64, 5473.16) * mm});
            skLineSegment(sketch, "E898.14.0.3", {"start": v(5536.64, 5473.16) * mm, "end": v(5635.42, 5571.94) * mm});
            skLineSegment(sketch, "E898.15.0.0", {"start": v(5087.62, 6119.73) * mm, "end": v(4988.84, 6020.95) * mm});
            skLineSegment(sketch, "E898.15.0.1", {"start": v(5348.05, 5859.3) * mm, "end": v(5087.62, 6119.73) * mm});
            skLineSegment(sketch, "E898.15.0.2", {"start": v(4988.84, 6020.95) * mm, "end": v(5249.27, 5760.52) * mm});
            skLineSegment(sketch, "E898.15.0.3", {"start": v(5249.27, 5760.52) * mm, "end": v(5348.05, 5859.3) * mm});
            skLineSegment(sketch, "E898.16.0.0", {"start": v(4800.26, 6407.1) * mm, "end": v(4701.47, 6308.32) * mm});
            skLineSegment(sketch, "E898.16.0.1", {"start": v(5060.68, 6146.68) * mm, "end": v(4800.26, 6407.1) * mm});
            skLineSegment(sketch, "E898.16.0.2", {"start": v(4701.47, 6308.32) * mm, "end": v(4961.9, 6047.9) * mm});
            skLineSegment(sketch, "E898.16.0.3", {"start": v(4961.9, 6047.9) * mm, "end": v(5060.68, 6146.68) * mm});
            skLineSegment(sketch, "E898.direction1", {"start": v(9559.8, 1450) * mm, "end": v(9272.42, 1737.37) * mm, "construction": true});
            skLineSegment(sketch, "E899", {"start": v(4490.44, 6519.36) * mm, "end": v(4589.22, 6618.14) * mm});
            skLineSegment(sketch, "E900", {"start": v(4589.22, 6618.14) * mm, "end": v(4773.32, 6434.04) * mm});
            skLineSegment(sketch, "E901", {"start": v(4773.32, 6434.04) * mm, "end": v(4674.53, 6335.26) * mm});
            skLineSegment(sketch, "E902", {"start": v(4674.53, 6335.26) * mm, "end": v(4589.22, 6420.57) * mm});
            skLineSegment(sketch, "E903", {"start": v(4589.22, 6420.57) * mm, "end": v(4616.16, 6447.51) * mm});
            skLineSegment(sketch, "E904", {"start": v(4616.16, 6447.51) * mm, "end": v(4517.4, 6546.28) * mm});
            skLineSegment(sketch, "E905", {"start": v(4517.4, 6546.28) * mm, "end": v(4490.46, 6519.34) * mm});
            skLineSegment(sketch, "E906", {"start": v(4490.46, 6519.34) * mm, "end": v(4490.44, 6519.36) * mm});
            skSolve(sketch);
        }
        {
            var Q0;
            Q0 = qSketchRegion(id + "F90", true);
            var Q1;
            Q1=makeQuery(id+"F59.boolean.opBoolean","COPY",FACE,{"derivedFrom":makeQuery(id+"F59.opExtrude","CAP_FACE",FACE,{"disambiguationData":[OSD([sQuery(id+"F58.wireOp",EDGE,"E571"),sQuery(id+"F58.wireOp",EDGE,"E572"),sQuery(id+"F58.wireOp",EDGE,"E573"),sQuery(id+"F58.wireOp",EDGE,"E574")])],"isStart":false})});
            extrude(context, id + "F91", {"entities" : qUnion([Q0]), "operationType" : NewBodyOperationType.REMOVE, "endBound" : BoundingType.UP_TO_SURFACE, "oppositeDirection" : true, "endBoundEntityFace" : qUnion([Q1]), "depth" : 457.2 * mm});
        }
        {
            var Q0;
            {var subQ0=sQuery(id+"F0.wireOp",EDGE,"E13.4");var subQ1=sQuery(id+"F0.wireOp",EDGE,"E64.trimOffspring");var subQ2=sQuery(id+"F0.wireOp",EDGE,"E62");Q0=makeQuery(id+"F91.boolean.opBoolean","SPLIT",FACE,{"disambiguationData":[TD([makeQuery(id+"F1.opExtrude","SWEPT_FACE",FACE,{"disambiguationData":[OSD([subQ2])]})])],"derivedFrom":makeQuery(id+"F1.opExtrude","CAP_FACE",FACE,{"disambiguationData":[OSD([subQ0,subQ2,subQ1,sQuery(id+"F0.wireOp",EDGE,"E66.trimOffspring")])],"isStart":false})});}
            var sketch = newSketch(context, id + "F92", { "sketchPlane" : qUnion([Q0]) });
            skSolve(sketch);
        }
        {
            var Q0;
            {var subQ0=sQuery(id+"F0.wireOp",EDGE,"E62");Q0=makeQuery(id+"F92.imprint","IMPRINT",FACE,{"disambiguationData":[TD([[makeQuery(id+"F92.imprint","IMPRINT",EDGE,{"derivedFrom":makeQuery(id+"F1.opExtrude","CAP_EDGE",EDGE,{"disambiguationData":[OSD([subQ0])],"isStart":false})}),1.0]])]});}
            var Q1;
            {var subQ0=sQuery(id+"F0.wireOp",EDGE,"E64.trimOffspring");var subQ1=sQuery(id+"F0.wireOp",EDGE,"E13.4");Q1=makeQuery(id+"F91.boolean.opBoolean","SPLIT",FACE,{"disambiguationData":[TD([makeQuery(id+"F91.opExtrude","SWEPT_FACE",FACE,{"disambiguationData":[OSD([sQuery(id+"F90.wireOp",EDGE,"E892")])]})])],"derivedFrom":makeQuery(id+"F1.opExtrude","CAP_FACE",FACE,{"disambiguationData":[OSD([subQ1,sQuery(id+"F0.wireOp",EDGE,"E62"),subQ0,sQuery(id+"F0.wireOp",EDGE,"E66.trimOffspring")])],"isStart":false})});}
            var Q2;
            {var subQ0=sQuery(id+"F0.wireOp",EDGE,"E64.trimOffspring");var subQ1=sQuery(id+"F0.wireOp",EDGE,"E13.4");Q2=makeQuery(id+"F91.boolean.opBoolean","SPLIT",FACE,{"disambiguationData":[TD([makeQuery(id+"F91.opExtrude","SWEPT_FACE",FACE,{"disambiguationData":[OSD([sQuery(id+"F90.wireOp",EDGE,"E896")])]})])],"derivedFrom":makeQuery(id+"F1.opExtrude","CAP_FACE",FACE,{"disambiguationData":[OSD([subQ1,sQuery(id+"F0.wireOp",EDGE,"E62"),subQ0,sQuery(id+"F0.wireOp",EDGE,"E66.trimOffspring")])],"isStart":false})});}
            var Q3;
            {var subQ0=sQuery(id+"F0.wireOp",EDGE,"E64.trimOffspring");var subQ1=sQuery(id+"F0.wireOp",EDGE,"E13.4");Q3=makeQuery(id+"F91.boolean.opBoolean","SPLIT",FACE,{"disambiguationData":[TD([makeQuery(id+"F91.opExtrude","SWEPT_FACE",FACE,{"disambiguationData":[OSD([sQuery(id+"F90.wireOp",EDGE,"E898.1.0.0")])]})])],"derivedFrom":makeQuery(id+"F1.opExtrude","CAP_FACE",FACE,{"disambiguationData":[OSD([subQ1,sQuery(id+"F0.wireOp",EDGE,"E62"),subQ0,sQuery(id+"F0.wireOp",EDGE,"E66.trimOffspring")])],"isStart":false})});}
            var Q4;
            {var subQ0=sQuery(id+"F0.wireOp",EDGE,"E64.trimOffspring");var subQ1=sQuery(id+"F0.wireOp",EDGE,"E13.4");Q4=makeQuery(id+"F91.boolean.opBoolean","SPLIT",FACE,{"disambiguationData":[TD([makeQuery(id+"F91.opExtrude","SWEPT_FACE",FACE,{"disambiguationData":[OSD([sQuery(id+"F90.wireOp",EDGE,"E898.2.0.0")])]})])],"derivedFrom":makeQuery(id+"F1.opExtrude","CAP_FACE",FACE,{"disambiguationData":[OSD([subQ1,sQuery(id+"F0.wireOp",EDGE,"E62"),subQ0,sQuery(id+"F0.wireOp",EDGE,"E66.trimOffspring")])],"isStart":false})});}
            var Q5;
            {var subQ0=sQuery(id+"F0.wireOp",EDGE,"E64.trimOffspring");var subQ1=sQuery(id+"F0.wireOp",EDGE,"E13.4");Q5=makeQuery(id+"F91.boolean.opBoolean","SPLIT",FACE,{"disambiguationData":[TD([makeQuery(id+"F91.opExtrude","SWEPT_FACE",FACE,{"disambiguationData":[OSD([sQuery(id+"F90.wireOp",EDGE,"E898.3.0.0")])]})])],"derivedFrom":makeQuery(id+"F1.opExtrude","CAP_FACE",FACE,{"disambiguationData":[OSD([subQ1,sQuery(id+"F0.wireOp",EDGE,"E62"),subQ0,sQuery(id+"F0.wireOp",EDGE,"E66.trimOffspring")])],"isStart":false})});}
            var Q6;
            {var subQ0=sQuery(id+"F0.wireOp",EDGE,"E64.trimOffspring");var subQ1=sQuery(id+"F0.wireOp",EDGE,"E13.4");Q6=makeQuery(id+"F91.boolean.opBoolean","SPLIT",FACE,{"disambiguationData":[TD([makeQuery(id+"F91.opExtrude","SWEPT_FACE",FACE,{"disambiguationData":[OSD([sQuery(id+"F90.wireOp",EDGE,"E898.4.0.0")])]})])],"derivedFrom":makeQuery(id+"F1.opExtrude","CAP_FACE",FACE,{"disambiguationData":[OSD([subQ1,sQuery(id+"F0.wireOp",EDGE,"E62"),subQ0,sQuery(id+"F0.wireOp",EDGE,"E66.trimOffspring")])],"isStart":false})});}
            var Q7;
            {var subQ0=sQuery(id+"F0.wireOp",EDGE,"E64.trimOffspring");var subQ1=sQuery(id+"F0.wireOp",EDGE,"E13.4");Q7=makeQuery(id+"F91.boolean.opBoolean","SPLIT",FACE,{"disambiguationData":[TD([makeQuery(id+"F91.opExtrude","SWEPT_FACE",FACE,{"disambiguationData":[OSD([sQuery(id+"F90.wireOp",EDGE,"E898.5.0.0")])]})])],"derivedFrom":makeQuery(id+"F1.opExtrude","CAP_FACE",FACE,{"disambiguationData":[OSD([subQ1,sQuery(id+"F0.wireOp",EDGE,"E62"),subQ0,sQuery(id+"F0.wireOp",EDGE,"E66.trimOffspring")])],"isStart":false})});}
            var Q8;
            {var subQ0=sQuery(id+"F0.wireOp",EDGE,"E64.trimOffspring");var subQ1=sQuery(id+"F0.wireOp",EDGE,"E13.4");Q8=makeQuery(id+"F91.boolean.opBoolean","SPLIT",FACE,{"disambiguationData":[TD([makeQuery(id+"F91.opExtrude","SWEPT_FACE",FACE,{"disambiguationData":[OSD([sQuery(id+"F90.wireOp",EDGE,"E898.6.0.0")])]})])],"derivedFrom":makeQuery(id+"F1.opExtrude","CAP_FACE",FACE,{"disambiguationData":[OSD([subQ1,sQuery(id+"F0.wireOp",EDGE,"E62"),subQ0,sQuery(id+"F0.wireOp",EDGE,"E66.trimOffspring")])],"isStart":false})});}
            var Q9;
            {var subQ0=sQuery(id+"F0.wireOp",EDGE,"E64.trimOffspring");var subQ1=sQuery(id+"F0.wireOp",EDGE,"E13.4");Q9=makeQuery(id+"F91.boolean.opBoolean","SPLIT",FACE,{"disambiguationData":[TD([makeQuery(id+"F91.opExtrude","SWEPT_FACE",FACE,{"disambiguationData":[OSD([sQuery(id+"F90.wireOp",EDGE,"E898.7.0.0")])]})])],"derivedFrom":makeQuery(id+"F1.opExtrude","CAP_FACE",FACE,{"disambiguationData":[OSD([subQ1,sQuery(id+"F0.wireOp",EDGE,"E62"),subQ0,sQuery(id+"F0.wireOp",EDGE,"E66.trimOffspring")])],"isStart":false})});}
            var Q10;
            {var subQ0=sQuery(id+"F0.wireOp",EDGE,"E64.trimOffspring");var subQ1=sQuery(id+"F0.wireOp",EDGE,"E13.4");Q10=makeQuery(id+"F91.boolean.opBoolean","SPLIT",FACE,{"disambiguationData":[TD([makeQuery(id+"F91.opExtrude","SWEPT_FACE",FACE,{"disambiguationData":[OSD([sQuery(id+"F90.wireOp",EDGE,"E898.8.0.0")])]})])],"derivedFrom":makeQuery(id+"F1.opExtrude","CAP_FACE",FACE,{"disambiguationData":[OSD([subQ1,sQuery(id+"F0.wireOp",EDGE,"E62"),subQ0,sQuery(id+"F0.wireOp",EDGE,"E66.trimOffspring")])],"isStart":false})});}
            var Q11;
            {var subQ0=sQuery(id+"F0.wireOp",EDGE,"E64.trimOffspring");var subQ1=sQuery(id+"F0.wireOp",EDGE,"E13.4");Q11=makeQuery(id+"F91.boolean.opBoolean","SPLIT",FACE,{"disambiguationData":[TD([makeQuery(id+"F91.opExtrude","SWEPT_FACE",FACE,{"disambiguationData":[OSD([sQuery(id+"F90.wireOp",EDGE,"E898.9.0.0")])]})])],"derivedFrom":makeQuery(id+"F1.opExtrude","CAP_FACE",FACE,{"disambiguationData":[OSD([subQ1,sQuery(id+"F0.wireOp",EDGE,"E62"),subQ0,sQuery(id+"F0.wireOp",EDGE,"E66.trimOffspring")])],"isStart":false})});}
            var Q12;
            {var subQ0=sQuery(id+"F0.wireOp",EDGE,"E64.trimOffspring");var subQ1=sQuery(id+"F0.wireOp",EDGE,"E13.4");Q12=makeQuery(id+"F91.boolean.opBoolean","SPLIT",FACE,{"disambiguationData":[TD([makeQuery(id+"F91.opExtrude","SWEPT_FACE",FACE,{"disambiguationData":[OSD([sQuery(id+"F90.wireOp",EDGE,"E898.10.0.0")])]})])],"derivedFrom":makeQuery(id+"F1.opExtrude","CAP_FACE",FACE,{"disambiguationData":[OSD([subQ1,sQuery(id+"F0.wireOp",EDGE,"E62"),subQ0,sQuery(id+"F0.wireOp",EDGE,"E66.trimOffspring")])],"isStart":false})});}
            var Q13;
            {var subQ0=sQuery(id+"F0.wireOp",EDGE,"E64.trimOffspring");var subQ1=sQuery(id+"F0.wireOp",EDGE,"E13.4");Q13=makeQuery(id+"F91.boolean.opBoolean","SPLIT",FACE,{"disambiguationData":[TD([makeQuery(id+"F91.opExtrude","SWEPT_FACE",FACE,{"disambiguationData":[OSD([sQuery(id+"F90.wireOp",EDGE,"E898.11.0.0")])]})])],"derivedFrom":makeQuery(id+"F1.opExtrude","CAP_FACE",FACE,{"disambiguationData":[OSD([subQ1,sQuery(id+"F0.wireOp",EDGE,"E62"),subQ0,sQuery(id+"F0.wireOp",EDGE,"E66.trimOffspring")])],"isStart":false})});}
            var Q14;
            {var subQ0=sQuery(id+"F0.wireOp",EDGE,"E64.trimOffspring");var subQ1=sQuery(id+"F0.wireOp",EDGE,"E13.4");Q14=makeQuery(id+"F91.boolean.opBoolean","SPLIT",FACE,{"disambiguationData":[TD([makeQuery(id+"F91.opExtrude","SWEPT_FACE",FACE,{"disambiguationData":[OSD([sQuery(id+"F90.wireOp",EDGE,"E898.12.0.0")])]})])],"derivedFrom":makeQuery(id+"F1.opExtrude","CAP_FACE",FACE,{"disambiguationData":[OSD([subQ1,sQuery(id+"F0.wireOp",EDGE,"E62"),subQ0,sQuery(id+"F0.wireOp",EDGE,"E66.trimOffspring")])],"isStart":false})});}
            var Q15;
            {var subQ0=sQuery(id+"F0.wireOp",EDGE,"E64.trimOffspring");var subQ1=sQuery(id+"F0.wireOp",EDGE,"E13.4");Q15=makeQuery(id+"F91.boolean.opBoolean","SPLIT",FACE,{"disambiguationData":[TD([makeQuery(id+"F91.opExtrude","SWEPT_FACE",FACE,{"disambiguationData":[OSD([sQuery(id+"F90.wireOp",EDGE,"E898.13.0.0")])]})])],"derivedFrom":makeQuery(id+"F1.opExtrude","CAP_FACE",FACE,{"disambiguationData":[OSD([subQ1,sQuery(id+"F0.wireOp",EDGE,"E62"),subQ0,sQuery(id+"F0.wireOp",EDGE,"E66.trimOffspring")])],"isStart":false})});}
            var Q16;
            {var subQ0=sQuery(id+"F0.wireOp",EDGE,"E64.trimOffspring");var subQ1=sQuery(id+"F0.wireOp",EDGE,"E13.4");Q16=makeQuery(id+"F91.boolean.opBoolean","SPLIT",FACE,{"disambiguationData":[TD([makeQuery(id+"F91.opExtrude","SWEPT_FACE",FACE,{"disambiguationData":[OSD([sQuery(id+"F90.wireOp",EDGE,"E898.14.0.0")])]})])],"derivedFrom":makeQuery(id+"F1.opExtrude","CAP_FACE",FACE,{"disambiguationData":[OSD([subQ1,sQuery(id+"F0.wireOp",EDGE,"E62"),subQ0,sQuery(id+"F0.wireOp",EDGE,"E66.trimOffspring")])],"isStart":false})});}
            var Q17;
            {var subQ0=sQuery(id+"F0.wireOp",EDGE,"E64.trimOffspring");var subQ1=sQuery(id+"F0.wireOp",EDGE,"E13.4");Q17=makeQuery(id+"F91.boolean.opBoolean","SPLIT",FACE,{"disambiguationData":[TD([makeQuery(id+"F91.opExtrude","SWEPT_FACE",FACE,{"disambiguationData":[OSD([sQuery(id+"F90.wireOp",EDGE,"E898.15.0.0")])]})])],"derivedFrom":makeQuery(id+"F1.opExtrude","CAP_FACE",FACE,{"disambiguationData":[OSD([subQ1,sQuery(id+"F0.wireOp",EDGE,"E62"),subQ0,sQuery(id+"F0.wireOp",EDGE,"E66.trimOffspring")])],"isStart":false})});}
            var Q18;
            {var subQ0=sQuery(id+"F0.wireOp",EDGE,"E64.trimOffspring");var subQ1=sQuery(id+"F0.wireOp",EDGE,"E13.4");Q18=makeQuery(id+"F91.boolean.opBoolean","SPLIT",FACE,{"disambiguationData":[TD([makeQuery(id+"F91.opExtrude","SWEPT_FACE",FACE,{"disambiguationData":[OSD([sQuery(id+"F90.wireOp",EDGE,"E898.16.0.0")])]})])],"derivedFrom":makeQuery(id+"F1.opExtrude","CAP_FACE",FACE,{"disambiguationData":[OSD([subQ1,sQuery(id+"F0.wireOp",EDGE,"E62"),subQ0,sQuery(id+"F0.wireOp",EDGE,"E66.trimOffspring")])],"isStart":false})});}
            var Q19;
            {var subQ0=sQuery(id+"F0.wireOp",EDGE,"E13.4");Q19=makeQuery(id+"F91.boolean.opBoolean","SPLIT",FACE,{"disambiguationData":[TD([makeQuery(id+"F91.opExtrude","SWEPT_FACE",FACE,{"disambiguationData":[OSD([sQuery(id+"F90.wireOp",EDGE,"E903")])]})])],"derivedFrom":makeQuery(id+"F1.opExtrude","CAP_FACE",FACE,{"disambiguationData":[OSD([subQ0,sQuery(id+"F0.wireOp",EDGE,"E62"),sQuery(id+"F0.wireOp",EDGE,"E64.trimOffspring"),sQuery(id+"F0.wireOp",EDGE,"E66.trimOffspring")])],"isStart":false})});}
            var Q20;
            {var subQ0=sQuery(id+"F0.wireOp",EDGE,"E66.trimOffspring");var subQ1=sQuery(id+"F0.wireOp",EDGE,"E13.4");var subQ2=sQuery(id+"F0.wireOp",EDGE,"E64.trimOffspring");Q20=makeQuery(id+"F91.boolean.opBoolean","SPLIT",FACE,{"disambiguationData":[TD([makeQuery(id+"F1.opExtrude","SWEPT_FACE",FACE,{"disambiguationData":[OSD([subQ0])]})])],"derivedFrom":makeQuery(id+"F1.opExtrude","CAP_FACE",FACE,{"disambiguationData":[OSD([subQ1,sQuery(id+"F0.wireOp",EDGE,"E62"),subQ2,subQ0])],"isStart":false})});}
            extrude(context, id + "F93", {"entities" : qUnion([Q0, Q1, Q2, Q3, Q4, Q5, Q6, Q7, Q8, Q9, Q10, Q11, Q12, Q13, Q14, Q15, Q16, Q17, Q18, Q19, Q20]), "operationType" : NewBodyOperationType.ADD, "depth" : 2352.67 * mm});
        }
        {
            var Q0;
            Q0=makeQuery(id+"F93.opExtrude","CAP_FACE",FACE,{"disambiguationData":[OSD([sQuery(id+"F0.wireOp",EDGE,"E13.4"),sQuery(id+"F0.wireOp",EDGE,"E62"),sQuery(id+"F0.wireOp",EDGE,"E64.trimOffspring"),sQuery(id+"F90.wireOp",EDGE,"E890")])],"isStart":false});
            var sketch = newSketch(context, id + "F94", { "sketchPlane" : qUnion([Q0]) });
            skLineSegment(sketch, "E907", {"start": v(9752.85, 1256.94) * mm, "end": v(4463.5, 6546.3) * mm});
            skLineSegment(sketch, "E908", {"start": v(4463.5, 6546.3) * mm, "end": v(4562.28, 6645.08) * mm});
            skLineSegment(sketch, "E909", {"start": v(4562.28, 6645.08) * mm, "end": v(9851.63, 1355.73) * mm});
            skLineSegment(sketch, "E910", {"start": v(9851.63, 1355.73) * mm, "end": v(9752.85, 1256.94) * mm});
            skSolve(sketch);
        }
        {
            var Q0;
            Q0 = qSketchRegion(id + "F94", true);
            extrude(context, id + "F95", {"entities" : qUnion([Q0]), "operationType" : NewBodyOperationType.ADD, "depth" : 76.2 * mm});
        }
        {
            var Q0;
            Q0=makeQuery(id+"F1.opExtrude","CAP_FACE",FACE,{"disambiguationData":[OSD([sQuery(id+"F0.wireOp",EDGE,"E13.5"),sQuery(id+"F0.wireOp",EDGE,"E17.0"),sQuery(id+"F0.wireOp",EDGE,"E42"),sQuery(id+"F0.wireOp",EDGE,"E43"),sQuery(id+"F0.wireOp",EDGE,"E48"),sQuery(id+"F0.wireOp",EDGE,"E49.trimOffspring")])],"isStart":false});
            var sketch = newSketch(context, id + "F96", { "sketchPlane" : qUnion([Q0]) });
            skLineSegment(sketch, "E911", {"start": v(3305.04, 5387.84) * mm, "end": v(3403.83, 5289.06) * mm});
            skLineSegment(sketch, "E912", {"start": v(3403.83, 5289.06) * mm, "end": v(3376.89, 5262.12) * mm});
            skLineSegment(sketch, "E913", {"start": v(3376.89, 5262.12) * mm, "end": v(3278.1, 5360.9) * mm});
            skLineSegment(sketch, "E914", {"start": v(3278.1, 5360.9) * mm, "end": v(3305.04, 5387.84) * mm});
            skLineSegment(sketch, "E915", {"start": v(3278.09, 5360.89) * mm, "end": v(3305.03, 5333.94) * mm});
            skLineSegment(sketch, "E916", {"start": v(3305.03, 5333.94) * mm, "end": v(3206.26, 5235.18) * mm});
            skLineSegment(sketch, "E917", {"start": v(3206.26, 5235.18) * mm, "end": v(3179.32, 5262.12) * mm});
            skLineSegment(sketch, "E918", {"start": v(3179.32, 5262.12) * mm, "end": v(3278.09, 5360.89) * mm});
            skLineSegment(sketch, "E919", {"start": v(635.02, 2717.82) * mm, "end": v(733.8, 2619.04) * mm});
            skLineSegment(sketch, "E920", {"start": v(733.8, 2619.04) * mm, "end": v(760.72, 2645.96) * mm});
            skLineSegment(sketch, "E921", {"start": v(760.72, 2645.96) * mm, "end": v(661.94, 2744.74) * mm});
            skLineSegment(sketch, "E922", {"start": v(661.94, 2744.74) * mm, "end": v(635.02, 2717.82) * mm});
            skLineSegment(sketch, "E923", {"start": v(3129.93, 5015.16) * mm, "end": v(3031.15, 5113.95) * mm});
            skLineSegment(sketch, "E924", {"start": v(3031.15, 5113.95) * mm, "end": v(3004.2, 5087) * mm});
            skLineSegment(sketch, "E925", {"start": v(3004.2, 5087) * mm, "end": v(3102.99, 4988.22) * mm});
            skLineSegment(sketch, "E926", {"start": v(3102.99, 4988.22) * mm, "end": v(3129.93, 5015.16) * mm});
            skLineSegment(sketch, "E927.1.0.0", {"start": v(2716.84, 4799.64) * mm, "end": v(2815.62, 4700.85) * mm});
            skLineSegment(sketch, "E927.1.0.1", {"start": v(2815.62, 4700.85) * mm, "end": v(2842.56, 4727.8) * mm});
            skLineSegment(sketch, "E927.1.0.2", {"start": v(2842.56, 4727.8) * mm, "end": v(2743.78, 4826.58) * mm});
            skLineSegment(sketch, "E927.1.0.3", {"start": v(2743.78, 4826.58) * mm, "end": v(2716.84, 4799.64) * mm});
            skLineSegment(sketch, "E927.2.0.0", {"start": v(2429.47, 4512.27) * mm, "end": v(2528.25, 4413.49) * mm});
            skLineSegment(sketch, "E927.2.0.1", {"start": v(2528.25, 4413.49) * mm, "end": v(2555.2, 4440.43) * mm});
            skLineSegment(sketch, "E927.2.0.2", {"start": v(2555.2, 4440.43) * mm, "end": v(2456.4, 4539.2) * mm});
            skLineSegment(sketch, "E927.2.0.3", {"start": v(2456.4, 4539.2) * mm, "end": v(2429.47, 4512.27) * mm});
            skLineSegment(sketch, "E927.3.0.0", {"start": v(2142.1, 4224.9) * mm, "end": v(2240.88, 4126.12) * mm});
            skLineSegment(sketch, "E927.3.0.1", {"start": v(2240.88, 4126.12) * mm, "end": v(2267.82, 4153.06) * mm});
            skLineSegment(sketch, "E927.3.0.2", {"start": v(2267.82, 4153.06) * mm, "end": v(2169.04, 4251.84) * mm});
            skLineSegment(sketch, "E927.3.0.3", {"start": v(2169.04, 4251.84) * mm, "end": v(2142.1, 4224.9) * mm});
            skLineSegment(sketch, "E927.4.0.0", {"start": v(1854.73, 3937.53) * mm, "end": v(1953.52, 3838.75) * mm});
            skLineSegment(sketch, "E927.4.0.1", {"start": v(1953.52, 3838.75) * mm, "end": v(1980.46, 3865.7) * mm});
            skLineSegment(sketch, "E927.4.0.2", {"start": v(1980.46, 3865.7) * mm, "end": v(1881.67, 3964.47) * mm});
            skLineSegment(sketch, "E927.4.0.3", {"start": v(1881.67, 3964.47) * mm, "end": v(1854.73, 3937.53) * mm});
            skLineSegment(sketch, "E927.5.0.0", {"start": v(1567.36, 3650.16) * mm, "end": v(1666.15, 3551.38) * mm});
            skLineSegment(sketch, "E927.5.0.1", {"start": v(1666.15, 3551.38) * mm, "end": v(1693.09, 3578.32) * mm});
            skLineSegment(sketch, "E927.5.0.2", {"start": v(1693.09, 3578.32) * mm, "end": v(1594.3, 3677.1) * mm});
            skLineSegment(sketch, "E927.5.0.3", {"start": v(1594.3, 3677.1) * mm, "end": v(1567.36, 3650.16) * mm});
            skLineSegment(sketch, "E927.6.0.0", {"start": v(1280, 3362.8) * mm, "end": v(1378.78, 3264.01) * mm});
            skLineSegment(sketch, "E927.6.0.1", {"start": v(1378.78, 3264.01) * mm, "end": v(1405.72, 3290.95) * mm});
            skLineSegment(sketch, "E927.6.0.2", {"start": v(1405.72, 3290.95) * mm, "end": v(1306.94, 3389.74) * mm});
            skLineSegment(sketch, "E927.6.0.3", {"start": v(1306.94, 3389.74) * mm, "end": v(1280, 3362.8) * mm});
            skLineSegment(sketch, "E927.7.0.0", {"start": v(992.63, 3075.43) * mm, "end": v(1091.41, 2976.65) * mm});
            skLineSegment(sketch, "E927.7.0.1", {"start": v(1091.41, 2976.65) * mm, "end": v(1118.35, 3003.59) * mm});
            skLineSegment(sketch, "E927.7.0.2", {"start": v(1118.35, 3003.59) * mm, "end": v(1019.57, 3102.37) * mm});
            skLineSegment(sketch, "E927.7.0.3", {"start": v(1019.57, 3102.37) * mm, "end": v(992.63, 3075.43) * mm});
            skLineSegment(sketch, "E927.direction1", {"start": v(3102.99, 4988.22) * mm, "end": v(2815.62, 4700.85) * mm, "construction": true});
            skLineSegment(sketch, "E928", {"start": v(3188.3, 5307.02) * mm, "end": v(1553.9, 3672.62) * mm, "construction": true});
            skLineSegment(sketch, "E929", {"start": v(1567.35, 3650.15) * mm, "end": v(1594.29, 3623.2) * mm});
            skLineSegment(sketch, "E930", {"start": v(1594.29, 3623.2) * mm, "end": v(1531.44, 3560.36) * mm});
            skLineSegment(sketch, "E931", {"start": v(1531.44, 3560.36) * mm, "end": v(1504.5, 3587.3) * mm});
            skLineSegment(sketch, "E932", {"start": v(1504.5, 3587.3) * mm, "end": v(1567.35, 3650.15) * mm});
            skLineSegment(sketch, "E933", {"start": v(1549.39, 3632.19) * mm, "end": v(1576.33, 3605.25) * mm, "construction": true});
            skLineSegment(sketch, "E934", {"start": v(1486.52, 3569.32) * mm, "end": v(1513.46, 3542.38) * mm, "construction": true});
            skLineSegment(sketch, "E935", {"start": v(1553.9, 3672.62) * mm, "end": v(1571.85, 3654.65) * mm, "construction": true});
            skLineSegment(sketch, "E936", {"start": v(1553.9, 3672.62) * mm, "end": v(1491.03, 3609.75) * mm, "construction": true});
            skLineSegment(sketch, "E937", {"start": v(1491.03, 3609.75) * mm, "end": v(1509, 3591.8) * mm, "construction": true});
            skLineSegment(sketch, "E938", {"start": v(1504.48, 3587.28) * mm, "end": v(1603.27, 3488.5) * mm});
            skLineSegment(sketch, "E939", {"start": v(1603.27, 3488.5) * mm, "end": v(1576.34, 3461.58) * mm});
            skLineSegment(sketch, "E940", {"start": v(1576.34, 3461.58) * mm, "end": v(1477.56, 3560.36) * mm});
            skLineSegment(sketch, "E941", {"start": v(1477.56, 3560.36) * mm, "end": v(1504.48, 3587.28) * mm});
            skLineSegment(sketch, "E942", {"start": v(1477.54, 3560.34) * mm, "end": v(1576.33, 3461.56) * mm});
            skLineSegment(sketch, "E943", {"start": v(1576.33, 3461.56) * mm, "end": v(1549.4, 3434.64) * mm});
            skLineSegment(sketch, "E944", {"start": v(1549.4, 3434.64) * mm, "end": v(1450.62, 3533.42) * mm});
            skLineSegment(sketch, "E945", {"start": v(1450.62, 3533.42) * mm, "end": v(1477.54, 3560.34) * mm});
            skLineSegment(sketch, "E946", {"start": v(759.14, 2841.94) * mm, "end": v(857.92, 2743.16) * mm});
            skLineSegment(sketch, "E947", {"start": v(857.92, 2743.16) * mm, "end": v(830.98, 2716.22) * mm});
            skLineSegment(sketch, "E948", {"start": v(830.98, 2716.22) * mm, "end": v(732.2, 2815) * mm});
            skLineSegment(sketch, "E949", {"start": v(732.2, 2815) * mm, "end": v(759.14, 2841.94) * mm});
            skLineSegment(sketch, "E950", {"start": v(732.18, 2814.98) * mm, "end": v(830.97, 2716.2) * mm});
            skLineSegment(sketch, "E951", {"start": v(830.97, 2716.2) * mm, "end": v(804.04, 2689.28) * mm});
            skLineSegment(sketch, "E952", {"start": v(804.04, 2689.28) * mm, "end": v(705.26, 2788.06) * mm});
            skLineSegment(sketch, "E953", {"start": v(705.26, 2788.06) * mm, "end": v(732.18, 2814.98) * mm});
            skLineSegment(sketch, "E954", {"start": v(7003.79, -1492.15) * mm, "end": v(1813.2, 3698.43) * mm, "construction": true});
            skLineSegment(sketch, "E955", {"start": v(1905.25, 3790.48) * mm, "end": v(7095.83, -1400.1) * mm, "construction": true});
            skLineSegment(sketch, "E956", {"start": v(1813.2, 3698.43) * mm, "end": v(1714.42, 3797.22) * mm});
            skLineSegment(sketch, "E957", {"start": v(1714.42, 3797.22) * mm, "end": v(1687.48, 3770.28) * mm});
            skLineSegment(sketch, "E958", {"start": v(1687.48, 3770.28) * mm, "end": v(1786.26, 3671.5) * mm});
            skLineSegment(sketch, "E959", {"start": v(1786.26, 3671.5) * mm, "end": v(1813.2, 3698.43) * mm});
            skLineSegment(sketch, "E960", {"start": v(1905.25, 3790.48) * mm, "end": v(1806.46, 3889.26) * mm});
            skLineSegment(sketch, "E961", {"start": v(1806.46, 3889.26) * mm, "end": v(1833.4, 3916.2) * mm});
            skLineSegment(sketch, "E962", {"start": v(1833.4, 3916.2) * mm, "end": v(1932.19, 3817.42) * mm});
            skLineSegment(sketch, "E963", {"start": v(1932.19, 3817.42) * mm, "end": v(1905.25, 3790.48) * mm});
            skLineSegment(sketch, "E964", {"start": v(1806.45, 3889.25) * mm, "end": v(1905.23, 3790.46) * mm});
            skLineSegment(sketch, "E965", {"start": v(1905.23, 3790.46) * mm, "end": v(1878.3, 3763.54) * mm});
            skLineSegment(sketch, "E966", {"start": v(1878.3, 3763.54) * mm, "end": v(1779.52, 3862.32) * mm});
            skLineSegment(sketch, "E967", {"start": v(1779.52, 3862.32) * mm, "end": v(1806.45, 3889.25) * mm});
            skLineSegment(sketch, "E968", {"start": v(1773.91, 3856.71) * mm, "end": v(1872.7, 3757.93) * mm});
            skLineSegment(sketch, "E969", {"start": v(1872.7, 3757.93) * mm, "end": v(1845.75, 3730.99) * mm});
            skLineSegment(sketch, "E970", {"start": v(1845.75, 3730.99) * mm, "end": v(1746.97, 3829.77) * mm});
            skLineSegment(sketch, "E971", {"start": v(1746.97, 3829.77) * mm, "end": v(1773.91, 3856.71) * mm});
            skLineSegment(sketch, "E972", {"start": v(1741.36, 3824.16) * mm, "end": v(1840.14, 3725.37) * mm});
            skLineSegment(sketch, "E973", {"start": v(1840.14, 3725.37) * mm, "end": v(1813.22, 3698.45) * mm});
            skLineSegment(sketch, "E974", {"start": v(1813.22, 3698.45) * mm, "end": v(1714.43, 3797.23) * mm});
            skLineSegment(sketch, "E975", {"start": v(1714.43, 3797.23) * mm, "end": v(1741.36, 3824.16) * mm});
            skSolve(sketch);
        }
        {
            var Q0;
            Q0 = qSketchRegion(id + "F96", true);
            extrude(context, id + "F97", {"entities" : qUnion([Q0]), "operationType" : NewBodyOperationType.ADD, "depth" : 2352.67 * mm});
        }
        {
            var Q0;
            Q0=makeQuery(id+"F97.opExtrude","CAP_FACE",FACE,{"disambiguationData":[OSD([sQuery(id+"F96.wireOp",EDGE,"E911"),sQuery(id+"F96.wireOp",EDGE,"E912"),sQuery(id+"F96.wireOp",EDGE,"E913"),sQuery(id+"F96.wireOp",EDGE,"E914")])],"isStart":false});
            var sketch = newSketch(context, id + "F98", { "sketchPlane" : qUnion([Q0]) });
            skLineSegment(sketch, "E976", {"start": v(3305.04, 5387.84) * mm, "end": v(3403.83, 5289.06) * mm});
            skLineSegment(sketch, "E977", {"start": v(3403.83, 5289.06) * mm, "end": v(733.8, 2619.04) * mm});
            skLineSegment(sketch, "E978", {"start": v(733.8, 2619.04) * mm, "end": v(635.02, 2717.82) * mm});
            skLineSegment(sketch, "E979", {"start": v(635.02, 2717.82) * mm, "end": v(3305.04, 5387.84) * mm});
            skSolve(sketch);
        }
        {
            var Q0;
            Q0 = qSketchRegion(id + "F98", true);
            extrude(context, id + "F99", {"entities" : qUnion([Q0]), "operationType" : NewBodyOperationType.ADD, "depth" : 76.2 * mm});
        }
        {
            var Q0;
            Q0=makeQuery(id+"F99.boolean.opBoolean","MERGE",FACE,{"derivedFrom":[makeQuery(id+"F97.boolean.opBoolean","MERGE",FACE,{"derivedFrom":[makeQuery(id+"F1.opExtrude","SWEPT_FACE",FACE,{"disambiguationData":[OSD([sQuery(id+"F0.wireOp",EDGE,"E13.5"),sQuery(id+"F0.wireOp",EDGE,"E49.trimOffspring")])]}),makeQuery(id+"F97.opExtrude","SWEPT_FACE",FACE,{"disambiguationData":[OSD([sQuery(id+"F96.wireOp",EDGE,"E912")])]}),makeQuery(id+"F97.opExtrude","SWEPT_FACE",FACE,{"disambiguationData":[OSD([sQuery(id+"F96.wireOp",EDGE,"E920")])]}),makeQuery(id+"F97.opExtrude","SWEPT_FACE",FACE,{"disambiguationData":[OSD([sQuery(id+"F96.wireOp",EDGE,"E926")])]}),makeQuery(id+"F97.opExtrude","SWEPT_FACE",FACE,{"disambiguationData":[OSD([sQuery(id+"F96.wireOp",EDGE,"E927.1.0.1")])]}),makeQuery(id+"F97.opExtrude","SWEPT_FACE",FACE,{"disambiguationData":[OSD([sQuery(id+"F96.wireOp",EDGE,"E927.2.0.1")])]}),makeQuery(id+"F97.opExtrude","SWEPT_FACE",FACE,{"disambiguationData":[OSD([sQuery(id+"F96.wireOp",EDGE,"E927.3.0.1")])]}),makeQuery(id+"F97.opExtrude","SWEPT_FACE",FACE,{"disambiguationData":[OSD([sQuery(id+"F96.wireOp",EDGE,"E927.4.0.1")])]}),makeQuery(id+"F97.opExtrude","SWEPT_FACE",FACE,{"disambiguationData":[OSD([sQuery(id+"F96.wireOp",EDGE,"E927.5.0.1")])]}),makeQuery(id+"F97.opExtrude","SWEPT_FACE",FACE,{"disambiguationData":[OSD([sQuery(id+"F96.wireOp",EDGE,"E927.6.0.1")])]}),makeQuery(id+"F97.opExtrude","SWEPT_FACE",FACE,{"disambiguationData":[OSD([sQuery(id+"F96.wireOp",EDGE,"E927.7.0.1")])]}),makeQuery(id+"F97.opExtrude","SWEPT_FACE",FACE,{"disambiguationData":[OSD([sQuery(id+"F96.wireOp",EDGE,"E939")])]}),makeQuery(id+"F97.opExtrude","SWEPT_FACE",FACE,{"disambiguationData":[OSD([sQuery(id+"F96.wireOp",EDGE,"E943")])]}),makeQuery(id+"F97.opExtrude","SWEPT_FACE",FACE,{"disambiguationData":[OSD([sQuery(id+"F96.wireOp",EDGE,"E947")])]}),makeQuery(id+"F97.opExtrude","SWEPT_FACE",FACE,{"disambiguationData":[OSD([sQuery(id+"F96.wireOp",EDGE,"E951")])]})]}),makeQuery(id+"F99.opExtrude","SWEPT_FACE",FACE,{"disambiguationData":[OSD([sQuery(id+"F98.wireOp",EDGE,"E977")])]})]});
            var sketch = newSketch(context, id + "F100", { "sketchPlane" : qUnion([Q0]) });
            skLineSegment(sketch, "E980", {"start": v(2508.22, 2390.78) * mm, "end": v(2508.22, 2095.5) * mm});
            skLineSegment(sketch, "E981", {"start": v(2508.22, 2095.5) * mm, "end": v(2546.35, 2095.5) * mm});
            skLineSegment(sketch, "E982", {"start": v(2546.35, 2095.5) * mm, "end": v(2546.35, 0) * mm});
            skLineSegment(sketch, "E983", {"start": v(2546.35, 0) * mm, "end": v(3524.25, 0) * mm});
            skLineSegment(sketch, "E984", {"start": v(3524.25, 0) * mm, "end": v(3524.25, 2095.5) * mm});
            skLineSegment(sketch, "E985", {"start": v(3524.25, 2095.5) * mm, "end": v(3562.32, 2095.5) * mm});
            skLineSegment(sketch, "E986", {"start": v(3562.32, 2095.5) * mm, "end": v(3562.32, 2390.78) * mm});
            skLineSegment(sketch, "E987", {"start": v(3562.32, 2390.78) * mm, "end": v(3524.25, 2390.78) * mm});
            skLineSegment(sketch, "E988", {"start": v(3524.25, 2390.78) * mm, "end": v(3524.25, 2235.2) * mm});
            skLineSegment(sketch, "E989", {"start": v(3524.25, 2235.2) * mm, "end": v(2546.35, 2235.2) * mm});
            skLineSegment(sketch, "E990", {"start": v(2546.35, 2235.2) * mm, "end": v(2546.35, 2390.78) * mm});
            skLineSegment(sketch, "E991", {"start": v(2546.35, 2390.78) * mm, "end": v(2508.22, 2390.78) * mm});
            skLineSegment(sketch, "E992.bottom", {"start": v(3897.31, 2466.98) * mm, "end": v(4027.49, 2466.98) * mm});
            skLineSegment(sketch, "E992.top", {"start": v(3897.31, 2273.3) * mm, "end": v(4027.49, 2273.3) * mm});
            skLineSegment(sketch, "E992.left", {"start": v(3897.31, 2466.98) * mm, "end": v(3897.31, 2273.3) * mm});
            skLineSegment(sketch, "E992.right", {"start": v(4027.49, 2466.98) * mm, "end": v(4027.49, 2273.3) * mm});
            skSolve(sketch);
        }
        {
            var Q0;
            Q0 = qSketchRegion(id + "F100", true);
            extrude(context, id + "F101", {"entities" : qUnion([Q0]), "operationType" : NewBodyOperationType.REMOVE, "oppositeDirection" : true, "depth" : 139.7 * mm});
        }
        {
            var Q0;
            Q0=makeQuery(id+"F97.opExtrude","SWEPT_FACE",FACE,{"disambiguationData":[OSD([sQuery(id+"F96.wireOp",EDGE,"E940")])]});
            var sketch = newSketch(context, id + "F102", { "sketchPlane" : qUnion([Q0]) });
            skLineSegment(sketch, "E993.bottom", {"start": v(-1472.76, 2095.53) * mm, "end": v(-1333.06, 2095.53) * mm});
            skLineSegment(sketch, "E993.top", {"start": v(-1472.76, 2235.17) * mm, "end": v(-1333.06, 2235.17) * mm});
            skLineSegment(sketch, "E993.left", {"start": v(-1472.76, 2095.53) * mm, "end": v(-1472.76, 2235.17) * mm});
            skLineSegment(sketch, "E993.right", {"start": v(-1333.06, 2095.53) * mm, "end": v(-1333.06, 2235.17) * mm});
            skSolve(sketch);
        }
        {
            var Q0;
            Q0 = qSketchRegion(id + "F102", true);
            var Q1;
            Q1=makeQuery(id+"F97.opExtrude","SWEPT_FACE",FACE,{"disambiguationData":[OSD([sQuery(id+"F96.wireOp",EDGE,"E950")])]});
            extrude(context, id + "F103", {"entities" : qUnion([Q0]), "operationType" : NewBodyOperationType.ADD, "endBound" : BoundingType.UP_TO_SURFACE, "endBoundEntityFace" : qUnion([Q1]), "depth" : 25.4 * mm});
        }
        {
            var Q0;
            Q0=makeQuery(id+"F1.opExtrude","CAP_FACE",FACE,{"disambiguationData":[OSD([sQuery(id+"F0.wireOp",EDGE,"E13.7"),sQuery(id+"F0.wireOp",EDGE,"E55"),sQuery(id+"F0.wireOp",EDGE,"E57.trimOffspring"),sQuery(id+"F0.wireOp",EDGE,"E59"),sQuery(id+"F0.wireOp",EDGE,"E60.trimOffspring")])],"isStart":true});
            var sketch = newSketch(context, id + "F104", { "sketchPlane" : qUnion([Q0]) });
            skLineSegment(sketch, "E994", {"start": v(318.8, 318.8) * mm, "end": v(417.58, 220.02) * mm});
            skLineSegment(sketch, "E995", {"start": v(417.58, 220.02) * mm, "end": v(4346.74, 4149.17) * mm});
            skLineSegment(sketch, "E996", {"start": v(4346.74, 4149.17) * mm, "end": v(4247.95, 4247.95) * mm});
            skLineSegment(sketch, "E997", {"start": v(4247.95, 4247.95) * mm, "end": v(318.8, 318.8) * mm});
            skSolve(sketch);
        }
        {
            var Q0;
            Q0=makeQuery(id+"F104.imprint","IMPRINT",FACE,{"disambiguationData":[TD([[makeQuery(id+"F104.imprint","IMPRINT",EDGE,{"derivedFrom":sQuery(id+"F104.wireOp",EDGE,"E994")}),1.0]])]});
            var Q1;
            {var subQ1=sQuery(id+"F0.wireOp",EDGE,"E46.trimOffspring");var subQ4=sQuery(id+"F0.wireOp",EDGE,"E65");var subQ5=sQuery(id+"F0.wireOp",EDGE,"E45");var subQ6=sQuery(id+"F0.wireOp",EDGE,"E10");var subQ25=makeQuery(id+"F1.opExtrude","SWEPT_FACE",FACE,{"disambiguationData":[OSD([subQ5])]});Q1=makeQuery(id+"F65.boolean.opBoolean","SPLIT",FACE,{"disambiguationData":[TD([subQ25])],"derivedFrom":makeQuery(id+"F57.opExtrude","CAP_FACE",FACE,{"disambiguationData":[OSD([subQ6,subQ5,subQ1,subQ4])],"isStart":false})});}
            extrude(context, id + "F105", {"entities" : qUnion([Q0]), "operationType" : NewBodyOperationType.ADD, "endBound" : BoundingType.UP_TO_SURFACE, "endBoundEntityFace" : qUnion([Q1]), "depth" : 727.07 * mm});
        }
        {
            var Q0;
            Q0=makeQuery(id+"F1.opExtrude","CAP_FACE",FACE,{"disambiguationData":[OSD([sQuery(id+"F0.wireOp",EDGE,"E13.7"),sQuery(id+"F0.wireOp",EDGE,"E55"),sQuery(id+"F0.wireOp",EDGE,"E57.trimOffspring"),sQuery(id+"F0.wireOp",EDGE,"E59"),sQuery(id+"F0.wireOp",EDGE,"E60.trimOffspring")])],"isStart":false});
            var sketch = newSketch(context, id + "F106", { "sketchPlane" : qUnion([Q0]) });
            skLineSegment(sketch, "E998", {"start": v(345.74, -345.74) * mm, "end": v(444.52, -246.96) * mm});
            skLineSegment(sketch, "E999", {"start": v(444.52, -246.96) * mm, "end": v(4319.81, -4122.25) * mm});
            skLineSegment(sketch, "E1000", {"start": v(4319.81, -4122.25) * mm, "end": v(4221.03, -4221.03) * mm});
            skLineSegment(sketch, "E1001", {"start": v(4221.03, -4221.03) * mm, "end": v(345.74, -345.74) * mm});
            skSolve(sketch);
        }
        {
            var Q0;
            Q0=makeQuery(id+"F106.imprint","IMPRINT",FACE,{"disambiguationData":[TD([[makeQuery(id+"F106.imprint","IMPRINT",EDGE,{"derivedFrom":sQuery(id+"F106.wireOp",EDGE,"E998")}),-1.0]])]});
            var Q1;
            Q1=makeQuery(id+"F59.boolean.opBoolean","COPY",FACE,{"derivedFrom":makeQuery(id+"F59.opExtrude","CAP_FACE",FACE,{"disambiguationData":[OSD([sQuery(id+"F58.wireOp",EDGE,"E571"),sQuery(id+"F58.wireOp",EDGE,"E572"),sQuery(id+"F58.wireOp",EDGE,"E573"),sQuery(id+"F58.wireOp",EDGE,"E574")])],"isStart":false})});
            extrude(context, id + "F107", {"entities" : qUnion([Q0]), "operationType" : NewBodyOperationType.REMOVE, "endBound" : BoundingType.UP_TO_SURFACE, "oppositeDirection" : true, "endBoundEntityFace" : qUnion([Q1]), "depth" : 727.07 * mm});
        }
        {
            var Q0;
            Q0=makeQuery(id+"F1.opExtrude","CAP_FACE",FACE,{"disambiguationData":[OSD([sQuery(id+"F0.wireOp",EDGE,"E13.7"),sQuery(id+"F0.wireOp",EDGE,"E55"),sQuery(id+"F0.wireOp",EDGE,"E57.trimOffspring"),sQuery(id+"F0.wireOp",EDGE,"E59"),sQuery(id+"F0.wireOp",EDGE,"E60.trimOffspring")])],"isStart":false});
            var sketch = newSketch(context, id + "F108", { "sketchPlane" : qUnion([Q0]) });
            skLineSegment(sketch, "E1002", {"start": v(0, 0) * mm, "end": v(98.78, 98.78) * mm});
            skLineSegment(sketch, "E1003", {"start": v(98.78, 98.78) * mm, "end": v(125.72, 71.84) * mm});
            skLineSegment(sketch, "E1004", {"start": v(125.72, 71.84) * mm, "end": v(26.94, -26.94) * mm});
            skLineSegment(sketch, "E1005", {"start": v(26.94, -26.94) * mm, "end": v(0, 0) * mm});
            skLineSegment(sketch, "E1006", {"start": v(0, 139.7) * mm, "end": v(0, 0.04) * mm});
            skLineSegment(sketch, "E1007", {"start": v(0, 0.04) * mm, "end": v(38.1, 38.14) * mm});
            skLineSegment(sketch, "E1008", {"start": v(38.1, 38.14) * mm, "end": v(38.1, 139.7) * mm});
            skLineSegment(sketch, "E1009", {"start": v(38.1, 139.7) * mm, "end": v(0, 139.7) * mm});
            skLineSegment(sketch, "E1010", {"start": v(38.13, 139.7) * mm, "end": v(57.87, 139.7) * mm});
            skLineSegment(sketch, "E1011", {"start": v(57.87, 139.7) * mm, "end": v(98.76, 98.8) * mm});
            skLineSegment(sketch, "E1012", {"start": v(98.76, 98.8) * mm, "end": v(71.82, 71.86) * mm});
            skLineSegment(sketch, "E1013", {"start": v(38.13, 105.56) * mm, "end": v(38.13, 139.7) * mm});
            skLineSegment(sketch, "E1014", {"start": v(71.82, 71.86) * mm, "end": v(38.13, 105.56) * mm});
            skLineSegment(sketch, "E1015", {"start": v(4081.84, -4081.84) * mm, "end": v(4180.62, -3983.05) * mm});
            skLineSegment(sketch, "E1016", {"start": v(4180.62, -3983.05) * mm, "end": v(4153.68, -3956.11) * mm});
            skLineSegment(sketch, "E1017", {"start": v(4153.68, -3956.11) * mm, "end": v(4054.9, -4054.9) * mm});
            skLineSegment(sketch, "E1018", {"start": v(4054.9, -4054.9) * mm, "end": v(4081.84, -4081.84) * mm});
            skLineSegment(sketch, "E1019.1.0.0", {"start": v(3893.25, -3695.69) * mm, "end": v(3866.3, -3668.74) * mm});
            skLineSegment(sketch, "E1019.1.0.1", {"start": v(3794.47, -3794.47) * mm, "end": v(3893.25, -3695.69) * mm});
            skLineSegment(sketch, "E1019.1.0.2", {"start": v(3767.53, -3767.53) * mm, "end": v(3794.47, -3794.47) * mm});
            skLineSegment(sketch, "E1019.1.0.3", {"start": v(3866.3, -3668.74) * mm, "end": v(3767.53, -3767.53) * mm});
            skLineSegment(sketch, "E1019.2.0.0", {"start": v(3605.88, -3408.32) * mm, "end": v(3578.94, -3381.38) * mm});
            skLineSegment(sketch, "E1019.2.0.1", {"start": v(3507.1, -3507.1) * mm, "end": v(3605.88, -3408.32) * mm});
            skLineSegment(sketch, "E1019.2.0.2", {"start": v(3480.16, -3480.16) * mm, "end": v(3507.1, -3507.1) * mm});
            skLineSegment(sketch, "E1019.2.0.3", {"start": v(3578.94, -3381.38) * mm, "end": v(3480.16, -3480.16) * mm});
            skLineSegment(sketch, "E1019.3.0.0", {"start": v(3318.51, -3120.95) * mm, "end": v(3291.57, -3094) * mm});
            skLineSegment(sketch, "E1019.3.0.1", {"start": v(3219.73, -3219.73) * mm, "end": v(3318.51, -3120.95) * mm});
            skLineSegment(sketch, "E1019.3.0.2", {"start": v(3192.8, -3192.8) * mm, "end": v(3219.73, -3219.73) * mm});
            skLineSegment(sketch, "E1019.3.0.3", {"start": v(3291.57, -3094) * mm, "end": v(3192.8, -3192.8) * mm});
            skLineSegment(sketch, "E1019.4.0.0", {"start": v(3031.15, -2833.58) * mm, "end": v(3004.2, -2806.64) * mm});
            skLineSegment(sketch, "E1019.4.0.1", {"start": v(2932.36, -2932.36) * mm, "end": v(3031.15, -2833.58) * mm});
            skLineSegment(sketch, "E1019.4.0.2", {"start": v(2905.42, -2905.42) * mm, "end": v(2932.36, -2932.36) * mm});
            skLineSegment(sketch, "E1019.4.0.3", {"start": v(3004.2, -2806.64) * mm, "end": v(2905.42, -2905.42) * mm});
            skLineSegment(sketch, "E1019.5.0.0", {"start": v(2743.78, -2546.21) * mm, "end": v(2716.84, -2519.27) * mm});
            skLineSegment(sketch, "E1019.5.0.1", {"start": v(2645, -2645) * mm, "end": v(2743.78, -2546.21) * mm});
            skLineSegment(sketch, "E1019.5.0.2", {"start": v(2618.05, -2618.05) * mm, "end": v(2645, -2645) * mm});
            skLineSegment(sketch, "E1019.5.0.3", {"start": v(2716.84, -2519.27) * mm, "end": v(2618.05, -2618.05) * mm});
            skLineSegment(sketch, "E1019.6.0.0", {"start": v(2456.4, -2258.84) * mm, "end": v(2429.47, -2231.9) * mm});
            skLineSegment(sketch, "E1019.6.0.1", {"start": v(2357.63, -2357.63) * mm, "end": v(2456.4, -2258.84) * mm});
            skLineSegment(sketch, "E1019.6.0.2", {"start": v(2330.69, -2330.69) * mm, "end": v(2357.63, -2357.63) * mm});
            skLineSegment(sketch, "E1019.6.0.3", {"start": v(2429.47, -2231.9) * mm, "end": v(2330.69, -2330.69) * mm});
            skLineSegment(sketch, "E1019.7.0.0", {"start": v(2169.04, -1971.48) * mm, "end": v(2142.1, -1944.54) * mm});
            skLineSegment(sketch, "E1019.7.0.1", {"start": v(2070.26, -2070.26) * mm, "end": v(2169.04, -1971.48) * mm});
            skLineSegment(sketch, "E1019.7.0.2", {"start": v(2043.32, -2043.32) * mm, "end": v(2070.26, -2070.26) * mm});
            skLineSegment(sketch, "E1019.7.0.3", {"start": v(2142.1, -1944.54) * mm, "end": v(2043.32, -2043.32) * mm});
            skLineSegment(sketch, "E1019.8.0.0", {"start": v(1881.67, -1684.1) * mm, "end": v(1854.73, -1657.17) * mm});
            skLineSegment(sketch, "E1019.8.0.1", {"start": v(1782.9, -1782.9) * mm, "end": v(1881.67, -1684.1) * mm});
            skLineSegment(sketch, "E1019.8.0.2", {"start": v(1755.95, -1755.95) * mm, "end": v(1782.9, -1782.9) * mm});
            skLineSegment(sketch, "E1019.8.0.3", {"start": v(1854.73, -1657.17) * mm, "end": v(1755.95, -1755.95) * mm});
            skLineSegment(sketch, "E1019.9.0.0", {"start": v(1594.3, -1396.74) * mm, "end": v(1567.36, -1369.8) * mm});
            skLineSegment(sketch, "E1019.9.0.1", {"start": v(1495.52, -1495.52) * mm, "end": v(1594.3, -1396.74) * mm});
            skLineSegment(sketch, "E1019.9.0.2", {"start": v(1468.58, -1468.58) * mm, "end": v(1495.52, -1495.52) * mm});
            skLineSegment(sketch, "E1019.9.0.3", {"start": v(1567.36, -1369.8) * mm, "end": v(1468.58, -1468.58) * mm});
            skLineSegment(sketch, "E1019.10.0.0", {"start": v(1306.94, -1109.37) * mm, "end": v(1280, -1082.43) * mm});
            skLineSegment(sketch, "E1019.10.0.1", {"start": v(1208.15, -1208.15) * mm, "end": v(1306.94, -1109.37) * mm});
            skLineSegment(sketch, "E1019.10.0.2", {"start": v(1181.21, -1181.21) * mm, "end": v(1208.15, -1208.15) * mm});
            skLineSegment(sketch, "E1019.10.0.3", {"start": v(1280, -1082.43) * mm, "end": v(1181.21, -1181.21) * mm});
            skLineSegment(sketch, "E1019.11.0.0", {"start": v(1019.57, -822) * mm, "end": v(992.63, -795.06) * mm});
            skLineSegment(sketch, "E1019.11.0.1", {"start": v(920.79, -920.79) * mm, "end": v(1019.57, -822) * mm});
            skLineSegment(sketch, "E1019.11.0.2", {"start": v(893.85, -893.85) * mm, "end": v(920.79, -920.79) * mm});
            skLineSegment(sketch, "E1019.11.0.3", {"start": v(992.63, -795.06) * mm, "end": v(893.85, -893.85) * mm});
            skLineSegment(sketch, "E1019.12.0.0", {"start": v(732.2, -534.63) * mm, "end": v(705.26, -507.7) * mm});
            skLineSegment(sketch, "E1019.12.0.1", {"start": v(633.42, -633.42) * mm, "end": v(732.2, -534.63) * mm});
            skLineSegment(sketch, "E1019.12.0.2", {"start": v(606.48, -606.48) * mm, "end": v(633.42, -633.42) * mm});
            skLineSegment(sketch, "E1019.12.0.3", {"start": v(705.26, -507.7) * mm, "end": v(606.48, -606.48) * mm});
            skLineSegment(sketch, "E1019.direction1", {"start": v(4081.84, -4081.84) * mm, "end": v(3794.47, -3794.47) * mm, "construction": true});
            skLineSegment(sketch, "E1020.0.14.0", {"start": v(157.46, 40.1) * mm, "end": v(130.52, 67.04) * mm});
            skLineSegment(sketch, "E1020.3.14.0", {"start": v(58.68, -58.68) * mm, "end": v(157.46, 40.1) * mm});
            skLineSegment(sketch, "E1020.6.14.0", {"start": v(31.74, -31.74) * mm, "end": v(58.68, -58.68) * mm});
            skLineSegment(sketch, "E1020.9.14.0", {"start": v(130.52, 67.04) * mm, "end": v(31.74, -31.74) * mm});
            skLineSegment(sketch, "E1021", {"start": v(318.8, -318.8) * mm, "end": v(417.58, -220.02) * mm});
            skLineSegment(sketch, "E1022", {"start": v(417.58, -220.02) * mm, "end": v(444.52, -246.96) * mm});
            skLineSegment(sketch, "E1023", {"start": v(444.52, -246.96) * mm, "end": v(345.74, -345.74) * mm});
            skLineSegment(sketch, "E1024", {"start": v(345.74, -345.74) * mm, "end": v(318.8, -318.8) * mm});
            skLineSegment(sketch, "E1025", {"start": v(291.86, -291.86) * mm, "end": v(390.64, -193.08) * mm});
            skLineSegment(sketch, "E1026", {"start": v(390.64, -193.08) * mm, "end": v(417.56, -220) * mm});
            skLineSegment(sketch, "E1027", {"start": v(417.56, -220) * mm, "end": v(318.78, -318.78) * mm});
            skLineSegment(sketch, "E1028", {"start": v(318.78, -318.78) * mm, "end": v(291.86, -291.86) * mm});
            skSolve(sketch);
        }
        {
            var Q0;
            Q0=makeQuery(id+"F108.imprint","IMPRINT",FACE,{"disambiguationData":[TD([[makeQuery(id+"F108.imprint","IMPRINT",EDGE,{"derivedFrom":sQuery(id+"F108.wireOp",EDGE,"E1019.12.0.0")}),1.0]])]});
            var Q1;
            Q1=makeQuery(id+"F108.imprint","IMPRINT",FACE,{"disambiguationData":[TD([[makeQuery(id+"F108.imprint","IMPRINT",EDGE,{"derivedFrom":sQuery(id+"F108.wireOp",EDGE,"E1019.11.0.0")}),1.0]])]});
            var Q2;
            Q2=makeQuery(id+"F108.imprint","IMPRINT",FACE,{"disambiguationData":[TD([[makeQuery(id+"F108.imprint","IMPRINT",EDGE,{"derivedFrom":sQuery(id+"F108.wireOp",EDGE,"E1019.10.0.0")}),1.0]])]});
            var Q3;
            Q3=makeQuery(id+"F108.imprint","IMPRINT",FACE,{"disambiguationData":[TD([[makeQuery(id+"F108.imprint","IMPRINT",EDGE,{"derivedFrom":sQuery(id+"F108.wireOp",EDGE,"E1019.9.0.0")}),1.0]])]});
            var Q4;
            Q4=makeQuery(id+"F108.imprint","IMPRINT",FACE,{"disambiguationData":[TD([[makeQuery(id+"F108.imprint","IMPRINT",EDGE,{"derivedFrom":sQuery(id+"F108.wireOp",EDGE,"E1019.8.0.0")}),1.0]])]});
            var Q5;
            Q5=makeQuery(id+"F108.imprint","IMPRINT",FACE,{"disambiguationData":[TD([[makeQuery(id+"F108.imprint","IMPRINT",EDGE,{"derivedFrom":sQuery(id+"F108.wireOp",EDGE,"E1019.7.0.0")}),1.0]])]});
            var Q6;
            Q6=makeQuery(id+"F108.imprint","IMPRINT",FACE,{"disambiguationData":[TD([[makeQuery(id+"F108.imprint","IMPRINT",EDGE,{"derivedFrom":sQuery(id+"F108.wireOp",EDGE,"E1019.6.0.0")}),1.0]])]});
            var Q7;
            Q7=makeQuery(id+"F108.imprint","IMPRINT",FACE,{"disambiguationData":[TD([[makeQuery(id+"F108.imprint","IMPRINT",EDGE,{"derivedFrom":sQuery(id+"F108.wireOp",EDGE,"E1019.5.0.0")}),1.0]])]});
            var Q8;
            Q8=makeQuery(id+"F108.imprint","IMPRINT",FACE,{"disambiguationData":[TD([[makeQuery(id+"F108.imprint","IMPRINT",EDGE,{"derivedFrom":sQuery(id+"F108.wireOp",EDGE,"E1019.4.0.0")}),1.0]])]});
            var Q9;
            Q9=makeQuery(id+"F108.imprint","IMPRINT",FACE,{"disambiguationData":[TD([[makeQuery(id+"F108.imprint","IMPRINT",EDGE,{"derivedFrom":sQuery(id+"F108.wireOp",EDGE,"E1019.3.0.0")}),1.0]])]});
            var Q10;
            Q10=makeQuery(id+"F108.imprint","IMPRINT",FACE,{"disambiguationData":[TD([[makeQuery(id+"F108.imprint","IMPRINT",EDGE,{"derivedFrom":sQuery(id+"F108.wireOp",EDGE,"E1019.2.0.0")}),1.0]])]});
            var Q11;
            Q11=makeQuery(id+"F108.imprint","IMPRINT",FACE,{"disambiguationData":[TD([[makeQuery(id+"F108.imprint","IMPRINT",EDGE,{"derivedFrom":sQuery(id+"F108.wireOp",EDGE,"E1019.1.0.0")}),1.0]])]});
            var Q12;
            Q12=makeQuery(id+"F108.imprint","IMPRINT",FACE,{"disambiguationData":[TD([[makeQuery(id+"F108.imprint","IMPRINT",EDGE,{"derivedFrom":sQuery(id+"F108.wireOp",EDGE,"E1015")}),1.0]])]});
            var Q13;
            Q13=makeQuery(id+"F107.boolean.opBoolean","COPY",FACE,{"derivedFrom":makeQuery(id+"F107.opExtrude","CAP_FACE",FACE,{"disambiguationData":[OSD([sQuery(id+"F58.wireOp",EDGE,"E571"),sQuery(id+"F58.wireOp",EDGE,"E572"),sQuery(id+"F58.wireOp",EDGE,"E573"),sQuery(id+"F58.wireOp",EDGE,"E574")])],"isStart":false})});
            extrude(context, id + "F109", {"entities" : qUnion([Q0, Q1, Q2, Q3, Q4, Q5, Q6, Q7, Q8, Q9, Q10, Q11, Q12]), "operationType" : NewBodyOperationType.ADD, "endBound" : BoundingType.UP_TO_SURFACE, "oppositeDirection" : true, "endBoundEntityFace" : qUnion([Q13]), "depth" : 25.4 * mm});
        }
        {
            var Q0;
            Q0 = qSketchRegion(id + "F108", true);
            var Q1;
            {var subQ0=sQuery(id+"F0.wireOp",EDGE,"E59");Q1=makeQuery(id+"F108.imprint","IMPRINT",FACE,{"disambiguationData":[TD([[makeQuery(id+"F108.imprint","IMPRINT",EDGE,{"derivedFrom":makeQuery(id+"F1.opExtrude","CAP_EDGE",EDGE,{"disambiguationData":[OSD([subQ0])],"isStart":false})}),-1.0]])]});}
            var Q2;
            {var subQ0=sQuery(id+"F4.wireOp",EDGE,"E110.bottom");var subQ1=sQuery(id+"F4.wireOp",EDGE,"E110.top");Q2=makeQuery(id+"F5.boolean.opBoolean","SPLIT",FACE,{"disambiguationData":[TD([makeQuery(id+"F3.opExtrude","SWEPT_FACE",FACE,{"disambiguationData":[OSD([sQuery(id+"F2.wireOp",EDGE,"E78.right")])]})])],"derivedFrom":makeQuery(id+"F5.opExtrude","CAP_FACE",FACE,{"disambiguationData":[OSD([subQ0,subQ1,sQuery(id+"F4.wireOp",EDGE,"E110.left"),sQuery(id+"F4.wireOp",EDGE,"E111")])],"isStart":true})});}
            extrude(context, id + "F110", {"entities" : qUnion([Q0, Q1]), "operationType" : NewBodyOperationType.ADD, "endBound" : BoundingType.UP_TO_SURFACE, "endBoundEntityFace" : qUnion([Q2]), "depth" : 2809.88 * mm});
        }
        {
            var Q0;
            Q0=makeQuery(id+"F110.opExtrude","CAP_FACE",FACE,{"disambiguationData":[OSD([sQuery(id+"F0.wireOp",EDGE,"E13.7"),sQuery(id+"F0.wireOp",EDGE,"E59"),sQuery(id+"F0.wireOp",EDGE,"E60.trimOffspring"),sQuery(id+"F106.wireOp",EDGE,"E1000")])],"isStart":false});
            var sketch = newSketch(context, id + "F111", { "sketchPlane" : qUnion([Q0]) });
            skLineSegment(sketch, "E1029", {"start": v(4247.95, -4247.95) * mm, "end": v(0, 0) * mm});
            skLineSegment(sketch, "E1030", {"start": v(0, 0) * mm, "end": v(0, 139.7) * mm});
            skLineSegment(sketch, "E1031", {"start": v(0, 139.7) * mm, "end": v(57.87, 139.7) * mm});
            skLineSegment(sketch, "E1032", {"start": v(57.87, 139.7) * mm, "end": v(4346.74, -4149.17) * mm});
            skLineSegment(sketch, "E1033", {"start": v(4346.74, -4149.17) * mm, "end": v(4247.95, -4247.95) * mm});
            skSolve(sketch);
        }
        {
            var Q0;
            Q0 = qSketchRegion(id + "F111", true);
            extrude(context, id + "F112", {"entities" : qUnion([Q0]), "operationType" : NewBodyOperationType.ADD, "depth" : 76.2 * mm});
        }
        {
            var Q0;
            Q0=makeQuery(id+"F1.opExtrude","CAP_FACE",FACE,{"disambiguationData":[OSD([sQuery(id+"F0.wireOp",EDGE,"E13.9"),sQuery(id+"F0.wireOp",EDGE,"CZHSg9ks-ZAnK-oHyx-VIKY-kEaD2SOFmb6v"),sQuery(id+"F0.wireOp",EDGE,"E19"),sQuery(id+"F0.wireOp",EDGE,"E20.trimOffspring")])],"isStart":false});
            var sketch = newSketch(context, id + "F113", { "sketchPlane" : qUnion([Q0]) });
            skLineSegment(sketch, "E1034.bottom", {"start": v(-11277.6, 425.45) * mm, "end": v(-11137.9, 425.45) * mm});
            skLineSegment(sketch, "E1034.top", {"start": v(-11277.6, 387.35) * mm, "end": v(-11137.9, 387.35) * mm});
            skLineSegment(sketch, "E1034.left", {"start": v(-11277.6, 425.45) * mm, "end": v(-11277.6, 387.35) * mm});
            skLineSegment(sketch, "E1034.right", {"start": v(-11137.9, 425.45) * mm, "end": v(-11137.9, 387.35) * mm});
            skLineSegment(sketch, "E1035.0.1.0", {"start": v(-11277.6, 831.85) * mm, "end": v(-11137.9, 831.85) * mm});
            skLineSegment(sketch, "E1035.0.1.1", {"start": v(-11277.6, 793.75) * mm, "end": v(-11137.9, 793.75) * mm});
            skLineSegment(sketch, "E1035.0.1.2", {"start": v(-11137.9, 831.85) * mm, "end": v(-11137.9, 793.75) * mm});
            skLineSegment(sketch, "E1035.0.1.3", {"start": v(-11277.6, 831.85) * mm, "end": v(-11277.6, 793.75) * mm});
            skLineSegment(sketch, "E1035.direction1", {"start": v(-11277.6, 387.35) * mm, "end": v(-11257.56, 387.35) * mm, "construction": true});
            skLineSegment(sketch, "E1035.direction2", {"start": v(-11277.6, 387.35) * mm, "end": v(-11277.6, 793.75) * mm, "construction": true});
            skLineSegment(sketch, "E1036.0.0.2", {"start": v(-11277.6, 1238.25) * mm, "end": v(-11137.9, 1238.25) * mm});
            skLineSegment(sketch, "E1036.3.0.2", {"start": v(-11277.6, 1200.15) * mm, "end": v(-11137.9, 1200.15) * mm});
            skLineSegment(sketch, "E1036.6.0.2", {"start": v(-11137.9, 1238.25) * mm, "end": v(-11137.9, 1200.15) * mm});
            skLineSegment(sketch, "E1036.9.0.2", {"start": v(-11277.6, 1238.25) * mm, "end": v(-11277.6, 1200.15) * mm});
            skLineSegment(sketch, "E1036.0.0.3", {"start": v(-11277.6, 1644.65) * mm, "end": v(-11137.9, 1644.65) * mm});
            skLineSegment(sketch, "E1036.3.0.3", {"start": v(-11277.6, 1606.55) * mm, "end": v(-11137.9, 1606.55) * mm});
            skLineSegment(sketch, "E1036.6.0.3", {"start": v(-11137.9, 1644.65) * mm, "end": v(-11137.9, 1606.55) * mm});
            skLineSegment(sketch, "E1036.9.0.3", {"start": v(-11277.6, 1644.65) * mm, "end": v(-11277.6, 1606.55) * mm});
            skLineSegment(sketch, "E1036.0.0.4", {"start": v(-11277.6, 2051.05) * mm, "end": v(-11137.9, 2051.05) * mm});
            skLineSegment(sketch, "E1036.3.0.4", {"start": v(-11277.6, 2012.95) * mm, "end": v(-11137.9, 2012.95) * mm});
            skLineSegment(sketch, "E1036.6.0.4", {"start": v(-11137.9, 2051.05) * mm, "end": v(-11137.9, 2012.95) * mm});
            skLineSegment(sketch, "E1036.9.0.4", {"start": v(-11277.6, 2051.05) * mm, "end": v(-11277.6, 2012.95) * mm});
            skLineSegment(sketch, "E1036.0.0.5", {"start": v(-11277.6, 2457.45) * mm, "end": v(-11137.9, 2457.45) * mm});
            skLineSegment(sketch, "E1036.3.0.5", {"start": v(-11277.6, 2419.35) * mm, "end": v(-11137.9, 2419.35) * mm});
            skLineSegment(sketch, "E1036.6.0.5", {"start": v(-11137.9, 2457.45) * mm, "end": v(-11137.9, 2419.35) * mm});
            skLineSegment(sketch, "E1036.9.0.5", {"start": v(-11277.6, 2457.45) * mm, "end": v(-11277.6, 2419.35) * mm});
            skLineSegment(sketch, "E1037.0.0.6", {"start": v(-11277.6, 2863.85) * mm, "end": v(-11137.9, 2863.85) * mm});
            skLineSegment(sketch, "E1037.3.0.6", {"start": v(-11277.6, 2825.75) * mm, "end": v(-11137.9, 2825.75) * mm});
            skLineSegment(sketch, "E1037.6.0.6", {"start": v(-11137.9, 2863.85) * mm, "end": v(-11137.9, 2825.75) * mm});
            skLineSegment(sketch, "E1037.9.0.6", {"start": v(-11277.6, 2863.85) * mm, "end": v(-11277.6, 2825.75) * mm});
            skLineSegment(sketch, "E1037.0.0.7", {"start": v(-11277.6, 3270.25) * mm, "end": v(-11137.9, 3270.25) * mm});
            skLineSegment(sketch, "E1037.3.0.7", {"start": v(-11277.6, 3232.15) * mm, "end": v(-11137.9, 3232.15) * mm});
            skLineSegment(sketch, "E1037.6.0.7", {"start": v(-11137.9, 3270.25) * mm, "end": v(-11137.9, 3232.15) * mm});
            skLineSegment(sketch, "E1037.9.0.7", {"start": v(-11277.6, 3270.25) * mm, "end": v(-11277.6, 3232.15) * mm});
            skLineSegment(sketch, "E1037.0.0.8", {"start": v(-11277.6, 3676.65) * mm, "end": v(-11137.9, 3676.65) * mm});
            skLineSegment(sketch, "E1037.3.0.8", {"start": v(-11277.6, 3638.55) * mm, "end": v(-11137.9, 3638.55) * mm});
            skLineSegment(sketch, "E1037.6.0.8", {"start": v(-11137.9, 3676.65) * mm, "end": v(-11137.9, 3638.55) * mm});
            skLineSegment(sketch, "E1037.9.0.8", {"start": v(-11277.6, 3676.65) * mm, "end": v(-11277.6, 3638.55) * mm});
            skLineSegment(sketch, "E1037.0.0.9", {"start": v(-11277.6, 4083.05) * mm, "end": v(-11137.9, 4083.05) * mm});
            skLineSegment(sketch, "E1037.3.0.9", {"start": v(-11277.6, 4044.95) * mm, "end": v(-11137.9, 4044.95) * mm});
            skLineSegment(sketch, "E1037.6.0.9", {"start": v(-11137.9, 4083.05) * mm, "end": v(-11137.9, 4044.95) * mm});
            skLineSegment(sketch, "E1037.9.0.9", {"start": v(-11277.6, 4083.05) * mm, "end": v(-11277.6, 4044.95) * mm});
            skLineSegment(sketch, "E1038.0.0.10", {"start": v(-11277.6, 4489.45) * mm, "end": v(-11137.9, 4489.45) * mm});
            skLineSegment(sketch, "E1038.3.0.10", {"start": v(-11277.6, 4451.35) * mm, "end": v(-11137.9, 4451.35) * mm});
            skLineSegment(sketch, "E1038.6.0.10", {"start": v(-11137.9, 4489.45) * mm, "end": v(-11137.9, 4451.35) * mm});
            skLineSegment(sketch, "E1038.9.0.10", {"start": v(-11277.6, 4489.45) * mm, "end": v(-11277.6, 4451.35) * mm});
            skLineSegment(sketch, "E1039", {"start": v(-11277.6, 5080) * mm, "end": v(-11579, 5080) * mm, "construction": true});
            skLineSegment(sketch, "E1040", {"start": v(-11277.6, 4991.1) * mm, "end": v(-11596.28, 4991.1) * mm, "construction": true});
            skLineSegment(sketch, "E1041", {"start": v(-11137.9, 5080) * mm, "end": v(-10828.74, 5080) * mm, "construction": true});
            skLineSegment(sketch, "E1042", {"start": v(-11137.9, 5000.63) * mm, "end": v(-10780.33, 5000.63) * mm, "construction": true});
            skLineSegment(sketch, "E1043.bottom", {"start": v(-11277.6, 5080) * mm, "end": v(-11137.9, 5080) * mm});
            skLineSegment(sketch, "E1043.top", {"start": v(-11277.6, 5041.9) * mm, "end": v(-11137.9, 5041.9) * mm});
            skLineSegment(sketch, "E1043.left", {"start": v(-11277.6, 5080) * mm, "end": v(-11277.6, 5041.9) * mm});
            skLineSegment(sketch, "E1043.right", {"start": v(-11137.9, 5080) * mm, "end": v(-11137.9, 5041.9) * mm});
            skLineSegment(sketch, "E1044.bottom", {"start": v(-11277.6, 5038.73) * mm, "end": v(-11137.9, 5038.73) * mm});
            skLineSegment(sketch, "E1044.top", {"start": v(-11277.6, 5000.63) * mm, "end": v(-11137.9, 5000.63) * mm});
            skLineSegment(sketch, "E1044.left", {"start": v(-11277.6, 5038.73) * mm, "end": v(-11277.6, 5000.63) * mm});
            skLineSegment(sketch, "E1044.right", {"start": v(-11137.9, 5038.73) * mm, "end": v(-11137.9, 5000.63) * mm});
            skLineSegment(sketch, "E1045.bottom", {"start": v(-11277.6, 4962.53) * mm, "end": v(-11137.9, 4962.53) * mm});
            skLineSegment(sketch, "E1045.top", {"start": v(-11277.6, 5000.6) * mm, "end": v(-11137.9, 5000.6) * mm});
            skLineSegment(sketch, "E1045.left", {"start": v(-11277.6, 4962.53) * mm, "end": v(-11277.6, 5000.6) * mm});
            skLineSegment(sketch, "E1045.right", {"start": v(-11137.9, 4962.53) * mm, "end": v(-11137.9, 5000.6) * mm});
            skLineSegment(sketch, "E1046.0.0.11", {"start": v(-11277.6, 4895.85) * mm, "end": v(-11137.9, 4895.85) * mm});
            skLineSegment(sketch, "E1046.3.0.11", {"start": v(-11277.6, 4857.75) * mm, "end": v(-11137.9, 4857.75) * mm});
            skLineSegment(sketch, "E1046.6.0.11", {"start": v(-11137.9, 4895.85) * mm, "end": v(-11137.9, 4857.75) * mm});
            skLineSegment(sketch, "E1046.9.0.11", {"start": v(-11277.6, 4895.85) * mm, "end": v(-11277.6, 4857.75) * mm});
            skLineSegment(sketch, "E1047", {"start": v(-11277.6, 4886.33) * mm, "end": v(-11428.71, 4886.33) * mm, "construction": true});
            skLineSegment(sketch, "E1048.bottom", {"start": v(-11277.6, 1114.43) * mm, "end": v(-11137.9, 1114.43) * mm});
            skLineSegment(sketch, "E1048.top", {"start": v(-11277.6, 1152.53) * mm, "end": v(-11137.9, 1152.53) * mm});
            skLineSegment(sketch, "E1048.left", {"start": v(-11277.6, 1114.43) * mm, "end": v(-11277.6, 1152.53) * mm});
            skLineSegment(sketch, "E1048.right", {"start": v(-11137.9, 1114.43) * mm, "end": v(-11137.9, 1152.53) * mm});
            skLineSegment(sketch, "E1049", {"start": v(-11137.9, 1228.73) * mm, "end": v(-11277.6, 1228.73) * mm, "construction": true});
            skLineSegment(sketch, "E1050.bottom", {"start": v(-11277.6, 177.8) * mm, "end": v(-11137.9, 177.8) * mm});
            skLineSegment(sketch, "E1050.top", {"start": v(-11277.6, 139.73) * mm, "end": v(-11137.9, 139.73) * mm});
            skLineSegment(sketch, "E1050.left", {"start": v(-11277.6, 177.8) * mm, "end": v(-11277.6, 139.73) * mm});
            skLineSegment(sketch, "E1050.right", {"start": v(-11137.9, 177.8) * mm, "end": v(-11137.9, 139.73) * mm});
            skLineSegment(sketch, "E1051.bottom", {"start": v(-11277.6, 1114.4) * mm, "end": v(-11239.5, 1114.4) * mm});
            skLineSegment(sketch, "E1051.top", {"start": v(-11277.6, 1025.53) * mm, "end": v(-11239.5, 1025.53) * mm});
            skLineSegment(sketch, "E1051.left", {"start": v(-11277.6, 1114.4) * mm, "end": v(-11277.6, 1025.53) * mm});
            skLineSegment(sketch, "E1051.right", {"start": v(-11239.5, 1114.4) * mm, "end": v(-11239.5, 1025.53) * mm});
            skLineSegment(sketch, "E1052", {"start": v(-11137.9, 793.75) * mm, "end": v(-11061.7, 793.75) * mm, "construction": true});
            skLineSegment(sketch, "E1053", {"start": v(-11061.7, 793.75) * mm, "end": v(-11061.7, 1200.15) * mm, "construction": true});
            skLineSegment(sketch, "E1054", {"start": v(-11061.7, 1200.15) * mm, "end": v(-11131.55, 1200.15) * mm, "construction": true});
            skSolve(sketch);
        }
        {
            var Q0;
            Q0 = qSketchRegion(id + "F113", true);
            extrude(context, id + "F114", {"entities" : qUnion([Q0]), "operationType" : NewBodyOperationType.ADD, "depth" : 2387.6 * mm});
        }
        {
            var Q0;
            Q0=makeQuery(id+"F114.opExtrude","CAP_FACE",FACE,{"disambiguationData":[OSD([sQuery(id+"F113.wireOp",EDGE,"E1045.bottom"),sQuery(id+"F113.wireOp",EDGE,"E1045.top"),sQuery(id+"F113.wireOp",EDGE,"E1045.left"),sQuery(id+"F113.wireOp",EDGE,"E1045.right")])],"isStart":false});
            var sketch = newSketch(context, id + "F115", { "sketchPlane" : qUnion([Q0]) });
            skSolve(sketch);
        }
        {
            var Q0;
            Q0=makeQuery(id+"F115.imprint","IMPRINT",FACE,{"disambiguationData":[TD([[makeQuery(id+"F115.imprint","IMPRINT",EDGE,{"derivedFrom":makeQuery(id+"F114.opExtrude","CAP_EDGE",EDGE,{"disambiguationData":[OSD([sQuery(id+"F113.wireOp",EDGE,"E1045.bottom")])],"isStart":false})}),1.0]])]});
            var Q1;
            Q1=makeQuery(id+"F114.opExtrude","CAP_FACE",FACE,{"disambiguationData":[OSD([sQuery(id+"F113.wireOp",EDGE,"E1046.0.0.11"),sQuery(id+"F113.wireOp",EDGE,"E1046.3.0.11"),sQuery(id+"F113.wireOp",EDGE,"E1046.6.0.11"),sQuery(id+"F113.wireOp",EDGE,"E1046.9.0.11")])],"isStart":false});
            var Q2;
            Q2=makeQuery(id+"F114.opExtrude","CAP_FACE",FACE,{"disambiguationData":[OSD([sQuery(id+"F113.wireOp",EDGE,"E1038.0.0.10"),sQuery(id+"F113.wireOp",EDGE,"E1038.3.0.10"),sQuery(id+"F113.wireOp",EDGE,"E1038.6.0.10"),sQuery(id+"F113.wireOp",EDGE,"E1038.9.0.10")])],"isStart":false});
            var Q3;
            Q3=makeQuery(id+"F114.opExtrude","CAP_FACE",FACE,{"disambiguationData":[OSD([sQuery(id+"F113.wireOp",EDGE,"E1037.0.0.9"),sQuery(id+"F113.wireOp",EDGE,"E1037.3.0.9"),sQuery(id+"F113.wireOp",EDGE,"E1037.6.0.9"),sQuery(id+"F113.wireOp",EDGE,"E1037.9.0.9")])],"isStart":false});
            var Q4;
            Q4=makeQuery(id+"F114.opExtrude","CAP_FACE",FACE,{"disambiguationData":[OSD([sQuery(id+"F113.wireOp",EDGE,"E1037.0.0.8"),sQuery(id+"F113.wireOp",EDGE,"E1037.3.0.8"),sQuery(id+"F113.wireOp",EDGE,"E1037.6.0.8"),sQuery(id+"F113.wireOp",EDGE,"E1037.9.0.8")])],"isStart":false});
            var Q5;
            Q5=makeQuery(id+"F114.opExtrude","CAP_FACE",FACE,{"disambiguationData":[OSD([sQuery(id+"F113.wireOp",EDGE,"E1037.0.0.7"),sQuery(id+"F113.wireOp",EDGE,"E1037.3.0.7"),sQuery(id+"F113.wireOp",EDGE,"E1037.6.0.7"),sQuery(id+"F113.wireOp",EDGE,"E1037.9.0.7")])],"isStart":false});
            var Q6;
            Q6=makeQuery(id+"F114.opExtrude","CAP_FACE",FACE,{"disambiguationData":[OSD([sQuery(id+"F113.wireOp",EDGE,"E1037.0.0.6"),sQuery(id+"F113.wireOp",EDGE,"E1037.3.0.6"),sQuery(id+"F113.wireOp",EDGE,"E1037.6.0.6"),sQuery(id+"F113.wireOp",EDGE,"E1037.9.0.6")])],"isStart":false});
            var Q7;
            Q7=makeQuery(id+"F114.opExtrude","CAP_FACE",FACE,{"disambiguationData":[OSD([sQuery(id+"F113.wireOp",EDGE,"E1036.0.0.5"),sQuery(id+"F113.wireOp",EDGE,"E1036.3.0.5"),sQuery(id+"F113.wireOp",EDGE,"E1036.6.0.5"),sQuery(id+"F113.wireOp",EDGE,"E1036.9.0.5")])],"isStart":false});
            var Q8;
            Q8=makeQuery(id+"F114.opExtrude","CAP_FACE",FACE,{"disambiguationData":[OSD([sQuery(id+"F113.wireOp",EDGE,"E1036.0.0.4"),sQuery(id+"F113.wireOp",EDGE,"E1036.3.0.4"),sQuery(id+"F113.wireOp",EDGE,"E1036.6.0.4"),sQuery(id+"F113.wireOp",EDGE,"E1036.9.0.4")])],"isStart":false});
            var Q9;
            Q9=makeQuery(id+"F114.opExtrude","CAP_FACE",FACE,{"disambiguationData":[OSD([sQuery(id+"F113.wireOp",EDGE,"E1036.0.0.3"),sQuery(id+"F113.wireOp",EDGE,"E1036.3.0.3"),sQuery(id+"F113.wireOp",EDGE,"E1036.6.0.3"),sQuery(id+"F113.wireOp",EDGE,"E1036.9.0.3")])],"isStart":false});
            var Q10;
            Q10=makeQuery(id+"F114.opExtrude","CAP_FACE",FACE,{"disambiguationData":[OSD([sQuery(id+"F113.wireOp",EDGE,"E1050.bottom"),sQuery(id+"F113.wireOp",EDGE,"E1050.top"),sQuery(id+"F113.wireOp",EDGE,"E1050.left"),sQuery(id+"F113.wireOp",EDGE,"E1050.right")])],"isStart":false});
            var Q11;
            Q11=makeQuery(id+"F114.opExtrude","CAP_FACE",FACE,{"disambiguationData":[OSD([sQuery(id+"F113.wireOp",EDGE,"E1034.bottom"),sQuery(id+"F113.wireOp",EDGE,"E1034.top"),sQuery(id+"F113.wireOp",EDGE,"E1034.left"),sQuery(id+"F113.wireOp",EDGE,"E1034.right")])],"isStart":false});
            var Q12;
            Q12=makeQuery(id+"F114.opExtrude","CAP_FACE",FACE,{"disambiguationData":[OSD([sQuery(id+"F113.wireOp",EDGE,"E1035.0.1.0"),sQuery(id+"F113.wireOp",EDGE,"E1035.0.1.1"),sQuery(id+"F113.wireOp",EDGE,"E1035.0.1.2"),sQuery(id+"F113.wireOp",EDGE,"E1035.0.1.3")])],"isStart":false});
            var Q13;
            Q13=makeQuery(id+"F114.opExtrude","CAP_FACE",FACE,{"disambiguationData":[OSD([sQuery(id+"F113.wireOp",EDGE,"E1036.0.0.2"),sQuery(id+"F113.wireOp",EDGE,"E1036.3.0.2"),sQuery(id+"F113.wireOp",EDGE,"E1036.6.0.2"),sQuery(id+"F113.wireOp",EDGE,"E1036.9.0.2")])],"isStart":false});
            var Q14;
            Q14=makeQuery(id+"F114.opExtrude","CAP_FACE",FACE,{"disambiguationData":[OSD([sQuery(id+"F113.wireOp",EDGE,"E1048.bottom"),sQuery(id+"F113.wireOp",EDGE,"E1048.top"),sQuery(id+"F113.wireOp",EDGE,"E1048.left"),sQuery(id+"F113.wireOp",EDGE,"E1048.right")])],"isStart":false});
            var Q15;
            Q15=makeQuery(id+"F114.opExtrude","CAP_FACE",FACE,{"disambiguationData":[OSD([sQuery(id+"F113.wireOp",EDGE,"E1051.bottom"),sQuery(id+"F113.wireOp",EDGE,"E1051.top"),sQuery(id+"F113.wireOp",EDGE,"E1051.left"),sQuery(id+"F113.wireOp",EDGE,"E1051.right")])],"isStart":false});
            extrude(context, id + "F116", {"entities" : qUnion([Q0, Q1, Q2, Q3, Q4, Q5, Q6, Q7, Q8, Q9, Q10, Q11, Q12, Q13, Q14, Q15]), "operationType" : NewBodyOperationType.ADD, "depth" : 2752.72 * mm});
        }
        {
            var Q0;
            Q0=makeQuery(id+"F116.opExtrude","CAP_FACE",FACE,{"disambiguationData":[OSD([sQuery(id+"F113.wireOp",EDGE,"E1050.bottom"),sQuery(id+"F113.wireOp",EDGE,"E1050.top"),sQuery(id+"F113.wireOp",EDGE,"E1050.left"),sQuery(id+"F113.wireOp",EDGE,"E1050.right")])],"isStart":false});
            var sketch = newSketch(context, id + "F117", { "sketchPlane" : qUnion([Q0]) });
            skLineSegment(sketch, "E1055.bottom", {"start": v(-11277.6, 139.73) * mm, "end": v(-11137.9, 139.73) * mm});
            skLineSegment(sketch, "E1055.top", {"start": v(-11277.6, 5000.6) * mm, "end": v(-11137.9, 5000.6) * mm});
            skLineSegment(sketch, "E1055.left", {"start": v(-11277.6, 139.73) * mm, "end": v(-11277.6, 5000.6) * mm});
            skLineSegment(sketch, "E1055.right", {"start": v(-11137.9, 139.73) * mm, "end": v(-11137.9, 5000.6) * mm});
            skSolve(sketch);
        }
        {
            var Q0;
            Q0 = qSketchRegion(id + "F117", true);
            extrude(context, id + "F118", {"entities" : qUnion([Q0]), "operationType" : NewBodyOperationType.ADD, "depth" : 76.2 * mm});
        }
        {
            var Q0;
            {var subQ0=sQuery(id+"F113.wireOp",EDGE,"E1045.right");var subQ1=sQuery(id+"F113.wireOp",EDGE,"E1050.right");var subQ2=sQuery(id+"F113.wireOp",EDGE,"E1048.right");var subQ3=sQuery(id+"F113.wireOp",EDGE,"E1046.6.0.11");var subQ4=sQuery(id+"F113.wireOp",EDGE,"E1038.6.0.10");var subQ5=sQuery(id+"F113.wireOp",EDGE,"E1037.6.0.9");var subQ6=sQuery(id+"F113.wireOp",EDGE,"E1037.6.0.8");var subQ7=sQuery(id+"F113.wireOp",EDGE,"E1037.6.0.7");var subQ8=sQuery(id+"F113.wireOp",EDGE,"E1037.6.0.6");var subQ9=sQuery(id+"F113.wireOp",EDGE,"E1036.6.0.5");var subQ10=sQuery(id+"F113.wireOp",EDGE,"E1036.6.0.4");var subQ11=sQuery(id+"F113.wireOp",EDGE,"E1036.6.0.3");var subQ12=sQuery(id+"F113.wireOp",EDGE,"E1036.6.0.2");var subQ13=sQuery(id+"F113.wireOp",EDGE,"E1035.0.1.2");var subQ14=sQuery(id+"F113.wireOp",EDGE,"E1034.right");Q0=makeQuery(id+"F118.boolean.opBoolean","MERGE",FACE,{"derivedFrom":[makeQuery(id+"F116.boolean.opBoolean","MERGE",FACE,{"derivedFrom":[makeQuery(id+"F114.boolean.opBoolean","MERGE",FACE,{"derivedFrom":[makeQuery(id+"F1.opExtrude","SWEPT_FACE",FACE,{"disambiguationData":[OSD([sQuery(id+"F0.wireOp",EDGE,"E13.9")])]}),makeQuery(id+"F114.opExtrude","SWEPT_FACE",FACE,{"disambiguationData":[OSD([subQ14])]}),makeQuery(id+"F114.opExtrude","SWEPT_FACE",FACE,{"disambiguationData":[OSD([subQ13])]}),makeQuery(id+"F114.opExtrude","SWEPT_FACE",FACE,{"disambiguationData":[OSD([subQ12])]}),makeQuery(id+"F114.opExtrude","SWEPT_FACE",FACE,{"disambiguationData":[OSD([subQ11])]}),makeQuery(id+"F114.opExtrude","SWEPT_FACE",FACE,{"disambiguationData":[OSD([subQ10])]}),makeQuery(id+"F114.opExtrude","SWEPT_FACE",FACE,{"disambiguationData":[OSD([subQ9])]}),makeQuery(id+"F114.opExtrude","SWEPT_FACE",FACE,{"disambiguationData":[OSD([subQ8])]}),makeQuery(id+"F114.opExtrude","SWEPT_FACE",FACE,{"disambiguationData":[OSD([subQ7])]}),makeQuery(id+"F114.opExtrude","SWEPT_FACE",FACE,{"disambiguationData":[OSD([subQ6])]}),makeQuery(id+"F114.opExtrude","SWEPT_FACE",FACE,{"disambiguationData":[OSD([subQ5])]}),makeQuery(id+"F114.opExtrude","SWEPT_FACE",FACE,{"disambiguationData":[OSD([subQ4])]}),makeQuery(id+"F114.opExtrude","SWEPT_FACE",FACE,{"disambiguationData":[OSD([sQuery(id+"F113.wireOp",EDGE,"E1043.right")])]}),makeQuery(id+"F114.opExtrude","SWEPT_FACE",FACE,{"disambiguationData":[OSD([sQuery(id+"F113.wireOp",EDGE,"E1044.right")])]}),makeQuery(id+"F114.opExtrude","SWEPT_FACE",FACE,{"disambiguationData":[OSD([subQ0])]}),makeQuery(id+"F114.opExtrude","SWEPT_FACE",FACE,{"disambiguationData":[OSD([subQ3])]}),makeQuery(id+"F114.opExtrude","SWEPT_FACE",FACE,{"disambiguationData":[OSD([subQ2])]}),makeQuery(id+"F114.opExtrude","SWEPT_FACE",FACE,{"disambiguationData":[OSD([subQ1])]})]}),makeQuery(id+"F116.opExtrude","SWEPT_FACE",FACE,{"disambiguationData":[OSD([subQ14])]}),makeQuery(id+"F116.opExtrude","SWEPT_FACE",FACE,{"disambiguationData":[OSD([subQ13])]}),makeQuery(id+"F116.opExtrude","SWEPT_FACE",FACE,{"disambiguationData":[OSD([subQ12])]}),makeQuery(id+"F116.opExtrude","SWEPT_FACE",FACE,{"disambiguationData":[OSD([subQ11])]}),makeQuery(id+"F116.opExtrude","SWEPT_FACE",FACE,{"disambiguationData":[OSD([subQ10])]}),makeQuery(id+"F116.opExtrude","SWEPT_FACE",FACE,{"disambiguationData":[OSD([subQ9])]}),makeQuery(id+"F116.opExtrude","SWEPT_FACE",FACE,{"disambiguationData":[OSD([subQ8])]}),makeQuery(id+"F116.opExtrude","SWEPT_FACE",FACE,{"disambiguationData":[OSD([subQ7])]}),makeQuery(id+"F116.opExtrude","SWEPT_FACE",FACE,{"disambiguationData":[OSD([subQ6])]}),makeQuery(id+"F116.opExtrude","SWEPT_FACE",FACE,{"disambiguationData":[OSD([subQ5])]}),makeQuery(id+"F116.opExtrude","SWEPT_FACE",FACE,{"disambiguationData":[OSD([subQ4])]}),makeQuery(id+"F116.opExtrude","SWEPT_FACE",FACE,{"disambiguationData":[OSD([subQ3])]}),makeQuery(id+"F116.opExtrude","SWEPT_FACE",FACE,{"disambiguationData":[OSD([subQ2])]}),makeQuery(id+"F116.opExtrude","SWEPT_FACE",FACE,{"disambiguationData":[OSD([subQ1])]}),makeQuery(id+"F116.opExtrude","SWEPT_FACE",FACE,{"disambiguationData":[OSD([subQ0])]})]}),makeQuery(id+"F118.opExtrude","SWEPT_FACE",FACE,{"disambiguationData":[OSD([sQuery(id+"F117.wireOp",EDGE,"E1055.right")])]})]});}
            var sketch = newSketch(context, id + "F119", { "sketchPlane" : qUnion([Q0]) });
            skLineSegment(sketch, "E1056.bottom", {"start": v(1228.73, 0) * mm, "end": v(4886.33, 0) * mm});
            skLineSegment(sketch, "E1056.top", {"start": v(1152.53, 2432.05) * mm, "end": v(4962.53, 2432.05) * mm});
            skLineSegment(sketch, "E1056.left", {"start": v(1152.53, 38.1) * mm, "end": v(1152.53, 2432.05) * mm});
            skLineSegment(sketch, "E1056.right", {"start": v(4962.53, 38.1) * mm, "end": v(4962.53, 2432.05) * mm});
            skLineSegment(sketch, "E1057", {"start": v(1152.53, 38.1) * mm, "end": v(1228.73, 38.1) * mm});
            skLineSegment(sketch, "E1058", {"start": v(1228.73, 38.1) * mm, "end": v(1228.73, 0) * mm});
            skPoint(sketch, "E1059.orphan", {"position": v(1152.53, 0) * mm});
            skLineSegment(sketch, "E1060", {"start": v(4962.53, 38.1) * mm, "end": v(4886.33, 38.1) * mm});
            skLineSegment(sketch, "E1061", {"start": v(4886.33, 38.1) * mm, "end": v(4886.33, 0) * mm});
            skSolve(sketch);
        }
        {
            var Q0;
            Q0 = qSketchRegion(id + "F119", true);
            extrude(context, id + "F120", {"entities" : qUnion([Q0]), "operationType" : NewBodyOperationType.REMOVE, "oppositeDirection" : true, "depth" : 139.7 * mm});
        }
        {
            var Q0;
            {var subQ20=sQuery(id+"F0.wireOp",EDGE,"E13.9");var subQ24=sQuery(id+"F0.wireOp",EDGE,"E20.trimOffspring");var subQ39=makeQuery(id+"F1.opExtrude","CAP_FACE",FACE,{"disambiguationData":[OSD([subQ20,sQuery(id+"F0.wireOp",EDGE,"E19"),subQ24,sQuery(id+"F0.wireOp",EDGE,"E75")])],"isStart":false});Q0=makeQuery(id+"F120.boolean.opBoolean","MERGE",FACE,{"derivedFrom":[makeQuery(id+"F114.boolean.opBoolean","SPLIT",FACE,{"disambiguationData":[TD([makeQuery(id+"F114.opExtrude","SWEPT_FACE",FACE,{"disambiguationData":[OSD([sQuery(id+"F113.wireOp",EDGE,"E1036.0.0.2")])]})])],"derivedFrom":subQ39}),makeQuery(id+"F114.boolean.opBoolean","SPLIT",FACE,{"disambiguationData":[TD([makeQuery(id+"F114.opExtrude","SWEPT_FACE",FACE,{"disambiguationData":[OSD([sQuery(id+"F113.wireOp",EDGE,"E1036.3.0.2")])]})])],"derivedFrom":subQ39}),makeQuery(id+"F120.opExtrude","SWEPT_FACE",FACE,{"disambiguationData":[OSD([sQuery(id+"F119.wireOp",EDGE,"E1057")])]})]});}
            var sketch = newSketch(context, id + "F121", { "sketchPlane" : qUnion([Q0]) });
            skLineSegment(sketch, "E1062.bottom", {"start": v(-11137.9, 1228.73) * mm, "end": v(-11277.6, 1228.73) * mm});
            skLineSegment(sketch, "E1062.top", {"start": v(-11137.9, 1190.65) * mm, "end": v(-11277.6, 1190.65) * mm});
            skLineSegment(sketch, "E1062.left", {"start": v(-11137.9, 1228.73) * mm, "end": v(-11137.9, 1190.65) * mm});
            skLineSegment(sketch, "E1062.right", {"start": v(-11277.6, 1228.73) * mm, "end": v(-11277.6, 1190.65) * mm});
            skLineSegment(sketch, "E1063.bottom", {"start": v(-11137.9, 1190.63) * mm, "end": v(-11277.6, 1190.63) * mm});
            skLineSegment(sketch, "E1063.top", {"start": v(-11137.9, 1152.55) * mm, "end": v(-11277.6, 1152.55) * mm});
            skLineSegment(sketch, "E1063.left", {"start": v(-11137.9, 1190.63) * mm, "end": v(-11137.9, 1152.55) * mm});
            skLineSegment(sketch, "E1063.right", {"start": v(-11277.6, 1190.63) * mm, "end": v(-11277.6, 1152.55) * mm});
            skLineSegment(sketch, "E1064.bottom", {"start": v(-11137.9, 4886.33) * mm, "end": v(-11277.6, 4886.33) * mm});
            skLineSegment(sketch, "E1064.top", {"start": v(-11137.9, 4924.4) * mm, "end": v(-11277.6, 4924.4) * mm});
            skLineSegment(sketch, "E1064.left", {"start": v(-11137.9, 4886.33) * mm, "end": v(-11137.9, 4924.4) * mm});
            skLineSegment(sketch, "E1064.right", {"start": v(-11277.6, 4886.33) * mm, "end": v(-11277.6, 4924.4) * mm});
            skLineSegment(sketch, "E1065.bottom", {"start": v(-11277.6, 4924.43) * mm, "end": v(-11137.9, 4924.43) * mm});
            skLineSegment(sketch, "E1065.top", {"start": v(-11277.6, 4962.5) * mm, "end": v(-11137.9, 4962.5) * mm});
            skLineSegment(sketch, "E1065.left", {"start": v(-11277.6, 4924.43) * mm, "end": v(-11277.6, 4962.5) * mm});
            skLineSegment(sketch, "E1065.right", {"start": v(-11137.9, 4924.43) * mm, "end": v(-11137.9, 4962.5) * mm});
            skSolve(sketch);
        }
        {
            var Q0;
            Q0 = qSketchRegion(id + "F121", true);
            extrude(context, id + "F122", {"entities" : qUnion([Q0]), "operationType" : NewBodyOperationType.ADD, "depth" : 2108.2 * mm});
        }
        {
            var Q0;
            {var subQ0=sQuery(id+"F113.wireOp",EDGE,"E1045.bottom");Q0=makeQuery(id+"F116.boolean.opBoolean","MERGE",FACE,{"derivedFrom":[makeQuery(id+"F114.opExtrude","SWEPT_FACE",FACE,{"disambiguationData":[OSD([subQ0])]}),makeQuery(id+"F116.opExtrude","SWEPT_FACE",FACE,{"disambiguationData":[OSD([subQ0])]})]});}
            var sketch = newSketch(context, id + "F123", { "sketchPlane" : qUnion([Q0]) });
            skLineSegment(sketch, "E1066.bottom", {"start": v(-11277.6, 2146.33) * mm, "end": v(-11137.9, 2146.33) * mm});
            skLineSegment(sketch, "E1066.top", {"start": v(-11277.6, 2432.02) * mm, "end": v(-11137.9, 2432.02) * mm});
            skLineSegment(sketch, "E1066.left", {"start": v(-11277.6, 2146.33) * mm, "end": v(-11277.6, 2432.02) * mm});
            skLineSegment(sketch, "E1066.right", {"start": v(-11137.9, 2146.33) * mm, "end": v(-11137.9, 2432.02) * mm});
            skSolve(sketch);
        }
        {
            var Q0;
            Q0 = qSketchRegion(id + "F123", true);
            var Q1;
            {var subQ0=sQuery(id+"F113.wireOp",EDGE,"E1048.top");Q1=makeQuery(id+"F116.boolean.opBoolean","MERGE",FACE,{"derivedFrom":[makeQuery(id+"F114.opExtrude","SWEPT_FACE",FACE,{"disambiguationData":[OSD([subQ0])]}),makeQuery(id+"F116.opExtrude","SWEPT_FACE",FACE,{"disambiguationData":[OSD([subQ0])]})]});}
            extrude(context, id + "F124", {"entities" : qUnion([Q0]), "operationType" : NewBodyOperationType.ADD, "endBound" : BoundingType.UP_TO_SURFACE, "endBoundEntityFace" : qUnion([Q1]), "depth" : 25.4 * mm});
        }
        {
            var Q0;
            Q0=makeQuery(id+"F1.opExtrude","CAP_FACE",FACE,{"disambiguationData":[OSD([sQuery(id+"F0.wireOp",EDGE,"E13.10"),sQuery(id+"F0.wireOp",EDGE,"E37"),sQuery(id+"F0.wireOp",EDGE,"E38.trimOffspring"),sQuery(id+"F0.wireOp",EDGE,"E40")])],"isStart":false});
            var sketch = newSketch(context, id + "F125", { "sketchPlane" : qUnion([Q0]) });
            skLineSegment(sketch, "E1067.bottom", {"start": v(-11137.87, 9855.2) * mm, "end": v(-11099.8, 9855.2) * mm});
            skLineSegment(sketch, "E1067.top", {"start": v(-11137.87, 9715.5) * mm, "end": v(-11099.8, 9715.5) * mm});
            skLineSegment(sketch, "E1067.left", {"start": v(-11137.87, 9855.2) * mm, "end": v(-11137.87, 9715.5) * mm});
            skLineSegment(sketch, "E1067.right", {"start": v(-11099.8, 9855.2) * mm, "end": v(-11099.8, 9715.5) * mm});
            skLineSegment(sketch, "E1068.bottom", {"start": v(-1220.2, 9715.5) * mm, "end": v(-1258.28, 9715.5) * mm});
            skLineSegment(sketch, "E1068.top", {"start": v(-1220.2, 9855.2) * mm, "end": v(-1258.28, 9855.2) * mm});
            skLineSegment(sketch, "E1068.left", {"start": v(-1220.2, 9715.5) * mm, "end": v(-1220.2, 9855.2) * mm});
            skLineSegment(sketch, "E1068.right", {"start": v(-1258.28, 9715.5) * mm, "end": v(-1258.28, 9855.2) * mm});
            skLineSegment(sketch, "E1069.bottom", {"start": v(-10902.95, 9855.2) * mm, "end": v(-10864.85, 9855.2) * mm});
            skLineSegment(sketch, "E1069.top", {"start": v(-10902.95, 9715.5) * mm, "end": v(-10864.85, 9715.5) * mm});
            skLineSegment(sketch, "E1069.left", {"start": v(-10902.95, 9855.2) * mm, "end": v(-10902.95, 9715.5) * mm});
            skLineSegment(sketch, "E1069.right", {"start": v(-10864.85, 9855.2) * mm, "end": v(-10864.85, 9715.5) * mm});
            skLineSegment(sketch, "E1070.1.0.0", {"start": v(-10458.45, 9855.2) * mm, "end": v(-10458.45, 9715.5) * mm});
            skLineSegment(sketch, "E1070.1.0.1", {"start": v(-10496.55, 9855.2) * mm, "end": v(-10496.55, 9715.5) * mm});
            skLineSegment(sketch, "E1070.1.0.2", {"start": v(-10496.55, 9715.5) * mm, "end": v(-10458.45, 9715.5) * mm});
            skLineSegment(sketch, "E1070.1.0.3", {"start": v(-10496.55, 9855.2) * mm, "end": v(-10458.45, 9855.2) * mm});
            skLineSegment(sketch, "E1070.2.0.0", {"start": v(-10052.05, 9855.2) * mm, "end": v(-10052.05, 9715.5) * mm});
            skLineSegment(sketch, "E1070.2.0.1", {"start": v(-10090.15, 9855.2) * mm, "end": v(-10090.15, 9715.5) * mm});
            skLineSegment(sketch, "E1070.2.0.2", {"start": v(-10090.15, 9715.5) * mm, "end": v(-10052.05, 9715.5) * mm});
            skLineSegment(sketch, "E1070.2.0.3", {"start": v(-10090.15, 9855.2) * mm, "end": v(-10052.05, 9855.2) * mm});
            skLineSegment(sketch, "E1070.3.0.0", {"start": v(-9645.65, 9855.2) * mm, "end": v(-9645.65, 9715.5) * mm});
            skLineSegment(sketch, "E1070.3.0.1", {"start": v(-9683.75, 9855.2) * mm, "end": v(-9683.75, 9715.5) * mm});
            skLineSegment(sketch, "E1070.3.0.2", {"start": v(-9683.75, 9715.5) * mm, "end": v(-9645.65, 9715.5) * mm});
            skLineSegment(sketch, "E1070.3.0.3", {"start": v(-9683.75, 9855.2) * mm, "end": v(-9645.65, 9855.2) * mm});
            skLineSegment(sketch, "E1070.4.0.0", {"start": v(-9239.25, 9855.2) * mm, "end": v(-9239.25, 9715.5) * mm});
            skLineSegment(sketch, "E1070.4.0.1", {"start": v(-9277.35, 9855.2) * mm, "end": v(-9277.35, 9715.5) * mm});
            skLineSegment(sketch, "E1070.4.0.2", {"start": v(-9277.35, 9715.5) * mm, "end": v(-9239.25, 9715.5) * mm});
            skLineSegment(sketch, "E1070.4.0.3", {"start": v(-9277.35, 9855.2) * mm, "end": v(-9239.25, 9855.2) * mm});
            skLineSegment(sketch, "E1070.5.0.0", {"start": v(-8832.85, 9855.2) * mm, "end": v(-8832.85, 9715.5) * mm});
            skLineSegment(sketch, "E1070.5.0.1", {"start": v(-8870.95, 9855.2) * mm, "end": v(-8870.95, 9715.5) * mm});
            skLineSegment(sketch, "E1070.5.0.2", {"start": v(-8870.95, 9715.5) * mm, "end": v(-8832.85, 9715.5) * mm});
            skLineSegment(sketch, "E1070.5.0.3", {"start": v(-8870.95, 9855.2) * mm, "end": v(-8832.85, 9855.2) * mm});
            skLineSegment(sketch, "E1070.6.0.0", {"start": v(-8426.45, 9855.2) * mm, "end": v(-8426.45, 9715.5) * mm});
            skLineSegment(sketch, "E1070.6.0.1", {"start": v(-8464.55, 9855.2) * mm, "end": v(-8464.55, 9715.5) * mm});
            skLineSegment(sketch, "E1070.6.0.2", {"start": v(-8464.55, 9715.5) * mm, "end": v(-8426.45, 9715.5) * mm});
            skLineSegment(sketch, "E1070.6.0.3", {"start": v(-8464.55, 9855.2) * mm, "end": v(-8426.45, 9855.2) * mm});
            skLineSegment(sketch, "E1070.7.0.0", {"start": v(-8020.05, 9855.2) * mm, "end": v(-8020.05, 9715.5) * mm});
            skLineSegment(sketch, "E1070.7.0.1", {"start": v(-8058.15, 9855.2) * mm, "end": v(-8058.15, 9715.5) * mm});
            skLineSegment(sketch, "E1070.7.0.2", {"start": v(-8058.15, 9715.5) * mm, "end": v(-8020.05, 9715.5) * mm});
            skLineSegment(sketch, "E1070.7.0.3", {"start": v(-8058.15, 9855.2) * mm, "end": v(-8020.05, 9855.2) * mm});
            skLineSegment(sketch, "E1070.8.0.0", {"start": v(-7613.65, 9855.2) * mm, "end": v(-7613.65, 9715.5) * mm});
            skLineSegment(sketch, "E1070.8.0.1", {"start": v(-7651.75, 9855.2) * mm, "end": v(-7651.75, 9715.5) * mm});
            skLineSegment(sketch, "E1070.8.0.2", {"start": v(-7651.75, 9715.5) * mm, "end": v(-7613.65, 9715.5) * mm});
            skLineSegment(sketch, "E1070.8.0.3", {"start": v(-7651.75, 9855.2) * mm, "end": v(-7613.65, 9855.2) * mm});
            skLineSegment(sketch, "E1070.9.0.0", {"start": v(-7207.25, 9855.2) * mm, "end": v(-7207.25, 9715.5) * mm});
            skLineSegment(sketch, "E1070.9.0.1", {"start": v(-7245.35, 9855.2) * mm, "end": v(-7245.35, 9715.5) * mm});
            skLineSegment(sketch, "E1070.9.0.2", {"start": v(-7245.35, 9715.5) * mm, "end": v(-7207.25, 9715.5) * mm});
            skLineSegment(sketch, "E1070.9.0.3", {"start": v(-7245.35, 9855.2) * mm, "end": v(-7207.25, 9855.2) * mm});
            skLineSegment(sketch, "E1070.10.0.0", {"start": v(-6800.85, 9855.2) * mm, "end": v(-6800.85, 9715.5) * mm});
            skLineSegment(sketch, "E1070.10.0.1", {"start": v(-6838.95, 9855.2) * mm, "end": v(-6838.95, 9715.5) * mm});
            skLineSegment(sketch, "E1070.10.0.2", {"start": v(-6838.95, 9715.5) * mm, "end": v(-6800.85, 9715.5) * mm});
            skLineSegment(sketch, "E1070.10.0.3", {"start": v(-6838.95, 9855.2) * mm, "end": v(-6800.85, 9855.2) * mm});
            skLineSegment(sketch, "E1070.12.0.0", {"start": v(-5988.05, 9855.2) * mm, "end": v(-5988.05, 9715.5) * mm});
            skLineSegment(sketch, "E1070.12.0.1", {"start": v(-6026.15, 9855.2) * mm, "end": v(-6026.15, 9715.5) * mm});
            skLineSegment(sketch, "E1070.12.0.2", {"start": v(-6026.15, 9715.5) * mm, "end": v(-5988.05, 9715.5) * mm});
            skLineSegment(sketch, "E1070.12.0.3", {"start": v(-6026.15, 9855.2) * mm, "end": v(-5988.05, 9855.2) * mm});
            skLineSegment(sketch, "E1070.13.0.0", {"start": v(-5581.65, 9855.2) * mm, "end": v(-5581.65, 9715.5) * mm});
            skLineSegment(sketch, "E1070.13.0.1", {"start": v(-5619.75, 9855.2) * mm, "end": v(-5619.75, 9715.5) * mm});
            skLineSegment(sketch, "E1070.13.0.2", {"start": v(-5619.75, 9715.5) * mm, "end": v(-5581.65, 9715.5) * mm});
            skLineSegment(sketch, "E1070.13.0.3", {"start": v(-5619.75, 9855.2) * mm, "end": v(-5581.65, 9855.2) * mm});
            skLineSegment(sketch, "E1070.14.0.0", {"start": v(-5175.25, 9855.2) * mm, "end": v(-5175.25, 9715.5) * mm});
            skLineSegment(sketch, "E1070.14.0.1", {"start": v(-5213.35, 9855.2) * mm, "end": v(-5213.35, 9715.5) * mm});
            skLineSegment(sketch, "E1070.14.0.2", {"start": v(-5213.35, 9715.5) * mm, "end": v(-5175.25, 9715.5) * mm});
            skLineSegment(sketch, "E1070.14.0.3", {"start": v(-5213.35, 9855.2) * mm, "end": v(-5175.25, 9855.2) * mm});
            skLineSegment(sketch, "E1070.15.0.0", {"start": v(-4768.85, 9855.2) * mm, "end": v(-4768.85, 9715.5) * mm});
            skLineSegment(sketch, "E1070.15.0.1", {"start": v(-4806.95, 9855.2) * mm, "end": v(-4806.95, 9715.5) * mm});
            skLineSegment(sketch, "E1070.15.0.2", {"start": v(-4806.95, 9715.5) * mm, "end": v(-4768.85, 9715.5) * mm});
            skLineSegment(sketch, "E1070.15.0.3", {"start": v(-4806.95, 9855.2) * mm, "end": v(-4768.85, 9855.2) * mm});
            skLineSegment(sketch, "E1070.16.0.0", {"start": v(-4362.45, 9855.2) * mm, "end": v(-4362.45, 9715.5) * mm});
            skLineSegment(sketch, "E1070.16.0.1", {"start": v(-4400.55, 9855.2) * mm, "end": v(-4400.55, 9715.5) * mm});
            skLineSegment(sketch, "E1070.16.0.2", {"start": v(-4400.55, 9715.5) * mm, "end": v(-4362.45, 9715.5) * mm});
            skLineSegment(sketch, "E1070.16.0.3", {"start": v(-4400.55, 9855.2) * mm, "end": v(-4362.45, 9855.2) * mm});
            skLineSegment(sketch, "E1070.17.0.0", {"start": v(-3956.05, 9855.2) * mm, "end": v(-3956.05, 9715.5) * mm});
            skLineSegment(sketch, "E1070.17.0.1", {"start": v(-3994.15, 9855.2) * mm, "end": v(-3994.15, 9715.5) * mm});
            skLineSegment(sketch, "E1070.17.0.2", {"start": v(-3994.15, 9715.5) * mm, "end": v(-3956.05, 9715.5) * mm});
            skLineSegment(sketch, "E1070.17.0.3", {"start": v(-3994.15, 9855.2) * mm, "end": v(-3956.05, 9855.2) * mm});
            skLineSegment(sketch, "E1070.18.0.0", {"start": v(-3549.65, 9855.2) * mm, "end": v(-3549.65, 9715.5) * mm});
            skLineSegment(sketch, "E1070.18.0.1", {"start": v(-3587.75, 9855.2) * mm, "end": v(-3587.75, 9715.5) * mm});
            skLineSegment(sketch, "E1070.18.0.2", {"start": v(-3587.75, 9715.5) * mm, "end": v(-3549.65, 9715.5) * mm});
            skLineSegment(sketch, "E1070.18.0.3", {"start": v(-3587.75, 9855.2) * mm, "end": v(-3549.65, 9855.2) * mm});
            skLineSegment(sketch, "E1070.19.0.0", {"start": v(-3143.25, 9855.2) * mm, "end": v(-3143.25, 9715.5) * mm});
            skLineSegment(sketch, "E1070.19.0.1", {"start": v(-3181.35, 9855.2) * mm, "end": v(-3181.35, 9715.5) * mm});
            skLineSegment(sketch, "E1070.19.0.2", {"start": v(-3181.35, 9715.5) * mm, "end": v(-3143.25, 9715.5) * mm});
            skLineSegment(sketch, "E1070.19.0.3", {"start": v(-3181.35, 9855.2) * mm, "end": v(-3143.25, 9855.2) * mm});
            skLineSegment(sketch, "E1070.20.0.0", {"start": v(-2736.85, 9855.2) * mm, "end": v(-2736.85, 9715.5) * mm});
            skLineSegment(sketch, "E1070.20.0.1", {"start": v(-2774.95, 9855.2) * mm, "end": v(-2774.95, 9715.5) * mm});
            skLineSegment(sketch, "E1070.20.0.2", {"start": v(-2774.95, 9715.5) * mm, "end": v(-2736.85, 9715.5) * mm});
            skLineSegment(sketch, "E1070.20.0.3", {"start": v(-2774.95, 9855.2) * mm, "end": v(-2736.85, 9855.2) * mm});
            skLineSegment(sketch, "E1070.21.0.0", {"start": v(-2330.45, 9855.2) * mm, "end": v(-2330.45, 9715.5) * mm});
            skLineSegment(sketch, "E1070.21.0.1", {"start": v(-2368.55, 9855.2) * mm, "end": v(-2368.55, 9715.5) * mm});
            skLineSegment(sketch, "E1070.21.0.2", {"start": v(-2368.55, 9715.5) * mm, "end": v(-2330.45, 9715.5) * mm});
            skLineSegment(sketch, "E1070.21.0.3", {"start": v(-2368.55, 9855.2) * mm, "end": v(-2330.45, 9855.2) * mm});
            skLineSegment(sketch, "E1070.22.0.0", {"start": v(-1924.05, 9855.2) * mm, "end": v(-1924.05, 9715.5) * mm});
            skLineSegment(sketch, "E1070.22.0.1", {"start": v(-1962.15, 9855.2) * mm, "end": v(-1962.15, 9715.5) * mm});
            skLineSegment(sketch, "E1070.22.0.2", {"start": v(-1962.15, 9715.5) * mm, "end": v(-1924.05, 9715.5) * mm});
            skLineSegment(sketch, "E1070.22.0.3", {"start": v(-1962.15, 9855.2) * mm, "end": v(-1924.05, 9855.2) * mm});
            skLineSegment(sketch, "E1070.23.0.0", {"start": v(-1517.65, 9855.2) * mm, "end": v(-1517.65, 9715.5) * mm});
            skLineSegment(sketch, "E1070.23.0.1", {"start": v(-1555.75, 9855.2) * mm, "end": v(-1555.75, 9715.5) * mm});
            skLineSegment(sketch, "E1070.23.0.2", {"start": v(-1555.75, 9715.5) * mm, "end": v(-1517.65, 9715.5) * mm});
            skLineSegment(sketch, "E1070.23.0.3", {"start": v(-1555.75, 9855.2) * mm, "end": v(-1517.65, 9855.2) * mm});
            skLineSegment(sketch, "E1070.direction1", {"start": v(-10902.95, 9715.5) * mm, "end": v(-10496.55, 9715.5) * mm, "construction": true});
            skLineSegment(sketch, "E1071.bottom", {"start": v(-7486.65, 9855.2) * mm, "end": v(-7448.55, 9855.2) * mm});
            skLineSegment(sketch, "E1071.top", {"start": v(-7486.65, 9715.5) * mm, "end": v(-7448.55, 9715.5) * mm});
            skLineSegment(sketch, "E1071.left", {"start": v(-7486.65, 9855.2) * mm, "end": v(-7486.65, 9715.5) * mm});
            skLineSegment(sketch, "E1071.right", {"start": v(-7448.55, 9855.2) * mm, "end": v(-7448.55, 9715.5) * mm});
            skLineSegment(sketch, "E1072.bottom", {"start": v(-7524.75, 9855.2) * mm, "end": v(-7486.68, 9855.2) * mm});
            skLineSegment(sketch, "E1072.top", {"start": v(-7524.75, 9715.5) * mm, "end": v(-7486.68, 9715.5) * mm});
            skLineSegment(sketch, "E1072.left", {"start": v(-7524.75, 9855.2) * mm, "end": v(-7524.75, 9715.5) * mm});
            skLineSegment(sketch, "E1072.right", {"start": v(-7486.68, 9855.2) * mm, "end": v(-7486.68, 9715.5) * mm});
            skLineSegment(sketch, "E1073.bottom", {"start": v(-6470.65, 9855.2) * mm, "end": v(-6432.55, 9855.2) * mm});
            skLineSegment(sketch, "E1073.top", {"start": v(-6470.65, 9715.5) * mm, "end": v(-6432.55, 9715.5) * mm});
            skLineSegment(sketch, "E1073.left", {"start": v(-6470.65, 9855.2) * mm, "end": v(-6470.65, 9715.5) * mm});
            skLineSegment(sketch, "E1073.right", {"start": v(-6432.55, 9855.2) * mm, "end": v(-6432.55, 9715.5) * mm});
            skLineSegment(sketch, "E1074.bottom", {"start": v(-6432.52, 9855.2) * mm, "end": v(-6394.45, 9855.2) * mm});
            skLineSegment(sketch, "E1074.top", {"start": v(-6432.52, 9715.5) * mm, "end": v(-6394.45, 9715.5) * mm});
            skLineSegment(sketch, "E1074.left", {"start": v(-6432.52, 9855.2) * mm, "end": v(-6432.52, 9715.5) * mm});
            skLineSegment(sketch, "E1074.right", {"start": v(-6394.45, 9855.2) * mm, "end": v(-6394.45, 9715.5) * mm});
            skLineSegment(sketch, "E1075.bottom", {"start": v(-3763.94, 9855.2) * mm, "end": v(-3802.04, 9855.2) * mm});
            skLineSegment(sketch, "E1075.top", {"start": v(-3763.94, 9715.5) * mm, "end": v(-3802.04, 9715.5) * mm});
            skLineSegment(sketch, "E1075.left", {"start": v(-3763.94, 9855.2) * mm, "end": v(-3763.94, 9715.5) * mm});
            skLineSegment(sketch, "E1075.right", {"start": v(-3802.04, 9855.2) * mm, "end": v(-3802.04, 9715.5) * mm});
            skLineSegment(sketch, "E1076.bottom", {"start": v(-3840.14, 9855.2) * mm, "end": v(-3802.06, 9855.2) * mm});
            skLineSegment(sketch, "E1076.top", {"start": v(-3840.14, 9715.5) * mm, "end": v(-3802.06, 9715.5) * mm});
            skLineSegment(sketch, "E1076.left", {"start": v(-3840.14, 9855.2) * mm, "end": v(-3840.14, 9715.5) * mm});
            skLineSegment(sketch, "E1076.right", {"start": v(-3802.06, 9855.2) * mm, "end": v(-3802.06, 9715.5) * mm});
            skLineSegment(sketch, "E1077.bottom", {"start": v(-2544.74, 9855.2) * mm, "end": v(-2506.64, 9855.2) * mm});
            skLineSegment(sketch, "E1077.top", {"start": v(-2544.74, 9715.5) * mm, "end": v(-2506.64, 9715.5) * mm});
            skLineSegment(sketch, "E1077.left", {"start": v(-2544.74, 9855.2) * mm, "end": v(-2544.74, 9715.5) * mm});
            skLineSegment(sketch, "E1077.right", {"start": v(-2506.64, 9855.2) * mm, "end": v(-2506.64, 9715.5) * mm});
            skLineSegment(sketch, "E1078.bottom", {"start": v(-2506.61, 9855.2) * mm, "end": v(-2468.54, 9855.2) * mm});
            skLineSegment(sketch, "E1078.top", {"start": v(-2506.61, 9715.5) * mm, "end": v(-2468.54, 9715.5) * mm});
            skLineSegment(sketch, "E1078.left", {"start": v(-2506.61, 9855.2) * mm, "end": v(-2506.61, 9715.5) * mm});
            skLineSegment(sketch, "E1078.right", {"start": v(-2468.54, 9855.2) * mm, "end": v(-2468.54, 9715.5) * mm});
            skLineSegment(sketch, "E1079.bottom", {"start": v(-6356.35, 9715.5) * mm, "end": v(-6394.42, 9715.5) * mm});
            skLineSegment(sketch, "E1079.top", {"start": v(-6356.35, 9855.2) * mm, "end": v(-6394.42, 9855.2) * mm});
            skLineSegment(sketch, "E1079.left", {"start": v(-6356.35, 9715.5) * mm, "end": v(-6356.35, 9855.2) * mm});
            skLineSegment(sketch, "E1079.right", {"start": v(-6394.42, 9715.5) * mm, "end": v(-6394.42, 9855.2) * mm});
            skLineSegment(sketch, "E1080.bottom", {"start": v(-7524.78, 9715.5) * mm, "end": v(-7562.85, 9715.5) * mm});
            skLineSegment(sketch, "E1080.top", {"start": v(-7524.78, 9855.2) * mm, "end": v(-7562.85, 9855.2) * mm});
            skLineSegment(sketch, "E1080.left", {"start": v(-7524.78, 9715.5) * mm, "end": v(-7524.78, 9855.2) * mm});
            skLineSegment(sketch, "E1080.right", {"start": v(-7562.85, 9715.5) * mm, "end": v(-7562.85, 9855.2) * mm});
            skLineSegment(sketch, "E1081", {"start": v(-2544.74, 9715.5) * mm, "end": v(-3154.34, 9410.7) * mm, "construction": true});
            skLineSegment(sketch, "E1082", {"start": v(-3154.34, 9410.7) * mm, "end": v(-3763.94, 9715.5) * mm, "construction": true});
            skLineSegment(sketch, "E1083", {"start": v(-3154.34, 9410.7) * mm, "end": v(-3154.34, 9715.5) * mm, "construction": true});
            skLineSegment(sketch, "E1084.bottom", {"start": v(-2430.44, 9715.5) * mm, "end": v(-2468.51, 9715.5) * mm});
            skLineSegment(sketch, "E1084.top", {"start": v(-2430.44, 9855.2) * mm, "end": v(-2468.51, 9855.2) * mm});
            skLineSegment(sketch, "E1084.left", {"start": v(-2430.44, 9715.5) * mm, "end": v(-2430.44, 9855.2) * mm});
            skLineSegment(sketch, "E1084.right", {"start": v(-2468.51, 9715.5) * mm, "end": v(-2468.51, 9855.2) * mm});
            skLineSegment(sketch, "E1085.bottom", {"start": v(-3840.16, 9715.5) * mm, "end": v(-3878.24, 9715.5) * mm});
            skLineSegment(sketch, "E1085.top", {"start": v(-3840.16, 9855.2) * mm, "end": v(-3878.24, 9855.2) * mm});
            skLineSegment(sketch, "E1085.left", {"start": v(-3840.16, 9715.5) * mm, "end": v(-3840.16, 9855.2) * mm});
            skLineSegment(sketch, "E1085.right", {"start": v(-3878.24, 9715.5) * mm, "end": v(-3878.24, 9855.2) * mm});
            skSolve(sketch);
        }
        {
            var Q0;
            Q0 = qSketchRegion(id + "F125", true);
            extrude(context, id + "F126", {"entities" : qUnion([Q0]), "operationType" : NewBodyOperationType.ADD, "depth" : 2352.67 * mm});
        }
        {
            var Q0;
            Q0=makeQuery(id+"F126.opExtrude","CAP_FACE",FACE,{"disambiguationData":[OSD([sQuery(id+"F125.wireOp",EDGE,"E1067.bottom"),sQuery(id+"F125.wireOp",EDGE,"E1067.top"),sQuery(id+"F125.wireOp",EDGE,"E1067.left"),sQuery(id+"F125.wireOp",EDGE,"E1067.right")])],"isStart":false});
            var sketch = newSketch(context, id + "F127", { "sketchPlane" : qUnion([Q0]) });
            skLineSegment(sketch, "E1086.bottom", {"start": v(-11137.87, 9855.2) * mm, "end": v(-1220.2, 9855.2) * mm});
            skLineSegment(sketch, "E1086.top", {"start": v(-11137.87, 9715.5) * mm, "end": v(-1220.2, 9715.5) * mm});
            skLineSegment(sketch, "E1086.left", {"start": v(-11137.87, 9855.2) * mm, "end": v(-11137.87, 9715.5) * mm});
            skLineSegment(sketch, "E1086.right", {"start": v(-1220.2, 9855.2) * mm, "end": v(-1220.2, 9715.5) * mm});
            skSolve(sketch);
        }
        {
            var Q0;
            Q0 = qSketchRegion(id + "F127", true);
            extrude(context, id + "F128", {"entities" : qUnion([Q0]), "operationType" : NewBodyOperationType.ADD, "depth" : 76.2 * mm});
        }
        {
            var Q0;
            Q0=makeQuery(id+"F128.boolean.opBoolean","MERGE",FACE,{"derivedFrom":[makeQuery(id+"F126.boolean.opBoolean","MERGE",FACE,{"derivedFrom":[makeQuery(id+"F1.opExtrude","SWEPT_FACE",FACE,{"disambiguationData":[OSD([sQuery(id+"F0.wireOp",EDGE,"E38.trimOffspring")])]}),makeQuery(id+"F126.opExtrude","SWEPT_FACE",FACE,{"disambiguationData":[OSD([sQuery(id+"F125.wireOp",EDGE,"E1067.bottom")])]}),makeQuery(id+"F126.opExtrude","SWEPT_FACE",FACE,{"disambiguationData":[OSD([sQuery(id+"F125.wireOp",EDGE,"E1068.top")])]}),makeQuery(id+"F126.opExtrude","SWEPT_FACE",FACE,{"disambiguationData":[OSD([sQuery(id+"F125.wireOp",EDGE,"E1069.bottom")])]}),makeQuery(id+"F126.opExtrude","SWEPT_FACE",FACE,{"disambiguationData":[OSD([sQuery(id+"F125.wireOp",EDGE,"E1070.1.0.3")])]}),makeQuery(id+"F126.opExtrude","SWEPT_FACE",FACE,{"disambiguationData":[OSD([sQuery(id+"F125.wireOp",EDGE,"E1070.2.0.3")])]}),makeQuery(id+"F126.opExtrude","SWEPT_FACE",FACE,{"disambiguationData":[OSD([sQuery(id+"F125.wireOp",EDGE,"E1070.3.0.3")])]}),makeQuery(id+"F126.opExtrude","SWEPT_FACE",FACE,{"disambiguationData":[OSD([sQuery(id+"F125.wireOp",EDGE,"E1070.4.0.3")])]}),makeQuery(id+"F126.opExtrude","SWEPT_FACE",FACE,{"disambiguationData":[OSD([sQuery(id+"F125.wireOp",EDGE,"E1070.5.0.3")])]}),makeQuery(id+"F126.opExtrude","SWEPT_FACE",FACE,{"disambiguationData":[OSD([sQuery(id+"F125.wireOp",EDGE,"E1070.6.0.3")])]}),makeQuery(id+"F126.opExtrude","SWEPT_FACE",FACE,{"disambiguationData":[OSD([sQuery(id+"F125.wireOp",EDGE,"E1070.7.0.3")])]}),makeQuery(id+"F126.opExtrude","SWEPT_FACE",FACE,{"disambiguationData":[OSD([sQuery(id+"F125.wireOp",EDGE,"E1070.8.0.3")])]}),makeQuery(id+"F126.opExtrude","SWEPT_FACE",FACE,{"disambiguationData":[OSD([sQuery(id+"F125.wireOp",EDGE,"E1070.9.0.3")])]}),makeQuery(id+"F126.opExtrude","SWEPT_FACE",FACE,{"disambiguationData":[OSD([sQuery(id+"F125.wireOp",EDGE,"E1070.10.0.3")])]}),makeQuery(id+"F126.opExtrude","SWEPT_FACE",FACE,{"disambiguationData":[OSD([sQuery(id+"F125.wireOp",EDGE,"E1070.11.0.3")])]}),makeQuery(id+"F126.opExtrude","SWEPT_FACE",FACE,{"disambiguationData":[OSD([sQuery(id+"F125.wireOp",EDGE,"E1070.12.0.3")])]}),makeQuery(id+"F126.opExtrude","SWEPT_FACE",FACE,{"disambiguationData":[OSD([sQuery(id+"F125.wireOp",EDGE,"E1070.13.0.3")])]}),makeQuery(id+"F126.opExtrude","SWEPT_FACE",FACE,{"disambiguationData":[OSD([sQuery(id+"F125.wireOp",EDGE,"E1070.14.0.3")])]}),makeQuery(id+"F126.opExtrude","SWEPT_FACE",FACE,{"disambiguationData":[OSD([sQuery(id+"F125.wireOp",EDGE,"E1070.15.0.3")])]}),makeQuery(id+"F126.opExtrude","SWEPT_FACE",FACE,{"disambiguationData":[OSD([sQuery(id+"F125.wireOp",EDGE,"E1070.16.0.3")])]}),makeQuery(id+"F126.opExtrude","SWEPT_FACE",FACE,{"disambiguationData":[OSD([sQuery(id+"F125.wireOp",EDGE,"E1070.17.0.3")])]}),makeQuery(id+"F126.opExtrude","SWEPT_FACE",FACE,{"disambiguationData":[OSD([sQuery(id+"F125.wireOp",EDGE,"E1070.18.0.3")])]}),makeQuery(id+"F126.opExtrude","SWEPT_FACE",FACE,{"disambiguationData":[OSD([sQuery(id+"F125.wireOp",EDGE,"E1070.19.0.3")])]}),makeQuery(id+"F126.opExtrude","SWEPT_FACE",FACE,{"disambiguationData":[OSD([sQuery(id+"F125.wireOp",EDGE,"E1070.20.0.3")])]}),makeQuery(id+"F126.opExtrude","SWEPT_FACE",FACE,{"disambiguationData":[OSD([sQuery(id+"F125.wireOp",EDGE,"E1070.21.0.3")])]}),makeQuery(id+"F126.opExtrude","SWEPT_FACE",FACE,{"disambiguationData":[OSD([sQuery(id+"F125.wireOp",EDGE,"E1070.22.0.3")])]}),makeQuery(id+"F126.opExtrude","SWEPT_FACE",FACE,{"disambiguationData":[OSD([sQuery(id+"F125.wireOp",EDGE,"E1070.23.0.3")])]}),makeQuery(id+"F126.opExtrude","SWEPT_FACE",FACE,{"disambiguationData":[OSD([sQuery(id+"F125.wireOp",EDGE,"E1071.bottom")])]}),makeQuery(id+"F126.opExtrude","SWEPT_FACE",FACE,{"disambiguationData":[OSD([sQuery(id+"F125.wireOp",EDGE,"E1072.bottom")])]}),makeQuery(id+"F126.opExtrude","SWEPT_FACE",FACE,{"disambiguationData":[OSD([sQuery(id+"F125.wireOp",EDGE,"E1073.bottom")])]}),makeQuery(id+"F126.opExtrude","SWEPT_FACE",FACE,{"disambiguationData":[OSD([sQuery(id+"F125.wireOp",EDGE,"E1074.bottom")])]}),makeQuery(id+"F126.opExtrude","SWEPT_FACE",FACE,{"disambiguationData":[OSD([sQuery(id+"F125.wireOp",EDGE,"E1075.bottom")])]}),makeQuery(id+"F126.opExtrude","SWEPT_FACE",FACE,{"disambiguationData":[OSD([sQuery(id+"F125.wireOp",EDGE,"E1076.bottom")])]}),makeQuery(id+"F126.opExtrude","SWEPT_FACE",FACE,{"disambiguationData":[OSD([sQuery(id+"F125.wireOp",EDGE,"E1077.bottom")])]}),makeQuery(id+"F126.opExtrude","SWEPT_FACE",FACE,{"disambiguationData":[OSD([sQuery(id+"F125.wireOp",EDGE,"E1078.bottom")])]})]}),makeQuery(id+"F128.opExtrude","SWEPT_FACE",FACE,{"disambiguationData":[OSD([sQuery(id+"F127.wireOp",EDGE,"E1086.bottom")])]})]});
            var sketch = newSketch(context, id + "F129", { "sketchPlane" : qUnion([Q0]) });
            skLineSegment(sketch, "E1087", {"start": v(6394.45, 2235.2) * mm, "end": v(6394.45, 2095.5) * mm});
            skLineSegment(sketch, "E1088", {"start": v(6394.45, 2095.5) * mm, "end": v(6470.65, 2095.5) * mm});
            skLineSegment(sketch, "E1089", {"start": v(6470.65, 2095.5) * mm, "end": v(6470.65, 0) * mm});
            skLineSegment(sketch, "E1090", {"start": v(6470.65, 0) * mm, "end": v(7448.55, 0) * mm});
            skLineSegment(sketch, "E1091", {"start": v(7448.55, 0) * mm, "end": v(7448.55, 2095.5) * mm});
            skLineSegment(sketch, "E1092", {"start": v(7448.55, 2095.5) * mm, "end": v(7524.78, 2095.5) * mm});
            skLineSegment(sketch, "E1093", {"start": v(7524.78, 2095.5) * mm, "end": v(7524.78, 2390.78) * mm});
            skLineSegment(sketch, "E1094", {"start": v(7524.78, 2390.78) * mm, "end": v(7448.55, 2390.78) * mm});
            skLineSegment(sketch, "E1095", {"start": v(7448.55, 2390.78) * mm, "end": v(7448.55, 2235.2) * mm});
            skLineSegment(sketch, "E1096", {"start": v(7448.55, 2235.2) * mm, "end": v(6470.65, 2235.2) * mm});
            skLineSegment(sketch, "E1097", {"start": v(6470.65, 2235.2) * mm, "end": v(6470.65, 2390.78) * mm});
            skLineSegment(sketch, "E1098", {"start": v(6470.65, 2390.78) * mm, "end": v(6432.52, 2390.78) * mm});
            skLineSegment(sketch, "E1099", {"start": v(2468.51, 2390.78) * mm, "end": v(2468.51, 2095.5) * mm});
            skLineSegment(sketch, "E1100", {"start": v(2468.51, 2095.5) * mm, "end": v(2544.74, 2095.5) * mm});
            skLineSegment(sketch, "E1101", {"start": v(2544.74, 2095.5) * mm, "end": v(2544.74, 1028.7) * mm});
            skLineSegment(sketch, "E1102", {"start": v(2544.74, 1028.7) * mm, "end": v(3763.94, 1028.7) * mm});
            skLineSegment(sketch, "E1103", {"start": v(3763.94, 1028.7) * mm, "end": v(3763.94, 2095.5) * mm});
            skLineSegment(sketch, "E1104", {"start": v(3763.94, 2095.5) * mm, "end": v(3840.14, 2095.5) * mm});
            skLineSegment(sketch, "E1105", {"start": v(3840.14, 2095.5) * mm, "end": v(3840.14, 2390.78) * mm});
            skLineSegment(sketch, "E1106", {"start": v(3840.14, 2390.78) * mm, "end": v(3763.94, 2390.78) * mm});
            skLineSegment(sketch, "E1107", {"start": v(3763.94, 2390.78) * mm, "end": v(3763.94, 2235.2) * mm});
            skLineSegment(sketch, "E1108", {"start": v(3763.94, 2235.2) * mm, "end": v(2544.74, 2235.2) * mm});
            skLineSegment(sketch, "E1109", {"start": v(2544.74, 2235.2) * mm, "end": v(2544.74, 2390.78) * mm});
            skLineSegment(sketch, "E1110", {"start": v(2544.74, 2390.78) * mm, "end": v(2468.51, 2390.78) * mm});
            skLineSegment(sketch, "E1111", {"start": v(6394.42, 2235.2) * mm, "end": v(6432.52, 2235.2) * mm});
            skLineSegment(sketch, "E1112", {"start": v(6432.52, 2235.2) * mm, "end": v(6432.52, 2390.77) * mm});
            skSolve(sketch);
        }
        {
            var Q0;
            Q0 = qSketchRegion(id + "F129", true);
            extrude(context, id + "F130", {"entities" : qUnion([Q0]), "operationType" : NewBodyOperationType.REMOVE, "oppositeDirection" : true, "depth" : 139.7 * mm});
        }
        {
            var Q0;
            Q0=makeQuery(id+"F128.boolean.opBoolean","MERGE",FACE,{"derivedFrom":[makeQuery(id+"F126.boolean.opBoolean","MERGE",FACE,{"derivedFrom":[makeQuery(id+"F1.opExtrude","SWEPT_FACE",FACE,{"disambiguationData":[OSD([sQuery(id+"F0.wireOp",EDGE,"E38.trimOffspring")])]}),makeQuery(id+"F126.opExtrude","SWEPT_FACE",FACE,{"disambiguationData":[OSD([sQuery(id+"F125.wireOp",EDGE,"E1067.bottom")])]}),makeQuery(id+"F126.opExtrude","SWEPT_FACE",FACE,{"disambiguationData":[OSD([sQuery(id+"F125.wireOp",EDGE,"E1068.top")])]}),makeQuery(id+"F126.opExtrude","SWEPT_FACE",FACE,{"disambiguationData":[OSD([sQuery(id+"F125.wireOp",EDGE,"E1069.bottom")])]}),makeQuery(id+"F126.opExtrude","SWEPT_FACE",FACE,{"disambiguationData":[OSD([sQuery(id+"F125.wireOp",EDGE,"E1070.1.0.3")])]}),makeQuery(id+"F126.opExtrude","SWEPT_FACE",FACE,{"disambiguationData":[OSD([sQuery(id+"F125.wireOp",EDGE,"E1070.2.0.3")])]}),makeQuery(id+"F126.opExtrude","SWEPT_FACE",FACE,{"disambiguationData":[OSD([sQuery(id+"F125.wireOp",EDGE,"E1070.3.0.3")])]}),makeQuery(id+"F126.opExtrude","SWEPT_FACE",FACE,{"disambiguationData":[OSD([sQuery(id+"F125.wireOp",EDGE,"E1070.4.0.3")])]}),makeQuery(id+"F126.opExtrude","SWEPT_FACE",FACE,{"disambiguationData":[OSD([sQuery(id+"F125.wireOp",EDGE,"E1070.5.0.3")])]}),makeQuery(id+"F126.opExtrude","SWEPT_FACE",FACE,{"disambiguationData":[OSD([sQuery(id+"F125.wireOp",EDGE,"E1070.6.0.3")])]}),makeQuery(id+"F126.opExtrude","SWEPT_FACE",FACE,{"disambiguationData":[OSD([sQuery(id+"F125.wireOp",EDGE,"E1070.7.0.3")])]}),makeQuery(id+"F126.opExtrude","SWEPT_FACE",FACE,{"disambiguationData":[OSD([sQuery(id+"F125.wireOp",EDGE,"E1070.8.0.3")])]}),makeQuery(id+"F126.opExtrude","SWEPT_FACE",FACE,{"disambiguationData":[OSD([sQuery(id+"F125.wireOp",EDGE,"E1070.9.0.3")])]}),makeQuery(id+"F126.opExtrude","SWEPT_FACE",FACE,{"disambiguationData":[OSD([sQuery(id+"F125.wireOp",EDGE,"E1070.10.0.3")])]}),makeQuery(id+"F126.opExtrude","SWEPT_FACE",FACE,{"disambiguationData":[OSD([sQuery(id+"F125.wireOp",EDGE,"E1070.12.0.3")])]}),makeQuery(id+"F126.opExtrude","SWEPT_FACE",FACE,{"disambiguationData":[OSD([sQuery(id+"F125.wireOp",EDGE,"E1070.13.0.3")])]}),makeQuery(id+"F126.opExtrude","SWEPT_FACE",FACE,{"disambiguationData":[OSD([sQuery(id+"F125.wireOp",EDGE,"E1070.14.0.3")])]}),makeQuery(id+"F126.opExtrude","SWEPT_FACE",FACE,{"disambiguationData":[OSD([sQuery(id+"F125.wireOp",EDGE,"E1070.15.0.3")])]}),makeQuery(id+"F126.opExtrude","SWEPT_FACE",FACE,{"disambiguationData":[OSD([sQuery(id+"F125.wireOp",EDGE,"E1070.16.0.3")])]}),makeQuery(id+"F126.opExtrude","SWEPT_FACE",FACE,{"disambiguationData":[OSD([sQuery(id+"F125.wireOp",EDGE,"E1070.17.0.3")])]}),makeQuery(id+"F126.opExtrude","SWEPT_FACE",FACE,{"disambiguationData":[OSD([sQuery(id+"F125.wireOp",EDGE,"E1070.18.0.3")])]}),makeQuery(id+"F126.opExtrude","SWEPT_FACE",FACE,{"disambiguationData":[OSD([sQuery(id+"F125.wireOp",EDGE,"E1070.19.0.3")])]}),makeQuery(id+"F126.opExtrude","SWEPT_FACE",FACE,{"disambiguationData":[OSD([sQuery(id+"F125.wireOp",EDGE,"E1070.20.0.3")])]}),makeQuery(id+"F126.opExtrude","SWEPT_FACE",FACE,{"disambiguationData":[OSD([sQuery(id+"F125.wireOp",EDGE,"E1070.21.0.3")])]}),makeQuery(id+"F126.opExtrude","SWEPT_FACE",FACE,{"disambiguationData":[OSD([sQuery(id+"F125.wireOp",EDGE,"E1070.22.0.3")])]}),makeQuery(id+"F126.opExtrude","SWEPT_FACE",FACE,{"disambiguationData":[OSD([sQuery(id+"F125.wireOp",EDGE,"E1070.23.0.3")])]}),makeQuery(id+"F126.opExtrude","SWEPT_FACE",FACE,{"disambiguationData":[OSD([sQuery(id+"F125.wireOp",EDGE,"E1071.bottom")])]}),makeQuery(id+"F126.opExtrude","SWEPT_FACE",FACE,{"disambiguationData":[OSD([sQuery(id+"F125.wireOp",EDGE,"E1072.bottom")])]}),makeQuery(id+"F126.opExtrude","SWEPT_FACE",FACE,{"disambiguationData":[OSD([sQuery(id+"F125.wireOp",EDGE,"E1073.bottom")])]}),makeQuery(id+"F126.opExtrude","SWEPT_FACE",FACE,{"disambiguationData":[OSD([sQuery(id+"F125.wireOp",EDGE,"E1074.bottom")])]}),makeQuery(id+"F126.opExtrude","SWEPT_FACE",FACE,{"disambiguationData":[OSD([sQuery(id+"F125.wireOp",EDGE,"E1075.bottom")])]}),makeQuery(id+"F126.opExtrude","SWEPT_FACE",FACE,{"disambiguationData":[OSD([sQuery(id+"F125.wireOp",EDGE,"E1076.bottom")])]}),makeQuery(id+"F126.opExtrude","SWEPT_FACE",FACE,{"disambiguationData":[OSD([sQuery(id+"F125.wireOp",EDGE,"E1077.bottom")])]}),makeQuery(id+"F126.opExtrude","SWEPT_FACE",FACE,{"disambiguationData":[OSD([sQuery(id+"F125.wireOp",EDGE,"E1078.bottom")])]}),makeQuery(id+"F126.opExtrude","SWEPT_FACE",FACE,{"disambiguationData":[OSD([sQuery(id+"F125.wireOp",EDGE,"E1079.top")])]}),makeQuery(id+"F126.opExtrude","SWEPT_FACE",FACE,{"disambiguationData":[OSD([sQuery(id+"F125.wireOp",EDGE,"E1080.top")])]}),makeQuery(id+"F126.opExtrude","SWEPT_FACE",FACE,{"disambiguationData":[OSD([sQuery(id+"F125.wireOp",EDGE,"E1084.top")])]}),makeQuery(id+"F126.opExtrude","SWEPT_FACE",FACE,{"disambiguationData":[OSD([sQuery(id+"F125.wireOp",EDGE,"E1085.top")])]})]}),makeQuery(id+"F128.opExtrude","SWEPT_FACE",FACE,{"disambiguationData":[OSD([sQuery(id+"F127.wireOp",EDGE,"E1086.bottom")])]})]});
            var sketch = newSketch(context, id + "F131", { "sketchPlane" : qUnion([Q0]) });
            skLineSegment(sketch, "E1113.bottom", {"start": v(2468.51, 2095.53) * mm, "end": v(3840.16, 2095.53) * mm});
            skLineSegment(sketch, "E1113.top", {"start": v(2468.51, 2235.17) * mm, "end": v(3840.16, 2235.17) * mm});
            skLineSegment(sketch, "E1113.left", {"start": v(2468.51, 2095.53) * mm, "end": v(2468.51, 2235.17) * mm});
            skLineSegment(sketch, "E1113.right", {"start": v(3840.16, 2095.53) * mm, "end": v(3840.16, 2235.17) * mm});
            skLineSegment(sketch, "E1114.bottom", {"start": v(2544.74, 990.6) * mm, "end": v(3763.94, 990.6) * mm});
            skLineSegment(sketch, "E1114.top", {"start": v(2544.74, 1028.7) * mm, "end": v(3763.94, 1028.7) * mm});
            skLineSegment(sketch, "E1114.left", {"start": v(2544.74, 990.6) * mm, "end": v(2544.74, 1028.7) * mm});
            skLineSegment(sketch, "E1114.right", {"start": v(3763.94, 990.6) * mm, "end": v(3763.94, 1028.7) * mm});
            skLineSegment(sketch, "E1115.bottom", {"start": v(7524.78, 2095.53) * mm, "end": v(6394.42, 2095.53) * mm});
            skLineSegment(sketch, "E1115.top", {"start": v(7524.78, 2235.17) * mm, "end": v(6394.42, 2235.17) * mm});
            skLineSegment(sketch, "E1115.left", {"start": v(7524.78, 2095.53) * mm, "end": v(7524.78, 2235.17) * mm});
            skLineSegment(sketch, "E1115.right", {"start": v(6394.42, 2095.53) * mm, "end": v(6394.42, 2235.17) * mm});
            skSolve(sketch);
        }
        {
            var Q0;
            Q0 = qSketchRegion(id + "F131", true);
            extrude(context, id + "F132", {"entities" : qUnion([Q0]), "operationType" : NewBodyOperationType.ADD, "oppositeDirection" : true, "depth" : 139.7 * mm});
        }
        {
            var Q0;
            Q0=makeQuery(id+"F1.opExtrude","CAP_FACE",FACE,{"disambiguationData":[OSD([sQuery(id+"F0.wireOp",EDGE,"E13.13"),sQuery(id+"F0.wireOp",EDGE,"E25"),sQuery(id+"F0.wireOp",EDGE,"E26.trimOffspring"),sQuery(id+"F0.wireOp",EDGE,"E28")])],"isStart":false});
            var sketch = newSketch(context, id + "F133", { "sketchPlane" : qUnion([Q0]) });
            skLineSegment(sketch, "E1116.bottom", {"start": v(-15087.6, 5428.5) * mm, "end": v(-14947.9, 5428.5) * mm});
            skLineSegment(sketch, "E1116.top", {"start": v(-15087.6, 5390.43) * mm, "end": v(-14947.9, 5390.43) * mm});
            skLineSegment(sketch, "E1116.left", {"start": v(-15087.6, 5428.5) * mm, "end": v(-15087.6, 5390.43) * mm});
            skLineSegment(sketch, "E1116.right", {"start": v(-14947.9, 5428.5) * mm, "end": v(-14947.9, 5390.43) * mm});
            skLineSegment(sketch, "E1117.bottom", {"start": v(-15087.6, 2343.9) * mm, "end": v(-14947.9, 2343.9) * mm});
            skLineSegment(sketch, "E1117.top", {"start": v(-15087.6, 2381.97) * mm, "end": v(-14947.9, 2381.97) * mm});
            skLineSegment(sketch, "E1117.left", {"start": v(-15087.6, 2343.9) * mm, "end": v(-15087.6, 2381.97) * mm});
            skLineSegment(sketch, "E1117.right", {"start": v(-14947.9, 2343.9) * mm, "end": v(-14947.9, 2381.97) * mm});
            skLineSegment(sketch, "E1118.bottom", {"start": v(-15087.6, 2706.19) * mm, "end": v(-14947.9, 2706.19) * mm});
            skLineSegment(sketch, "E1118.top", {"start": v(-15087.6, 2668.09) * mm, "end": v(-14947.9, 2668.09) * mm});
            skLineSegment(sketch, "E1118.left", {"start": v(-15087.6, 2706.19) * mm, "end": v(-15087.6, 2668.09) * mm});
            skLineSegment(sketch, "E1118.right", {"start": v(-14947.9, 2706.19) * mm, "end": v(-14947.9, 2668.09) * mm});
            skLineSegment(sketch, "E1119", {"start": v(-15087.6, 2343.9) * mm, "end": v(-15087.6, 2280.74) * mm, "construction": true});
            skLineSegment(sketch, "E1120", {"start": v(-15087.6, 2280.74) * mm, "end": v(-15100.3, 2280.74) * mm, "construction": true});
            skLineSegment(sketch, "E1121", {"start": v(-15100.3, 2280.74) * mm, "end": v(-15100.3, 2404.54) * mm, "construction": true});
            skLineSegment(sketch, "E1122", {"start": v(-14999.43, 2197.83) * mm, "end": v(-15084.97, 2283.37) * mm, "construction": true});
            skLineSegment(sketch, "E1123", {"start": v(-15084.97, 2283.37) * mm, "end": v(-15093.95, 2274.39) * mm, "construction": true});
            skLineSegment(sketch, "E1124", {"start": v(-15093.95, 2274.39) * mm, "end": v(-15028.04, 2208.48) * mm, "construction": true});
            skLineSegment(sketch, "E1125.0.1.0", {"start": v(-15087.6, 3112.59) * mm, "end": v(-14947.9, 3112.59) * mm});
            skLineSegment(sketch, "E1125.0.1.1", {"start": v(-15087.6, 3074.49) * mm, "end": v(-14947.9, 3074.49) * mm});
            skLineSegment(sketch, "E1125.0.1.2", {"start": v(-15087.6, 3112.59) * mm, "end": v(-15087.6, 3074.49) * mm});
            skLineSegment(sketch, "E1125.0.1.3", {"start": v(-14947.9, 3112.59) * mm, "end": v(-14947.9, 3074.49) * mm});
            skLineSegment(sketch, "E1125.0.2.0", {"start": v(-15087.6, 3518.99) * mm, "end": v(-14947.9, 3518.99) * mm});
            skLineSegment(sketch, "E1125.0.2.1", {"start": v(-15087.6, 3480.89) * mm, "end": v(-14947.9, 3480.89) * mm});
            skLineSegment(sketch, "E1125.0.2.2", {"start": v(-15087.6, 3518.99) * mm, "end": v(-15087.6, 3480.89) * mm});
            skLineSegment(sketch, "E1125.0.2.3", {"start": v(-14947.9, 3518.99) * mm, "end": v(-14947.9, 3480.89) * mm});
            skLineSegment(sketch, "E1125.0.3.0", {"start": v(-15087.6, 3925.39) * mm, "end": v(-14947.9, 3925.39) * mm});
            skLineSegment(sketch, "E1125.0.3.1", {"start": v(-15087.6, 3887.29) * mm, "end": v(-14947.9, 3887.29) * mm});
            skLineSegment(sketch, "E1125.0.3.2", {"start": v(-15087.6, 3925.39) * mm, "end": v(-15087.6, 3887.29) * mm});
            skLineSegment(sketch, "E1125.0.3.3", {"start": v(-14947.9, 3925.39) * mm, "end": v(-14947.9, 3887.29) * mm});
            skLineSegment(sketch, "E1125.0.4.0", {"start": v(-15087.6, 4331.79) * mm, "end": v(-14947.9, 4331.79) * mm});
            skLineSegment(sketch, "E1125.0.4.1", {"start": v(-15087.6, 4293.69) * mm, "end": v(-14947.9, 4293.69) * mm});
            skLineSegment(sketch, "E1125.0.4.2", {"start": v(-15087.6, 4331.79) * mm, "end": v(-15087.6, 4293.69) * mm});
            skLineSegment(sketch, "E1125.0.4.3", {"start": v(-14947.9, 4331.79) * mm, "end": v(-14947.9, 4293.69) * mm});
            skLineSegment(sketch, "E1125.0.5.0", {"start": v(-15087.6, 4738.19) * mm, "end": v(-14947.9, 4738.19) * mm});
            skLineSegment(sketch, "E1125.0.5.1", {"start": v(-15087.6, 4700.09) * mm, "end": v(-14947.9, 4700.09) * mm});
            skLineSegment(sketch, "E1125.0.5.2", {"start": v(-15087.6, 4738.19) * mm, "end": v(-15087.6, 4700.09) * mm});
            skLineSegment(sketch, "E1125.0.5.3", {"start": v(-14947.9, 4738.19) * mm, "end": v(-14947.9, 4700.09) * mm});
            skLineSegment(sketch, "E1125.0.6.0", {"start": v(-15087.6, 5144.59) * mm, "end": v(-14947.9, 5144.59) * mm});
            skLineSegment(sketch, "E1125.0.6.1", {"start": v(-15087.6, 5106.49) * mm, "end": v(-14947.9, 5106.49) * mm});
            skLineSegment(sketch, "E1125.0.6.2", {"start": v(-15087.6, 5144.59) * mm, "end": v(-15087.6, 5106.49) * mm});
            skLineSegment(sketch, "E1125.0.6.3", {"start": v(-14947.9, 5144.59) * mm, "end": v(-14947.9, 5106.49) * mm});
            skLineSegment(sketch, "E1125.direction1", {"start": v(-15087.6, 2668.09) * mm, "end": v(-15062.2, 2668.09) * mm, "construction": true});
            skLineSegment(sketch, "E1125.direction2", {"start": v(-15087.6, 2668.09) * mm, "end": v(-15087.6, 3074.49) * mm, "construction": true});
            skSolve(sketch);
        }
        {
            var Q0;
            Q0 = qSketchRegion(id + "F133", true);
            extrude(context, id + "F134", {"entities" : qUnion([Q0]), "operationType" : NewBodyOperationType.ADD, "depth" : 2352.67 * mm});
        }
        {
            var Q0;
            Q0=makeQuery(id+"F134.opExtrude","CAP_FACE",FACE,{"disambiguationData":[OSD([sQuery(id+"F133.wireOp",EDGE,"E1116.bottom"),sQuery(id+"F133.wireOp",EDGE,"E1116.top"),sQuery(id+"F133.wireOp",EDGE,"E1116.left"),sQuery(id+"F133.wireOp",EDGE,"E1116.right")])],"isStart":false});
            var sketch = newSketch(context, id + "F135", { "sketchPlane" : qUnion([Q0]) });
            skLineSegment(sketch, "E1126.bottom", {"start": v(-15087.6, 5428.5) * mm, "end": v(-14947.9, 5428.5) * mm});
            skLineSegment(sketch, "E1126.top", {"start": v(-15087.6, 2343.9) * mm, "end": v(-14947.9, 2343.9) * mm});
            skLineSegment(sketch, "E1126.left", {"start": v(-15087.6, 5428.5) * mm, "end": v(-15087.6, 2343.9) * mm});
            skLineSegment(sketch, "E1126.right", {"start": v(-14947.9, 5428.5) * mm, "end": v(-14947.9, 2343.9) * mm});
            skSolve(sketch);
        }
        {
            var Q0;
            Q0 = qSketchRegion(id + "F135", true);
            extrude(context, id + "F136", {"entities" : qUnion([Q0]), "operationType" : NewBodyOperationType.ADD, "depth" : 76.2 * mm});
        }
        {
            var Q0;
            Q0=makeQuery(id+"F1.opExtrude","CAP_FACE",FACE,{"disambiguationData":[OSD([sQuery(id+"F0.wireOp",EDGE,"E14"),sQuery(id+"F0.wireOp",EDGE,"E17.2"),sQuery(id+"F0.wireOp",EDGE,"E51"),sQuery(id+"F0.wireOp",EDGE,"E54")])],"isStart":false});
            var sketch = newSketch(context, id + "F137", { "sketchPlane" : qUnion([Q0]) });
            skLineSegment(sketch, "E1127.bottom", {"start": v(57.87, 139.73) * mm, "end": v(-81.83, 139.73) * mm});
            skLineSegment(sketch, "E1127.top", {"start": v(57.87, 177.8) * mm, "end": v(-81.83, 177.8) * mm});
            skLineSegment(sketch, "E1127.left", {"start": v(57.87, 139.73) * mm, "end": v(57.87, 177.8) * mm});
            skLineSegment(sketch, "E1127.right", {"start": v(-81.83, 139.73) * mm, "end": v(-81.83, 177.8) * mm});
            skLineSegment(sketch, "E1128.bottom", {"start": v(-81.83, 2578.07) * mm, "end": v(57.87, 2578.07) * mm});
            skLineSegment(sketch, "E1128.top", {"start": v(-81.83, 2540) * mm, "end": v(57.87, 2540) * mm});
            skLineSegment(sketch, "E1128.left", {"start": v(-81.83, 2578.07) * mm, "end": v(-81.83, 2540) * mm});
            skLineSegment(sketch, "E1128.right", {"start": v(57.87, 2578.07) * mm, "end": v(57.87, 2540) * mm});
            skLineSegment(sketch, "E1129.bottom", {"start": v(-81.83, 565.15) * mm, "end": v(57.87, 565.15) * mm});
            skLineSegment(sketch, "E1129.top", {"start": v(-81.83, 527.05) * mm, "end": v(57.87, 527.05) * mm});
            skLineSegment(sketch, "E1129.left", {"start": v(-81.83, 565.15) * mm, "end": v(-81.83, 527.05) * mm});
            skLineSegment(sketch, "E1129.right", {"start": v(57.87, 565.15) * mm, "end": v(57.87, 527.05) * mm});
            skLineSegment(sketch, "E1130.0.1.0", {"start": v(-81.83, 971.55) * mm, "end": v(57.87, 971.55) * mm});
            skLineSegment(sketch, "E1130.0.1.1", {"start": v(-81.83, 933.45) * mm, "end": v(57.87, 933.45) * mm});
            skLineSegment(sketch, "E1130.0.1.2", {"start": v(-81.83, 971.55) * mm, "end": v(-81.83, 933.45) * mm});
            skLineSegment(sketch, "E1130.0.1.3", {"start": v(57.87, 971.55) * mm, "end": v(57.87, 933.45) * mm});
            skLineSegment(sketch, "E1130.0.2.0", {"start": v(-81.83, 1377.95) * mm, "end": v(57.87, 1377.95) * mm});
            skLineSegment(sketch, "E1130.0.2.1", {"start": v(-81.83, 1339.85) * mm, "end": v(57.87, 1339.85) * mm});
            skLineSegment(sketch, "E1130.0.2.2", {"start": v(-81.83, 1377.95) * mm, "end": v(-81.83, 1339.85) * mm});
            skLineSegment(sketch, "E1130.0.2.3", {"start": v(57.87, 1377.95) * mm, "end": v(57.87, 1339.85) * mm});
            skLineSegment(sketch, "E1130.0.3.0", {"start": v(-81.83, 1784.35) * mm, "end": v(57.87, 1784.35) * mm});
            skLineSegment(sketch, "E1130.0.3.1", {"start": v(-81.83, 1746.25) * mm, "end": v(57.87, 1746.25) * mm});
            skLineSegment(sketch, "E1130.0.3.2", {"start": v(-81.83, 1784.35) * mm, "end": v(-81.83, 1746.25) * mm});
            skLineSegment(sketch, "E1130.0.3.3", {"start": v(57.87, 1784.35) * mm, "end": v(57.87, 1746.25) * mm});
            skLineSegment(sketch, "E1130.0.4.0", {"start": v(-81.83, 2190.75) * mm, "end": v(57.87, 2190.75) * mm});
            skLineSegment(sketch, "E1130.0.4.1", {"start": v(-81.83, 2152.65) * mm, "end": v(57.87, 2152.65) * mm});
            skLineSegment(sketch, "E1130.0.4.2", {"start": v(-81.83, 2190.75) * mm, "end": v(-81.83, 2152.65) * mm});
            skLineSegment(sketch, "E1130.0.4.3", {"start": v(57.87, 2190.75) * mm, "end": v(57.87, 2152.65) * mm});
            skLineSegment(sketch, "E1130.direction1", {"start": v(-81.83, 527.05) * mm, "end": v(-56.43, 527.05) * mm, "construction": true});
            skLineSegment(sketch, "E1130.direction2", {"start": v(-81.83, 527.05) * mm, "end": v(-81.83, 933.45) * mm, "construction": true});
            skLineSegment(sketch, "E1131.bottom", {"start": v(-81.83, 1943.1) * mm, "end": v(-43.73, 1943.1) * mm});
            skLineSegment(sketch, "E1131.top", {"start": v(-81.83, 1803.4) * mm, "end": v(-43.73, 1803.4) * mm});
            skLineSegment(sketch, "E1131.left", {"start": v(-81.83, 1943.1) * mm, "end": v(-81.83, 1803.4) * mm});
            skLineSegment(sketch, "E1131.right", {"start": v(-43.73, 1943.1) * mm, "end": v(-43.73, 1803.4) * mm});
            skSolve(sketch);
        }
        {
            var Q0;
            Q0 = qSketchRegion(id + "F137", true);
            extrude(context, id + "F138", {"entities" : qUnion([Q0]), "operationType" : NewBodyOperationType.ADD, "depth" : 2352.67 * mm});
        }
        {
            var Q0;
            Q0=makeQuery(id+"F138.opExtrude","CAP_FACE",FACE,{"disambiguationData":[OSD([sQuery(id+"F137.wireOp",EDGE,"E1128.bottom"),sQuery(id+"F137.wireOp",EDGE,"E1128.top"),sQuery(id+"F137.wireOp",EDGE,"E1128.left"),sQuery(id+"F137.wireOp",EDGE,"E1128.right")])],"isStart":false});
            var sketch = newSketch(context, id + "F139", { "sketchPlane" : qUnion([Q0]) });
            skLineSegment(sketch, "E1132.bottom", {"start": v(-81.83, 2578.07) * mm, "end": v(57.87, 2578.07) * mm});
            skLineSegment(sketch, "E1132.top", {"start": v(-81.83, 139.73) * mm, "end": v(57.87, 139.73) * mm});
            skLineSegment(sketch, "E1132.left", {"start": v(-81.83, 2578.07) * mm, "end": v(-81.83, 139.73) * mm});
            skLineSegment(sketch, "E1132.right", {"start": v(57.87, 2578.07) * mm, "end": v(57.87, 139.73) * mm});
            skSolve(sketch);
        }
        {
            var Q0;
            Q0 = qSketchRegion(id + "F139", true);
            extrude(context, id + "F140", {"entities" : qUnion([Q0]), "operationType" : NewBodyOperationType.ADD, "depth" : 76.2 * mm});
        }
        {
            var Q0;
            Q0=makeQuery(id+"F1.opExtrude","CAP_FACE",FACE,{"disambiguationData":[OSD([sQuery(id+"F0.wireOp",EDGE,"E15"),sQuery(id+"F0.wireOp",EDGE,"E16"),sQuery(id+"F0.wireOp",EDGE,"E17.1"),sQuery(id+"F0.wireOp",EDGE,"E47"),sQuery(id+"F0.wireOp",EDGE,"E50"),sQuery(id+"F0.wireOp",EDGE,"E52.trimOffspring")])],"isStart":false});
            var sketch = newSketch(context, id + "F141", { "sketchPlane" : qUnion([Q0]) });
            skLineSegment(sketch, "E1133.bottom", {"start": v(-81.83, 2717.8) * mm, "end": v(-43.73, 2717.8) * mm});
            skLineSegment(sketch, "E1133.top", {"start": v(-81.83, 2578.1) * mm, "end": v(-43.73, 2578.1) * mm});
            skLineSegment(sketch, "E1133.left", {"start": v(-81.83, 2717.8) * mm, "end": v(-81.83, 2578.1) * mm});
            skLineSegment(sketch, "E1133.right", {"start": v(-43.73, 2717.8) * mm, "end": v(-43.73, 2578.1) * mm});
            skLineSegment(sketch, "E1134.bottom", {"start": v(-43.7, 2578.1) * mm, "end": v(95.97, 2578.1) * mm});
            skLineSegment(sketch, "E1134.top", {"start": v(-43.7, 2616.2) * mm, "end": v(95.97, 2616.2) * mm});
            skLineSegment(sketch, "E1134.left", {"start": v(-43.7, 2578.1) * mm, "end": v(-43.7, 2616.2) * mm});
            skLineSegment(sketch, "E1134.right", {"start": v(95.97, 2578.1) * mm, "end": v(95.97, 2616.2) * mm});
            skLineSegment(sketch, "E1135.bottom", {"start": v(635, 2717.8) * mm, "end": v(596.9, 2717.8) * mm});
            skLineSegment(sketch, "E1135.top", {"start": v(635, 2578.1) * mm, "end": v(596.9, 2578.1) * mm});
            skLineSegment(sketch, "E1135.left", {"start": v(635, 2717.8) * mm, "end": v(635, 2578.1) * mm});
            skLineSegment(sketch, "E1135.right", {"start": v(596.9, 2717.8) * mm, "end": v(596.9, 2578.1) * mm});
            skLineSegment(sketch, "E1136.bottom", {"start": v(292.82, 2717.8) * mm, "end": v(330.92, 2717.8) * mm});
            skLineSegment(sketch, "E1136.top", {"start": v(292.82, 2578.1) * mm, "end": v(330.92, 2578.1) * mm});
            skLineSegment(sketch, "E1136.left", {"start": v(292.82, 2717.8) * mm, "end": v(292.82, 2578.1) * mm});
            skLineSegment(sketch, "E1136.right", {"start": v(330.92, 2717.8) * mm, "end": v(330.92, 2578.1) * mm});
            skLineSegment(sketch, "E1137", {"start": v(635.03, 2717.77) * mm, "end": v(635.03, 2663.9) * mm});
            skLineSegment(sketch, "E1138", {"start": v(635.03, 2663.9) * mm, "end": v(706.84, 2592.08) * mm});
            skLineSegment(sketch, "E1139", {"start": v(706.84, 2592.08) * mm, "end": v(733.78, 2619.02) * mm});
            skLineSegment(sketch, "E1140", {"start": v(733.78, 2619.02) * mm, "end": v(635.03, 2717.77) * mm});
            skLineSegment(sketch, "E1141", {"start": v(635.03, 2616.2) * mm, "end": v(682.68, 2616.2) * mm});
            skLineSegment(sketch, "E1142", {"start": v(682.68, 2616.2) * mm, "end": v(706.82, 2592.06) * mm});
            skLineSegment(sketch, "E1143", {"start": v(706.82, 2592.06) * mm, "end": v(692.87, 2578.1) * mm});
            skLineSegment(sketch, "E1144", {"start": v(692.87, 2578.1) * mm, "end": v(635.03, 2578.1) * mm});
            skLineSegment(sketch, "E1145", {"start": v(635.03, 2578.1) * mm, "end": v(635.03, 2616.2) * mm});
            skSolve(sketch);
        }
        {
            var Q0;
            Q0 = qSketchRegion(id + "F141", true);
            extrude(context, id + "F142", {"entities" : qUnion([Q0]), "operationType" : NewBodyOperationType.ADD, "depth" : 2352.67 * mm});
        }
        {
            var Q0;
            Q0=makeQuery(id+"F142.opExtrude","CAP_FACE",FACE,{"disambiguationData":[OSD([sQuery(id+"F141.wireOp",EDGE,"E1133.bottom"),sQuery(id+"F141.wireOp",EDGE,"E1133.top"),sQuery(id+"F141.wireOp",EDGE,"E1133.left"),sQuery(id+"F141.wireOp",EDGE,"E1133.right")])],"isStart":false});
            var sketch = newSketch(context, id + "F143", { "sketchPlane" : qUnion([Q0]) });
            skLineSegment(sketch, "E1146", {"start": v(-81.83, 2717.8) * mm, "end": v(-81.83, 2578.1) * mm});
            skLineSegment(sketch, "E1147", {"start": v(-81.83, 2578.1) * mm, "end": v(692.87, 2578.1) * mm});
            skLineSegment(sketch, "E1148", {"start": v(692.87, 2578.1) * mm, "end": v(733.78, 2619.02) * mm});
            skLineSegment(sketch, "E1149", {"start": v(733.78, 2619.02) * mm, "end": v(635, 2717.8) * mm});
            skLineSegment(sketch, "E1150", {"start": v(635, 2717.8) * mm, "end": v(-81.83, 2717.8) * mm});
            skSolve(sketch);
        }
        {
            var Q0;
            Q0 = qSketchRegion(id + "F143", true);
            extrude(context, id + "F144", {"entities" : qUnion([Q0]), "operationType" : NewBodyOperationType.ADD, "depth" : 76.2 * mm});
        }
    });
